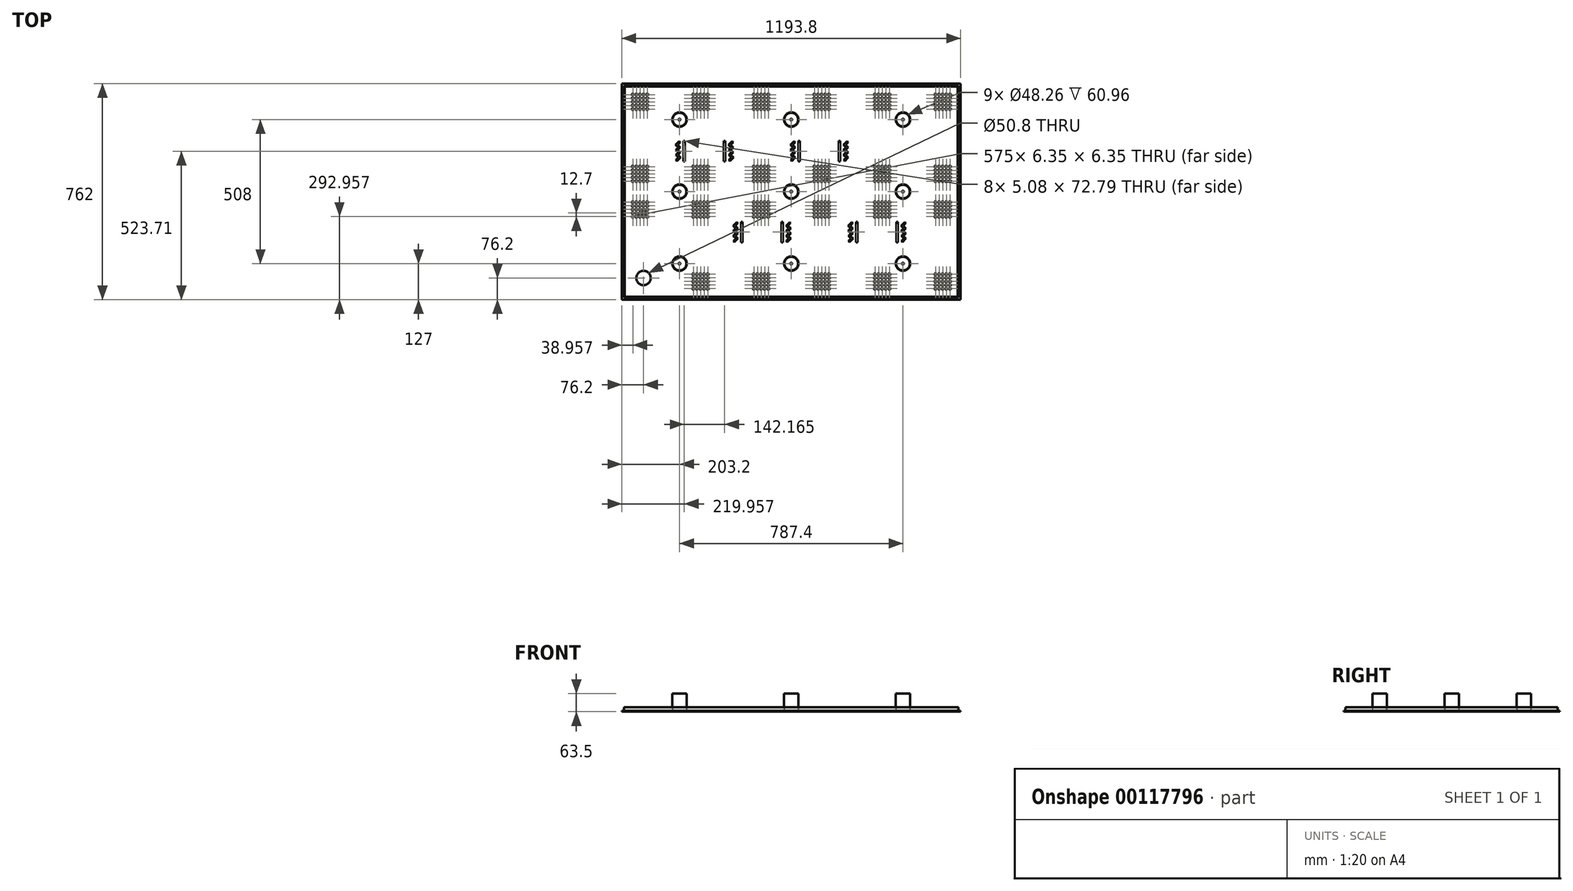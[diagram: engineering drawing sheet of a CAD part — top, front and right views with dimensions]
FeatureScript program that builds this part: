
annotation { "Feature Type Name" : "Feature", "Feature Type Description" : "" }
export const myFeature = defineFeature(function(context is Context, id is Id, definition is map)
    precondition{}
    {
        {
            var Q0;
            Q0=qCreatedBy(makeId("Top.planeOp"),FACE);
            var sketch = newSketch(context, id + "F0", { "sketchPlane" : qUnion([Q0])});
            skLineSegment(sketch, "E0.bottom", {"start": v(596.9, -381) * mm, "end": v(-596.9, -381) * mm});
            skLineSegment(sketch, "E0.top", {"start": v(596.9, 381) * mm, "end": v(-596.9, 381) * mm});
            skLineSegment(sketch, "E0.left", {"start": v(596.9, -381) * mm, "end": v(596.9, 381) * mm});
            skLineSegment(sketch, "E0.right", {"start": v(-596.9, -381) * mm, "end": v(-596.9, 381) * mm});
            skPoint(sketch, "E0.middle", {"position": v(0, 0) * mm});
            skSolve(sketch);
        }
        {
            var Q0;
            Q0=makeQuery(id+"F0.imprint","IMPRINT",FACE,{"disambiguationData":[TD([[makeQuery(id+"F0.imprint","IMPRINT",EDGE,{"derivedFrom":sQuery(id+"F0.wireOp",EDGE,"E0.bottom")}),-1.0]])]});
            extrude(context, id + "F1", {"entities" : qUnion([Q0]), "oppositeDirection" : true, "depth" : 2.54 * mm});
        }
        {
            var Q0;
            Q0=qCreatedBy(makeId("Top.planeOp"),FACE);
            var sketch = newSketch(context, id + "F2", { "sketchPlane" : qUnion([Q0])});
            skLineSegment(sketch, "E1.bottom", {"start": v(596.9, -381) * mm, "end": v(-596.9, -381) * mm});
            skLineSegment(sketch, "E1.top", {"start": v(596.9, 381) * mm, "end": v(-596.9, 381) * mm});
            skLineSegment(sketch, "E1.left", {"start": v(596.9, -381) * mm, "end": v(596.9, 381) * mm});
            skLineSegment(sketch, "E1.right", {"start": v(-596.9, -381) * mm, "end": v(-596.9, 381) * mm});
            skPoint(sketch, "E1.middle", {"position": v(0, 0) * mm});
            skLineSegment(sketch, "E2", {"start": v(-407.26, 165.03) * mm, "end": v(-398.13, 156.2) * mm});
            skLineSegment(sketch, "E3", {"start": v(-398.13, 156.2) * mm, "end": v(-406.97, 147.07) * mm});
            skLineSegment(sketch, "E4", {"start": v(-406.97, 147.07) * mm, "end": v(-397.85, 138.23) * mm});
            skLineSegment(sketch, "E5", {"start": v(-397.85, 138.23) * mm, "end": v(-406.69, 129.11) * mm});
            skLineSegment(sketch, "E6", {"start": v(-406.69, 129.11) * mm, "end": v(-397.56, 120.28) * mm});
            skLineSegment(sketch, "E7", {"start": v(-397.56, 120.28) * mm, "end": v(-406.4, 111.15) * mm});
            skLineSegment(sketch, "E8", {"start": v(-407.26, 165.03) * mm, "end": v(-394.88, 177.8) * mm});
            skLineSegment(sketch, "E9.0", {"start": v(-400.07, 165.14) * mm, "end": v(-391.24, 174.27) * mm});
            skLineSegment(sketch, "E9.1", {"start": v(-400.07, 165.14) * mm, "end": v(-390.95, 156.3) * mm});
            skLineSegment(sketch, "E9.2", {"start": v(-390.95, 156.3) * mm, "end": v(-399.79, 147.19) * mm});
            skLineSegment(sketch, "E9.3", {"start": v(-390.38, 120.4) * mm, "end": v(-402.75, 107.62) * mm});
            skLineSegment(sketch, "E9.4", {"start": v(-399.5, 129.23) * mm, "end": v(-390.38, 120.4) * mm});
            skLineSegment(sketch, "E9.5", {"start": v(-390.67, 138.35) * mm, "end": v(-399.5, 129.23) * mm});
            skLineSegment(sketch, "E9.6", {"start": v(-399.79, 147.19) * mm, "end": v(-390.67, 138.35) * mm});
            skLineSegment(sketch, "E10", {"start": v(-394.88, 177.8) * mm, "end": v(-391.24, 174.27) * mm});
            skLineSegment(sketch, "E11", {"start": v(-406.4, 111.15) * mm, "end": v(-402.75, 107.62) * mm});
            skLineSegment(sketch, "E12.bottom", {"start": v(-382.06, 177.8) * mm, "end": v(-229.66, 177.8) * mm});
            skLineSegment(sketch, "E12.top", {"start": v(-382.06, 107.62) * mm, "end": v(-229.66, 107.62) * mm});
            skLineSegment(sketch, "E12.left", {"start": v(-382.06, 177.8) * mm, "end": v(-382.06, 107.62) * mm});
            skLineSegment(sketch, "E12.right", {"start": v(-229.66, 177.8) * mm, "end": v(-229.66, 107.62) * mm});
            skLineSegment(sketch, "E13", {"start": v(-220.77, 165.03) * mm, "end": v(-211.65, 156.2) * mm});
            skLineSegment(sketch, "E14", {"start": v(-211.65, 156.2) * mm, "end": v(-220.49, 147.07) * mm});
            skLineSegment(sketch, "E15", {"start": v(-220.49, 147.07) * mm, "end": v(-211.36, 138.23) * mm});
            skLineSegment(sketch, "E16", {"start": v(-211.36, 138.23) * mm, "end": v(-220.2, 129.11) * mm});
            skLineSegment(sketch, "E17", {"start": v(-220.2, 129.11) * mm, "end": v(-211.08, 120.28) * mm});
            skLineSegment(sketch, "E18", {"start": v(-211.08, 120.28) * mm, "end": v(-219.92, 111.15) * mm});
            skLineSegment(sketch, "E19", {"start": v(-220.77, 165.03) * mm, "end": v(-208.4, 177.8) * mm});
            skLineSegment(sketch, "E20.0", {"start": v(-213.59, 165.14) * mm, "end": v(-204.75, 174.27) * mm});
            skLineSegment(sketch, "E20.1", {"start": v(-213.59, 165.14) * mm, "end": v(-204.47, 156.3) * mm});
            skLineSegment(sketch, "E20.2", {"start": v(-204.47, 156.3) * mm, "end": v(-213.3, 147.19) * mm});
            skLineSegment(sketch, "E20.3", {"start": v(-203.9, 120.4) * mm, "end": v(-216.27, 107.62) * mm});
            skLineSegment(sketch, "E20.4", {"start": v(-213.02, 129.23) * mm, "end": v(-203.9, 120.4) * mm});
            skLineSegment(sketch, "E20.5", {"start": v(-204.18, 138.35) * mm, "end": v(-213.02, 129.23) * mm});
            skLineSegment(sketch, "E20.6", {"start": v(-213.3, 147.19) * mm, "end": v(-204.18, 138.35) * mm});
            skLineSegment(sketch, "E21", {"start": v(-208.4, 177.8) * mm, "end": v(-204.75, 174.27) * mm});
            skLineSegment(sketch, "E22", {"start": v(-219.92, 111.15) * mm, "end": v(-216.27, 107.62) * mm});
            skLineSegment(sketch, "E23", {"start": v(-204.75, -120.4) * mm, "end": v(-195.63, -129.23) * mm});
            skLineSegment(sketch, "E24", {"start": v(-195.63, -129.23) * mm, "end": v(-204.47, -138.35) * mm});
            skLineSegment(sketch, "E25", {"start": v(-204.47, -138.35) * mm, "end": v(-195.34, -147.19) * mm});
            skLineSegment(sketch, "E26", {"start": v(-195.34, -147.19) * mm, "end": v(-204.18, -156.3) * mm});
            skLineSegment(sketch, "E27", {"start": v(-204.18, -156.3) * mm, "end": v(-195.06, -165.14) * mm});
            skLineSegment(sketch, "E28", {"start": v(-195.06, -165.14) * mm, "end": v(-203.9, -174.27) * mm});
            skLineSegment(sketch, "E29", {"start": v(-204.75, -120.4) * mm, "end": v(-192.38, -107.62) * mm});
            skLineSegment(sketch, "E30.0", {"start": v(-197.57, -120.28) * mm, "end": v(-188.73, -111.15) * mm});
            skLineSegment(sketch, "E30.1", {"start": v(-197.57, -120.28) * mm, "end": v(-188.45, -129.11) * mm});
            skLineSegment(sketch, "E30.2", {"start": v(-188.45, -129.11) * mm, "end": v(-197.28, -138.23) * mm});
            skLineSegment(sketch, "E30.3", {"start": v(-187.88, -165.03) * mm, "end": v(-200.25, -177.8) * mm});
            skLineSegment(sketch, "E30.4", {"start": v(-197, -156.2) * mm, "end": v(-187.88, -165.03) * mm});
            skLineSegment(sketch, "E30.5", {"start": v(-188.16, -147.07) * mm, "end": v(-197, -156.2) * mm});
            skLineSegment(sketch, "E30.6", {"start": v(-197.28, -138.23) * mm, "end": v(-188.16, -147.07) * mm});
            skLineSegment(sketch, "E31", {"start": v(-192.38, -107.62) * mm, "end": v(-188.73, -111.15) * mm});
            skLineSegment(sketch, "E32", {"start": v(-203.9, -174.27) * mm, "end": v(-200.25, -177.8) * mm});
            skLineSegment(sketch, "E33.bottom", {"start": v(-179.56, -107.62) * mm, "end": v(-27.16, -107.62) * mm});
            skLineSegment(sketch, "E33.top", {"start": v(-179.56, -177.8) * mm, "end": v(-27.16, -177.8) * mm});
            skLineSegment(sketch, "E33.left", {"start": v(-179.56, -107.62) * mm, "end": v(-179.56, -177.8) * mm});
            skLineSegment(sketch, "E33.right", {"start": v(-27.16, -107.62) * mm, "end": v(-27.16, -177.8) * mm});
            skLineSegment(sketch, "E34", {"start": v(-18.27, -120.4) * mm, "end": v(-9.14, -129.23) * mm});
            skLineSegment(sketch, "E35", {"start": v(-9.14, -129.23) * mm, "end": v(-17.98, -138.35) * mm});
            skLineSegment(sketch, "E36", {"start": v(-17.98, -138.35) * mm, "end": v(-8.86, -147.19) * mm});
            skLineSegment(sketch, "E37", {"start": v(-8.86, -147.19) * mm, "end": v(-17.7, -156.3) * mm});
            skLineSegment(sketch, "E38", {"start": v(-17.7, -156.3) * mm, "end": v(-8.57, -165.14) * mm});
            skLineSegment(sketch, "E39", {"start": v(-8.57, -165.14) * mm, "end": v(-17.41, -174.27) * mm});
            skLineSegment(sketch, "E40", {"start": v(-18.27, -120.4) * mm, "end": v(-5.9, -107.62) * mm});
            skLineSegment(sketch, "E41.0", {"start": v(-11.08, -120.28) * mm, "end": v(-2.25, -111.15) * mm});
            skLineSegment(sketch, "E41.1", {"start": v(-11.08, -120.28) * mm, "end": v(-1.96, -129.11) * mm});
            skLineSegment(sketch, "E41.2", {"start": v(-1.96, -129.11) * mm, "end": v(-10.8, -138.23) * mm});
            skLineSegment(sketch, "E41.3", {"start": v(-1.4, -165.03) * mm, "end": v(-13.76, -177.8) * mm});
            skLineSegment(sketch, "E41.4", {"start": v(-10.51, -156.2) * mm, "end": v(-1.4, -165.03) * mm});
            skLineSegment(sketch, "E41.5", {"start": v(-1.68, -147.07) * mm, "end": v(-10.51, -156.2) * mm});
            skLineSegment(sketch, "E41.6", {"start": v(-10.8, -138.23) * mm, "end": v(-1.68, -147.07) * mm});
            skLineSegment(sketch, "E42", {"start": v(-5.9, -107.62) * mm, "end": v(-2.25, -111.15) * mm});
            skLineSegment(sketch, "E43", {"start": v(-17.41, -174.27) * mm, "end": v(-13.76, -177.8) * mm});
            skLineSegment(sketch, "E44", {"start": v(-2.53, 165.03) * mm, "end": v(6.6, 156.2) * mm});
            skLineSegment(sketch, "E45", {"start": v(6.6, 156.2) * mm, "end": v(-2.25, 147.07) * mm});
            skLineSegment(sketch, "E46", {"start": v(-2.25, 147.07) * mm, "end": v(6.88, 138.23) * mm});
            skLineSegment(sketch, "E47", {"start": v(6.88, 138.23) * mm, "end": v(-1.96, 129.11) * mm});
            skLineSegment(sketch, "E48", {"start": v(-1.96, 129.11) * mm, "end": v(7.16, 120.28) * mm});
            skLineSegment(sketch, "E49", {"start": v(7.16, 120.28) * mm, "end": v(-1.68, 111.15) * mm});
            skLineSegment(sketch, "E50", {"start": v(-2.53, 165.03) * mm, "end": v(9.84, 177.8) * mm});
            skLineSegment(sketch, "E51.0", {"start": v(4.65, 165.14) * mm, "end": v(13.49, 174.27) * mm});
            skLineSegment(sketch, "E51.1", {"start": v(4.65, 165.14) * mm, "end": v(13.77, 156.3) * mm});
            skLineSegment(sketch, "E51.2", {"start": v(13.77, 156.3) * mm, "end": v(4.94, 147.19) * mm});
            skLineSegment(sketch, "E51.3", {"start": v(14.34, 120.4) * mm, "end": v(1.97, 107.62) * mm});
            skLineSegment(sketch, "E51.4", {"start": v(5.22, 129.23) * mm, "end": v(14.34, 120.4) * mm});
            skLineSegment(sketch, "E51.5", {"start": v(14.06, 138.35) * mm, "end": v(5.22, 129.23) * mm});
            skLineSegment(sketch, "E51.6", {"start": v(4.94, 147.19) * mm, "end": v(14.06, 138.35) * mm});
            skLineSegment(sketch, "E52", {"start": v(9.84, 177.8) * mm, "end": v(13.49, 174.27) * mm});
            skLineSegment(sketch, "E53", {"start": v(-1.68, 111.15) * mm, "end": v(1.97, 107.62) * mm});
            skLineSegment(sketch, "E54.bottom", {"start": v(22.66, 177.8) * mm, "end": v(175.06, 177.8) * mm});
            skLineSegment(sketch, "E54.top", {"start": v(22.66, 107.62) * mm, "end": v(175.06, 107.62) * mm});
            skLineSegment(sketch, "E54.left", {"start": v(22.66, 177.8) * mm, "end": v(22.66, 107.62) * mm});
            skLineSegment(sketch, "E54.right", {"start": v(175.06, 177.8) * mm, "end": v(175.06, 107.62) * mm});
            skLineSegment(sketch, "E55", {"start": v(183.95, 165.03) * mm, "end": v(193.08, 156.2) * mm});
            skLineSegment(sketch, "E56", {"start": v(193.08, 156.2) * mm, "end": v(184.24, 147.07) * mm});
            skLineSegment(sketch, "E57", {"start": v(184.24, 147.07) * mm, "end": v(193.36, 138.23) * mm});
            skLineSegment(sketch, "E58", {"start": v(193.36, 138.23) * mm, "end": v(184.52, 129.11) * mm});
            skLineSegment(sketch, "E59", {"start": v(184.52, 129.11) * mm, "end": v(193.65, 120.28) * mm});
            skLineSegment(sketch, "E60", {"start": v(193.65, 120.28) * mm, "end": v(184.8, 111.15) * mm});
            skLineSegment(sketch, "E61", {"start": v(183.95, 165.03) * mm, "end": v(196.33, 177.8) * mm});
            skLineSegment(sketch, "E62.0", {"start": v(191.14, 165.14) * mm, "end": v(199.97, 174.27) * mm});
            skLineSegment(sketch, "E62.1", {"start": v(191.14, 165.14) * mm, "end": v(200.26, 156.3) * mm});
            skLineSegment(sketch, "E62.2", {"start": v(200.26, 156.3) * mm, "end": v(191.42, 147.19) * mm});
            skLineSegment(sketch, "E62.3", {"start": v(200.83, 120.4) * mm, "end": v(188.46, 107.62) * mm});
            skLineSegment(sketch, "E62.4", {"start": v(191.7, 129.23) * mm, "end": v(200.83, 120.4) * mm});
            skLineSegment(sketch, "E62.5", {"start": v(200.54, 138.35) * mm, "end": v(191.7, 129.23) * mm});
            skLineSegment(sketch, "E62.6", {"start": v(191.42, 147.19) * mm, "end": v(200.54, 138.35) * mm});
            skLineSegment(sketch, "E63", {"start": v(196.33, 177.8) * mm, "end": v(199.97, 174.27) * mm});
            skLineSegment(sketch, "E64", {"start": v(184.8, 111.15) * mm, "end": v(188.46, 107.62) * mm});
            skLineSegment(sketch, "E65", {"start": v(200.83, -120.4) * mm, "end": v(209.95, -129.23) * mm});
            skLineSegment(sketch, "E66", {"start": v(209.95, -129.23) * mm, "end": v(201.11, -138.35) * mm});
            skLineSegment(sketch, "E67", {"start": v(201.11, -138.35) * mm, "end": v(210.24, -147.19) * mm});
            skLineSegment(sketch, "E68", {"start": v(210.24, -147.19) * mm, "end": v(201.4, -156.3) * mm});
            skLineSegment(sketch, "E69", {"start": v(201.4, -156.3) * mm, "end": v(210.52, -165.14) * mm});
            skLineSegment(sketch, "E70", {"start": v(210.52, -165.14) * mm, "end": v(201.68, -174.27) * mm});
            skLineSegment(sketch, "E71", {"start": v(200.83, -120.4) * mm, "end": v(213.2, -107.62) * mm});
            skLineSegment(sketch, "E72.0", {"start": v(208.01, -120.28) * mm, "end": v(216.85, -111.15) * mm});
            skLineSegment(sketch, "E72.1", {"start": v(208.01, -120.28) * mm, "end": v(217.13, -129.11) * mm});
            skLineSegment(sketch, "E72.2", {"start": v(217.13, -129.11) * mm, "end": v(208.3, -138.23) * mm});
            skLineSegment(sketch, "E72.3", {"start": v(217.7, -165.03) * mm, "end": v(205.33, -177.8) * mm});
            skLineSegment(sketch, "E72.4", {"start": v(208.58, -156.2) * mm, "end": v(217.7, -165.03) * mm});
            skLineSegment(sketch, "E72.5", {"start": v(217.42, -147.07) * mm, "end": v(208.58, -156.2) * mm});
            skLineSegment(sketch, "E72.6", {"start": v(208.3, -138.23) * mm, "end": v(217.42, -147.07) * mm});
            skLineSegment(sketch, "E73", {"start": v(213.2, -107.62) * mm, "end": v(216.85, -111.15) * mm});
            skLineSegment(sketch, "E74", {"start": v(201.68, -174.27) * mm, "end": v(205.33, -177.8) * mm});
            skLineSegment(sketch, "E75.bottom", {"start": v(226.02, -107.62) * mm, "end": v(378.42, -107.62) * mm});
            skLineSegment(sketch, "E75.top", {"start": v(226.02, -177.8) * mm, "end": v(378.42, -177.8) * mm});
            skLineSegment(sketch, "E75.left", {"start": v(226.02, -107.62) * mm, "end": v(226.02, -177.8) * mm});
            skLineSegment(sketch, "E75.right", {"start": v(378.42, -107.62) * mm, "end": v(378.42, -177.8) * mm});
            skLineSegment(sketch, "E76", {"start": v(387.31, -120.4) * mm, "end": v(396.44, -129.23) * mm});
            skLineSegment(sketch, "E77", {"start": v(396.44, -129.23) * mm, "end": v(387.6, -138.35) * mm});
            skLineSegment(sketch, "E78", {"start": v(387.6, -138.35) * mm, "end": v(396.72, -147.19) * mm});
            skLineSegment(sketch, "E79", {"start": v(396.72, -147.19) * mm, "end": v(387.88, -156.3) * mm});
            skLineSegment(sketch, "E80", {"start": v(387.88, -156.3) * mm, "end": v(397, -165.14) * mm});
            skLineSegment(sketch, "E81", {"start": v(397, -165.14) * mm, "end": v(388.17, -174.27) * mm});
            skLineSegment(sketch, "E82", {"start": v(387.31, -120.4) * mm, "end": v(399.69, -107.62) * mm});
            skLineSegment(sketch, "E83.0", {"start": v(394.5, -120.28) * mm, "end": v(403.33, -111.15) * mm});
            skLineSegment(sketch, "E83.1", {"start": v(394.5, -120.28) * mm, "end": v(403.62, -129.11) * mm});
            skLineSegment(sketch, "E83.2", {"start": v(403.62, -129.11) * mm, "end": v(394.78, -138.23) * mm});
            skLineSegment(sketch, "E83.3", {"start": v(404.19, -165.03) * mm, "end": v(391.82, -177.8) * mm});
            skLineSegment(sketch, "E83.4", {"start": v(395.07, -156.2) * mm, "end": v(404.19, -165.03) * mm});
            skLineSegment(sketch, "E83.5", {"start": v(403.9, -147.07) * mm, "end": v(395.07, -156.2) * mm});
            skLineSegment(sketch, "E83.6", {"start": v(394.78, -138.23) * mm, "end": v(403.9, -147.07) * mm});
            skLineSegment(sketch, "E84", {"start": v(399.69, -107.62) * mm, "end": v(403.33, -111.15) * mm});
            skLineSegment(sketch, "E85", {"start": v(388.17, -174.27) * mm, "end": v(391.82, -177.8) * mm});
            skSolve(sketch);
        }
        {
            var Q0;
            Q0=makeQuery(id+"F2.imprint","IMPRINT",FACE,{"disambiguationData":[TD([[makeQuery(id+"F2.imprint","IMPRINT",EDGE,{"derivedFrom":sQuery(id+"F2.wireOp",EDGE,"E2")}),1.0]])]});
            var Q1;
            Q1=makeQuery(id+"F2.imprint","IMPRINT",FACE,{"disambiguationData":[TD([[makeQuery(id+"F2.imprint","IMPRINT",EDGE,{"derivedFrom":sQuery(id+"F2.wireOp",EDGE,"E13")}),1.0]])]});
            var Q2;
            Q2=makeQuery(id+"F2.imprint","IMPRINT",FACE,{"disambiguationData":[TD([[makeQuery(id+"F2.imprint","IMPRINT",EDGE,{"derivedFrom":sQuery(id+"F2.wireOp",EDGE,"E23")}),1.0]])]});
            var Q3;
            Q3=makeQuery(id+"F2.imprint","IMPRINT",FACE,{"disambiguationData":[TD([[makeQuery(id+"F2.imprint","IMPRINT",EDGE,{"derivedFrom":sQuery(id+"F2.wireOp",EDGE,"E34")}),1.0]])]});
            var Q4;
            Q4=makeQuery(id+"F2.imprint","IMPRINT",FACE,{"disambiguationData":[TD([[makeQuery(id+"F2.imprint","IMPRINT",EDGE,{"derivedFrom":sQuery(id+"F2.wireOp",EDGE,"E76")}),1.0]])]});
            var Q5;
            Q5=makeQuery(id+"F2.imprint","IMPRINT",FACE,{"disambiguationData":[TD([[makeQuery(id+"F2.imprint","IMPRINT",EDGE,{"derivedFrom":sQuery(id+"F2.wireOp",EDGE,"E65")}),1.0]])]});
            var Q6;
            Q6=makeQuery(id+"F2.imprint","IMPRINT",FACE,{"disambiguationData":[TD([[makeQuery(id+"F2.imprint","IMPRINT",EDGE,{"derivedFrom":sQuery(id+"F2.wireOp",EDGE,"E44")}),1.0]])]});
            var Q7;
            Q7=makeQuery(id+"F2.imprint","IMPRINT",FACE,{"disambiguationData":[TD([[makeQuery(id+"F2.imprint","IMPRINT",EDGE,{"derivedFrom":sQuery(id+"F2.wireOp",EDGE,"E55")}),1.0]])]});
            extrude(context, id + "F3", {"entities" : qUnion([Q0, Q1, Q2, Q3, Q4, Q5, Q6, Q7]), "operationType" : NewBodyOperationType.REMOVE, "endBound" : BoundingType.THROUGH_ALL, "oppositeDirection" : true, "depth" : 25.4 * mm, "hasDraft" : true, "draftAngle" : 20 * degree});
        }
        {
            var Q0;
            Q0=makeQuery(id+"F1.opExtrude","CAP_FACE",FACE,{"disambiguationData":[OSD([sQuery(id+"F0.wireOp",EDGE,"E0.bottom"),sQuery(id+"F0.wireOp",EDGE,"E0.top"),sQuery(id+"F0.wireOp",EDGE,"E0.left"),sQuery(id+"F0.wireOp",EDGE,"E0.right")])],"isStart":false});
            var sketch = newSketch(context, id + "F4", { "sketchPlane" : qUnion([Q0])});
            skLineSegment(sketch, "E86.left", {"start": v(-176.7, 179.1) * mm, "end": v(-176.7, 106.31) * mm});
            skLineSegment(sketch, "E86.right", {"start": v(-29.73, 179.1) * mm, "end": v(-29.73, 106.31) * mm});
            skLineSegment(sketch, "E87.left", {"start": v(228.6, 179.1) * mm, "end": v(228.6, 106.31) * mm});
            skLineSegment(sketch, "E87.right", {"start": v(375.85, 179.1) * mm, "end": v(375.85, 106.31) * mm});
            skLineSegment(sketch, "E88.left", {"start": v(-379.48, -106.31) * mm, "end": v(-379.48, -179.1) * mm});
            skLineSegment(sketch, "E88.right", {"start": v(-232.24, -106.31) * mm, "end": v(-232.24, -179.1) * mm});
            skLineSegment(sketch, "E89.left", {"start": v(25.24, -106.31) * mm, "end": v(25.24, -179.1) * mm});
            skLineSegment(sketch, "E89.right", {"start": v(172.49, -106.31) * mm, "end": v(172.49, -179.1) * mm});
            skLineSegment(sketch, "E90", {"start": v(-379.48, -106.31) * mm, "end": v(-374.4, -106.31) * mm});
            skLineSegment(sketch, "E91", {"start": v(-374.4, -106.31) * mm, "end": v(-374.4, -179.1) * mm});
            skLineSegment(sketch, "E92", {"start": v(-374.4, -179.1) * mm, "end": v(-379.48, -179.1) * mm});
            skLineSegment(sketch, "E93", {"start": v(-232.24, -106.31) * mm, "end": v(-237.32, -106.31) * mm});
            skLineSegment(sketch, "E94", {"start": v(-237.32, -106.31) * mm, "end": v(-237.32, -179.1) * mm});
            skLineSegment(sketch, "E95", {"start": v(-237.32, -179.1) * mm, "end": v(-232.24, -179.1) * mm});
            skLineSegment(sketch, "E96", {"start": v(-176.7, 179.1) * mm, "end": v(-171.61, 179.1) * mm});
            skLineSegment(sketch, "E97", {"start": v(-171.61, 179.1) * mm, "end": v(-171.61, 106.31) * mm});
            skLineSegment(sketch, "E98", {"start": v(-171.61, 106.31) * mm, "end": v(-176.7, 106.31) * mm});
            skLineSegment(sketch, "E99", {"start": v(-29.73, 179.1) * mm, "end": v(-34.81, 179.1) * mm});
            skLineSegment(sketch, "E100", {"start": v(-34.81, 179.1) * mm, "end": v(-34.81, 106.31) * mm});
            skLineSegment(sketch, "E101", {"start": v(-34.81, 106.31) * mm, "end": v(-29.73, 106.31) * mm});
            skLineSegment(sketch, "E102", {"start": v(25.24, -106.31) * mm, "end": v(30.32, -106.31) * mm});
            skLineSegment(sketch, "E103", {"start": v(30.32, -106.31) * mm, "end": v(30.32, -179.1) * mm});
            skLineSegment(sketch, "E104", {"start": v(30.32, -179.1) * mm, "end": v(25.24, -179.1) * mm});
            skLineSegment(sketch, "E105", {"start": v(172.49, -106.31) * mm, "end": v(167.4, -106.31) * mm});
            skLineSegment(sketch, "E106", {"start": v(167.4, -106.31) * mm, "end": v(167.4, -179.1) * mm});
            skLineSegment(sketch, "E107", {"start": v(167.4, -179.1) * mm, "end": v(172.49, -179.1) * mm});
            skLineSegment(sketch, "E108", {"start": v(228.6, 179.1) * mm, "end": v(233.68, 179.1) * mm});
            skLineSegment(sketch, "E109", {"start": v(233.68, 179.1) * mm, "end": v(233.68, 106.31) * mm});
            skLineSegment(sketch, "E110", {"start": v(233.68, 106.31) * mm, "end": v(228.6, 106.31) * mm});
            skLineSegment(sketch, "E111", {"start": v(375.85, 179.1) * mm, "end": v(370.77, 179.1) * mm});
            skLineSegment(sketch, "E112", {"start": v(370.77, 179.1) * mm, "end": v(370.77, 106.31) * mm});
            skLineSegment(sketch, "E113", {"start": v(370.77, 106.31) * mm, "end": v(375.85, 106.31) * mm});
            skSolve(sketch);
        }
        {
            var Q0;
            Q0=makeQuery(id+"F1.opExtrude","CAP_FACE",FACE,{"disambiguationData":[OSD([sQuery(id+"F0.wireOp",EDGE,"E0.bottom"),sQuery(id+"F0.wireOp",EDGE,"E0.top"),sQuery(id+"F0.wireOp",EDGE,"E0.left"),sQuery(id+"F0.wireOp",EDGE,"E0.right")])],"isStart":true});
            var sketch = newSketch(context, id + "F5", { "sketchPlane" : qUnion([Q0])});
            skLineSegment(sketch, "E114.bottom", {"start": v(589.28, -373.38) * mm, "end": v(-589.28, -373.38) * mm});
            skLineSegment(sketch, "E114.top", {"start": v(589.28, 373.38) * mm, "end": v(-589.28, 373.38) * mm});
            skLineSegment(sketch, "E114.left", {"start": v(589.28, -373.38) * mm, "end": v(589.28, 373.38) * mm});
            skLineSegment(sketch, "E114.right", {"start": v(-589.28, -373.38) * mm, "end": v(-589.28, 373.38) * mm});
            skPoint(sketch, "E114.middle", {"position": v(0, 0) * mm});
            skLineSegment(sketch, "E115.0", {"start": v(586.74, 370.84) * mm, "end": v(-586.74, 370.84) * mm});
            skLineSegment(sketch, "E115.1", {"start": v(586.74, -370.84) * mm, "end": v(586.74, 370.84) * mm});
            skLineSegment(sketch, "E115.2", {"start": v(586.74, -370.84) * mm, "end": v(-586.74, -370.84) * mm});
            skLineSegment(sketch, "E115.3", {"start": v(-586.74, -370.84) * mm, "end": v(-586.74, 370.84) * mm});
            skSolve(sketch);
        }
        {
            var Q0;
            Q0=makeQuery(id+"F5.imprint","IMPRINT",FACE,{"disambiguationData":[TD([[makeQuery(id+"F5.imprint","IMPRINT",EDGE,{"derivedFrom":sQuery(id+"F5.wireOp",EDGE,"E114.bottom")}),-1.0]])]});
            extrude(context, id + "F6", {"entities" : qUnion([Q0]), "operationType" : NewBodyOperationType.ADD, "depth" : 12.7 * mm, "hasDraft" : true, "draftAngle" : 1 * degree});
        }
        {
            var Q0;
            Q0=makeQuery(id+"F6.boolean.opBoolean","SPLIT",FACE,{"disambiguationData":[TD([makeQuery(id+"F3.boolean.opBoolean","COPY",FACE,{"derivedFrom":makeQuery(id+"F3.opExtrude","SWEPT_FACE",FACE,{"disambiguationData":[OSD([sQuery(id+"F2.wireOp",EDGE,"E2")])]})})])],"derivedFrom":makeQuery(id+"F1.opExtrude","CAP_FACE",FACE,{"disambiguationData":[OSD([sQuery(id+"F0.wireOp",EDGE,"E0.bottom"),sQuery(id+"F0.wireOp",EDGE,"E0.top"),sQuery(id+"F0.wireOp",EDGE,"E0.left"),sQuery(id+"F0.wireOp",EDGE,"E0.right")])],"isStart":true})});
            var sketch = newSketch(context, id + "F7", { "sketchPlane" : qUnion([Q0])});
            skCircle(sketch, "E116", {"center": v(-393.7, 254) * mm, "radius": 25.4 * mm});
            skCircle(sketch, "E117", {"center": v(-393.7, 0) * mm, "radius": 25.4 * mm});
            skCircle(sketch, "E118", {"center": v(-393.7, -254) * mm, "radius": 25.4 * mm});
            skCircle(sketch, "E119", {"center": v(0, 254) * mm, "radius": 25.4 * mm});
            skCircle(sketch, "E120", {"center": v(393.7, 254) * mm, "radius": 25.4 * mm});
            skCircle(sketch, "E121", {"center": v(0, 0) * mm, "radius": 25.4 * mm});
            skCircle(sketch, "E122", {"center": v(0, -254) * mm, "radius": 25.4 * mm});
            skCircle(sketch, "E123", {"center": v(393.7, 0) * mm, "radius": 25.4 * mm});
            skCircle(sketch, "E124", {"center": v(393.7, -254) * mm, "radius": 25.4 * mm});
            skCircle(sketch, "E125", {"center": v(-393.7, 254) * mm, "radius": 24.13 * mm});
            skCircle(sketch, "E126", {"center": v(0, 254) * mm, "radius": 24.13 * mm});
            skCircle(sketch, "E127", {"center": v(393.7, 254) * mm, "radius": 24.13 * mm});
            skCircle(sketch, "E128", {"center": v(-393.7, 0) * mm, "radius": 24.13 * mm});
            skCircle(sketch, "E129", {"center": v(0, 0) * mm, "radius": 24.13 * mm});
            skCircle(sketch, "E130", {"center": v(393.7, 0) * mm, "radius": 24.13 * mm});
            skCircle(sketch, "E131", {"center": v(0, -254) * mm, "radius": 24.13 * mm});
            skCircle(sketch, "E132", {"center": v(393.7, -254) * mm, "radius": 24.13 * mm});
            skCircle(sketch, "E133", {"center": v(-393.7, -254) * mm, "radius": 24.13 * mm});
            skCircle(sketch, "E134", {"center": v(-393.7, 254) * mm, "radius": 3.18 * mm});
            skCircle(sketch, "E135", {"center": v(0, 254) * mm, "radius": 3.18 * mm});
            skCircle(sketch, "E136", {"center": v(393.7, 254) * mm, "radius": 3.18 * mm});
            skCircle(sketch, "E137", {"center": v(-393.7, 0) * mm, "radius": 3.18 * mm});
            skCircle(sketch, "E138", {"center": v(0, 0) * mm, "radius": 3.18 * mm});
            skCircle(sketch, "E139", {"center": v(393.7, 0) * mm, "radius": 3.18 * mm});
            skCircle(sketch, "E140", {"center": v(393.7, -254) * mm, "radius": 3.18 * mm});
            skCircle(sketch, "E141", {"center": v(0, -254) * mm, "radius": 3.18 * mm});
            skCircle(sketch, "E142", {"center": v(-393.7, -254) * mm, "radius": 3.18 * mm});
            skSolve(sketch);
        }
        {
            var Q0;
            Q0=makeQuery(id+"F7.imprint","IMPRINT",FACE,{"disambiguationData":[TD([[makeQuery(id+"F7.imprint","IMPRINT",EDGE,{"derivedFrom":sQuery(id+"F7.wireOp",EDGE,"E116")}),1.0]])]});
            var Q1;
            Q1=makeQuery(id+"F7.imprint","IMPRINT",FACE,{"disambiguationData":[TD([[makeQuery(id+"F7.imprint","IMPRINT",EDGE,{"derivedFrom":sQuery(id+"F7.wireOp",EDGE,"E119")}),1.0]])]});
            var Q2;
            Q2=makeQuery(id+"F7.imprint","IMPRINT",FACE,{"disambiguationData":[TD([[makeQuery(id+"F7.imprint","IMPRINT",EDGE,{"derivedFrom":sQuery(id+"F7.wireOp",EDGE,"E120")}),1.0]])]});
            var Q3;
            Q3=makeQuery(id+"F7.imprint","IMPRINT",FACE,{"disambiguationData":[TD([[makeQuery(id+"F7.imprint","IMPRINT",EDGE,{"derivedFrom":sQuery(id+"F7.wireOp",EDGE,"E123")}),1.0]])]});
            var Q4;
            Q4=makeQuery(id+"F7.imprint","IMPRINT",FACE,{"disambiguationData":[TD([[makeQuery(id+"F7.imprint","IMPRINT",EDGE,{"derivedFrom":sQuery(id+"F7.wireOp",EDGE,"E121")}),1.0]])]});
            var Q5;
            Q5=makeQuery(id+"F7.imprint","IMPRINT",FACE,{"disambiguationData":[TD([[makeQuery(id+"F7.imprint","IMPRINT",EDGE,{"derivedFrom":sQuery(id+"F7.wireOp",EDGE,"E117")}),1.0]])]});
            var Q6;
            Q6=makeQuery(id+"F7.imprint","IMPRINT",FACE,{"disambiguationData":[TD([[makeQuery(id+"F7.imprint","IMPRINT",EDGE,{"derivedFrom":sQuery(id+"F7.wireOp",EDGE,"E118")}),1.0]])]});
            var Q7;
            Q7=makeQuery(id+"F7.imprint","IMPRINT",FACE,{"disambiguationData":[TD([[makeQuery(id+"F7.imprint","IMPRINT",EDGE,{"derivedFrom":sQuery(id+"F7.wireOp",EDGE,"E122")}),1.0]])]});
            var Q8;
            Q8=makeQuery(id+"F7.imprint","IMPRINT",FACE,{"disambiguationData":[TD([[makeQuery(id+"F7.imprint","IMPRINT",EDGE,{"derivedFrom":sQuery(id+"F7.wireOp",EDGE,"E124")}),1.0]])]});
            extrude(context, id + "F8", {"entities" : qUnion([Q0, Q1, Q2, Q3, Q4, Q5, Q6, Q7, Q8]), "operationType" : NewBodyOperationType.ADD, "depth" : 60.96 * mm});
        }
        {
            var Q0;
            Q0=makeQuery(id+"F1.opExtrude","CAP_FACE",FACE,{"disambiguationData":[OSD([sQuery(id+"F0.wireOp",EDGE,"E0.bottom"),sQuery(id+"F0.wireOp",EDGE,"E0.top"),sQuery(id+"F0.wireOp",EDGE,"E0.left"),sQuery(id+"F0.wireOp",EDGE,"E0.right")])],"isStart":false});
            var sketch = newSketch(context, id + "F9", { "sketchPlane" : qUnion([Q0])});
            skCircle(sketch, "E143", {"center": v(-520.7, 304.8) * mm, "radius": 25.4 * mm});
            skSolve(sketch);
        }
        {
            var Q0;
            Q0=makeQuery(id+"F9.imprint","IMPRINT",FACE,{"disambiguationData":[TD([[makeQuery(id+"F9.imprint","IMPRINT",EDGE,{"derivedFrom":sQuery(id+"F9.wireOp",EDGE,"E143")}),1.0]])]});
            extrude(context, id + "F10", {"entities" : qUnion([Q0]), "operationType" : NewBodyOperationType.REMOVE, "endBound" : BoundingType.THROUGH_ALL, "oppositeDirection" : true, "depth" : 25.4 * mm});
        }
        {
            var Q0;
            Q0=makeQuery(id+"F7.imprint","IMPRINT",FACE,{"disambiguationData":[TD([[makeQuery(id+"F7.imprint","IMPRINT",EDGE,{"derivedFrom":sQuery(id+"F7.wireOp",EDGE,"E134")}),1.0]])]});
            var Q1;
            Q1=makeQuery(id+"F7.imprint","IMPRINT",FACE,{"disambiguationData":[TD([[makeQuery(id+"F7.imprint","IMPRINT",EDGE,{"derivedFrom":sQuery(id+"F7.wireOp",EDGE,"E135")}),1.0]])]});
            var Q2;
            Q2=makeQuery(id+"F7.imprint","IMPRINT",FACE,{"disambiguationData":[TD([[makeQuery(id+"F7.imprint","IMPRINT",EDGE,{"derivedFrom":sQuery(id+"F7.wireOp",EDGE,"E136")}),1.0]])]});
            var Q3;
            Q3=makeQuery(id+"F7.imprint","IMPRINT",FACE,{"disambiguationData":[TD([[makeQuery(id+"F7.imprint","IMPRINT",EDGE,{"derivedFrom":sQuery(id+"F7.wireOp",EDGE,"E139")}),1.0]])]});
            var Q4;
            Q4=makeQuery(id+"F7.imprint","IMPRINT",FACE,{"disambiguationData":[TD([[makeQuery(id+"F7.imprint","IMPRINT",EDGE,{"derivedFrom":sQuery(id+"F7.wireOp",EDGE,"E138")}),1.0]])]});
            var Q5;
            Q5=makeQuery(id+"F7.imprint","IMPRINT",FACE,{"disambiguationData":[TD([[makeQuery(id+"F7.imprint","IMPRINT",EDGE,{"derivedFrom":sQuery(id+"F7.wireOp",EDGE,"E137")}),1.0]])]});
            var Q6;
            Q6=makeQuery(id+"F7.imprint","IMPRINT",FACE,{"disambiguationData":[TD([[makeQuery(id+"F7.imprint","IMPRINT",EDGE,{"derivedFrom":sQuery(id+"F7.wireOp",EDGE,"E142")}),1.0]])]});
            var Q7;
            Q7=makeQuery(id+"F7.imprint","IMPRINT",FACE,{"disambiguationData":[TD([[makeQuery(id+"F7.imprint","IMPRINT",EDGE,{"derivedFrom":sQuery(id+"F7.wireOp",EDGE,"E141")}),1.0]])]});
            var Q8;
            Q8=makeQuery(id+"F7.imprint","IMPRINT",FACE,{"disambiguationData":[TD([[makeQuery(id+"F7.imprint","IMPRINT",EDGE,{"derivedFrom":sQuery(id+"F7.wireOp",EDGE,"E140")}),1.0]])]});
            extrude(context, id + "F11", {"entities" : qUnion([Q0, Q1, Q2, Q3, Q4, Q5, Q6, Q7, Q8]), "operationType" : NewBodyOperationType.REMOVE, "endBound" : BoundingType.THROUGH_ALL, "oppositeDirection" : true, "depth" : 25.4 * mm, "hasDraft" : true, "draftAngle" : 3 * degree});
        }
        {
            var Q0;
            {var subQ75=makeQuery(id+"F3.boolean.opBoolean","COPY",FACE,{"derivedFrom":makeQuery(id+"F3.opExtrude","SWEPT_FACE",FACE,{"disambiguationData":[OSD([sQuery(id+"F2.wireOp",EDGE,"E2")])]})});Q0=makeQuery(id+"F8.boolean.opBoolean","SPLIT",FACE,{"disambiguationData":[TD([subQ75])],"derivedFrom":makeQuery(id+"F6.boolean.opBoolean","SPLIT",FACE,{"disambiguationData":[TD([subQ75])],"derivedFrom":makeQuery(id+"F1.opExtrude","CAP_FACE",FACE,{"disambiguationData":[OSD([sQuery(id+"F0.wireOp",EDGE,"E0.bottom"),sQuery(id+"F0.wireOp",EDGE,"E0.top"),sQuery(id+"F0.wireOp",EDGE,"E0.left"),sQuery(id+"F0.wireOp",EDGE,"E0.right")])],"isStart":true})})});}
            var sketch = newSketch(context, id + "F12", { "sketchPlane" : qUnion([Q0])});
            skLineSegment(sketch, "E144.bottom", {"start": v(-561.12, 345.22) * mm, "end": v(-554.77, 345.22) * mm});
            skLineSegment(sketch, "E144.top", {"start": v(-561.12, 338.87) * mm, "end": v(-554.77, 338.87) * mm});
            skLineSegment(sketch, "E144.left", {"start": v(-561.12, 345.22) * mm, "end": v(-561.12, 338.87) * mm});
            skLineSegment(sketch, "E144.right", {"start": v(-554.77, 345.22) * mm, "end": v(-554.77, 338.87) * mm});
            skLineSegment(sketch, "E145.0.1.0", {"start": v(-554.77, 332.52) * mm, "end": v(-554.77, 326.17) * mm});
            skLineSegment(sketch, "E145.0.1.1", {"start": v(-561.12, 326.17) * mm, "end": v(-554.77, 326.17) * mm});
            skLineSegment(sketch, "E145.0.1.2", {"start": v(-561.12, 332.52) * mm, "end": v(-561.12, 326.17) * mm});
            skLineSegment(sketch, "E145.0.1.3", {"start": v(-561.12, 332.52) * mm, "end": v(-554.77, 332.52) * mm});
            skLineSegment(sketch, "E145.0.2.0", {"start": v(-554.77, 319.82) * mm, "end": v(-554.77, 313.47) * mm});
            skLineSegment(sketch, "E145.0.2.1", {"start": v(-561.12, 313.47) * mm, "end": v(-554.77, 313.47) * mm});
            skLineSegment(sketch, "E145.0.2.2", {"start": v(-561.12, 319.82) * mm, "end": v(-561.12, 313.47) * mm});
            skLineSegment(sketch, "E145.0.2.3", {"start": v(-561.12, 319.82) * mm, "end": v(-554.77, 319.82) * mm});
            skLineSegment(sketch, "E145.0.3.0", {"start": v(-554.77, 307.12) * mm, "end": v(-554.77, 300.77) * mm});
            skLineSegment(sketch, "E145.0.3.1", {"start": v(-561.12, 300.77) * mm, "end": v(-554.77, 300.77) * mm});
            skLineSegment(sketch, "E145.0.3.2", {"start": v(-561.12, 307.12) * mm, "end": v(-561.12, 300.77) * mm});
            skLineSegment(sketch, "E145.0.3.3", {"start": v(-561.12, 307.12) * mm, "end": v(-554.77, 307.12) * mm});
            skLineSegment(sketch, "E145.0.4.0", {"start": v(-554.77, 294.42) * mm, "end": v(-554.77, 288.07) * mm});
            skLineSegment(sketch, "E145.0.4.1", {"start": v(-561.12, 288.07) * mm, "end": v(-554.77, 288.07) * mm});
            skLineSegment(sketch, "E145.0.4.2", {"start": v(-561.12, 294.42) * mm, "end": v(-561.12, 288.07) * mm});
            skLineSegment(sketch, "E145.0.4.3", {"start": v(-561.12, 294.42) * mm, "end": v(-554.77, 294.42) * mm});
            skLineSegment(sketch, "E145.1.0.0", {"start": v(-542.07, 345.22) * mm, "end": v(-542.07, 338.87) * mm});
            skLineSegment(sketch, "E145.1.0.1", {"start": v(-548.42, 338.87) * mm, "end": v(-542.07, 338.87) * mm});
            skLineSegment(sketch, "E145.1.0.2", {"start": v(-548.42, 345.22) * mm, "end": v(-548.42, 338.87) * mm});
            skLineSegment(sketch, "E145.1.0.3", {"start": v(-548.42, 345.22) * mm, "end": v(-542.07, 345.22) * mm});
            skLineSegment(sketch, "E145.1.1.0", {"start": v(-542.07, 332.52) * mm, "end": v(-542.07, 326.17) * mm});
            skLineSegment(sketch, "E145.1.1.1", {"start": v(-548.42, 326.17) * mm, "end": v(-542.07, 326.17) * mm});
            skLineSegment(sketch, "E145.1.1.2", {"start": v(-548.42, 332.52) * mm, "end": v(-548.42, 326.17) * mm});
            skLineSegment(sketch, "E145.1.1.3", {"start": v(-548.42, 332.52) * mm, "end": v(-542.07, 332.52) * mm});
            skLineSegment(sketch, "E145.1.2.0", {"start": v(-542.07, 319.82) * mm, "end": v(-542.07, 313.47) * mm});
            skLineSegment(sketch, "E145.1.2.1", {"start": v(-548.42, 313.47) * mm, "end": v(-542.07, 313.47) * mm});
            skLineSegment(sketch, "E145.1.2.2", {"start": v(-548.42, 319.82) * mm, "end": v(-548.42, 313.47) * mm});
            skLineSegment(sketch, "E145.1.2.3", {"start": v(-548.42, 319.82) * mm, "end": v(-542.07, 319.82) * mm});
            skLineSegment(sketch, "E145.1.3.0", {"start": v(-542.07, 307.12) * mm, "end": v(-542.07, 300.77) * mm});
            skLineSegment(sketch, "E145.1.3.1", {"start": v(-548.42, 300.77) * mm, "end": v(-542.07, 300.77) * mm});
            skLineSegment(sketch, "E145.1.3.2", {"start": v(-548.42, 307.12) * mm, "end": v(-548.42, 300.77) * mm});
            skLineSegment(sketch, "E145.1.3.3", {"start": v(-548.42, 307.12) * mm, "end": v(-542.07, 307.12) * mm});
            skLineSegment(sketch, "E145.1.4.0", {"start": v(-542.07, 294.42) * mm, "end": v(-542.07, 288.07) * mm});
            skLineSegment(sketch, "E145.1.4.1", {"start": v(-548.42, 288.07) * mm, "end": v(-542.07, 288.07) * mm});
            skLineSegment(sketch, "E145.1.4.2", {"start": v(-548.42, 294.42) * mm, "end": v(-548.42, 288.07) * mm});
            skLineSegment(sketch, "E145.1.4.3", {"start": v(-548.42, 294.42) * mm, "end": v(-542.07, 294.42) * mm});
            skLineSegment(sketch, "E145.2.0.0", {"start": v(-529.37, 345.22) * mm, "end": v(-529.37, 338.87) * mm});
            skLineSegment(sketch, "E145.2.0.1", {"start": v(-535.72, 338.87) * mm, "end": v(-529.37, 338.87) * mm});
            skLineSegment(sketch, "E145.2.0.2", {"start": v(-535.72, 345.22) * mm, "end": v(-535.72, 338.87) * mm});
            skLineSegment(sketch, "E145.2.0.3", {"start": v(-535.72, 345.22) * mm, "end": v(-529.37, 345.22) * mm});
            skLineSegment(sketch, "E145.2.1.0", {"start": v(-529.37, 332.52) * mm, "end": v(-529.37, 326.17) * mm});
            skLineSegment(sketch, "E145.2.1.1", {"start": v(-535.72, 326.17) * mm, "end": v(-529.37, 326.17) * mm});
            skLineSegment(sketch, "E145.2.1.2", {"start": v(-535.72, 332.52) * mm, "end": v(-535.72, 326.17) * mm});
            skLineSegment(sketch, "E145.2.1.3", {"start": v(-535.72, 332.52) * mm, "end": v(-529.37, 332.52) * mm});
            skLineSegment(sketch, "E145.2.2.0", {"start": v(-529.37, 319.82) * mm, "end": v(-529.37, 313.47) * mm});
            skLineSegment(sketch, "E145.2.2.1", {"start": v(-535.72, 313.47) * mm, "end": v(-529.37, 313.47) * mm});
            skLineSegment(sketch, "E145.2.2.2", {"start": v(-535.72, 319.82) * mm, "end": v(-535.72, 313.47) * mm});
            skLineSegment(sketch, "E145.2.2.3", {"start": v(-535.72, 319.82) * mm, "end": v(-529.37, 319.82) * mm});
            skLineSegment(sketch, "E145.2.3.0", {"start": v(-529.37, 307.12) * mm, "end": v(-529.37, 300.77) * mm});
            skLineSegment(sketch, "E145.2.3.1", {"start": v(-535.72, 300.77) * mm, "end": v(-529.37, 300.77) * mm});
            skLineSegment(sketch, "E145.2.3.2", {"start": v(-535.72, 307.12) * mm, "end": v(-535.72, 300.77) * mm});
            skLineSegment(sketch, "E145.2.3.3", {"start": v(-535.72, 307.12) * mm, "end": v(-529.37, 307.12) * mm});
            skLineSegment(sketch, "E145.2.4.0", {"start": v(-529.37, 294.42) * mm, "end": v(-529.37, 288.07) * mm});
            skLineSegment(sketch, "E145.2.4.1", {"start": v(-535.72, 288.07) * mm, "end": v(-529.37, 288.07) * mm});
            skLineSegment(sketch, "E145.2.4.2", {"start": v(-535.72, 294.42) * mm, "end": v(-535.72, 288.07) * mm});
            skLineSegment(sketch, "E145.2.4.3", {"start": v(-535.72, 294.42) * mm, "end": v(-529.37, 294.42) * mm});
            skLineSegment(sketch, "E145.3.0.0", {"start": v(-516.67, 345.22) * mm, "end": v(-516.67, 338.87) * mm});
            skLineSegment(sketch, "E145.3.0.1", {"start": v(-523.02, 338.87) * mm, "end": v(-516.67, 338.87) * mm});
            skLineSegment(sketch, "E145.3.0.2", {"start": v(-523.02, 345.22) * mm, "end": v(-523.02, 338.87) * mm});
            skLineSegment(sketch, "E145.3.0.3", {"start": v(-523.02, 345.22) * mm, "end": v(-516.67, 345.22) * mm});
            skLineSegment(sketch, "E145.3.1.0", {"start": v(-516.67, 332.52) * mm, "end": v(-516.67, 326.17) * mm});
            skLineSegment(sketch, "E145.3.1.1", {"start": v(-523.02, 326.17) * mm, "end": v(-516.67, 326.17) * mm});
            skLineSegment(sketch, "E145.3.1.2", {"start": v(-523.02, 332.52) * mm, "end": v(-523.02, 326.17) * mm});
            skLineSegment(sketch, "E145.3.1.3", {"start": v(-523.02, 332.52) * mm, "end": v(-516.67, 332.52) * mm});
            skLineSegment(sketch, "E145.3.2.0", {"start": v(-516.67, 319.82) * mm, "end": v(-516.67, 313.47) * mm});
            skLineSegment(sketch, "E145.3.2.1", {"start": v(-523.02, 313.47) * mm, "end": v(-516.67, 313.47) * mm});
            skLineSegment(sketch, "E145.3.2.2", {"start": v(-523.02, 319.82) * mm, "end": v(-523.02, 313.47) * mm});
            skLineSegment(sketch, "E145.3.2.3", {"start": v(-523.02, 319.82) * mm, "end": v(-516.67, 319.82) * mm});
            skLineSegment(sketch, "E145.3.3.0", {"start": v(-516.67, 307.12) * mm, "end": v(-516.67, 300.77) * mm});
            skLineSegment(sketch, "E145.3.3.1", {"start": v(-523.02, 300.77) * mm, "end": v(-516.67, 300.77) * mm});
            skLineSegment(sketch, "E145.3.3.2", {"start": v(-523.02, 307.12) * mm, "end": v(-523.02, 300.77) * mm});
            skLineSegment(sketch, "E145.3.3.3", {"start": v(-523.02, 307.12) * mm, "end": v(-516.67, 307.12) * mm});
            skLineSegment(sketch, "E145.3.4.0", {"start": v(-516.67, 294.42) * mm, "end": v(-516.67, 288.07) * mm});
            skLineSegment(sketch, "E145.3.4.1", {"start": v(-523.02, 288.07) * mm, "end": v(-516.67, 288.07) * mm});
            skLineSegment(sketch, "E145.3.4.2", {"start": v(-523.02, 294.42) * mm, "end": v(-523.02, 288.07) * mm});
            skLineSegment(sketch, "E145.3.4.3", {"start": v(-523.02, 294.42) * mm, "end": v(-516.67, 294.42) * mm});
            skLineSegment(sketch, "E145.4.0.0", {"start": v(-503.97, 345.22) * mm, "end": v(-503.97, 338.87) * mm});
            skLineSegment(sketch, "E145.4.0.1", {"start": v(-510.32, 338.87) * mm, "end": v(-503.97, 338.87) * mm});
            skLineSegment(sketch, "E145.4.0.2", {"start": v(-510.32, 345.22) * mm, "end": v(-510.32, 338.87) * mm});
            skLineSegment(sketch, "E145.4.0.3", {"start": v(-510.32, 345.22) * mm, "end": v(-503.97, 345.22) * mm});
            skLineSegment(sketch, "E145.4.1.0", {"start": v(-503.97, 332.52) * mm, "end": v(-503.97, 326.17) * mm});
            skLineSegment(sketch, "E145.4.1.1", {"start": v(-510.32, 326.17) * mm, "end": v(-503.97, 326.17) * mm});
            skLineSegment(sketch, "E145.4.1.2", {"start": v(-510.32, 332.52) * mm, "end": v(-510.32, 326.17) * mm});
            skLineSegment(sketch, "E145.4.1.3", {"start": v(-510.32, 332.52) * mm, "end": v(-503.97, 332.52) * mm});
            skLineSegment(sketch, "E145.4.2.0", {"start": v(-503.97, 319.82) * mm, "end": v(-503.97, 313.47) * mm});
            skLineSegment(sketch, "E145.4.2.1", {"start": v(-510.32, 313.47) * mm, "end": v(-503.97, 313.47) * mm});
            skLineSegment(sketch, "E145.4.2.2", {"start": v(-510.32, 319.82) * mm, "end": v(-510.32, 313.47) * mm});
            skLineSegment(sketch, "E145.4.2.3", {"start": v(-510.32, 319.82) * mm, "end": v(-503.97, 319.82) * mm});
            skLineSegment(sketch, "E145.4.3.0", {"start": v(-503.97, 307.12) * mm, "end": v(-503.97, 300.77) * mm});
            skLineSegment(sketch, "E145.4.3.1", {"start": v(-510.32, 300.77) * mm, "end": v(-503.97, 300.77) * mm});
            skLineSegment(sketch, "E145.4.3.2", {"start": v(-510.32, 307.12) * mm, "end": v(-510.32, 300.77) * mm});
            skLineSegment(sketch, "E145.4.3.3", {"start": v(-510.32, 307.12) * mm, "end": v(-503.97, 307.12) * mm});
            skLineSegment(sketch, "E145.4.4.0", {"start": v(-503.97, 294.42) * mm, "end": v(-503.97, 288.07) * mm});
            skLineSegment(sketch, "E145.4.4.1", {"start": v(-510.32, 288.07) * mm, "end": v(-503.97, 288.07) * mm});
            skLineSegment(sketch, "E145.4.4.2", {"start": v(-510.32, 294.42) * mm, "end": v(-510.32, 288.07) * mm});
            skLineSegment(sketch, "E145.4.4.3", {"start": v(-510.32, 294.42) * mm, "end": v(-503.97, 294.42) * mm});
            skLineSegment(sketch, "E145.direction1", {"start": v(-561.12, 338.87) * mm, "end": v(-548.42, 338.87) * mm, "construction": true});
            skLineSegment(sketch, "E145.direction2", {"start": v(-561.12, 338.87) * mm, "end": v(-561.12, 326.17) * mm, "construction": true});
            skLineSegment(sketch, "E146.0.1.0", {"start": v(-535.72, 72.17) * mm, "end": v(-529.37, 72.17) * mm});
            skLineSegment(sketch, "E146.0.1.1", {"start": v(-523.02, 84.87) * mm, "end": v(-516.67, 84.87) * mm});
            skLineSegment(sketch, "E146.0.1.2", {"start": v(-523.02, 34.07) * mm, "end": v(-516.67, 34.07) * mm});
            skLineSegment(sketch, "E146.0.1.3", {"start": v(-510.32, 46.77) * mm, "end": v(-503.97, 46.77) * mm});
            skLineSegment(sketch, "E146.0.1.4", {"start": v(-535.72, 78.52) * mm, "end": v(-529.37, 78.52) * mm});
            skLineSegment(sketch, "E146.0.1.5", {"start": v(-523.02, 91.22) * mm, "end": v(-516.67, 91.22) * mm});
            skLineSegment(sketch, "E146.0.1.6", {"start": v(-523.02, 40.42) * mm, "end": v(-516.67, 40.42) * mm});
            skLineSegment(sketch, "E146.0.1.7", {"start": v(-510.32, 53.12) * mm, "end": v(-503.97, 53.12) * mm});
            skLineSegment(sketch, "E146.0.1.8", {"start": v(-535.72, 78.52) * mm, "end": v(-535.72, 72.17) * mm});
            skLineSegment(sketch, "E146.0.1.9", {"start": v(-523.02, 91.22) * mm, "end": v(-523.02, 84.87) * mm});
            skLineSegment(sketch, "E146.0.1.10", {"start": v(-523.02, 40.42) * mm, "end": v(-523.02, 34.07) * mm});
            skLineSegment(sketch, "E146.0.1.11", {"start": v(-510.32, 53.12) * mm, "end": v(-510.32, 46.77) * mm});
            skLineSegment(sketch, "E146.0.1.12", {"start": v(-554.77, 40.42) * mm, "end": v(-554.77, 34.07) * mm});
            skLineSegment(sketch, "E146.0.1.13", {"start": v(-542.07, 53.12) * mm, "end": v(-542.07, 46.77) * mm});
            skLineSegment(sketch, "E146.0.1.14", {"start": v(-535.72, 65.82) * mm, "end": v(-535.72, 59.47) * mm});
            skLineSegment(sketch, "E146.0.1.15", {"start": v(-523.02, 78.52) * mm, "end": v(-523.02, 72.17) * mm});
            skLineSegment(sketch, "E146.0.1.16", {"start": v(-510.32, 91.22) * mm, "end": v(-510.32, 84.87) * mm});
            skLineSegment(sketch, "E146.0.1.17", {"start": v(-510.32, 40.42) * mm, "end": v(-510.32, 34.07) * mm});
            skLineSegment(sketch, "E146.0.1.18", {"start": v(-561.12, 40.42) * mm, "end": v(-561.12, 34.07) * mm});
            skLineSegment(sketch, "E146.0.1.19", {"start": v(-548.42, 53.12) * mm, "end": v(-548.42, 46.77) * mm});
            skLineSegment(sketch, "E146.0.1.20", {"start": v(-561.12, 34.07) * mm, "end": v(-554.77, 34.07) * mm});
            skLineSegment(sketch, "E146.0.1.21", {"start": v(-548.42, 46.77) * mm, "end": v(-542.07, 46.77) * mm});
            skLineSegment(sketch, "E146.0.1.22", {"start": v(-535.72, 59.47) * mm, "end": v(-529.37, 59.47) * mm});
            skLineSegment(sketch, "E146.0.1.23", {"start": v(-523.02, 72.17) * mm, "end": v(-516.67, 72.17) * mm});
            skLineSegment(sketch, "E146.0.1.24", {"start": v(-510.32, 84.87) * mm, "end": v(-503.97, 84.87) * mm});
            skLineSegment(sketch, "E146.0.1.25", {"start": v(-510.32, 34.07) * mm, "end": v(-503.97, 34.07) * mm});
            skLineSegment(sketch, "E146.0.1.26", {"start": v(-529.37, 65.82) * mm, "end": v(-529.37, 59.47) * mm});
            skLineSegment(sketch, "E146.0.1.27", {"start": v(-516.67, 78.52) * mm, "end": v(-516.67, 72.17) * mm});
            skLineSegment(sketch, "E146.0.1.28", {"start": v(-503.97, 91.22) * mm, "end": v(-503.97, 84.87) * mm});
            skLineSegment(sketch, "E146.0.1.29", {"start": v(-503.97, 40.42) * mm, "end": v(-503.97, 34.07) * mm});
            skLineSegment(sketch, "E146.0.1.30", {"start": v(-548.42, 78.52) * mm, "end": v(-548.42, 72.17) * mm});
            skLineSegment(sketch, "E146.0.1.31", {"start": v(-535.72, 91.22) * mm, "end": v(-535.72, 84.87) * mm});
            skLineSegment(sketch, "E146.0.1.32", {"start": v(-535.72, 40.42) * mm, "end": v(-535.72, 34.07) * mm});
            skLineSegment(sketch, "E146.0.1.33", {"start": v(-523.02, 53.12) * mm, "end": v(-523.02, 46.77) * mm});
            skLineSegment(sketch, "E146.0.1.34", {"start": v(-510.32, 65.82) * mm, "end": v(-510.32, 59.47) * mm});
            skLineSegment(sketch, "E146.0.1.35", {"start": v(-510.32, 59.47) * mm, "end": v(-503.97, 59.47) * mm});
            skLineSegment(sketch, "E146.0.1.36", {"start": v(-548.42, 72.17) * mm, "end": v(-542.07, 72.17) * mm});
            skLineSegment(sketch, "E146.0.1.37", {"start": v(-535.72, 84.87) * mm, "end": v(-529.37, 84.87) * mm});
            skLineSegment(sketch, "E146.0.1.38", {"start": v(-535.72, 34.07) * mm, "end": v(-529.37, 34.07) * mm});
            skLineSegment(sketch, "E146.0.1.39", {"start": v(-523.02, 46.77) * mm, "end": v(-516.67, 46.77) * mm});
            skLineSegment(sketch, "E146.0.1.40", {"start": v(-542.07, 65.82) * mm, "end": v(-542.07, 59.47) * mm});
            skLineSegment(sketch, "E146.0.1.41", {"start": v(-529.37, 78.52) * mm, "end": v(-529.37, 72.17) * mm});
            skLineSegment(sketch, "E146.0.1.42", {"start": v(-516.67, 91.22) * mm, "end": v(-516.67, 84.87) * mm});
            skLineSegment(sketch, "E146.0.1.43", {"start": v(-516.67, 40.42) * mm, "end": v(-516.67, 34.07) * mm});
            skLineSegment(sketch, "E146.0.1.44", {"start": v(-503.97, 53.12) * mm, "end": v(-503.97, 46.77) * mm});
            skLineSegment(sketch, "E146.0.1.45", {"start": v(-548.42, 78.52) * mm, "end": v(-542.07, 78.52) * mm});
            skLineSegment(sketch, "E146.0.1.46", {"start": v(-535.72, 91.22) * mm, "end": v(-529.37, 91.22) * mm});
            skLineSegment(sketch, "E146.0.1.47", {"start": v(-535.72, 40.42) * mm, "end": v(-529.37, 40.42) * mm});
            skLineSegment(sketch, "E146.0.1.48", {"start": v(-523.02, 53.12) * mm, "end": v(-516.67, 53.12) * mm});
            skLineSegment(sketch, "E146.0.1.49", {"start": v(-510.32, 65.82) * mm, "end": v(-503.97, 65.82) * mm});
            skLineSegment(sketch, "E146.0.1.50", {"start": v(-542.07, 91.22) * mm, "end": v(-542.07, 84.87) * mm});
            skLineSegment(sketch, "E146.0.1.51", {"start": v(-542.07, 40.42) * mm, "end": v(-542.07, 34.07) * mm});
            skLineSegment(sketch, "E146.0.1.52", {"start": v(-529.37, 53.12) * mm, "end": v(-529.37, 46.77) * mm});
            skLineSegment(sketch, "E146.0.1.53", {"start": v(-516.67, 65.82) * mm, "end": v(-516.67, 59.47) * mm});
            skLineSegment(sketch, "E146.0.1.54", {"start": v(-503.97, 78.52) * mm, "end": v(-503.97, 72.17) * mm});
            skLineSegment(sketch, "E146.0.1.55", {"start": v(-561.12, 40.42) * mm, "end": v(-554.77, 40.42) * mm});
            skLineSegment(sketch, "E146.0.1.56", {"start": v(-548.42, 53.12) * mm, "end": v(-542.07, 53.12) * mm});
            skLineSegment(sketch, "E146.0.1.57", {"start": v(-535.72, 65.82) * mm, "end": v(-529.37, 65.82) * mm});
            skLineSegment(sketch, "E146.0.1.58", {"start": v(-523.02, 78.52) * mm, "end": v(-516.67, 78.52) * mm});
            skLineSegment(sketch, "E146.0.1.59", {"start": v(-510.32, 91.22) * mm, "end": v(-503.97, 91.22) * mm});
            skLineSegment(sketch, "E146.0.1.60", {"start": v(-510.32, 40.42) * mm, "end": v(-503.97, 40.42) * mm});
            skLineSegment(sketch, "E146.0.1.61", {"start": v(-535.72, 53.12) * mm, "end": v(-535.72, 46.77) * mm});
            skLineSegment(sketch, "E146.0.1.62", {"start": v(-523.02, 65.82) * mm, "end": v(-523.02, 59.47) * mm});
            skLineSegment(sketch, "E146.0.1.63", {"start": v(-510.32, 78.52) * mm, "end": v(-510.32, 72.17) * mm});
            skLineSegment(sketch, "E146.0.1.64", {"start": v(-548.42, 40.42) * mm, "end": v(-548.42, 34.07) * mm});
            skLineSegment(sketch, "E146.0.1.65", {"start": v(-561.12, 46.77) * mm, "end": v(-554.77, 46.77) * mm});
            skLineSegment(sketch, "E146.0.1.66", {"start": v(-561.12, 53.12) * mm, "end": v(-554.77, 53.12) * mm});
            skLineSegment(sketch, "E146.0.1.67", {"start": v(-561.12, 53.12) * mm, "end": v(-561.12, 46.77) * mm});
            skLineSegment(sketch, "E146.0.1.68", {"start": v(-548.42, 84.87) * mm, "end": v(-542.07, 84.87) * mm});
            skLineSegment(sketch, "E146.0.1.69", {"start": v(-548.42, 34.07) * mm, "end": v(-542.07, 34.07) * mm});
            skLineSegment(sketch, "E146.0.1.70", {"start": v(-535.72, 46.77) * mm, "end": v(-529.37, 46.77) * mm});
            skLineSegment(sketch, "E146.0.1.71", {"start": v(-523.02, 59.47) * mm, "end": v(-516.67, 59.47) * mm});
            skLineSegment(sketch, "E146.0.1.72", {"start": v(-510.32, 72.17) * mm, "end": v(-503.97, 72.17) * mm});
            skLineSegment(sketch, "E146.0.1.73", {"start": v(-561.12, 59.47) * mm, "end": v(-554.77, 59.47) * mm});
            skLineSegment(sketch, "E146.0.1.74", {"start": v(-561.12, 65.82) * mm, "end": v(-561.12, 59.47) * mm});
            skLineSegment(sketch, "E146.0.1.75", {"start": v(-554.77, 53.12) * mm, "end": v(-554.77, 46.77) * mm});
            skLineSegment(sketch, "E146.0.1.76", {"start": v(-542.07, 78.52) * mm, "end": v(-542.07, 72.17) * mm});
            skLineSegment(sketch, "E146.0.1.77", {"start": v(-529.37, 91.22) * mm, "end": v(-529.37, 84.87) * mm});
            skLineSegment(sketch, "E146.0.1.78", {"start": v(-529.37, 40.42) * mm, "end": v(-529.37, 34.07) * mm});
            skLineSegment(sketch, "E146.0.1.79", {"start": v(-516.67, 53.12) * mm, "end": v(-516.67, 46.77) * mm});
            skLineSegment(sketch, "E146.0.1.80", {"start": v(-503.97, 65.82) * mm, "end": v(-503.97, 59.47) * mm});
            skLineSegment(sketch, "E146.0.1.81", {"start": v(-548.42, 40.42) * mm, "end": v(-542.07, 40.42) * mm});
            skLineSegment(sketch, "E146.0.1.82", {"start": v(-535.72, 53.12) * mm, "end": v(-529.37, 53.12) * mm});
            skLineSegment(sketch, "E146.0.1.83", {"start": v(-523.02, 65.82) * mm, "end": v(-516.67, 65.82) * mm});
            skLineSegment(sketch, "E146.0.1.84", {"start": v(-510.32, 78.52) * mm, "end": v(-503.97, 78.52) * mm});
            skLineSegment(sketch, "E146.0.1.85", {"start": v(-548.42, 59.47) * mm, "end": v(-542.07, 59.47) * mm});
            skLineSegment(sketch, "E146.0.1.86", {"start": v(-548.42, 65.82) * mm, "end": v(-542.07, 65.82) * mm});
            skLineSegment(sketch, "E146.0.1.87", {"start": v(-548.42, 65.82) * mm, "end": v(-548.42, 59.47) * mm});
            skLineSegment(sketch, "E146.0.1.88", {"start": v(-561.12, 84.87) * mm, "end": v(-548.42, 84.87) * mm, "construction": true});
            skLineSegment(sketch, "E146.0.1.89", {"start": v(-554.77, 78.52) * mm, "end": v(-554.77, 72.17) * mm});
            skLineSegment(sketch, "E146.0.1.90", {"start": v(-554.77, 91.22) * mm, "end": v(-554.77, 84.87) * mm});
            skLineSegment(sketch, "E146.0.1.91", {"start": v(-561.12, 72.17) * mm, "end": v(-554.77, 72.17) * mm});
            skLineSegment(sketch, "E146.0.1.92", {"start": v(-561.12, 78.52) * mm, "end": v(-554.77, 78.52) * mm});
            skLineSegment(sketch, "E146.0.1.93", {"start": v(-561.12, 84.87) * mm, "end": v(-561.12, 72.17) * mm, "construction": true});
            skLineSegment(sketch, "E146.0.1.94", {"start": v(-554.77, 65.82) * mm, "end": v(-554.77, 59.47) * mm});
            skLineSegment(sketch, "E146.0.1.95", {"start": v(-561.12, 65.82) * mm, "end": v(-554.77, 65.82) * mm});
            skLineSegment(sketch, "E146.0.1.96", {"start": v(-548.42, 91.22) * mm, "end": v(-542.07, 91.22) * mm});
            skLineSegment(sketch, "E146.0.1.97", {"start": v(-548.42, 91.22) * mm, "end": v(-548.42, 84.87) * mm});
            skLineSegment(sketch, "E146.0.1.98", {"start": v(-561.12, 91.22) * mm, "end": v(-554.77, 91.22) * mm});
            skLineSegment(sketch, "E146.0.1.99", {"start": v(-561.12, 91.22) * mm, "end": v(-561.12, 84.87) * mm});
            skLineSegment(sketch, "E146.0.1.100", {"start": v(-561.12, 84.87) * mm, "end": v(-554.77, 84.87) * mm});
            skLineSegment(sketch, "E146.0.1.101", {"start": v(-561.12, 78.52) * mm, "end": v(-561.12, 72.17) * mm});
            skLineSegment(sketch, "E146.1.0.0", {"start": v(-322.36, 326.17) * mm, "end": v(-316, 326.17) * mm});
            skLineSegment(sketch, "E146.1.0.1", {"start": v(-309.66, 338.87) * mm, "end": v(-303.3, 338.87) * mm});
            skLineSegment(sketch, "E146.1.0.2", {"start": v(-309.66, 288.07) * mm, "end": v(-303.3, 288.07) * mm});
            skLineSegment(sketch, "E146.1.0.3", {"start": v(-296.96, 300.77) * mm, "end": v(-290.6, 300.77) * mm});
            skLineSegment(sketch, "E146.1.0.4", {"start": v(-322.36, 332.52) * mm, "end": v(-316, 332.52) * mm});
            skLineSegment(sketch, "E146.1.0.5", {"start": v(-309.66, 345.22) * mm, "end": v(-303.3, 345.22) * mm});
            skLineSegment(sketch, "E146.1.0.6", {"start": v(-309.66, 294.42) * mm, "end": v(-303.3, 294.42) * mm});
            skLineSegment(sketch, "E146.1.0.7", {"start": v(-296.96, 307.12) * mm, "end": v(-290.6, 307.12) * mm});
            skLineSegment(sketch, "E146.1.0.8", {"start": v(-322.36, 332.52) * mm, "end": v(-322.36, 326.17) * mm});
            skLineSegment(sketch, "E146.1.0.9", {"start": v(-309.66, 345.22) * mm, "end": v(-309.66, 338.87) * mm});
            skLineSegment(sketch, "E146.1.0.10", {"start": v(-309.66, 294.42) * mm, "end": v(-309.66, 288.07) * mm});
            skLineSegment(sketch, "E146.1.0.11", {"start": v(-296.96, 307.12) * mm, "end": v(-296.96, 300.77) * mm});
            skLineSegment(sketch, "E146.1.0.12", {"start": v(-341.4, 294.42) * mm, "end": v(-341.4, 288.07) * mm});
            skLineSegment(sketch, "E146.1.0.13", {"start": v(-328.7, 307.12) * mm, "end": v(-328.7, 300.77) * mm});
            skLineSegment(sketch, "E146.1.0.14", {"start": v(-322.36, 319.82) * mm, "end": v(-322.36, 313.47) * mm});
            skLineSegment(sketch, "E146.1.0.15", {"start": v(-309.66, 332.52) * mm, "end": v(-309.66, 326.17) * mm});
            skLineSegment(sketch, "E146.1.0.16", {"start": v(-296.96, 345.22) * mm, "end": v(-296.96, 338.87) * mm});
            skLineSegment(sketch, "E146.1.0.17", {"start": v(-296.96, 294.42) * mm, "end": v(-296.96, 288.07) * mm});
            skLineSegment(sketch, "E146.1.0.18", {"start": v(-347.76, 294.42) * mm, "end": v(-347.76, 288.07) * mm});
            skLineSegment(sketch, "E146.1.0.19", {"start": v(-335.06, 307.12) * mm, "end": v(-335.06, 300.77) * mm});
            skLineSegment(sketch, "E146.1.0.20", {"start": v(-347.76, 288.07) * mm, "end": v(-341.4, 288.07) * mm});
            skLineSegment(sketch, "E146.1.0.21", {"start": v(-335.06, 300.77) * mm, "end": v(-328.7, 300.77) * mm});
            skLineSegment(sketch, "E146.1.0.22", {"start": v(-322.36, 313.47) * mm, "end": v(-316, 313.47) * mm});
            skLineSegment(sketch, "E146.1.0.23", {"start": v(-309.66, 326.17) * mm, "end": v(-303.3, 326.17) * mm});
            skLineSegment(sketch, "E146.1.0.24", {"start": v(-296.96, 338.87) * mm, "end": v(-290.6, 338.87) * mm});
            skLineSegment(sketch, "E146.1.0.25", {"start": v(-296.96, 288.07) * mm, "end": v(-290.6, 288.07) * mm});
            skLineSegment(sketch, "E146.1.0.26", {"start": v(-316, 319.82) * mm, "end": v(-316, 313.47) * mm});
            skLineSegment(sketch, "E146.1.0.27", {"start": v(-303.3, 332.52) * mm, "end": v(-303.3, 326.17) * mm});
            skLineSegment(sketch, "E146.1.0.28", {"start": v(-290.6, 345.22) * mm, "end": v(-290.6, 338.87) * mm});
            skLineSegment(sketch, "E146.1.0.29", {"start": v(-290.6, 294.42) * mm, "end": v(-290.6, 288.07) * mm});
            skLineSegment(sketch, "E146.1.0.30", {"start": v(-335.06, 332.52) * mm, "end": v(-335.06, 326.17) * mm});
            skLineSegment(sketch, "E146.1.0.31", {"start": v(-322.36, 345.22) * mm, "end": v(-322.36, 338.87) * mm});
            skLineSegment(sketch, "E146.1.0.32", {"start": v(-322.36, 294.42) * mm, "end": v(-322.36, 288.07) * mm});
            skLineSegment(sketch, "E146.1.0.33", {"start": v(-309.66, 307.12) * mm, "end": v(-309.66, 300.77) * mm});
            skLineSegment(sketch, "E146.1.0.34", {"start": v(-296.96, 319.82) * mm, "end": v(-296.96, 313.47) * mm});
            skLineSegment(sketch, "E146.1.0.35", {"start": v(-296.96, 313.47) * mm, "end": v(-290.6, 313.47) * mm});
            skLineSegment(sketch, "E146.1.0.36", {"start": v(-335.06, 326.17) * mm, "end": v(-328.7, 326.17) * mm});
            skLineSegment(sketch, "E146.1.0.37", {"start": v(-322.36, 338.87) * mm, "end": v(-316, 338.87) * mm});
            skLineSegment(sketch, "E146.1.0.38", {"start": v(-322.36, 288.07) * mm, "end": v(-316, 288.07) * mm});
            skLineSegment(sketch, "E146.1.0.39", {"start": v(-309.66, 300.77) * mm, "end": v(-303.3, 300.77) * mm});
            skLineSegment(sketch, "E146.1.0.40", {"start": v(-328.7, 319.82) * mm, "end": v(-328.7, 313.47) * mm});
            skLineSegment(sketch, "E146.1.0.41", {"start": v(-316, 332.52) * mm, "end": v(-316, 326.17) * mm});
            skLineSegment(sketch, "E146.1.0.42", {"start": v(-303.3, 345.22) * mm, "end": v(-303.3, 338.87) * mm});
            skLineSegment(sketch, "E146.1.0.43", {"start": v(-303.3, 294.42) * mm, "end": v(-303.3, 288.07) * mm});
            skLineSegment(sketch, "E146.1.0.44", {"start": v(-290.6, 307.12) * mm, "end": v(-290.6, 300.77) * mm});
            skLineSegment(sketch, "E146.1.0.45", {"start": v(-335.06, 332.52) * mm, "end": v(-328.7, 332.52) * mm});
            skLineSegment(sketch, "E146.1.0.46", {"start": v(-322.36, 345.22) * mm, "end": v(-316, 345.22) * mm});
            skLineSegment(sketch, "E146.1.0.47", {"start": v(-322.36, 294.42) * mm, "end": v(-316, 294.42) * mm});
            skLineSegment(sketch, "E146.1.0.48", {"start": v(-309.66, 307.12) * mm, "end": v(-303.3, 307.12) * mm});
            skLineSegment(sketch, "E146.1.0.49", {"start": v(-296.96, 319.82) * mm, "end": v(-290.6, 319.82) * mm});
            skLineSegment(sketch, "E146.1.0.50", {"start": v(-328.7, 345.22) * mm, "end": v(-328.7, 338.87) * mm});
            skLineSegment(sketch, "E146.1.0.51", {"start": v(-328.7, 294.42) * mm, "end": v(-328.7, 288.07) * mm});
            skLineSegment(sketch, "E146.1.0.52", {"start": v(-316, 307.12) * mm, "end": v(-316, 300.77) * mm});
            skLineSegment(sketch, "E146.1.0.53", {"start": v(-303.3, 319.82) * mm, "end": v(-303.3, 313.47) * mm});
            skLineSegment(sketch, "E146.1.0.54", {"start": v(-290.6, 332.52) * mm, "end": v(-290.6, 326.17) * mm});
            skLineSegment(sketch, "E146.1.0.55", {"start": v(-347.76, 294.42) * mm, "end": v(-341.4, 294.42) * mm});
            skLineSegment(sketch, "E146.1.0.56", {"start": v(-335.06, 307.12) * mm, "end": v(-328.7, 307.12) * mm});
            skLineSegment(sketch, "E146.1.0.57", {"start": v(-322.36, 319.82) * mm, "end": v(-316, 319.82) * mm});
            skLineSegment(sketch, "E146.1.0.58", {"start": v(-309.66, 332.52) * mm, "end": v(-303.3, 332.52) * mm});
            skLineSegment(sketch, "E146.1.0.59", {"start": v(-296.96, 345.22) * mm, "end": v(-290.6, 345.22) * mm});
            skLineSegment(sketch, "E146.1.0.60", {"start": v(-296.96, 294.42) * mm, "end": v(-290.6, 294.42) * mm});
            skLineSegment(sketch, "E146.1.0.61", {"start": v(-322.36, 307.12) * mm, "end": v(-322.36, 300.77) * mm});
            skLineSegment(sketch, "E146.1.0.62", {"start": v(-309.66, 319.82) * mm, "end": v(-309.66, 313.47) * mm});
            skLineSegment(sketch, "E146.1.0.63", {"start": v(-296.96, 332.52) * mm, "end": v(-296.96, 326.17) * mm});
            skLineSegment(sketch, "E146.1.0.64", {"start": v(-335.06, 294.42) * mm, "end": v(-335.06, 288.07) * mm});
            skLineSegment(sketch, "E146.1.0.65", {"start": v(-347.76, 300.77) * mm, "end": v(-341.4, 300.77) * mm});
            skLineSegment(sketch, "E146.1.0.66", {"start": v(-347.76, 307.12) * mm, "end": v(-341.4, 307.12) * mm});
            skLineSegment(sketch, "E146.1.0.67", {"start": v(-347.76, 307.12) * mm, "end": v(-347.76, 300.77) * mm});
            skLineSegment(sketch, "E146.1.0.68", {"start": v(-335.06, 338.87) * mm, "end": v(-328.7, 338.87) * mm});
            skLineSegment(sketch, "E146.1.0.69", {"start": v(-335.06, 288.07) * mm, "end": v(-328.7, 288.07) * mm});
            skLineSegment(sketch, "E146.1.0.70", {"start": v(-322.36, 300.77) * mm, "end": v(-316, 300.77) * mm});
            skLineSegment(sketch, "E146.1.0.71", {"start": v(-309.66, 313.47) * mm, "end": v(-303.3, 313.47) * mm});
            skLineSegment(sketch, "E146.1.0.72", {"start": v(-296.96, 326.17) * mm, "end": v(-290.6, 326.17) * mm});
            skLineSegment(sketch, "E146.1.0.73", {"start": v(-347.76, 313.47) * mm, "end": v(-341.4, 313.47) * mm});
            skLineSegment(sketch, "E146.1.0.74", {"start": v(-347.76, 319.82) * mm, "end": v(-347.76, 313.47) * mm});
            skLineSegment(sketch, "E146.1.0.75", {"start": v(-341.4, 307.12) * mm, "end": v(-341.4, 300.77) * mm});
            skLineSegment(sketch, "E146.1.0.76", {"start": v(-328.7, 332.52) * mm, "end": v(-328.7, 326.17) * mm});
            skLineSegment(sketch, "E146.1.0.77", {"start": v(-316, 345.22) * mm, "end": v(-316, 338.87) * mm});
            skLineSegment(sketch, "E146.1.0.78", {"start": v(-316, 294.42) * mm, "end": v(-316, 288.07) * mm});
            skLineSegment(sketch, "E146.1.0.79", {"start": v(-303.3, 307.12) * mm, "end": v(-303.3, 300.77) * mm});
            skLineSegment(sketch, "E146.1.0.80", {"start": v(-290.6, 319.82) * mm, "end": v(-290.6, 313.47) * mm});
            skLineSegment(sketch, "E146.1.0.81", {"start": v(-335.06, 294.42) * mm, "end": v(-328.7, 294.42) * mm});
            skLineSegment(sketch, "E146.1.0.82", {"start": v(-322.36, 307.12) * mm, "end": v(-316, 307.12) * mm});
            skLineSegment(sketch, "E146.1.0.83", {"start": v(-309.66, 319.82) * mm, "end": v(-303.3, 319.82) * mm});
            skLineSegment(sketch, "E146.1.0.84", {"start": v(-296.96, 332.52) * mm, "end": v(-290.6, 332.52) * mm});
            skLineSegment(sketch, "E146.1.0.85", {"start": v(-335.06, 313.47) * mm, "end": v(-328.7, 313.47) * mm});
            skLineSegment(sketch, "E146.1.0.86", {"start": v(-335.06, 319.82) * mm, "end": v(-328.7, 319.82) * mm});
            skLineSegment(sketch, "E146.1.0.87", {"start": v(-335.06, 319.82) * mm, "end": v(-335.06, 313.47) * mm});
            skLineSegment(sketch, "E146.1.0.88", {"start": v(-347.76, 338.87) * mm, "end": v(-335.06, 338.87) * mm, "construction": true});
            skLineSegment(sketch, "E146.1.0.89", {"start": v(-341.4, 332.52) * mm, "end": v(-341.4, 326.17) * mm});
            skLineSegment(sketch, "E146.1.0.90", {"start": v(-341.4, 345.22) * mm, "end": v(-341.4, 338.87) * mm});
            skLineSegment(sketch, "E146.1.0.91", {"start": v(-347.76, 326.17) * mm, "end": v(-341.4, 326.17) * mm});
            skLineSegment(sketch, "E146.1.0.92", {"start": v(-347.76, 332.52) * mm, "end": v(-341.4, 332.52) * mm});
            skLineSegment(sketch, "E146.1.0.93", {"start": v(-347.76, 338.87) * mm, "end": v(-347.76, 326.17) * mm, "construction": true});
            skLineSegment(sketch, "E146.1.0.94", {"start": v(-341.4, 319.82) * mm, "end": v(-341.4, 313.47) * mm});
            skLineSegment(sketch, "E146.1.0.95", {"start": v(-347.76, 319.82) * mm, "end": v(-341.4, 319.82) * mm});
            skLineSegment(sketch, "E146.1.0.96", {"start": v(-335.06, 345.22) * mm, "end": v(-328.7, 345.22) * mm});
            skLineSegment(sketch, "E146.1.0.97", {"start": v(-335.06, 345.22) * mm, "end": v(-335.06, 338.87) * mm});
            skLineSegment(sketch, "E146.1.0.98", {"start": v(-347.76, 345.22) * mm, "end": v(-341.4, 345.22) * mm});
            skLineSegment(sketch, "E146.1.0.99", {"start": v(-347.76, 345.22) * mm, "end": v(-347.76, 338.87) * mm});
            skLineSegment(sketch, "E146.1.0.100", {"start": v(-347.76, 338.87) * mm, "end": v(-341.4, 338.87) * mm});
            skLineSegment(sketch, "E146.1.0.101", {"start": v(-347.76, 332.52) * mm, "end": v(-347.76, 326.17) * mm});
            skLineSegment(sketch, "E146.1.1.0", {"start": v(-322.36, 72.17) * mm, "end": v(-316, 72.17) * mm});
            skLineSegment(sketch, "E146.1.1.1", {"start": v(-309.66, 84.87) * mm, "end": v(-303.3, 84.87) * mm});
            skLineSegment(sketch, "E146.1.1.2", {"start": v(-309.66, 34.07) * mm, "end": v(-303.3, 34.07) * mm});
            skLineSegment(sketch, "E146.1.1.3", {"start": v(-296.96, 46.77) * mm, "end": v(-290.6, 46.77) * mm});
            skLineSegment(sketch, "E146.1.1.4", {"start": v(-322.36, 78.52) * mm, "end": v(-316, 78.52) * mm});
            skLineSegment(sketch, "E146.1.1.5", {"start": v(-309.66, 91.22) * mm, "end": v(-303.3, 91.22) * mm});
            skLineSegment(sketch, "E146.1.1.6", {"start": v(-309.66, 40.42) * mm, "end": v(-303.3, 40.42) * mm});
            skLineSegment(sketch, "E146.1.1.7", {"start": v(-296.96, 53.12) * mm, "end": v(-290.6, 53.12) * mm});
            skLineSegment(sketch, "E146.1.1.8", {"start": v(-322.36, 78.52) * mm, "end": v(-322.36, 72.17) * mm});
            skLineSegment(sketch, "E146.1.1.9", {"start": v(-309.66, 91.22) * mm, "end": v(-309.66, 84.87) * mm});
            skLineSegment(sketch, "E146.1.1.10", {"start": v(-309.66, 40.42) * mm, "end": v(-309.66, 34.07) * mm});
            skLineSegment(sketch, "E146.1.1.11", {"start": v(-296.96, 53.12) * mm, "end": v(-296.96, 46.77) * mm});
            skLineSegment(sketch, "E146.1.1.12", {"start": v(-341.4, 40.42) * mm, "end": v(-341.4, 34.07) * mm});
            skLineSegment(sketch, "E146.1.1.13", {"start": v(-328.7, 53.12) * mm, "end": v(-328.7, 46.77) * mm});
            skLineSegment(sketch, "E146.1.1.14", {"start": v(-322.36, 65.82) * mm, "end": v(-322.36, 59.47) * mm});
            skLineSegment(sketch, "E146.1.1.15", {"start": v(-309.66, 78.52) * mm, "end": v(-309.66, 72.17) * mm});
            skLineSegment(sketch, "E146.1.1.16", {"start": v(-296.96, 91.22) * mm, "end": v(-296.96, 84.87) * mm});
            skLineSegment(sketch, "E146.1.1.17", {"start": v(-296.96, 40.42) * mm, "end": v(-296.96, 34.07) * mm});
            skLineSegment(sketch, "E146.1.1.18", {"start": v(-347.76, 40.42) * mm, "end": v(-347.76, 34.07) * mm});
            skLineSegment(sketch, "E146.1.1.19", {"start": v(-335.06, 53.12) * mm, "end": v(-335.06, 46.77) * mm});
            skLineSegment(sketch, "E146.1.1.20", {"start": v(-347.76, 34.07) * mm, "end": v(-341.4, 34.07) * mm});
            skLineSegment(sketch, "E146.1.1.21", {"start": v(-335.06, 46.77) * mm, "end": v(-328.7, 46.77) * mm});
            skLineSegment(sketch, "E146.1.1.22", {"start": v(-322.36, 59.47) * mm, "end": v(-316, 59.47) * mm});
            skLineSegment(sketch, "E146.1.1.23", {"start": v(-309.66, 72.17) * mm, "end": v(-303.3, 72.17) * mm});
            skLineSegment(sketch, "E146.1.1.24", {"start": v(-296.96, 84.87) * mm, "end": v(-290.6, 84.87) * mm});
            skLineSegment(sketch, "E146.1.1.25", {"start": v(-296.96, 34.07) * mm, "end": v(-290.6, 34.07) * mm});
            skLineSegment(sketch, "E146.1.1.26", {"start": v(-316, 65.82) * mm, "end": v(-316, 59.47) * mm});
            skLineSegment(sketch, "E146.1.1.27", {"start": v(-303.3, 78.52) * mm, "end": v(-303.3, 72.17) * mm});
            skLineSegment(sketch, "E146.1.1.28", {"start": v(-290.6, 91.22) * mm, "end": v(-290.6, 84.87) * mm});
            skLineSegment(sketch, "E146.1.1.29", {"start": v(-290.6, 40.42) * mm, "end": v(-290.6, 34.07) * mm});
            skLineSegment(sketch, "E146.1.1.30", {"start": v(-335.06, 78.52) * mm, "end": v(-335.06, 72.17) * mm});
            skLineSegment(sketch, "E146.1.1.31", {"start": v(-322.36, 91.22) * mm, "end": v(-322.36, 84.87) * mm});
            skLineSegment(sketch, "E146.1.1.32", {"start": v(-322.36, 40.42) * mm, "end": v(-322.36, 34.07) * mm});
            skLineSegment(sketch, "E146.1.1.33", {"start": v(-309.66, 53.12) * mm, "end": v(-309.66, 46.77) * mm});
            skLineSegment(sketch, "E146.1.1.34", {"start": v(-296.96, 65.82) * mm, "end": v(-296.96, 59.47) * mm});
            skLineSegment(sketch, "E146.1.1.35", {"start": v(-296.96, 59.47) * mm, "end": v(-290.6, 59.47) * mm});
            skLineSegment(sketch, "E146.1.1.36", {"start": v(-335.06, 72.17) * mm, "end": v(-328.7, 72.17) * mm});
            skLineSegment(sketch, "E146.1.1.37", {"start": v(-322.36, 84.87) * mm, "end": v(-316, 84.87) * mm});
            skLineSegment(sketch, "E146.1.1.38", {"start": v(-322.36, 34.07) * mm, "end": v(-316, 34.07) * mm});
            skLineSegment(sketch, "E146.1.1.39", {"start": v(-309.66, 46.77) * mm, "end": v(-303.3, 46.77) * mm});
            skLineSegment(sketch, "E146.1.1.40", {"start": v(-328.7, 65.82) * mm, "end": v(-328.7, 59.47) * mm});
            skLineSegment(sketch, "E146.1.1.41", {"start": v(-316, 78.52) * mm, "end": v(-316, 72.17) * mm});
            skLineSegment(sketch, "E146.1.1.42", {"start": v(-303.3, 91.22) * mm, "end": v(-303.3, 84.87) * mm});
            skLineSegment(sketch, "E146.1.1.43", {"start": v(-303.3, 40.42) * mm, "end": v(-303.3, 34.07) * mm});
            skLineSegment(sketch, "E146.1.1.44", {"start": v(-290.6, 53.12) * mm, "end": v(-290.6, 46.77) * mm});
            skLineSegment(sketch, "E146.1.1.45", {"start": v(-335.06, 78.52) * mm, "end": v(-328.7, 78.52) * mm});
            skLineSegment(sketch, "E146.1.1.46", {"start": v(-322.36, 91.22) * mm, "end": v(-316, 91.22) * mm});
            skLineSegment(sketch, "E146.1.1.47", {"start": v(-322.36, 40.42) * mm, "end": v(-316, 40.42) * mm});
            skLineSegment(sketch, "E146.1.1.48", {"start": v(-309.66, 53.12) * mm, "end": v(-303.3, 53.12) * mm});
            skLineSegment(sketch, "E146.1.1.49", {"start": v(-296.96, 65.82) * mm, "end": v(-290.6, 65.82) * mm});
            skLineSegment(sketch, "E146.1.1.50", {"start": v(-328.7, 91.22) * mm, "end": v(-328.7, 84.87) * mm});
            skLineSegment(sketch, "E146.1.1.51", {"start": v(-328.7, 40.42) * mm, "end": v(-328.7, 34.07) * mm});
            skLineSegment(sketch, "E146.1.1.52", {"start": v(-316, 53.12) * mm, "end": v(-316, 46.77) * mm});
            skLineSegment(sketch, "E146.1.1.53", {"start": v(-303.3, 65.82) * mm, "end": v(-303.3, 59.47) * mm});
            skLineSegment(sketch, "E146.1.1.54", {"start": v(-290.6, 78.52) * mm, "end": v(-290.6, 72.17) * mm});
            skLineSegment(sketch, "E146.1.1.55", {"start": v(-347.76, 40.42) * mm, "end": v(-341.4, 40.42) * mm});
            skLineSegment(sketch, "E146.1.1.56", {"start": v(-335.06, 53.12) * mm, "end": v(-328.7, 53.12) * mm});
            skLineSegment(sketch, "E146.1.1.57", {"start": v(-322.36, 65.82) * mm, "end": v(-316, 65.82) * mm});
            skLineSegment(sketch, "E146.1.1.58", {"start": v(-309.66, 78.52) * mm, "end": v(-303.3, 78.52) * mm});
            skLineSegment(sketch, "E146.1.1.59", {"start": v(-296.96, 91.22) * mm, "end": v(-290.6, 91.22) * mm});
            skLineSegment(sketch, "E146.1.1.60", {"start": v(-296.96, 40.42) * mm, "end": v(-290.6, 40.42) * mm});
            skLineSegment(sketch, "E146.1.1.61", {"start": v(-322.36, 53.12) * mm, "end": v(-322.36, 46.77) * mm});
            skLineSegment(sketch, "E146.1.1.62", {"start": v(-309.66, 65.82) * mm, "end": v(-309.66, 59.47) * mm});
            skLineSegment(sketch, "E146.1.1.63", {"start": v(-296.96, 78.52) * mm, "end": v(-296.96, 72.17) * mm});
            skLineSegment(sketch, "E146.1.1.64", {"start": v(-335.06, 40.42) * mm, "end": v(-335.06, 34.07) * mm});
            skLineSegment(sketch, "E146.1.1.65", {"start": v(-347.76, 46.77) * mm, "end": v(-341.4, 46.77) * mm});
            skLineSegment(sketch, "E146.1.1.66", {"start": v(-347.76, 53.12) * mm, "end": v(-341.4, 53.12) * mm});
            skLineSegment(sketch, "E146.1.1.67", {"start": v(-347.76, 53.12) * mm, "end": v(-347.76, 46.77) * mm});
            skLineSegment(sketch, "E146.1.1.68", {"start": v(-335.06, 84.87) * mm, "end": v(-328.7, 84.87) * mm});
            skLineSegment(sketch, "E146.1.1.69", {"start": v(-335.06, 34.07) * mm, "end": v(-328.7, 34.07) * mm});
            skLineSegment(sketch, "E146.1.1.70", {"start": v(-322.36, 46.77) * mm, "end": v(-316, 46.77) * mm});
            skLineSegment(sketch, "E146.1.1.71", {"start": v(-309.66, 59.47) * mm, "end": v(-303.3, 59.47) * mm});
            skLineSegment(sketch, "E146.1.1.72", {"start": v(-296.96, 72.17) * mm, "end": v(-290.6, 72.17) * mm});
            skLineSegment(sketch, "E146.1.1.73", {"start": v(-347.76, 59.47) * mm, "end": v(-341.4, 59.47) * mm});
            skLineSegment(sketch, "E146.1.1.74", {"start": v(-347.76, 65.82) * mm, "end": v(-347.76, 59.47) * mm});
            skLineSegment(sketch, "E146.1.1.75", {"start": v(-341.4, 53.12) * mm, "end": v(-341.4, 46.77) * mm});
            skLineSegment(sketch, "E146.1.1.76", {"start": v(-328.7, 78.52) * mm, "end": v(-328.7, 72.17) * mm});
            skLineSegment(sketch, "E146.1.1.77", {"start": v(-316, 91.22) * mm, "end": v(-316, 84.87) * mm});
            skLineSegment(sketch, "E146.1.1.78", {"start": v(-316, 40.42) * mm, "end": v(-316, 34.07) * mm});
            skLineSegment(sketch, "E146.1.1.79", {"start": v(-303.3, 53.12) * mm, "end": v(-303.3, 46.77) * mm});
            skLineSegment(sketch, "E146.1.1.80", {"start": v(-290.6, 65.82) * mm, "end": v(-290.6, 59.47) * mm});
            skLineSegment(sketch, "E146.1.1.81", {"start": v(-335.06, 40.42) * mm, "end": v(-328.7, 40.42) * mm});
            skLineSegment(sketch, "E146.1.1.82", {"start": v(-322.36, 53.12) * mm, "end": v(-316, 53.12) * mm});
            skLineSegment(sketch, "E146.1.1.83", {"start": v(-309.66, 65.82) * mm, "end": v(-303.3, 65.82) * mm});
            skLineSegment(sketch, "E146.1.1.84", {"start": v(-296.96, 78.52) * mm, "end": v(-290.6, 78.52) * mm});
            skLineSegment(sketch, "E146.1.1.85", {"start": v(-335.06, 59.47) * mm, "end": v(-328.7, 59.47) * mm});
            skLineSegment(sketch, "E146.1.1.86", {"start": v(-335.06, 65.82) * mm, "end": v(-328.7, 65.82) * mm});
            skLineSegment(sketch, "E146.1.1.87", {"start": v(-335.06, 65.82) * mm, "end": v(-335.06, 59.47) * mm});
            skLineSegment(sketch, "E146.1.1.88", {"start": v(-347.76, 84.87) * mm, "end": v(-335.06, 84.87) * mm, "construction": true});
            skLineSegment(sketch, "E146.1.1.89", {"start": v(-341.4, 78.52) * mm, "end": v(-341.4, 72.17) * mm});
            skLineSegment(sketch, "E146.1.1.90", {"start": v(-341.4, 91.22) * mm, "end": v(-341.4, 84.87) * mm});
            skLineSegment(sketch, "E146.1.1.91", {"start": v(-347.76, 72.17) * mm, "end": v(-341.4, 72.17) * mm});
            skLineSegment(sketch, "E146.1.1.92", {"start": v(-347.76, 78.52) * mm, "end": v(-341.4, 78.52) * mm});
            skLineSegment(sketch, "E146.1.1.93", {"start": v(-347.76, 84.87) * mm, "end": v(-347.76, 72.17) * mm, "construction": true});
            skLineSegment(sketch, "E146.1.1.94", {"start": v(-341.4, 65.82) * mm, "end": v(-341.4, 59.47) * mm});
            skLineSegment(sketch, "E146.1.1.95", {"start": v(-347.76, 65.82) * mm, "end": v(-341.4, 65.82) * mm});
            skLineSegment(sketch, "E146.1.1.96", {"start": v(-335.06, 91.22) * mm, "end": v(-328.7, 91.22) * mm});
            skLineSegment(sketch, "E146.1.1.97", {"start": v(-335.06, 91.22) * mm, "end": v(-335.06, 84.87) * mm});
            skLineSegment(sketch, "E146.1.1.98", {"start": v(-347.76, 91.22) * mm, "end": v(-341.4, 91.22) * mm});
            skLineSegment(sketch, "E146.1.1.99", {"start": v(-347.76, 91.22) * mm, "end": v(-347.76, 84.87) * mm});
            skLineSegment(sketch, "E146.1.1.100", {"start": v(-347.76, 84.87) * mm, "end": v(-341.4, 84.87) * mm});
            skLineSegment(sketch, "E146.1.1.101", {"start": v(-347.76, 78.52) * mm, "end": v(-347.76, 72.17) * mm});
            skLineSegment(sketch, "E146.2.0.0", {"start": v(-109, 326.17) * mm, "end": v(-102.65, 326.17) * mm});
            skLineSegment(sketch, "E146.2.0.1", {"start": v(-96.3, 338.87) * mm, "end": v(-89.95, 338.87) * mm});
            skLineSegment(sketch, "E146.2.0.2", {"start": v(-96.3, 288.07) * mm, "end": v(-89.95, 288.07) * mm});
            skLineSegment(sketch, "E146.2.0.3", {"start": v(-83.6, 300.77) * mm, "end": v(-77.25, 300.77) * mm});
            skLineSegment(sketch, "E146.2.0.4", {"start": v(-109, 332.52) * mm, "end": v(-102.65, 332.52) * mm});
            skLineSegment(sketch, "E146.2.0.5", {"start": v(-96.3, 345.22) * mm, "end": v(-89.95, 345.22) * mm});
            skLineSegment(sketch, "E146.2.0.6", {"start": v(-96.3, 294.42) * mm, "end": v(-89.95, 294.42) * mm});
            skLineSegment(sketch, "E146.2.0.7", {"start": v(-83.6, 307.12) * mm, "end": v(-77.25, 307.12) * mm});
            skLineSegment(sketch, "E146.2.0.8", {"start": v(-109, 332.52) * mm, "end": v(-109, 326.17) * mm});
            skLineSegment(sketch, "E146.2.0.9", {"start": v(-96.3, 345.22) * mm, "end": v(-96.3, 338.87) * mm});
            skLineSegment(sketch, "E146.2.0.10", {"start": v(-96.3, 294.42) * mm, "end": v(-96.3, 288.07) * mm});
            skLineSegment(sketch, "E146.2.0.11", {"start": v(-83.6, 307.12) * mm, "end": v(-83.6, 300.77) * mm});
            skLineSegment(sketch, "E146.2.0.12", {"start": v(-128.05, 294.42) * mm, "end": v(-128.05, 288.07) * mm});
            skLineSegment(sketch, "E146.2.0.13", {"start": v(-115.35, 307.12) * mm, "end": v(-115.35, 300.77) * mm});
            skLineSegment(sketch, "E146.2.0.14", {"start": v(-109, 319.82) * mm, "end": v(-109, 313.47) * mm});
            skLineSegment(sketch, "E146.2.0.15", {"start": v(-96.3, 332.52) * mm, "end": v(-96.3, 326.17) * mm});
            skLineSegment(sketch, "E146.2.0.16", {"start": v(-83.6, 345.22) * mm, "end": v(-83.6, 338.87) * mm});
            skLineSegment(sketch, "E146.2.0.17", {"start": v(-83.6, 294.42) * mm, "end": v(-83.6, 288.07) * mm});
            skLineSegment(sketch, "E146.2.0.18", {"start": v(-134.4, 294.42) * mm, "end": v(-134.4, 288.07) * mm});
            skLineSegment(sketch, "E146.2.0.19", {"start": v(-121.7, 307.12) * mm, "end": v(-121.7, 300.77) * mm});
            skLineSegment(sketch, "E146.2.0.20", {"start": v(-134.4, 288.07) * mm, "end": v(-128.05, 288.07) * mm});
            skLineSegment(sketch, "E146.2.0.21", {"start": v(-121.7, 300.77) * mm, "end": v(-115.35, 300.77) * mm});
            skLineSegment(sketch, "E146.2.0.22", {"start": v(-109, 313.47) * mm, "end": v(-102.65, 313.47) * mm});
            skLineSegment(sketch, "E146.2.0.23", {"start": v(-96.3, 326.17) * mm, "end": v(-89.95, 326.17) * mm});
            skLineSegment(sketch, "E146.2.0.24", {"start": v(-83.6, 338.87) * mm, "end": v(-77.25, 338.87) * mm});
            skLineSegment(sketch, "E146.2.0.25", {"start": v(-83.6, 288.07) * mm, "end": v(-77.25, 288.07) * mm});
            skLineSegment(sketch, "E146.2.0.26", {"start": v(-102.65, 319.82) * mm, "end": v(-102.65, 313.47) * mm});
            skLineSegment(sketch, "E146.2.0.27", {"start": v(-89.95, 332.52) * mm, "end": v(-89.95, 326.17) * mm});
            skLineSegment(sketch, "E146.2.0.28", {"start": v(-77.25, 345.22) * mm, "end": v(-77.25, 338.87) * mm});
            skLineSegment(sketch, "E146.2.0.29", {"start": v(-77.25, 294.42) * mm, "end": v(-77.25, 288.07) * mm});
            skLineSegment(sketch, "E146.2.0.30", {"start": v(-121.7, 332.52) * mm, "end": v(-121.7, 326.17) * mm});
            skLineSegment(sketch, "E146.2.0.31", {"start": v(-109, 345.22) * mm, "end": v(-109, 338.87) * mm});
            skLineSegment(sketch, "E146.2.0.32", {"start": v(-109, 294.42) * mm, "end": v(-109, 288.07) * mm});
            skLineSegment(sketch, "E146.2.0.33", {"start": v(-96.3, 307.12) * mm, "end": v(-96.3, 300.77) * mm});
            skLineSegment(sketch, "E146.2.0.34", {"start": v(-83.6, 319.82) * mm, "end": v(-83.6, 313.47) * mm});
            skLineSegment(sketch, "E146.2.0.35", {"start": v(-83.6, 313.47) * mm, "end": v(-77.25, 313.47) * mm});
            skLineSegment(sketch, "E146.2.0.36", {"start": v(-121.7, 326.17) * mm, "end": v(-115.35, 326.17) * mm});
            skLineSegment(sketch, "E146.2.0.37", {"start": v(-109, 338.87) * mm, "end": v(-102.65, 338.87) * mm});
            skLineSegment(sketch, "E146.2.0.38", {"start": v(-109, 288.07) * mm, "end": v(-102.65, 288.07) * mm});
            skLineSegment(sketch, "E146.2.0.39", {"start": v(-96.3, 300.77) * mm, "end": v(-89.95, 300.77) * mm});
            skLineSegment(sketch, "E146.2.0.40", {"start": v(-115.35, 319.82) * mm, "end": v(-115.35, 313.47) * mm});
            skLineSegment(sketch, "E146.2.0.41", {"start": v(-102.65, 332.52) * mm, "end": v(-102.65, 326.17) * mm});
            skLineSegment(sketch, "E146.2.0.42", {"start": v(-89.95, 345.22) * mm, "end": v(-89.95, 338.87) * mm});
            skLineSegment(sketch, "E146.2.0.43", {"start": v(-89.95, 294.42) * mm, "end": v(-89.95, 288.07) * mm});
            skLineSegment(sketch, "E146.2.0.44", {"start": v(-77.25, 307.12) * mm, "end": v(-77.25, 300.77) * mm});
            skLineSegment(sketch, "E146.2.0.45", {"start": v(-121.7, 332.52) * mm, "end": v(-115.35, 332.52) * mm});
            skLineSegment(sketch, "E146.2.0.46", {"start": v(-109, 345.22) * mm, "end": v(-102.65, 345.22) * mm});
            skLineSegment(sketch, "E146.2.0.47", {"start": v(-109, 294.42) * mm, "end": v(-102.65, 294.42) * mm});
            skLineSegment(sketch, "E146.2.0.48", {"start": v(-96.3, 307.12) * mm, "end": v(-89.95, 307.12) * mm});
            skLineSegment(sketch, "E146.2.0.49", {"start": v(-83.6, 319.82) * mm, "end": v(-77.25, 319.82) * mm});
            skLineSegment(sketch, "E146.2.0.50", {"start": v(-115.35, 345.22) * mm, "end": v(-115.35, 338.87) * mm});
            skLineSegment(sketch, "E146.2.0.51", {"start": v(-115.35, 294.42) * mm, "end": v(-115.35, 288.07) * mm});
            skLineSegment(sketch, "E146.2.0.52", {"start": v(-102.65, 307.12) * mm, "end": v(-102.65, 300.77) * mm});
            skLineSegment(sketch, "E146.2.0.53", {"start": v(-89.95, 319.82) * mm, "end": v(-89.95, 313.47) * mm});
            skLineSegment(sketch, "E146.2.0.54", {"start": v(-77.25, 332.52) * mm, "end": v(-77.25, 326.17) * mm});
            skLineSegment(sketch, "E146.2.0.55", {"start": v(-134.4, 294.42) * mm, "end": v(-128.05, 294.42) * mm});
            skLineSegment(sketch, "E146.2.0.56", {"start": v(-121.7, 307.12) * mm, "end": v(-115.35, 307.12) * mm});
            skLineSegment(sketch, "E146.2.0.57", {"start": v(-109, 319.82) * mm, "end": v(-102.65, 319.82) * mm});
            skLineSegment(sketch, "E146.2.0.58", {"start": v(-96.3, 332.52) * mm, "end": v(-89.95, 332.52) * mm});
            skLineSegment(sketch, "E146.2.0.59", {"start": v(-83.6, 345.22) * mm, "end": v(-77.25, 345.22) * mm});
            skLineSegment(sketch, "E146.2.0.60", {"start": v(-83.6, 294.42) * mm, "end": v(-77.25, 294.42) * mm});
            skLineSegment(sketch, "E146.2.0.61", {"start": v(-109, 307.12) * mm, "end": v(-109, 300.77) * mm});
            skLineSegment(sketch, "E146.2.0.62", {"start": v(-96.3, 319.82) * mm, "end": v(-96.3, 313.47) * mm});
            skLineSegment(sketch, "E146.2.0.63", {"start": v(-83.6, 332.52) * mm, "end": v(-83.6, 326.17) * mm});
            skLineSegment(sketch, "E146.2.0.64", {"start": v(-121.7, 294.42) * mm, "end": v(-121.7, 288.07) * mm});
            skLineSegment(sketch, "E146.2.0.65", {"start": v(-134.4, 300.77) * mm, "end": v(-128.05, 300.77) * mm});
            skLineSegment(sketch, "E146.2.0.66", {"start": v(-134.4, 307.12) * mm, "end": v(-128.05, 307.12) * mm});
            skLineSegment(sketch, "E146.2.0.67", {"start": v(-134.4, 307.12) * mm, "end": v(-134.4, 300.77) * mm});
            skLineSegment(sketch, "E146.2.0.68", {"start": v(-121.7, 338.87) * mm, "end": v(-115.35, 338.87) * mm});
            skLineSegment(sketch, "E146.2.0.69", {"start": v(-121.7, 288.07) * mm, "end": v(-115.35, 288.07) * mm});
            skLineSegment(sketch, "E146.2.0.70", {"start": v(-109, 300.77) * mm, "end": v(-102.65, 300.77) * mm});
            skLineSegment(sketch, "E146.2.0.71", {"start": v(-96.3, 313.47) * mm, "end": v(-89.95, 313.47) * mm});
            skLineSegment(sketch, "E146.2.0.72", {"start": v(-83.6, 326.17) * mm, "end": v(-77.25, 326.17) * mm});
            skLineSegment(sketch, "E146.2.0.73", {"start": v(-134.4, 313.47) * mm, "end": v(-128.05, 313.47) * mm});
            skLineSegment(sketch, "E146.2.0.74", {"start": v(-134.4, 319.82) * mm, "end": v(-134.4, 313.47) * mm});
            skLineSegment(sketch, "E146.2.0.75", {"start": v(-128.05, 307.12) * mm, "end": v(-128.05, 300.77) * mm});
            skLineSegment(sketch, "E146.2.0.76", {"start": v(-115.35, 332.52) * mm, "end": v(-115.35, 326.17) * mm});
            skLineSegment(sketch, "E146.2.0.77", {"start": v(-102.65, 345.22) * mm, "end": v(-102.65, 338.87) * mm});
            skLineSegment(sketch, "E146.2.0.78", {"start": v(-102.65, 294.42) * mm, "end": v(-102.65, 288.07) * mm});
            skLineSegment(sketch, "E146.2.0.79", {"start": v(-89.95, 307.12) * mm, "end": v(-89.95, 300.77) * mm});
            skLineSegment(sketch, "E146.2.0.80", {"start": v(-77.25, 319.82) * mm, "end": v(-77.25, 313.47) * mm});
            skLineSegment(sketch, "E146.2.0.81", {"start": v(-121.7, 294.42) * mm, "end": v(-115.35, 294.42) * mm});
            skLineSegment(sketch, "E146.2.0.82", {"start": v(-109, 307.12) * mm, "end": v(-102.65, 307.12) * mm});
            skLineSegment(sketch, "E146.2.0.83", {"start": v(-96.3, 319.82) * mm, "end": v(-89.95, 319.82) * mm});
            skLineSegment(sketch, "E146.2.0.84", {"start": v(-83.6, 332.52) * mm, "end": v(-77.25, 332.52) * mm});
            skLineSegment(sketch, "E146.2.0.85", {"start": v(-121.7, 313.47) * mm, "end": v(-115.35, 313.47) * mm});
            skLineSegment(sketch, "E146.2.0.86", {"start": v(-121.7, 319.82) * mm, "end": v(-115.35, 319.82) * mm});
            skLineSegment(sketch, "E146.2.0.87", {"start": v(-121.7, 319.82) * mm, "end": v(-121.7, 313.47) * mm});
            skLineSegment(sketch, "E146.2.0.88", {"start": v(-134.4, 338.87) * mm, "end": v(-121.7, 338.87) * mm, "construction": true});
            skLineSegment(sketch, "E146.2.0.89", {"start": v(-128.05, 332.52) * mm, "end": v(-128.05, 326.17) * mm});
            skLineSegment(sketch, "E146.2.0.90", {"start": v(-128.05, 345.22) * mm, "end": v(-128.05, 338.87) * mm});
            skLineSegment(sketch, "E146.2.0.91", {"start": v(-134.4, 326.17) * mm, "end": v(-128.05, 326.17) * mm});
            skLineSegment(sketch, "E146.2.0.92", {"start": v(-134.4, 332.52) * mm, "end": v(-128.05, 332.52) * mm});
            skLineSegment(sketch, "E146.2.0.93", {"start": v(-134.4, 338.87) * mm, "end": v(-134.4, 326.17) * mm, "construction": true});
            skLineSegment(sketch, "E146.2.0.94", {"start": v(-128.05, 319.82) * mm, "end": v(-128.05, 313.47) * mm});
            skLineSegment(sketch, "E146.2.0.95", {"start": v(-134.4, 319.82) * mm, "end": v(-128.05, 319.82) * mm});
            skLineSegment(sketch, "E146.2.0.96", {"start": v(-121.7, 345.22) * mm, "end": v(-115.35, 345.22) * mm});
            skLineSegment(sketch, "E146.2.0.97", {"start": v(-121.7, 345.22) * mm, "end": v(-121.7, 338.87) * mm});
            skLineSegment(sketch, "E146.2.0.98", {"start": v(-134.4, 345.22) * mm, "end": v(-128.05, 345.22) * mm});
            skLineSegment(sketch, "E146.2.0.99", {"start": v(-134.4, 345.22) * mm, "end": v(-134.4, 338.87) * mm});
            skLineSegment(sketch, "E146.2.0.100", {"start": v(-134.4, 338.87) * mm, "end": v(-128.05, 338.87) * mm});
            skLineSegment(sketch, "E146.2.0.101", {"start": v(-134.4, 332.52) * mm, "end": v(-134.4, 326.17) * mm});
            skLineSegment(sketch, "E146.2.1.0", {"start": v(-109, 72.17) * mm, "end": v(-102.65, 72.17) * mm});
            skLineSegment(sketch, "E146.2.1.1", {"start": v(-96.3, 84.87) * mm, "end": v(-89.95, 84.87) * mm});
            skLineSegment(sketch, "E146.2.1.2", {"start": v(-96.3, 34.07) * mm, "end": v(-89.95, 34.07) * mm});
            skLineSegment(sketch, "E146.2.1.3", {"start": v(-83.6, 46.77) * mm, "end": v(-77.25, 46.77) * mm});
            skLineSegment(sketch, "E146.2.1.4", {"start": v(-109, 78.52) * mm, "end": v(-102.65, 78.52) * mm});
            skLineSegment(sketch, "E146.2.1.5", {"start": v(-96.3, 91.22) * mm, "end": v(-89.95, 91.22) * mm});
            skLineSegment(sketch, "E146.2.1.6", {"start": v(-96.3, 40.42) * mm, "end": v(-89.95, 40.42) * mm});
            skLineSegment(sketch, "E146.2.1.7", {"start": v(-83.6, 53.12) * mm, "end": v(-77.25, 53.12) * mm});
            skLineSegment(sketch, "E146.2.1.8", {"start": v(-109, 78.52) * mm, "end": v(-109, 72.17) * mm});
            skLineSegment(sketch, "E146.2.1.9", {"start": v(-96.3, 91.22) * mm, "end": v(-96.3, 84.87) * mm});
            skLineSegment(sketch, "E146.2.1.10", {"start": v(-96.3, 40.42) * mm, "end": v(-96.3, 34.07) * mm});
            skLineSegment(sketch, "E146.2.1.11", {"start": v(-83.6, 53.12) * mm, "end": v(-83.6, 46.77) * mm});
            skLineSegment(sketch, "E146.2.1.12", {"start": v(-128.05, 40.42) * mm, "end": v(-128.05, 34.07) * mm});
            skLineSegment(sketch, "E146.2.1.13", {"start": v(-115.35, 53.12) * mm, "end": v(-115.35, 46.77) * mm});
            skLineSegment(sketch, "E146.2.1.14", {"start": v(-109, 65.82) * mm, "end": v(-109, 59.47) * mm});
            skLineSegment(sketch, "E146.2.1.15", {"start": v(-96.3, 78.52) * mm, "end": v(-96.3, 72.17) * mm});
            skLineSegment(sketch, "E146.2.1.16", {"start": v(-83.6, 91.22) * mm, "end": v(-83.6, 84.87) * mm});
            skLineSegment(sketch, "E146.2.1.17", {"start": v(-83.6, 40.42) * mm, "end": v(-83.6, 34.07) * mm});
            skLineSegment(sketch, "E146.2.1.18", {"start": v(-134.4, 40.42) * mm, "end": v(-134.4, 34.07) * mm});
            skLineSegment(sketch, "E146.2.1.19", {"start": v(-121.7, 53.12) * mm, "end": v(-121.7, 46.77) * mm});
            skLineSegment(sketch, "E146.2.1.20", {"start": v(-134.4, 34.07) * mm, "end": v(-128.05, 34.07) * mm});
            skLineSegment(sketch, "E146.2.1.21", {"start": v(-121.7, 46.77) * mm, "end": v(-115.35, 46.77) * mm});
            skLineSegment(sketch, "E146.2.1.22", {"start": v(-109, 59.47) * mm, "end": v(-102.65, 59.47) * mm});
            skLineSegment(sketch, "E146.2.1.23", {"start": v(-96.3, 72.17) * mm, "end": v(-89.95, 72.17) * mm});
            skLineSegment(sketch, "E146.2.1.24", {"start": v(-83.6, 84.87) * mm, "end": v(-77.25, 84.87) * mm});
            skLineSegment(sketch, "E146.2.1.25", {"start": v(-83.6, 34.07) * mm, "end": v(-77.25, 34.07) * mm});
            skLineSegment(sketch, "E146.2.1.26", {"start": v(-102.65, 65.82) * mm, "end": v(-102.65, 59.47) * mm});
            skLineSegment(sketch, "E146.2.1.27", {"start": v(-89.95, 78.52) * mm, "end": v(-89.95, 72.17) * mm});
            skLineSegment(sketch, "E146.2.1.28", {"start": v(-77.25, 91.22) * mm, "end": v(-77.25, 84.87) * mm});
            skLineSegment(sketch, "E146.2.1.29", {"start": v(-77.25, 40.42) * mm, "end": v(-77.25, 34.07) * mm});
            skLineSegment(sketch, "E146.2.1.30", {"start": v(-121.7, 78.52) * mm, "end": v(-121.7, 72.17) * mm});
            skLineSegment(sketch, "E146.2.1.31", {"start": v(-109, 91.22) * mm, "end": v(-109, 84.87) * mm});
            skLineSegment(sketch, "E146.2.1.32", {"start": v(-109, 40.42) * mm, "end": v(-109, 34.07) * mm});
            skLineSegment(sketch, "E146.2.1.33", {"start": v(-96.3, 53.12) * mm, "end": v(-96.3, 46.77) * mm});
            skLineSegment(sketch, "E146.2.1.34", {"start": v(-83.6, 65.82) * mm, "end": v(-83.6, 59.47) * mm});
            skLineSegment(sketch, "E146.2.1.35", {"start": v(-83.6, 59.47) * mm, "end": v(-77.25, 59.47) * mm});
            skLineSegment(sketch, "E146.2.1.36", {"start": v(-121.7, 72.17) * mm, "end": v(-115.35, 72.17) * mm});
            skLineSegment(sketch, "E146.2.1.37", {"start": v(-109, 84.87) * mm, "end": v(-102.65, 84.87) * mm});
            skLineSegment(sketch, "E146.2.1.38", {"start": v(-109, 34.07) * mm, "end": v(-102.65, 34.07) * mm});
            skLineSegment(sketch, "E146.2.1.39", {"start": v(-96.3, 46.77) * mm, "end": v(-89.95, 46.77) * mm});
            skLineSegment(sketch, "E146.2.1.40", {"start": v(-115.35, 65.82) * mm, "end": v(-115.35, 59.47) * mm});
            skLineSegment(sketch, "E146.2.1.41", {"start": v(-102.65, 78.52) * mm, "end": v(-102.65, 72.17) * mm});
            skLineSegment(sketch, "E146.2.1.42", {"start": v(-89.95, 91.22) * mm, "end": v(-89.95, 84.87) * mm});
            skLineSegment(sketch, "E146.2.1.43", {"start": v(-89.95, 40.42) * mm, "end": v(-89.95, 34.07) * mm});
            skLineSegment(sketch, "E146.2.1.44", {"start": v(-77.25, 53.12) * mm, "end": v(-77.25, 46.77) * mm});
            skLineSegment(sketch, "E146.2.1.45", {"start": v(-121.7, 78.52) * mm, "end": v(-115.35, 78.52) * mm});
            skLineSegment(sketch, "E146.2.1.46", {"start": v(-109, 91.22) * mm, "end": v(-102.65, 91.22) * mm});
            skLineSegment(sketch, "E146.2.1.47", {"start": v(-109, 40.42) * mm, "end": v(-102.65, 40.42) * mm});
            skLineSegment(sketch, "E146.2.1.48", {"start": v(-96.3, 53.12) * mm, "end": v(-89.95, 53.12) * mm});
            skLineSegment(sketch, "E146.2.1.49", {"start": v(-83.6, 65.82) * mm, "end": v(-77.25, 65.82) * mm});
            skLineSegment(sketch, "E146.2.1.50", {"start": v(-115.35, 91.22) * mm, "end": v(-115.35, 84.87) * mm});
            skLineSegment(sketch, "E146.2.1.51", {"start": v(-115.35, 40.42) * mm, "end": v(-115.35, 34.07) * mm});
            skLineSegment(sketch, "E146.2.1.52", {"start": v(-102.65, 53.12) * mm, "end": v(-102.65, 46.77) * mm});
            skLineSegment(sketch, "E146.2.1.53", {"start": v(-89.95, 65.82) * mm, "end": v(-89.95, 59.47) * mm});
            skLineSegment(sketch, "E146.2.1.54", {"start": v(-77.25, 78.52) * mm, "end": v(-77.25, 72.17) * mm});
            skLineSegment(sketch, "E146.2.1.55", {"start": v(-134.4, 40.42) * mm, "end": v(-128.05, 40.42) * mm});
            skLineSegment(sketch, "E146.2.1.56", {"start": v(-121.7, 53.12) * mm, "end": v(-115.35, 53.12) * mm});
            skLineSegment(sketch, "E146.2.1.57", {"start": v(-109, 65.82) * mm, "end": v(-102.65, 65.82) * mm});
            skLineSegment(sketch, "E146.2.1.58", {"start": v(-96.3, 78.52) * mm, "end": v(-89.95, 78.52) * mm});
            skLineSegment(sketch, "E146.2.1.59", {"start": v(-83.6, 91.22) * mm, "end": v(-77.25, 91.22) * mm});
            skLineSegment(sketch, "E146.2.1.60", {"start": v(-83.6, 40.42) * mm, "end": v(-77.25, 40.42) * mm});
            skLineSegment(sketch, "E146.2.1.61", {"start": v(-109, 53.12) * mm, "end": v(-109, 46.77) * mm});
            skLineSegment(sketch, "E146.2.1.62", {"start": v(-96.3, 65.82) * mm, "end": v(-96.3, 59.47) * mm});
            skLineSegment(sketch, "E146.2.1.63", {"start": v(-83.6, 78.52) * mm, "end": v(-83.6, 72.17) * mm});
            skLineSegment(sketch, "E146.2.1.64", {"start": v(-121.7, 40.42) * mm, "end": v(-121.7, 34.07) * mm});
            skLineSegment(sketch, "E146.2.1.65", {"start": v(-134.4, 46.77) * mm, "end": v(-128.05, 46.77) * mm});
            skLineSegment(sketch, "E146.2.1.66", {"start": v(-134.4, 53.12) * mm, "end": v(-128.05, 53.12) * mm});
            skLineSegment(sketch, "E146.2.1.67", {"start": v(-134.4, 53.12) * mm, "end": v(-134.4, 46.77) * mm});
            skLineSegment(sketch, "E146.2.1.68", {"start": v(-121.7, 84.87) * mm, "end": v(-115.35, 84.87) * mm});
            skLineSegment(sketch, "E146.2.1.69", {"start": v(-121.7, 34.07) * mm, "end": v(-115.35, 34.07) * mm});
            skLineSegment(sketch, "E146.2.1.70", {"start": v(-109, 46.77) * mm, "end": v(-102.65, 46.77) * mm});
            skLineSegment(sketch, "E146.2.1.71", {"start": v(-96.3, 59.47) * mm, "end": v(-89.95, 59.47) * mm});
            skLineSegment(sketch, "E146.2.1.72", {"start": v(-83.6, 72.17) * mm, "end": v(-77.25, 72.17) * mm});
            skLineSegment(sketch, "E146.2.1.73", {"start": v(-134.4, 59.47) * mm, "end": v(-128.05, 59.47) * mm});
            skLineSegment(sketch, "E146.2.1.74", {"start": v(-134.4, 65.82) * mm, "end": v(-134.4, 59.47) * mm});
            skLineSegment(sketch, "E146.2.1.75", {"start": v(-128.05, 53.12) * mm, "end": v(-128.05, 46.77) * mm});
            skLineSegment(sketch, "E146.2.1.76", {"start": v(-115.35, 78.52) * mm, "end": v(-115.35, 72.17) * mm});
            skLineSegment(sketch, "E146.2.1.77", {"start": v(-102.65, 91.22) * mm, "end": v(-102.65, 84.87) * mm});
            skLineSegment(sketch, "E146.2.1.78", {"start": v(-102.65, 40.42) * mm, "end": v(-102.65, 34.07) * mm});
            skLineSegment(sketch, "E146.2.1.79", {"start": v(-89.95, 53.12) * mm, "end": v(-89.95, 46.77) * mm});
            skLineSegment(sketch, "E146.2.1.80", {"start": v(-77.25, 65.82) * mm, "end": v(-77.25, 59.47) * mm});
            skLineSegment(sketch, "E146.2.1.81", {"start": v(-121.7, 40.42) * mm, "end": v(-115.35, 40.42) * mm});
            skLineSegment(sketch, "E146.2.1.82", {"start": v(-109, 53.12) * mm, "end": v(-102.65, 53.12) * mm});
            skLineSegment(sketch, "E146.2.1.83", {"start": v(-96.3, 65.82) * mm, "end": v(-89.95, 65.82) * mm});
            skLineSegment(sketch, "E146.2.1.84", {"start": v(-83.6, 78.52) * mm, "end": v(-77.25, 78.52) * mm});
            skLineSegment(sketch, "E146.2.1.85", {"start": v(-121.7, 59.47) * mm, "end": v(-115.35, 59.47) * mm});
            skLineSegment(sketch, "E146.2.1.86", {"start": v(-121.7, 65.82) * mm, "end": v(-115.35, 65.82) * mm});
            skLineSegment(sketch, "E146.2.1.87", {"start": v(-121.7, 65.82) * mm, "end": v(-121.7, 59.47) * mm});
            skLineSegment(sketch, "E146.2.1.88", {"start": v(-134.4, 84.87) * mm, "end": v(-121.7, 84.87) * mm, "construction": true});
            skLineSegment(sketch, "E146.2.1.89", {"start": v(-128.05, 78.52) * mm, "end": v(-128.05, 72.17) * mm});
            skLineSegment(sketch, "E146.2.1.90", {"start": v(-128.05, 91.22) * mm, "end": v(-128.05, 84.87) * mm});
            skLineSegment(sketch, "E146.2.1.91", {"start": v(-134.4, 72.17) * mm, "end": v(-128.05, 72.17) * mm});
            skLineSegment(sketch, "E146.2.1.92", {"start": v(-134.4, 78.52) * mm, "end": v(-128.05, 78.52) * mm});
            skLineSegment(sketch, "E146.2.1.93", {"start": v(-134.4, 84.87) * mm, "end": v(-134.4, 72.17) * mm, "construction": true});
            skLineSegment(sketch, "E146.2.1.94", {"start": v(-128.05, 65.82) * mm, "end": v(-128.05, 59.47) * mm});
            skLineSegment(sketch, "E146.2.1.95", {"start": v(-134.4, 65.82) * mm, "end": v(-128.05, 65.82) * mm});
            skLineSegment(sketch, "E146.2.1.96", {"start": v(-121.7, 91.22) * mm, "end": v(-115.35, 91.22) * mm});
            skLineSegment(sketch, "E146.2.1.97", {"start": v(-121.7, 91.22) * mm, "end": v(-121.7, 84.87) * mm});
            skLineSegment(sketch, "E146.2.1.98", {"start": v(-134.4, 91.22) * mm, "end": v(-128.05, 91.22) * mm});
            skLineSegment(sketch, "E146.2.1.99", {"start": v(-134.4, 91.22) * mm, "end": v(-134.4, 84.87) * mm});
            skLineSegment(sketch, "E146.2.1.100", {"start": v(-134.4, 84.87) * mm, "end": v(-128.05, 84.87) * mm});
            skLineSegment(sketch, "E146.2.1.101", {"start": v(-134.4, 78.52) * mm, "end": v(-134.4, 72.17) * mm});
            skLineSegment(sketch, "E146.3.0.0", {"start": v(104.36, 326.17) * mm, "end": v(110.71, 326.17) * mm});
            skLineSegment(sketch, "E146.3.0.1", {"start": v(117.06, 338.87) * mm, "end": v(123.41, 338.87) * mm});
            skLineSegment(sketch, "E146.3.0.2", {"start": v(117.06, 288.07) * mm, "end": v(123.41, 288.07) * mm});
            skLineSegment(sketch, "E146.3.0.3", {"start": v(129.76, 300.77) * mm, "end": v(136.11, 300.77) * mm});
            skLineSegment(sketch, "E146.3.0.4", {"start": v(104.36, 332.52) * mm, "end": v(110.71, 332.52) * mm});
            skLineSegment(sketch, "E146.3.0.5", {"start": v(117.06, 345.22) * mm, "end": v(123.41, 345.22) * mm});
            skLineSegment(sketch, "E146.3.0.6", {"start": v(117.06, 294.42) * mm, "end": v(123.41, 294.42) * mm});
            skLineSegment(sketch, "E146.3.0.7", {"start": v(129.76, 307.12) * mm, "end": v(136.11, 307.12) * mm});
            skLineSegment(sketch, "E146.3.0.8", {"start": v(104.36, 332.52) * mm, "end": v(104.36, 326.17) * mm});
            skLineSegment(sketch, "E146.3.0.9", {"start": v(117.06, 345.22) * mm, "end": v(117.06, 338.87) * mm});
            skLineSegment(sketch, "E146.3.0.10", {"start": v(117.06, 294.42) * mm, "end": v(117.06, 288.07) * mm});
            skLineSegment(sketch, "E146.3.0.11", {"start": v(129.76, 307.12) * mm, "end": v(129.76, 300.77) * mm});
            skLineSegment(sketch, "E146.3.0.12", {"start": v(85.31, 294.42) * mm, "end": v(85.31, 288.07) * mm});
            skLineSegment(sketch, "E146.3.0.13", {"start": v(98.01, 307.12) * mm, "end": v(98.01, 300.77) * mm});
            skLineSegment(sketch, "E146.3.0.14", {"start": v(104.36, 319.82) * mm, "end": v(104.36, 313.47) * mm});
            skLineSegment(sketch, "E146.3.0.15", {"start": v(117.06, 332.52) * mm, "end": v(117.06, 326.17) * mm});
            skLineSegment(sketch, "E146.3.0.16", {"start": v(129.76, 345.22) * mm, "end": v(129.76, 338.87) * mm});
            skLineSegment(sketch, "E146.3.0.17", {"start": v(129.76, 294.42) * mm, "end": v(129.76, 288.07) * mm});
            skLineSegment(sketch, "E146.3.0.18", {"start": v(78.96, 294.42) * mm, "end": v(78.96, 288.07) * mm});
            skLineSegment(sketch, "E146.3.0.19", {"start": v(91.66, 307.12) * mm, "end": v(91.66, 300.77) * mm});
            skLineSegment(sketch, "E146.3.0.20", {"start": v(78.96, 288.07) * mm, "end": v(85.31, 288.07) * mm});
            skLineSegment(sketch, "E146.3.0.21", {"start": v(91.66, 300.77) * mm, "end": v(98.01, 300.77) * mm});
            skLineSegment(sketch, "E146.3.0.22", {"start": v(104.36, 313.47) * mm, "end": v(110.71, 313.47) * mm});
            skLineSegment(sketch, "E146.3.0.23", {"start": v(117.06, 326.17) * mm, "end": v(123.41, 326.17) * mm});
            skLineSegment(sketch, "E146.3.0.24", {"start": v(129.76, 338.87) * mm, "end": v(136.11, 338.87) * mm});
            skLineSegment(sketch, "E146.3.0.25", {"start": v(129.76, 288.07) * mm, "end": v(136.11, 288.07) * mm});
            skLineSegment(sketch, "E146.3.0.26", {"start": v(110.71, 319.82) * mm, "end": v(110.71, 313.47) * mm});
            skLineSegment(sketch, "E146.3.0.27", {"start": v(123.41, 332.52) * mm, "end": v(123.41, 326.17) * mm});
            skLineSegment(sketch, "E146.3.0.28", {"start": v(136.11, 345.22) * mm, "end": v(136.11, 338.87) * mm});
            skLineSegment(sketch, "E146.3.0.29", {"start": v(136.11, 294.42) * mm, "end": v(136.11, 288.07) * mm});
            skLineSegment(sketch, "E146.3.0.30", {"start": v(91.66, 332.52) * mm, "end": v(91.66, 326.17) * mm});
            skLineSegment(sketch, "E146.3.0.31", {"start": v(104.36, 345.22) * mm, "end": v(104.36, 338.87) * mm});
            skLineSegment(sketch, "E146.3.0.32", {"start": v(104.36, 294.42) * mm, "end": v(104.36, 288.07) * mm});
            skLineSegment(sketch, "E146.3.0.33", {"start": v(117.06, 307.12) * mm, "end": v(117.06, 300.77) * mm});
            skLineSegment(sketch, "E146.3.0.34", {"start": v(129.76, 319.82) * mm, "end": v(129.76, 313.47) * mm});
            skLineSegment(sketch, "E146.3.0.35", {"start": v(129.76, 313.47) * mm, "end": v(136.11, 313.47) * mm});
            skLineSegment(sketch, "E146.3.0.36", {"start": v(91.66, 326.17) * mm, "end": v(98.01, 326.17) * mm});
            skLineSegment(sketch, "E146.3.0.37", {"start": v(104.36, 338.87) * mm, "end": v(110.71, 338.87) * mm});
            skLineSegment(sketch, "E146.3.0.38", {"start": v(104.36, 288.07) * mm, "end": v(110.71, 288.07) * mm});
            skLineSegment(sketch, "E146.3.0.39", {"start": v(117.06, 300.77) * mm, "end": v(123.41, 300.77) * mm});
            skLineSegment(sketch, "E146.3.0.40", {"start": v(98.01, 319.82) * mm, "end": v(98.01, 313.47) * mm});
            skLineSegment(sketch, "E146.3.0.41", {"start": v(110.71, 332.52) * mm, "end": v(110.71, 326.17) * mm});
            skLineSegment(sketch, "E146.3.0.42", {"start": v(123.41, 345.22) * mm, "end": v(123.41, 338.87) * mm});
            skLineSegment(sketch, "E146.3.0.43", {"start": v(123.41, 294.42) * mm, "end": v(123.41, 288.07) * mm});
            skLineSegment(sketch, "E146.3.0.44", {"start": v(136.11, 307.12) * mm, "end": v(136.11, 300.77) * mm});
            skLineSegment(sketch, "E146.3.0.45", {"start": v(91.66, 332.52) * mm, "end": v(98.01, 332.52) * mm});
            skLineSegment(sketch, "E146.3.0.46", {"start": v(104.36, 345.22) * mm, "end": v(110.71, 345.22) * mm});
            skLineSegment(sketch, "E146.3.0.47", {"start": v(104.36, 294.42) * mm, "end": v(110.71, 294.42) * mm});
            skLineSegment(sketch, "E146.3.0.48", {"start": v(117.06, 307.12) * mm, "end": v(123.41, 307.12) * mm});
            skLineSegment(sketch, "E146.3.0.49", {"start": v(129.76, 319.82) * mm, "end": v(136.11, 319.82) * mm});
            skLineSegment(sketch, "E146.3.0.50", {"start": v(98.01, 345.22) * mm, "end": v(98.01, 338.87) * mm});
            skLineSegment(sketch, "E146.3.0.51", {"start": v(98.01, 294.42) * mm, "end": v(98.01, 288.07) * mm});
            skLineSegment(sketch, "E146.3.0.52", {"start": v(110.71, 307.12) * mm, "end": v(110.71, 300.77) * mm});
            skLineSegment(sketch, "E146.3.0.53", {"start": v(123.41, 319.82) * mm, "end": v(123.41, 313.47) * mm});
            skLineSegment(sketch, "E146.3.0.54", {"start": v(136.11, 332.52) * mm, "end": v(136.11, 326.17) * mm});
            skLineSegment(sketch, "E146.3.0.55", {"start": v(78.96, 294.42) * mm, "end": v(85.31, 294.42) * mm});
            skLineSegment(sketch, "E146.3.0.56", {"start": v(91.66, 307.12) * mm, "end": v(98.01, 307.12) * mm});
            skLineSegment(sketch, "E146.3.0.57", {"start": v(104.36, 319.82) * mm, "end": v(110.71, 319.82) * mm});
            skLineSegment(sketch, "E146.3.0.58", {"start": v(117.06, 332.52) * mm, "end": v(123.41, 332.52) * mm});
            skLineSegment(sketch, "E146.3.0.59", {"start": v(129.76, 345.22) * mm, "end": v(136.11, 345.22) * mm});
            skLineSegment(sketch, "E146.3.0.60", {"start": v(129.76, 294.42) * mm, "end": v(136.11, 294.42) * mm});
            skLineSegment(sketch, "E146.3.0.61", {"start": v(104.36, 307.12) * mm, "end": v(104.36, 300.77) * mm});
            skLineSegment(sketch, "E146.3.0.62", {"start": v(117.06, 319.82) * mm, "end": v(117.06, 313.47) * mm});
            skLineSegment(sketch, "E146.3.0.63", {"start": v(129.76, 332.52) * mm, "end": v(129.76, 326.17) * mm});
            skLineSegment(sketch, "E146.3.0.64", {"start": v(91.66, 294.42) * mm, "end": v(91.66, 288.07) * mm});
            skLineSegment(sketch, "E146.3.0.65", {"start": v(78.96, 300.77) * mm, "end": v(85.31, 300.77) * mm});
            skLineSegment(sketch, "E146.3.0.66", {"start": v(78.96, 307.12) * mm, "end": v(85.31, 307.12) * mm});
            skLineSegment(sketch, "E146.3.0.67", {"start": v(78.96, 307.12) * mm, "end": v(78.96, 300.77) * mm});
            skLineSegment(sketch, "E146.3.0.68", {"start": v(91.66, 338.87) * mm, "end": v(98.01, 338.87) * mm});
            skLineSegment(sketch, "E146.3.0.69", {"start": v(91.66, 288.07) * mm, "end": v(98.01, 288.07) * mm});
            skLineSegment(sketch, "E146.3.0.70", {"start": v(104.36, 300.77) * mm, "end": v(110.71, 300.77) * mm});
            skLineSegment(sketch, "E146.3.0.71", {"start": v(117.06, 313.47) * mm, "end": v(123.41, 313.47) * mm});
            skLineSegment(sketch, "E146.3.0.72", {"start": v(129.76, 326.17) * mm, "end": v(136.11, 326.17) * mm});
            skLineSegment(sketch, "E146.3.0.73", {"start": v(78.96, 313.47) * mm, "end": v(85.31, 313.47) * mm});
            skLineSegment(sketch, "E146.3.0.74", {"start": v(78.96, 319.82) * mm, "end": v(78.96, 313.47) * mm});
            skLineSegment(sketch, "E146.3.0.75", {"start": v(85.31, 307.12) * mm, "end": v(85.31, 300.77) * mm});
            skLineSegment(sketch, "E146.3.0.76", {"start": v(98.01, 332.52) * mm, "end": v(98.01, 326.17) * mm});
            skLineSegment(sketch, "E146.3.0.77", {"start": v(110.71, 345.22) * mm, "end": v(110.71, 338.87) * mm});
            skLineSegment(sketch, "E146.3.0.78", {"start": v(110.71, 294.42) * mm, "end": v(110.71, 288.07) * mm});
            skLineSegment(sketch, "E146.3.0.79", {"start": v(123.41, 307.12) * mm, "end": v(123.41, 300.77) * mm});
            skLineSegment(sketch, "E146.3.0.80", {"start": v(136.11, 319.82) * mm, "end": v(136.11, 313.47) * mm});
            skLineSegment(sketch, "E146.3.0.81", {"start": v(91.66, 294.42) * mm, "end": v(98.01, 294.42) * mm});
            skLineSegment(sketch, "E146.3.0.82", {"start": v(104.36, 307.12) * mm, "end": v(110.71, 307.12) * mm});
            skLineSegment(sketch, "E146.3.0.83", {"start": v(117.06, 319.82) * mm, "end": v(123.41, 319.82) * mm});
            skLineSegment(sketch, "E146.3.0.84", {"start": v(129.76, 332.52) * mm, "end": v(136.11, 332.52) * mm});
            skLineSegment(sketch, "E146.3.0.85", {"start": v(91.66, 313.47) * mm, "end": v(98.01, 313.47) * mm});
            skLineSegment(sketch, "E146.3.0.86", {"start": v(91.66, 319.82) * mm, "end": v(98.01, 319.82) * mm});
            skLineSegment(sketch, "E146.3.0.87", {"start": v(91.66, 319.82) * mm, "end": v(91.66, 313.47) * mm});
            skLineSegment(sketch, "E146.3.0.88", {"start": v(78.96, 338.87) * mm, "end": v(91.66, 338.87) * mm, "construction": true});
            skLineSegment(sketch, "E146.3.0.89", {"start": v(85.31, 332.52) * mm, "end": v(85.31, 326.17) * mm});
            skLineSegment(sketch, "E146.3.0.90", {"start": v(85.31, 345.22) * mm, "end": v(85.31, 338.87) * mm});
            skLineSegment(sketch, "E146.3.0.91", {"start": v(78.96, 326.17) * mm, "end": v(85.31, 326.17) * mm});
            skLineSegment(sketch, "E146.3.0.92", {"start": v(78.96, 332.52) * mm, "end": v(85.31, 332.52) * mm});
            skLineSegment(sketch, "E146.3.0.93", {"start": v(78.96, 338.87) * mm, "end": v(78.96, 326.17) * mm, "construction": true});
            skLineSegment(sketch, "E146.3.0.94", {"start": v(85.31, 319.82) * mm, "end": v(85.31, 313.47) * mm});
            skLineSegment(sketch, "E146.3.0.95", {"start": v(78.96, 319.82) * mm, "end": v(85.31, 319.82) * mm});
            skLineSegment(sketch, "E146.3.0.96", {"start": v(91.66, 345.22) * mm, "end": v(98.01, 345.22) * mm});
            skLineSegment(sketch, "E146.3.0.97", {"start": v(91.66, 345.22) * mm, "end": v(91.66, 338.87) * mm});
            skLineSegment(sketch, "E146.3.0.98", {"start": v(78.96, 345.22) * mm, "end": v(85.31, 345.22) * mm});
            skLineSegment(sketch, "E146.3.0.99", {"start": v(78.96, 345.22) * mm, "end": v(78.96, 338.87) * mm});
            skLineSegment(sketch, "E146.3.0.100", {"start": v(78.96, 338.87) * mm, "end": v(85.31, 338.87) * mm});
            skLineSegment(sketch, "E146.3.0.101", {"start": v(78.96, 332.52) * mm, "end": v(78.96, 326.17) * mm});
            skLineSegment(sketch, "E146.3.1.0", {"start": v(104.36, 72.17) * mm, "end": v(110.71, 72.17) * mm});
            skLineSegment(sketch, "E146.3.1.1", {"start": v(117.06, 84.87) * mm, "end": v(123.41, 84.87) * mm});
            skLineSegment(sketch, "E146.3.1.2", {"start": v(117.06, 34.07) * mm, "end": v(123.41, 34.07) * mm});
            skLineSegment(sketch, "E146.3.1.3", {"start": v(129.76, 46.77) * mm, "end": v(136.11, 46.77) * mm});
            skLineSegment(sketch, "E146.3.1.4", {"start": v(104.36, 78.52) * mm, "end": v(110.71, 78.52) * mm});
            skLineSegment(sketch, "E146.3.1.5", {"start": v(117.06, 91.22) * mm, "end": v(123.41, 91.22) * mm});
            skLineSegment(sketch, "E146.3.1.6", {"start": v(117.06, 40.42) * mm, "end": v(123.41, 40.42) * mm});
            skLineSegment(sketch, "E146.3.1.7", {"start": v(129.76, 53.12) * mm, "end": v(136.11, 53.12) * mm});
            skLineSegment(sketch, "E146.3.1.8", {"start": v(104.36, 78.52) * mm, "end": v(104.36, 72.17) * mm});
            skLineSegment(sketch, "E146.3.1.9", {"start": v(117.06, 91.22) * mm, "end": v(117.06, 84.87) * mm});
            skLineSegment(sketch, "E146.3.1.10", {"start": v(117.06, 40.42) * mm, "end": v(117.06, 34.07) * mm});
            skLineSegment(sketch, "E146.3.1.11", {"start": v(129.76, 53.12) * mm, "end": v(129.76, 46.77) * mm});
            skLineSegment(sketch, "E146.3.1.12", {"start": v(85.31, 40.42) * mm, "end": v(85.31, 34.07) * mm});
            skLineSegment(sketch, "E146.3.1.13", {"start": v(98.01, 53.12) * mm, "end": v(98.01, 46.77) * mm});
            skLineSegment(sketch, "E146.3.1.14", {"start": v(104.36, 65.82) * mm, "end": v(104.36, 59.47) * mm});
            skLineSegment(sketch, "E146.3.1.15", {"start": v(117.06, 78.52) * mm, "end": v(117.06, 72.17) * mm});
            skLineSegment(sketch, "E146.3.1.16", {"start": v(129.76, 91.22) * mm, "end": v(129.76, 84.87) * mm});
            skLineSegment(sketch, "E146.3.1.17", {"start": v(129.76, 40.42) * mm, "end": v(129.76, 34.07) * mm});
            skLineSegment(sketch, "E146.3.1.18", {"start": v(78.96, 40.42) * mm, "end": v(78.96, 34.07) * mm});
            skLineSegment(sketch, "E146.3.1.19", {"start": v(91.66, 53.12) * mm, "end": v(91.66, 46.77) * mm});
            skLineSegment(sketch, "E146.3.1.20", {"start": v(78.96, 34.07) * mm, "end": v(85.31, 34.07) * mm});
            skLineSegment(sketch, "E146.3.1.21", {"start": v(91.66, 46.77) * mm, "end": v(98.01, 46.77) * mm});
            skLineSegment(sketch, "E146.3.1.22", {"start": v(104.36, 59.47) * mm, "end": v(110.71, 59.47) * mm});
            skLineSegment(sketch, "E146.3.1.23", {"start": v(117.06, 72.17) * mm, "end": v(123.41, 72.17) * mm});
            skLineSegment(sketch, "E146.3.1.24", {"start": v(129.76, 84.87) * mm, "end": v(136.11, 84.87) * mm});
            skLineSegment(sketch, "E146.3.1.25", {"start": v(129.76, 34.07) * mm, "end": v(136.11, 34.07) * mm});
            skLineSegment(sketch, "E146.3.1.26", {"start": v(110.71, 65.82) * mm, "end": v(110.71, 59.47) * mm});
            skLineSegment(sketch, "E146.3.1.27", {"start": v(123.41, 78.52) * mm, "end": v(123.41, 72.17) * mm});
            skLineSegment(sketch, "E146.3.1.28", {"start": v(136.11, 91.22) * mm, "end": v(136.11, 84.87) * mm});
            skLineSegment(sketch, "E146.3.1.29", {"start": v(136.11, 40.42) * mm, "end": v(136.11, 34.07) * mm});
            skLineSegment(sketch, "E146.3.1.30", {"start": v(91.66, 78.52) * mm, "end": v(91.66, 72.17) * mm});
            skLineSegment(sketch, "E146.3.1.31", {"start": v(104.36, 91.22) * mm, "end": v(104.36, 84.87) * mm});
            skLineSegment(sketch, "E146.3.1.32", {"start": v(104.36, 40.42) * mm, "end": v(104.36, 34.07) * mm});
            skLineSegment(sketch, "E146.3.1.33", {"start": v(117.06, 53.12) * mm, "end": v(117.06, 46.77) * mm});
            skLineSegment(sketch, "E146.3.1.34", {"start": v(129.76, 65.82) * mm, "end": v(129.76, 59.47) * mm});
            skLineSegment(sketch, "E146.3.1.35", {"start": v(129.76, 59.47) * mm, "end": v(136.11, 59.47) * mm});
            skLineSegment(sketch, "E146.3.1.36", {"start": v(91.66, 72.17) * mm, "end": v(98.01, 72.17) * mm});
            skLineSegment(sketch, "E146.3.1.37", {"start": v(104.36, 84.87) * mm, "end": v(110.71, 84.87) * mm});
            skLineSegment(sketch, "E146.3.1.38", {"start": v(104.36, 34.07) * mm, "end": v(110.71, 34.07) * mm});
            skLineSegment(sketch, "E146.3.1.39", {"start": v(117.06, 46.77) * mm, "end": v(123.41, 46.77) * mm});
            skLineSegment(sketch, "E146.3.1.40", {"start": v(98.01, 65.82) * mm, "end": v(98.01, 59.47) * mm});
            skLineSegment(sketch, "E146.3.1.41", {"start": v(110.71, 78.52) * mm, "end": v(110.71, 72.17) * mm});
            skLineSegment(sketch, "E146.3.1.42", {"start": v(123.41, 91.22) * mm, "end": v(123.41, 84.87) * mm});
            skLineSegment(sketch, "E146.3.1.43", {"start": v(123.41, 40.42) * mm, "end": v(123.41, 34.07) * mm});
            skLineSegment(sketch, "E146.3.1.44", {"start": v(136.11, 53.12) * mm, "end": v(136.11, 46.77) * mm});
            skLineSegment(sketch, "E146.3.1.45", {"start": v(91.66, 78.52) * mm, "end": v(98.01, 78.52) * mm});
            skLineSegment(sketch, "E146.3.1.46", {"start": v(104.36, 91.22) * mm, "end": v(110.71, 91.22) * mm});
            skLineSegment(sketch, "E146.3.1.47", {"start": v(104.36, 40.42) * mm, "end": v(110.71, 40.42) * mm});
            skLineSegment(sketch, "E146.3.1.48", {"start": v(117.06, 53.12) * mm, "end": v(123.41, 53.12) * mm});
            skLineSegment(sketch, "E146.3.1.49", {"start": v(129.76, 65.82) * mm, "end": v(136.11, 65.82) * mm});
            skLineSegment(sketch, "E146.3.1.50", {"start": v(98.01, 91.22) * mm, "end": v(98.01, 84.87) * mm});
            skLineSegment(sketch, "E146.3.1.51", {"start": v(98.01, 40.42) * mm, "end": v(98.01, 34.07) * mm});
            skLineSegment(sketch, "E146.3.1.52", {"start": v(110.71, 53.12) * mm, "end": v(110.71, 46.77) * mm});
            skLineSegment(sketch, "E146.3.1.53", {"start": v(123.41, 65.82) * mm, "end": v(123.41, 59.47) * mm});
            skLineSegment(sketch, "E146.3.1.54", {"start": v(136.11, 78.52) * mm, "end": v(136.11, 72.17) * mm});
            skLineSegment(sketch, "E146.3.1.55", {"start": v(78.96, 40.42) * mm, "end": v(85.31, 40.42) * mm});
            skLineSegment(sketch, "E146.3.1.56", {"start": v(91.66, 53.12) * mm, "end": v(98.01, 53.12) * mm});
            skLineSegment(sketch, "E146.3.1.57", {"start": v(104.36, 65.82) * mm, "end": v(110.71, 65.82) * mm});
            skLineSegment(sketch, "E146.3.1.58", {"start": v(117.06, 78.52) * mm, "end": v(123.41, 78.52) * mm});
            skLineSegment(sketch, "E146.3.1.59", {"start": v(129.76, 91.22) * mm, "end": v(136.11, 91.22) * mm});
            skLineSegment(sketch, "E146.3.1.60", {"start": v(129.76, 40.42) * mm, "end": v(136.11, 40.42) * mm});
            skLineSegment(sketch, "E146.3.1.61", {"start": v(104.36, 53.12) * mm, "end": v(104.36, 46.77) * mm});
            skLineSegment(sketch, "E146.3.1.62", {"start": v(117.06, 65.82) * mm, "end": v(117.06, 59.47) * mm});
            skLineSegment(sketch, "E146.3.1.63", {"start": v(129.76, 78.52) * mm, "end": v(129.76, 72.17) * mm});
            skLineSegment(sketch, "E146.3.1.64", {"start": v(91.66, 40.42) * mm, "end": v(91.66, 34.07) * mm});
            skLineSegment(sketch, "E146.3.1.65", {"start": v(78.96, 46.77) * mm, "end": v(85.31, 46.77) * mm});
            skLineSegment(sketch, "E146.3.1.66", {"start": v(78.96, 53.12) * mm, "end": v(85.31, 53.12) * mm});
            skLineSegment(sketch, "E146.3.1.67", {"start": v(78.96, 53.12) * mm, "end": v(78.96, 46.77) * mm});
            skLineSegment(sketch, "E146.3.1.68", {"start": v(91.66, 84.87) * mm, "end": v(98.01, 84.87) * mm});
            skLineSegment(sketch, "E146.3.1.69", {"start": v(91.66, 34.07) * mm, "end": v(98.01, 34.07) * mm});
            skLineSegment(sketch, "E146.3.1.70", {"start": v(104.36, 46.77) * mm, "end": v(110.71, 46.77) * mm});
            skLineSegment(sketch, "E146.3.1.71", {"start": v(117.06, 59.47) * mm, "end": v(123.41, 59.47) * mm});
            skLineSegment(sketch, "E146.3.1.72", {"start": v(129.76, 72.17) * mm, "end": v(136.11, 72.17) * mm});
            skLineSegment(sketch, "E146.3.1.73", {"start": v(78.96, 59.47) * mm, "end": v(85.31, 59.47) * mm});
            skLineSegment(sketch, "E146.3.1.74", {"start": v(78.96, 65.82) * mm, "end": v(78.96, 59.47) * mm});
            skLineSegment(sketch, "E146.3.1.75", {"start": v(85.31, 53.12) * mm, "end": v(85.31, 46.77) * mm});
            skLineSegment(sketch, "E146.3.1.76", {"start": v(98.01, 78.52) * mm, "end": v(98.01, 72.17) * mm});
            skLineSegment(sketch, "E146.3.1.77", {"start": v(110.71, 91.22) * mm, "end": v(110.71, 84.87) * mm});
            skLineSegment(sketch, "E146.3.1.78", {"start": v(110.71, 40.42) * mm, "end": v(110.71, 34.07) * mm});
            skLineSegment(sketch, "E146.3.1.79", {"start": v(123.41, 53.12) * mm, "end": v(123.41, 46.77) * mm});
            skLineSegment(sketch, "E146.3.1.80", {"start": v(136.11, 65.82) * mm, "end": v(136.11, 59.47) * mm});
            skLineSegment(sketch, "E146.3.1.81", {"start": v(91.66, 40.42) * mm, "end": v(98.01, 40.42) * mm});
            skLineSegment(sketch, "E146.3.1.82", {"start": v(104.36, 53.12) * mm, "end": v(110.71, 53.12) * mm});
            skLineSegment(sketch, "E146.3.1.83", {"start": v(117.06, 65.82) * mm, "end": v(123.41, 65.82) * mm});
            skLineSegment(sketch, "E146.3.1.84", {"start": v(129.76, 78.52) * mm, "end": v(136.11, 78.52) * mm});
            skLineSegment(sketch, "E146.3.1.85", {"start": v(91.66, 59.47) * mm, "end": v(98.01, 59.47) * mm});
            skLineSegment(sketch, "E146.3.1.86", {"start": v(91.66, 65.82) * mm, "end": v(98.01, 65.82) * mm});
            skLineSegment(sketch, "E146.3.1.87", {"start": v(91.66, 65.82) * mm, "end": v(91.66, 59.47) * mm});
            skLineSegment(sketch, "E146.3.1.88", {"start": v(78.96, 84.87) * mm, "end": v(91.66, 84.87) * mm, "construction": true});
            skLineSegment(sketch, "E146.3.1.89", {"start": v(85.31, 78.52) * mm, "end": v(85.31, 72.17) * mm});
            skLineSegment(sketch, "E146.3.1.90", {"start": v(85.31, 91.22) * mm, "end": v(85.31, 84.87) * mm});
            skLineSegment(sketch, "E146.3.1.91", {"start": v(78.96, 72.17) * mm, "end": v(85.31, 72.17) * mm});
            skLineSegment(sketch, "E146.3.1.92", {"start": v(78.96, 78.52) * mm, "end": v(85.31, 78.52) * mm});
            skLineSegment(sketch, "E146.3.1.93", {"start": v(78.96, 84.87) * mm, "end": v(78.96, 72.17) * mm, "construction": true});
            skLineSegment(sketch, "E146.3.1.94", {"start": v(85.31, 65.82) * mm, "end": v(85.31, 59.47) * mm});
            skLineSegment(sketch, "E146.3.1.95", {"start": v(78.96, 65.82) * mm, "end": v(85.31, 65.82) * mm});
            skLineSegment(sketch, "E146.3.1.96", {"start": v(91.66, 91.22) * mm, "end": v(98.01, 91.22) * mm});
            skLineSegment(sketch, "E146.3.1.97", {"start": v(91.66, 91.22) * mm, "end": v(91.66, 84.87) * mm});
            skLineSegment(sketch, "E146.3.1.98", {"start": v(78.96, 91.22) * mm, "end": v(85.31, 91.22) * mm});
            skLineSegment(sketch, "E146.3.1.99", {"start": v(78.96, 91.22) * mm, "end": v(78.96, 84.87) * mm});
            skLineSegment(sketch, "E146.3.1.100", {"start": v(78.96, 84.87) * mm, "end": v(85.31, 84.87) * mm});
            skLineSegment(sketch, "E146.3.1.101", {"start": v(78.96, 78.52) * mm, "end": v(78.96, 72.17) * mm});
            skLineSegment(sketch, "E146.4.0.0", {"start": v(317.72, 326.17) * mm, "end": v(324.07, 326.17) * mm});
            skLineSegment(sketch, "E146.4.0.1", {"start": v(330.42, 338.87) * mm, "end": v(336.77, 338.87) * mm});
            skLineSegment(sketch, "E146.4.0.2", {"start": v(330.42, 288.07) * mm, "end": v(336.77, 288.07) * mm});
            skLineSegment(sketch, "E146.4.0.3", {"start": v(343.12, 300.77) * mm, "end": v(349.47, 300.77) * mm});
            skLineSegment(sketch, "E146.4.0.4", {"start": v(317.72, 332.52) * mm, "end": v(324.07, 332.52) * mm});
            skLineSegment(sketch, "E146.4.0.5", {"start": v(330.42, 345.22) * mm, "end": v(336.77, 345.22) * mm});
            skLineSegment(sketch, "E146.4.0.6", {"start": v(330.42, 294.42) * mm, "end": v(336.77, 294.42) * mm});
            skLineSegment(sketch, "E146.4.0.7", {"start": v(343.12, 307.12) * mm, "end": v(349.47, 307.12) * mm});
            skLineSegment(sketch, "E146.4.0.8", {"start": v(317.72, 332.52) * mm, "end": v(317.72, 326.17) * mm});
            skLineSegment(sketch, "E146.4.0.9", {"start": v(330.42, 345.22) * mm, "end": v(330.42, 338.87) * mm});
            skLineSegment(sketch, "E146.4.0.10", {"start": v(330.42, 294.42) * mm, "end": v(330.42, 288.07) * mm});
            skLineSegment(sketch, "E146.4.0.11", {"start": v(343.12, 307.12) * mm, "end": v(343.12, 300.77) * mm});
            skLineSegment(sketch, "E146.4.0.12", {"start": v(298.67, 294.42) * mm, "end": v(298.67, 288.07) * mm});
            skLineSegment(sketch, "E146.4.0.13", {"start": v(311.37, 307.12) * mm, "end": v(311.37, 300.77) * mm});
            skLineSegment(sketch, "E146.4.0.14", {"start": v(317.72, 319.82) * mm, "end": v(317.72, 313.47) * mm});
            skLineSegment(sketch, "E146.4.0.15", {"start": v(330.42, 332.52) * mm, "end": v(330.42, 326.17) * mm});
            skLineSegment(sketch, "E146.4.0.16", {"start": v(343.12, 345.22) * mm, "end": v(343.12, 338.87) * mm});
            skLineSegment(sketch, "E146.4.0.17", {"start": v(343.12, 294.42) * mm, "end": v(343.12, 288.07) * mm});
            skLineSegment(sketch, "E146.4.0.18", {"start": v(292.32, 294.42) * mm, "end": v(292.32, 288.07) * mm});
            skLineSegment(sketch, "E146.4.0.19", {"start": v(305.02, 307.12) * mm, "end": v(305.02, 300.77) * mm});
            skLineSegment(sketch, "E146.4.0.20", {"start": v(292.32, 288.07) * mm, "end": v(298.67, 288.07) * mm});
            skLineSegment(sketch, "E146.4.0.21", {"start": v(305.02, 300.77) * mm, "end": v(311.37, 300.77) * mm});
            skLineSegment(sketch, "E146.4.0.22", {"start": v(317.72, 313.47) * mm, "end": v(324.07, 313.47) * mm});
            skLineSegment(sketch, "E146.4.0.23", {"start": v(330.42, 326.17) * mm, "end": v(336.77, 326.17) * mm});
            skLineSegment(sketch, "E146.4.0.24", {"start": v(343.12, 338.87) * mm, "end": v(349.47, 338.87) * mm});
            skLineSegment(sketch, "E146.4.0.25", {"start": v(343.12, 288.07) * mm, "end": v(349.47, 288.07) * mm});
            skLineSegment(sketch, "E146.4.0.26", {"start": v(324.07, 319.82) * mm, "end": v(324.07, 313.47) * mm});
            skLineSegment(sketch, "E146.4.0.27", {"start": v(336.77, 332.52) * mm, "end": v(336.77, 326.17) * mm});
            skLineSegment(sketch, "E146.4.0.28", {"start": v(349.47, 345.22) * mm, "end": v(349.47, 338.87) * mm});
            skLineSegment(sketch, "E146.4.0.29", {"start": v(349.47, 294.42) * mm, "end": v(349.47, 288.07) * mm});
            skLineSegment(sketch, "E146.4.0.30", {"start": v(305.02, 332.52) * mm, "end": v(305.02, 326.17) * mm});
            skLineSegment(sketch, "E146.4.0.31", {"start": v(317.72, 345.22) * mm, "end": v(317.72, 338.87) * mm});
            skLineSegment(sketch, "E146.4.0.32", {"start": v(317.72, 294.42) * mm, "end": v(317.72, 288.07) * mm});
            skLineSegment(sketch, "E146.4.0.33", {"start": v(330.42, 307.12) * mm, "end": v(330.42, 300.77) * mm});
            skLineSegment(sketch, "E146.4.0.34", {"start": v(343.12, 319.82) * mm, "end": v(343.12, 313.47) * mm});
            skLineSegment(sketch, "E146.4.0.35", {"start": v(343.12, 313.47) * mm, "end": v(349.47, 313.47) * mm});
            skLineSegment(sketch, "E146.4.0.36", {"start": v(305.02, 326.17) * mm, "end": v(311.37, 326.17) * mm});
            skLineSegment(sketch, "E146.4.0.37", {"start": v(317.72, 338.87) * mm, "end": v(324.07, 338.87) * mm});
            skLineSegment(sketch, "E146.4.0.38", {"start": v(317.72, 288.07) * mm, "end": v(324.07, 288.07) * mm});
            skLineSegment(sketch, "E146.4.0.39", {"start": v(330.42, 300.77) * mm, "end": v(336.77, 300.77) * mm});
            skLineSegment(sketch, "E146.4.0.40", {"start": v(311.37, 319.82) * mm, "end": v(311.37, 313.47) * mm});
            skLineSegment(sketch, "E146.4.0.41", {"start": v(324.07, 332.52) * mm, "end": v(324.07, 326.17) * mm});
            skLineSegment(sketch, "E146.4.0.42", {"start": v(336.77, 345.22) * mm, "end": v(336.77, 338.87) * mm});
            skLineSegment(sketch, "E146.4.0.43", {"start": v(336.77, 294.42) * mm, "end": v(336.77, 288.07) * mm});
            skLineSegment(sketch, "E146.4.0.44", {"start": v(349.47, 307.12) * mm, "end": v(349.47, 300.77) * mm});
            skLineSegment(sketch, "E146.4.0.45", {"start": v(305.02, 332.52) * mm, "end": v(311.37, 332.52) * mm});
            skLineSegment(sketch, "E146.4.0.46", {"start": v(317.72, 345.22) * mm, "end": v(324.07, 345.22) * mm});
            skLineSegment(sketch, "E146.4.0.47", {"start": v(317.72, 294.42) * mm, "end": v(324.07, 294.42) * mm});
            skLineSegment(sketch, "E146.4.0.48", {"start": v(330.42, 307.12) * mm, "end": v(336.77, 307.12) * mm});
            skLineSegment(sketch, "E146.4.0.49", {"start": v(343.12, 319.82) * mm, "end": v(349.47, 319.82) * mm});
            skLineSegment(sketch, "E146.4.0.50", {"start": v(311.37, 345.22) * mm, "end": v(311.37, 338.87) * mm});
            skLineSegment(sketch, "E146.4.0.51", {"start": v(311.37, 294.42) * mm, "end": v(311.37, 288.07) * mm});
            skLineSegment(sketch, "E146.4.0.52", {"start": v(324.07, 307.12) * mm, "end": v(324.07, 300.77) * mm});
            skLineSegment(sketch, "E146.4.0.53", {"start": v(336.77, 319.82) * mm, "end": v(336.77, 313.47) * mm});
            skLineSegment(sketch, "E146.4.0.54", {"start": v(349.47, 332.52) * mm, "end": v(349.47, 326.17) * mm});
            skLineSegment(sketch, "E146.4.0.55", {"start": v(292.32, 294.42) * mm, "end": v(298.67, 294.42) * mm});
            skLineSegment(sketch, "E146.4.0.56", {"start": v(305.02, 307.12) * mm, "end": v(311.37, 307.12) * mm});
            skLineSegment(sketch, "E146.4.0.57", {"start": v(317.72, 319.82) * mm, "end": v(324.07, 319.82) * mm});
            skLineSegment(sketch, "E146.4.0.58", {"start": v(330.42, 332.52) * mm, "end": v(336.77, 332.52) * mm});
            skLineSegment(sketch, "E146.4.0.59", {"start": v(343.12, 345.22) * mm, "end": v(349.47, 345.22) * mm});
            skLineSegment(sketch, "E146.4.0.60", {"start": v(343.12, 294.42) * mm, "end": v(349.47, 294.42) * mm});
            skLineSegment(sketch, "E146.4.0.61", {"start": v(317.72, 307.12) * mm, "end": v(317.72, 300.77) * mm});
            skLineSegment(sketch, "E146.4.0.62", {"start": v(330.42, 319.82) * mm, "end": v(330.42, 313.47) * mm});
            skLineSegment(sketch, "E146.4.0.63", {"start": v(343.12, 332.52) * mm, "end": v(343.12, 326.17) * mm});
            skLineSegment(sketch, "E146.4.0.64", {"start": v(305.02, 294.42) * mm, "end": v(305.02, 288.07) * mm});
            skLineSegment(sketch, "E146.4.0.65", {"start": v(292.32, 300.77) * mm, "end": v(298.67, 300.77) * mm});
            skLineSegment(sketch, "E146.4.0.66", {"start": v(292.32, 307.12) * mm, "end": v(298.67, 307.12) * mm});
            skLineSegment(sketch, "E146.4.0.67", {"start": v(292.32, 307.12) * mm, "end": v(292.32, 300.77) * mm});
            skLineSegment(sketch, "E146.4.0.68", {"start": v(305.02, 338.87) * mm, "end": v(311.37, 338.87) * mm});
            skLineSegment(sketch, "E146.4.0.69", {"start": v(305.02, 288.07) * mm, "end": v(311.37, 288.07) * mm});
            skLineSegment(sketch, "E146.4.0.70", {"start": v(317.72, 300.77) * mm, "end": v(324.07, 300.77) * mm});
            skLineSegment(sketch, "E146.4.0.71", {"start": v(330.42, 313.47) * mm, "end": v(336.77, 313.47) * mm});
            skLineSegment(sketch, "E146.4.0.72", {"start": v(343.12, 326.17) * mm, "end": v(349.47, 326.17) * mm});
            skLineSegment(sketch, "E146.4.0.73", {"start": v(292.32, 313.47) * mm, "end": v(298.67, 313.47) * mm});
            skLineSegment(sketch, "E146.4.0.74", {"start": v(292.32, 319.82) * mm, "end": v(292.32, 313.47) * mm});
            skLineSegment(sketch, "E146.4.0.75", {"start": v(298.67, 307.12) * mm, "end": v(298.67, 300.77) * mm});
            skLineSegment(sketch, "E146.4.0.76", {"start": v(311.37, 332.52) * mm, "end": v(311.37, 326.17) * mm});
            skLineSegment(sketch, "E146.4.0.77", {"start": v(324.07, 345.22) * mm, "end": v(324.07, 338.87) * mm});
            skLineSegment(sketch, "E146.4.0.78", {"start": v(324.07, 294.42) * mm, "end": v(324.07, 288.07) * mm});
            skLineSegment(sketch, "E146.4.0.79", {"start": v(336.77, 307.12) * mm, "end": v(336.77, 300.77) * mm});
            skLineSegment(sketch, "E146.4.0.80", {"start": v(349.47, 319.82) * mm, "end": v(349.47, 313.47) * mm});
            skLineSegment(sketch, "E146.4.0.81", {"start": v(305.02, 294.42) * mm, "end": v(311.37, 294.42) * mm});
            skLineSegment(sketch, "E146.4.0.82", {"start": v(317.72, 307.12) * mm, "end": v(324.07, 307.12) * mm});
            skLineSegment(sketch, "E146.4.0.83", {"start": v(330.42, 319.82) * mm, "end": v(336.77, 319.82) * mm});
            skLineSegment(sketch, "E146.4.0.84", {"start": v(343.12, 332.52) * mm, "end": v(349.47, 332.52) * mm});
            skLineSegment(sketch, "E146.4.0.85", {"start": v(305.02, 313.47) * mm, "end": v(311.37, 313.47) * mm});
            skLineSegment(sketch, "E146.4.0.86", {"start": v(305.02, 319.82) * mm, "end": v(311.37, 319.82) * mm});
            skLineSegment(sketch, "E146.4.0.87", {"start": v(305.02, 319.82) * mm, "end": v(305.02, 313.47) * mm});
            skLineSegment(sketch, "E146.4.0.88", {"start": v(292.32, 338.87) * mm, "end": v(305.02, 338.87) * mm, "construction": true});
            skLineSegment(sketch, "E146.4.0.89", {"start": v(298.67, 332.52) * mm, "end": v(298.67, 326.17) * mm});
            skLineSegment(sketch, "E146.4.0.90", {"start": v(298.67, 345.22) * mm, "end": v(298.67, 338.87) * mm});
            skLineSegment(sketch, "E146.4.0.91", {"start": v(292.32, 326.17) * mm, "end": v(298.67, 326.17) * mm});
            skLineSegment(sketch, "E146.4.0.92", {"start": v(292.32, 332.52) * mm, "end": v(298.67, 332.52) * mm});
            skLineSegment(sketch, "E146.4.0.93", {"start": v(292.32, 338.87) * mm, "end": v(292.32, 326.17) * mm, "construction": true});
            skLineSegment(sketch, "E146.4.0.94", {"start": v(298.67, 319.82) * mm, "end": v(298.67, 313.47) * mm});
            skLineSegment(sketch, "E146.4.0.95", {"start": v(292.32, 319.82) * mm, "end": v(298.67, 319.82) * mm});
            skLineSegment(sketch, "E146.4.0.96", {"start": v(305.02, 345.22) * mm, "end": v(311.37, 345.22) * mm});
            skLineSegment(sketch, "E146.4.0.97", {"start": v(305.02, 345.22) * mm, "end": v(305.02, 338.87) * mm});
            skLineSegment(sketch, "E146.4.0.98", {"start": v(292.32, 345.22) * mm, "end": v(298.67, 345.22) * mm});
            skLineSegment(sketch, "E146.4.0.99", {"start": v(292.32, 345.22) * mm, "end": v(292.32, 338.87) * mm});
            skLineSegment(sketch, "E146.4.0.100", {"start": v(292.32, 338.87) * mm, "end": v(298.67, 338.87) * mm});
            skLineSegment(sketch, "E146.4.0.101", {"start": v(292.32, 332.52) * mm, "end": v(292.32, 326.17) * mm});
            skLineSegment(sketch, "E146.4.1.0", {"start": v(317.72, 72.17) * mm, "end": v(324.07, 72.17) * mm});
            skLineSegment(sketch, "E146.4.1.1", {"start": v(330.42, 84.87) * mm, "end": v(336.77, 84.87) * mm});
            skLineSegment(sketch, "E146.4.1.2", {"start": v(330.42, 34.07) * mm, "end": v(336.77, 34.07) * mm});
            skLineSegment(sketch, "E146.4.1.3", {"start": v(343.12, 46.77) * mm, "end": v(349.47, 46.77) * mm});
            skLineSegment(sketch, "E146.4.1.4", {"start": v(317.72, 78.52) * mm, "end": v(324.07, 78.52) * mm});
            skLineSegment(sketch, "E146.4.1.5", {"start": v(330.42, 91.22) * mm, "end": v(336.77, 91.22) * mm});
            skLineSegment(sketch, "E146.4.1.6", {"start": v(330.42, 40.42) * mm, "end": v(336.77, 40.42) * mm});
            skLineSegment(sketch, "E146.4.1.7", {"start": v(343.12, 53.12) * mm, "end": v(349.47, 53.12) * mm});
            skLineSegment(sketch, "E146.4.1.8", {"start": v(317.72, 78.52) * mm, "end": v(317.72, 72.17) * mm});
            skLineSegment(sketch, "E146.4.1.9", {"start": v(330.42, 91.22) * mm, "end": v(330.42, 84.87) * mm});
            skLineSegment(sketch, "E146.4.1.10", {"start": v(330.42, 40.42) * mm, "end": v(330.42, 34.07) * mm});
            skLineSegment(sketch, "E146.4.1.11", {"start": v(343.12, 53.12) * mm, "end": v(343.12, 46.77) * mm});
            skLineSegment(sketch, "E146.4.1.12", {"start": v(298.67, 40.42) * mm, "end": v(298.67, 34.07) * mm});
            skLineSegment(sketch, "E146.4.1.13", {"start": v(311.37, 53.12) * mm, "end": v(311.37, 46.77) * mm});
            skLineSegment(sketch, "E146.4.1.14", {"start": v(317.72, 65.82) * mm, "end": v(317.72, 59.47) * mm});
            skLineSegment(sketch, "E146.4.1.15", {"start": v(330.42, 78.52) * mm, "end": v(330.42, 72.17) * mm});
            skLineSegment(sketch, "E146.4.1.16", {"start": v(343.12, 91.22) * mm, "end": v(343.12, 84.87) * mm});
            skLineSegment(sketch, "E146.4.1.17", {"start": v(343.12, 40.42) * mm, "end": v(343.12, 34.07) * mm});
            skLineSegment(sketch, "E146.4.1.18", {"start": v(292.32, 40.42) * mm, "end": v(292.32, 34.07) * mm});
            skLineSegment(sketch, "E146.4.1.19", {"start": v(305.02, 53.12) * mm, "end": v(305.02, 46.77) * mm});
            skLineSegment(sketch, "E146.4.1.20", {"start": v(292.32, 34.07) * mm, "end": v(298.67, 34.07) * mm});
            skLineSegment(sketch, "E146.4.1.21", {"start": v(305.02, 46.77) * mm, "end": v(311.37, 46.77) * mm});
            skLineSegment(sketch, "E146.4.1.22", {"start": v(317.72, 59.47) * mm, "end": v(324.07, 59.47) * mm});
            skLineSegment(sketch, "E146.4.1.23", {"start": v(330.42, 72.17) * mm, "end": v(336.77, 72.17) * mm});
            skLineSegment(sketch, "E146.4.1.24", {"start": v(343.12, 84.87) * mm, "end": v(349.47, 84.87) * mm});
            skLineSegment(sketch, "E146.4.1.25", {"start": v(343.12, 34.07) * mm, "end": v(349.47, 34.07) * mm});
            skLineSegment(sketch, "E146.4.1.26", {"start": v(324.07, 65.82) * mm, "end": v(324.07, 59.47) * mm});
            skLineSegment(sketch, "E146.4.1.27", {"start": v(336.77, 78.52) * mm, "end": v(336.77, 72.17) * mm});
            skLineSegment(sketch, "E146.4.1.28", {"start": v(349.47, 91.22) * mm, "end": v(349.47, 84.87) * mm});
            skLineSegment(sketch, "E146.4.1.29", {"start": v(349.47, 40.42) * mm, "end": v(349.47, 34.07) * mm});
            skLineSegment(sketch, "E146.4.1.30", {"start": v(305.02, 78.52) * mm, "end": v(305.02, 72.17) * mm});
            skLineSegment(sketch, "E146.4.1.31", {"start": v(317.72, 91.22) * mm, "end": v(317.72, 84.87) * mm});
            skLineSegment(sketch, "E146.4.1.32", {"start": v(317.72, 40.42) * mm, "end": v(317.72, 34.07) * mm});
            skLineSegment(sketch, "E146.4.1.33", {"start": v(330.42, 53.12) * mm, "end": v(330.42, 46.77) * mm});
            skLineSegment(sketch, "E146.4.1.34", {"start": v(343.12, 65.82) * mm, "end": v(343.12, 59.47) * mm});
            skLineSegment(sketch, "E146.4.1.35", {"start": v(343.12, 59.47) * mm, "end": v(349.47, 59.47) * mm});
            skLineSegment(sketch, "E146.4.1.36", {"start": v(305.02, 72.17) * mm, "end": v(311.37, 72.17) * mm});
            skLineSegment(sketch, "E146.4.1.37", {"start": v(317.72, 84.87) * mm, "end": v(324.07, 84.87) * mm});
            skLineSegment(sketch, "E146.4.1.38", {"start": v(317.72, 34.07) * mm, "end": v(324.07, 34.07) * mm});
            skLineSegment(sketch, "E146.4.1.39", {"start": v(330.42, 46.77) * mm, "end": v(336.77, 46.77) * mm});
            skLineSegment(sketch, "E146.4.1.40", {"start": v(311.37, 65.82) * mm, "end": v(311.37, 59.47) * mm});
            skLineSegment(sketch, "E146.4.1.41", {"start": v(324.07, 78.52) * mm, "end": v(324.07, 72.17) * mm});
            skLineSegment(sketch, "E146.4.1.42", {"start": v(336.77, 91.22) * mm, "end": v(336.77, 84.87) * mm});
            skLineSegment(sketch, "E146.4.1.43", {"start": v(336.77, 40.42) * mm, "end": v(336.77, 34.07) * mm});
            skLineSegment(sketch, "E146.4.1.44", {"start": v(349.47, 53.12) * mm, "end": v(349.47, 46.77) * mm});
            skLineSegment(sketch, "E146.4.1.45", {"start": v(305.02, 78.52) * mm, "end": v(311.37, 78.52) * mm});
            skLineSegment(sketch, "E146.4.1.46", {"start": v(317.72, 91.22) * mm, "end": v(324.07, 91.22) * mm});
            skLineSegment(sketch, "E146.4.1.47", {"start": v(317.72, 40.42) * mm, "end": v(324.07, 40.42) * mm});
            skLineSegment(sketch, "E146.4.1.48", {"start": v(330.42, 53.12) * mm, "end": v(336.77, 53.12) * mm});
            skLineSegment(sketch, "E146.4.1.49", {"start": v(343.12, 65.82) * mm, "end": v(349.47, 65.82) * mm});
            skLineSegment(sketch, "E146.4.1.50", {"start": v(311.37, 91.22) * mm, "end": v(311.37, 84.87) * mm});
            skLineSegment(sketch, "E146.4.1.51", {"start": v(311.37, 40.42) * mm, "end": v(311.37, 34.07) * mm});
            skLineSegment(sketch, "E146.4.1.52", {"start": v(324.07, 53.12) * mm, "end": v(324.07, 46.77) * mm});
            skLineSegment(sketch, "E146.4.1.53", {"start": v(336.77, 65.82) * mm, "end": v(336.77, 59.47) * mm});
            skLineSegment(sketch, "E146.4.1.54", {"start": v(349.47, 78.52) * mm, "end": v(349.47, 72.17) * mm});
            skLineSegment(sketch, "E146.4.1.55", {"start": v(292.32, 40.42) * mm, "end": v(298.67, 40.42) * mm});
            skLineSegment(sketch, "E146.4.1.56", {"start": v(305.02, 53.12) * mm, "end": v(311.37, 53.12) * mm});
            skLineSegment(sketch, "E146.4.1.57", {"start": v(317.72, 65.82) * mm, "end": v(324.07, 65.82) * mm});
            skLineSegment(sketch, "E146.4.1.58", {"start": v(330.42, 78.52) * mm, "end": v(336.77, 78.52) * mm});
            skLineSegment(sketch, "E146.4.1.59", {"start": v(343.12, 91.22) * mm, "end": v(349.47, 91.22) * mm});
            skLineSegment(sketch, "E146.4.1.60", {"start": v(343.12, 40.42) * mm, "end": v(349.47, 40.42) * mm});
            skLineSegment(sketch, "E146.4.1.61", {"start": v(317.72, 53.12) * mm, "end": v(317.72, 46.77) * mm});
            skLineSegment(sketch, "E146.4.1.62", {"start": v(330.42, 65.82) * mm, "end": v(330.42, 59.47) * mm});
            skLineSegment(sketch, "E146.4.1.63", {"start": v(343.12, 78.52) * mm, "end": v(343.12, 72.17) * mm});
            skLineSegment(sketch, "E146.4.1.64", {"start": v(305.02, 40.42) * mm, "end": v(305.02, 34.07) * mm});
            skLineSegment(sketch, "E146.4.1.65", {"start": v(292.32, 46.77) * mm, "end": v(298.67, 46.77) * mm});
            skLineSegment(sketch, "E146.4.1.66", {"start": v(292.32, 53.12) * mm, "end": v(298.67, 53.12) * mm});
            skLineSegment(sketch, "E146.4.1.67", {"start": v(292.32, 53.12) * mm, "end": v(292.32, 46.77) * mm});
            skLineSegment(sketch, "E146.4.1.68", {"start": v(305.02, 84.87) * mm, "end": v(311.37, 84.87) * mm});
            skLineSegment(sketch, "E146.4.1.69", {"start": v(305.02, 34.07) * mm, "end": v(311.37, 34.07) * mm});
            skLineSegment(sketch, "E146.4.1.70", {"start": v(317.72, 46.77) * mm, "end": v(324.07, 46.77) * mm});
            skLineSegment(sketch, "E146.4.1.71", {"start": v(330.42, 59.47) * mm, "end": v(336.77, 59.47) * mm});
            skLineSegment(sketch, "E146.4.1.72", {"start": v(343.12, 72.17) * mm, "end": v(349.47, 72.17) * mm});
            skLineSegment(sketch, "E146.4.1.73", {"start": v(292.32, 59.47) * mm, "end": v(298.67, 59.47) * mm});
            skLineSegment(sketch, "E146.4.1.74", {"start": v(292.32, 65.82) * mm, "end": v(292.32, 59.47) * mm});
            skLineSegment(sketch, "E146.4.1.75", {"start": v(298.67, 53.12) * mm, "end": v(298.67, 46.77) * mm});
            skLineSegment(sketch, "E146.4.1.76", {"start": v(311.37, 78.52) * mm, "end": v(311.37, 72.17) * mm});
            skLineSegment(sketch, "E146.4.1.77", {"start": v(324.07, 91.22) * mm, "end": v(324.07, 84.87) * mm});
            skLineSegment(sketch, "E146.4.1.78", {"start": v(324.07, 40.42) * mm, "end": v(324.07, 34.07) * mm});
            skLineSegment(sketch, "E146.4.1.79", {"start": v(336.77, 53.12) * mm, "end": v(336.77, 46.77) * mm});
            skLineSegment(sketch, "E146.4.1.80", {"start": v(349.47, 65.82) * mm, "end": v(349.47, 59.47) * mm});
            skLineSegment(sketch, "E146.4.1.81", {"start": v(305.02, 40.42) * mm, "end": v(311.37, 40.42) * mm});
            skLineSegment(sketch, "E146.4.1.82", {"start": v(317.72, 53.12) * mm, "end": v(324.07, 53.12) * mm});
            skLineSegment(sketch, "E146.4.1.83", {"start": v(330.42, 65.82) * mm, "end": v(336.77, 65.82) * mm});
            skLineSegment(sketch, "E146.4.1.84", {"start": v(343.12, 78.52) * mm, "end": v(349.47, 78.52) * mm});
            skLineSegment(sketch, "E146.4.1.85", {"start": v(305.02, 59.47) * mm, "end": v(311.37, 59.47) * mm});
            skLineSegment(sketch, "E146.4.1.86", {"start": v(305.02, 65.82) * mm, "end": v(311.37, 65.82) * mm});
            skLineSegment(sketch, "E146.4.1.87", {"start": v(305.02, 65.82) * mm, "end": v(305.02, 59.47) * mm});
            skLineSegment(sketch, "E146.4.1.88", {"start": v(292.32, 84.87) * mm, "end": v(305.02, 84.87) * mm, "construction": true});
            skLineSegment(sketch, "E146.4.1.89", {"start": v(298.67, 78.52) * mm, "end": v(298.67, 72.17) * mm});
            skLineSegment(sketch, "E146.4.1.90", {"start": v(298.67, 91.22) * mm, "end": v(298.67, 84.87) * mm});
            skLineSegment(sketch, "E146.4.1.91", {"start": v(292.32, 72.17) * mm, "end": v(298.67, 72.17) * mm});
            skLineSegment(sketch, "E146.4.1.92", {"start": v(292.32, 78.52) * mm, "end": v(298.67, 78.52) * mm});
            skLineSegment(sketch, "E146.4.1.93", {"start": v(292.32, 84.87) * mm, "end": v(292.32, 72.17) * mm, "construction": true});
            skLineSegment(sketch, "E146.4.1.94", {"start": v(298.67, 65.82) * mm, "end": v(298.67, 59.47) * mm});
            skLineSegment(sketch, "E146.4.1.95", {"start": v(292.32, 65.82) * mm, "end": v(298.67, 65.82) * mm});
            skLineSegment(sketch, "E146.4.1.96", {"start": v(305.02, 91.22) * mm, "end": v(311.37, 91.22) * mm});
            skLineSegment(sketch, "E146.4.1.97", {"start": v(305.02, 91.22) * mm, "end": v(305.02, 84.87) * mm});
            skLineSegment(sketch, "E146.4.1.98", {"start": v(292.32, 91.22) * mm, "end": v(298.67, 91.22) * mm});
            skLineSegment(sketch, "E146.4.1.99", {"start": v(292.32, 91.22) * mm, "end": v(292.32, 84.87) * mm});
            skLineSegment(sketch, "E146.4.1.100", {"start": v(292.32, 84.87) * mm, "end": v(298.67, 84.87) * mm});
            skLineSegment(sketch, "E146.4.1.101", {"start": v(292.32, 78.52) * mm, "end": v(292.32, 72.17) * mm});
            skLineSegment(sketch, "E146.5.0.0", {"start": v(531.08, 326.17) * mm, "end": v(537.43, 326.17) * mm});
            skLineSegment(sketch, "E146.5.0.1", {"start": v(543.78, 338.87) * mm, "end": v(550.13, 338.87) * mm});
            skLineSegment(sketch, "E146.5.0.2", {"start": v(543.78, 288.07) * mm, "end": v(550.13, 288.07) * mm});
            skLineSegment(sketch, "E146.5.0.3", {"start": v(556.48, 300.77) * mm, "end": v(562.83, 300.77) * mm});
            skLineSegment(sketch, "E146.5.0.4", {"start": v(531.08, 332.52) * mm, "end": v(537.43, 332.52) * mm});
            skLineSegment(sketch, "E146.5.0.5", {"start": v(543.78, 345.22) * mm, "end": v(550.13, 345.22) * mm});
            skLineSegment(sketch, "E146.5.0.6", {"start": v(543.78, 294.42) * mm, "end": v(550.13, 294.42) * mm});
            skLineSegment(sketch, "E146.5.0.7", {"start": v(556.48, 307.12) * mm, "end": v(562.83, 307.12) * mm});
            skLineSegment(sketch, "E146.5.0.8", {"start": v(531.08, 332.52) * mm, "end": v(531.08, 326.17) * mm});
            skLineSegment(sketch, "E146.5.0.9", {"start": v(543.78, 345.22) * mm, "end": v(543.78, 338.87) * mm});
            skLineSegment(sketch, "E146.5.0.10", {"start": v(543.78, 294.42) * mm, "end": v(543.78, 288.07) * mm});
            skLineSegment(sketch, "E146.5.0.11", {"start": v(556.48, 307.12) * mm, "end": v(556.48, 300.77) * mm});
            skLineSegment(sketch, "E146.5.0.12", {"start": v(512.03, 294.42) * mm, "end": v(512.03, 288.07) * mm});
            skLineSegment(sketch, "E146.5.0.13", {"start": v(524.73, 307.12) * mm, "end": v(524.73, 300.77) * mm});
            skLineSegment(sketch, "E146.5.0.14", {"start": v(531.08, 319.82) * mm, "end": v(531.08, 313.47) * mm});
            skLineSegment(sketch, "E146.5.0.15", {"start": v(543.78, 332.52) * mm, "end": v(543.78, 326.17) * mm});
            skLineSegment(sketch, "E146.5.0.16", {"start": v(556.48, 345.22) * mm, "end": v(556.48, 338.87) * mm});
            skLineSegment(sketch, "E146.5.0.17", {"start": v(556.48, 294.42) * mm, "end": v(556.48, 288.07) * mm});
            skLineSegment(sketch, "E146.5.0.18", {"start": v(505.68, 294.42) * mm, "end": v(505.68, 288.07) * mm});
            skLineSegment(sketch, "E146.5.0.19", {"start": v(518.38, 307.12) * mm, "end": v(518.38, 300.77) * mm});
            skLineSegment(sketch, "E146.5.0.20", {"start": v(505.68, 288.07) * mm, "end": v(512.03, 288.07) * mm});
            skLineSegment(sketch, "E146.5.0.21", {"start": v(518.38, 300.77) * mm, "end": v(524.73, 300.77) * mm});
            skLineSegment(sketch, "E146.5.0.22", {"start": v(531.08, 313.47) * mm, "end": v(537.43, 313.47) * mm});
            skLineSegment(sketch, "E146.5.0.23", {"start": v(543.78, 326.17) * mm, "end": v(550.13, 326.17) * mm});
            skLineSegment(sketch, "E146.5.0.24", {"start": v(556.48, 338.87) * mm, "end": v(562.83, 338.87) * mm});
            skLineSegment(sketch, "E146.5.0.25", {"start": v(556.48, 288.07) * mm, "end": v(562.83, 288.07) * mm});
            skLineSegment(sketch, "E146.5.0.26", {"start": v(537.43, 319.82) * mm, "end": v(537.43, 313.47) * mm});
            skLineSegment(sketch, "E146.5.0.27", {"start": v(550.13, 332.52) * mm, "end": v(550.13, 326.17) * mm});
            skLineSegment(sketch, "E146.5.0.28", {"start": v(562.83, 345.22) * mm, "end": v(562.83, 338.87) * mm});
            skLineSegment(sketch, "E146.5.0.29", {"start": v(562.83, 294.42) * mm, "end": v(562.83, 288.07) * mm});
            skLineSegment(sketch, "E146.5.0.30", {"start": v(518.38, 332.52) * mm, "end": v(518.38, 326.17) * mm});
            skLineSegment(sketch, "E146.5.0.31", {"start": v(531.08, 345.22) * mm, "end": v(531.08, 338.87) * mm});
            skLineSegment(sketch, "E146.5.0.32", {"start": v(531.08, 294.42) * mm, "end": v(531.08, 288.07) * mm});
            skLineSegment(sketch, "E146.5.0.33", {"start": v(543.78, 307.12) * mm, "end": v(543.78, 300.77) * mm});
            skLineSegment(sketch, "E146.5.0.34", {"start": v(556.48, 319.82) * mm, "end": v(556.48, 313.47) * mm});
            skLineSegment(sketch, "E146.5.0.35", {"start": v(556.48, 313.47) * mm, "end": v(562.83, 313.47) * mm});
            skLineSegment(sketch, "E146.5.0.36", {"start": v(518.38, 326.17) * mm, "end": v(524.73, 326.17) * mm});
            skLineSegment(sketch, "E146.5.0.37", {"start": v(531.08, 338.87) * mm, "end": v(537.43, 338.87) * mm});
            skLineSegment(sketch, "E146.5.0.38", {"start": v(531.08, 288.07) * mm, "end": v(537.43, 288.07) * mm});
            skLineSegment(sketch, "E146.5.0.39", {"start": v(543.78, 300.77) * mm, "end": v(550.13, 300.77) * mm});
            skLineSegment(sketch, "E146.5.0.40", {"start": v(524.73, 319.82) * mm, "end": v(524.73, 313.47) * mm});
            skLineSegment(sketch, "E146.5.0.41", {"start": v(537.43, 332.52) * mm, "end": v(537.43, 326.17) * mm});
            skLineSegment(sketch, "E146.5.0.42", {"start": v(550.13, 345.22) * mm, "end": v(550.13, 338.87) * mm});
            skLineSegment(sketch, "E146.5.0.43", {"start": v(550.13, 294.42) * mm, "end": v(550.13, 288.07) * mm});
            skLineSegment(sketch, "E146.5.0.44", {"start": v(562.83, 307.12) * mm, "end": v(562.83, 300.77) * mm});
            skLineSegment(sketch, "E146.5.0.45", {"start": v(518.38, 332.52) * mm, "end": v(524.73, 332.52) * mm});
            skLineSegment(sketch, "E146.5.0.46", {"start": v(531.08, 345.22) * mm, "end": v(537.43, 345.22) * mm});
            skLineSegment(sketch, "E146.5.0.47", {"start": v(531.08, 294.42) * mm, "end": v(537.43, 294.42) * mm});
            skLineSegment(sketch, "E146.5.0.48", {"start": v(543.78, 307.12) * mm, "end": v(550.13, 307.12) * mm});
            skLineSegment(sketch, "E146.5.0.49", {"start": v(556.48, 319.82) * mm, "end": v(562.83, 319.82) * mm});
            skLineSegment(sketch, "E146.5.0.50", {"start": v(524.73, 345.22) * mm, "end": v(524.73, 338.87) * mm});
            skLineSegment(sketch, "E146.5.0.51", {"start": v(524.73, 294.42) * mm, "end": v(524.73, 288.07) * mm});
            skLineSegment(sketch, "E146.5.0.52", {"start": v(537.43, 307.12) * mm, "end": v(537.43, 300.77) * mm});
            skLineSegment(sketch, "E146.5.0.53", {"start": v(550.13, 319.82) * mm, "end": v(550.13, 313.47) * mm});
            skLineSegment(sketch, "E146.5.0.54", {"start": v(562.83, 332.52) * mm, "end": v(562.83, 326.17) * mm});
            skLineSegment(sketch, "E146.5.0.55", {"start": v(505.68, 294.42) * mm, "end": v(512.03, 294.42) * mm});
            skLineSegment(sketch, "E146.5.0.56", {"start": v(518.38, 307.12) * mm, "end": v(524.73, 307.12) * mm});
            skLineSegment(sketch, "E146.5.0.57", {"start": v(531.08, 319.82) * mm, "end": v(537.43, 319.82) * mm});
            skLineSegment(sketch, "E146.5.0.58", {"start": v(543.78, 332.52) * mm, "end": v(550.13, 332.52) * mm});
            skLineSegment(sketch, "E146.5.0.59", {"start": v(556.48, 345.22) * mm, "end": v(562.83, 345.22) * mm});
            skLineSegment(sketch, "E146.5.0.60", {"start": v(556.48, 294.42) * mm, "end": v(562.83, 294.42) * mm});
            skLineSegment(sketch, "E146.5.0.61", {"start": v(531.08, 307.12) * mm, "end": v(531.08, 300.77) * mm});
            skLineSegment(sketch, "E146.5.0.62", {"start": v(543.78, 319.82) * mm, "end": v(543.78, 313.47) * mm});
            skLineSegment(sketch, "E146.5.0.63", {"start": v(556.48, 332.52) * mm, "end": v(556.48, 326.17) * mm});
            skLineSegment(sketch, "E146.5.0.64", {"start": v(518.38, 294.42) * mm, "end": v(518.38, 288.07) * mm});
            skLineSegment(sketch, "E146.5.0.65", {"start": v(505.68, 300.77) * mm, "end": v(512.03, 300.77) * mm});
            skLineSegment(sketch, "E146.5.0.66", {"start": v(505.68, 307.12) * mm, "end": v(512.03, 307.12) * mm});
            skLineSegment(sketch, "E146.5.0.67", {"start": v(505.68, 307.12) * mm, "end": v(505.68, 300.77) * mm});
            skLineSegment(sketch, "E146.5.0.68", {"start": v(518.38, 338.87) * mm, "end": v(524.73, 338.87) * mm});
            skLineSegment(sketch, "E146.5.0.69", {"start": v(518.38, 288.07) * mm, "end": v(524.73, 288.07) * mm});
            skLineSegment(sketch, "E146.5.0.70", {"start": v(531.08, 300.77) * mm, "end": v(537.43, 300.77) * mm});
            skLineSegment(sketch, "E146.5.0.71", {"start": v(543.78, 313.47) * mm, "end": v(550.13, 313.47) * mm});
            skLineSegment(sketch, "E146.5.0.72", {"start": v(556.48, 326.17) * mm, "end": v(562.83, 326.17) * mm});
            skLineSegment(sketch, "E146.5.0.73", {"start": v(505.68, 313.47) * mm, "end": v(512.03, 313.47) * mm});
            skLineSegment(sketch, "E146.5.0.74", {"start": v(505.68, 319.82) * mm, "end": v(505.68, 313.47) * mm});
            skLineSegment(sketch, "E146.5.0.75", {"start": v(512.03, 307.12) * mm, "end": v(512.03, 300.77) * mm});
            skLineSegment(sketch, "E146.5.0.76", {"start": v(524.73, 332.52) * mm, "end": v(524.73, 326.17) * mm});
            skLineSegment(sketch, "E146.5.0.77", {"start": v(537.43, 345.22) * mm, "end": v(537.43, 338.87) * mm});
            skLineSegment(sketch, "E146.5.0.78", {"start": v(537.43, 294.42) * mm, "end": v(537.43, 288.07) * mm});
            skLineSegment(sketch, "E146.5.0.79", {"start": v(550.13, 307.12) * mm, "end": v(550.13, 300.77) * mm});
            skLineSegment(sketch, "E146.5.0.80", {"start": v(562.83, 319.82) * mm, "end": v(562.83, 313.47) * mm});
            skLineSegment(sketch, "E146.5.0.81", {"start": v(518.38, 294.42) * mm, "end": v(524.73, 294.42) * mm});
            skLineSegment(sketch, "E146.5.0.82", {"start": v(531.08, 307.12) * mm, "end": v(537.43, 307.12) * mm});
            skLineSegment(sketch, "E146.5.0.83", {"start": v(543.78, 319.82) * mm, "end": v(550.13, 319.82) * mm});
            skLineSegment(sketch, "E146.5.0.84", {"start": v(556.48, 332.52) * mm, "end": v(562.83, 332.52) * mm});
            skLineSegment(sketch, "E146.5.0.85", {"start": v(518.38, 313.47) * mm, "end": v(524.73, 313.47) * mm});
            skLineSegment(sketch, "E146.5.0.86", {"start": v(518.38, 319.82) * mm, "end": v(524.73, 319.82) * mm});
            skLineSegment(sketch, "E146.5.0.87", {"start": v(518.38, 319.82) * mm, "end": v(518.38, 313.47) * mm});
            skLineSegment(sketch, "E146.5.0.88", {"start": v(505.68, 338.87) * mm, "end": v(518.38, 338.87) * mm, "construction": true});
            skLineSegment(sketch, "E146.5.0.89", {"start": v(512.03, 332.52) * mm, "end": v(512.03, 326.17) * mm});
            skLineSegment(sketch, "E146.5.0.90", {"start": v(512.03, 345.22) * mm, "end": v(512.03, 338.87) * mm});
            skLineSegment(sketch, "E146.5.0.91", {"start": v(505.68, 326.17) * mm, "end": v(512.03, 326.17) * mm});
            skLineSegment(sketch, "E146.5.0.92", {"start": v(505.68, 332.52) * mm, "end": v(512.03, 332.52) * mm});
            skLineSegment(sketch, "E146.5.0.93", {"start": v(505.68, 338.87) * mm, "end": v(505.68, 326.17) * mm, "construction": true});
            skLineSegment(sketch, "E146.5.0.94", {"start": v(512.03, 319.82) * mm, "end": v(512.03, 313.47) * mm});
            skLineSegment(sketch, "E146.5.0.95", {"start": v(505.68, 319.82) * mm, "end": v(512.03, 319.82) * mm});
            skLineSegment(sketch, "E146.5.0.96", {"start": v(518.38, 345.22) * mm, "end": v(524.73, 345.22) * mm});
            skLineSegment(sketch, "E146.5.0.97", {"start": v(518.38, 345.22) * mm, "end": v(518.38, 338.87) * mm});
            skLineSegment(sketch, "E146.5.0.98", {"start": v(505.68, 345.22) * mm, "end": v(512.03, 345.22) * mm});
            skLineSegment(sketch, "E146.5.0.99", {"start": v(505.68, 345.22) * mm, "end": v(505.68, 338.87) * mm});
            skLineSegment(sketch, "E146.5.0.100", {"start": v(505.68, 338.87) * mm, "end": v(512.03, 338.87) * mm});
            skLineSegment(sketch, "E146.5.0.101", {"start": v(505.68, 332.52) * mm, "end": v(505.68, 326.17) * mm});
            skLineSegment(sketch, "E146.5.1.0", {"start": v(531.08, 72.17) * mm, "end": v(537.43, 72.17) * mm});
            skLineSegment(sketch, "E146.5.1.1", {"start": v(543.78, 84.87) * mm, "end": v(550.13, 84.87) * mm});
            skLineSegment(sketch, "E146.5.1.2", {"start": v(543.78, 34.07) * mm, "end": v(550.13, 34.07) * mm});
            skLineSegment(sketch, "E146.5.1.3", {"start": v(556.48, 46.77) * mm, "end": v(562.83, 46.77) * mm});
            skLineSegment(sketch, "E146.5.1.4", {"start": v(531.08, 78.52) * mm, "end": v(537.43, 78.52) * mm});
            skLineSegment(sketch, "E146.5.1.5", {"start": v(543.78, 91.22) * mm, "end": v(550.13, 91.22) * mm});
            skLineSegment(sketch, "E146.5.1.6", {"start": v(543.78, 40.42) * mm, "end": v(550.13, 40.42) * mm});
            skLineSegment(sketch, "E146.5.1.7", {"start": v(556.48, 53.12) * mm, "end": v(562.83, 53.12) * mm});
            skLineSegment(sketch, "E146.5.1.8", {"start": v(531.08, 78.52) * mm, "end": v(531.08, 72.17) * mm});
            skLineSegment(sketch, "E146.5.1.9", {"start": v(543.78, 91.22) * mm, "end": v(543.78, 84.87) * mm});
            skLineSegment(sketch, "E146.5.1.10", {"start": v(543.78, 40.42) * mm, "end": v(543.78, 34.07) * mm});
            skLineSegment(sketch, "E146.5.1.11", {"start": v(556.48, 53.12) * mm, "end": v(556.48, 46.77) * mm});
            skLineSegment(sketch, "E146.5.1.12", {"start": v(512.03, 40.42) * mm, "end": v(512.03, 34.07) * mm});
            skLineSegment(sketch, "E146.5.1.13", {"start": v(524.73, 53.12) * mm, "end": v(524.73, 46.77) * mm});
            skLineSegment(sketch, "E146.5.1.14", {"start": v(531.08, 65.82) * mm, "end": v(531.08, 59.47) * mm});
            skLineSegment(sketch, "E146.5.1.15", {"start": v(543.78, 78.52) * mm, "end": v(543.78, 72.17) * mm});
            skLineSegment(sketch, "E146.5.1.16", {"start": v(556.48, 91.22) * mm, "end": v(556.48, 84.87) * mm});
            skLineSegment(sketch, "E146.5.1.17", {"start": v(556.48, 40.42) * mm, "end": v(556.48, 34.07) * mm});
            skLineSegment(sketch, "E146.5.1.18", {"start": v(505.68, 40.42) * mm, "end": v(505.68, 34.07) * mm});
            skLineSegment(sketch, "E146.5.1.19", {"start": v(518.38, 53.12) * mm, "end": v(518.38, 46.77) * mm});
            skLineSegment(sketch, "E146.5.1.20", {"start": v(505.68, 34.07) * mm, "end": v(512.03, 34.07) * mm});
            skLineSegment(sketch, "E146.5.1.21", {"start": v(518.38, 46.77) * mm, "end": v(524.73, 46.77) * mm});
            skLineSegment(sketch, "E146.5.1.22", {"start": v(531.08, 59.47) * mm, "end": v(537.43, 59.47) * mm});
            skLineSegment(sketch, "E146.5.1.23", {"start": v(543.78, 72.17) * mm, "end": v(550.13, 72.17) * mm});
            skLineSegment(sketch, "E146.5.1.24", {"start": v(556.48, 84.87) * mm, "end": v(562.83, 84.87) * mm});
            skLineSegment(sketch, "E146.5.1.25", {"start": v(556.48, 34.07) * mm, "end": v(562.83, 34.07) * mm});
            skLineSegment(sketch, "E146.5.1.26", {"start": v(537.43, 65.82) * mm, "end": v(537.43, 59.47) * mm});
            skLineSegment(sketch, "E146.5.1.27", {"start": v(550.13, 78.52) * mm, "end": v(550.13, 72.17) * mm});
            skLineSegment(sketch, "E146.5.1.28", {"start": v(562.83, 91.22) * mm, "end": v(562.83, 84.87) * mm});
            skLineSegment(sketch, "E146.5.1.29", {"start": v(562.83, 40.42) * mm, "end": v(562.83, 34.07) * mm});
            skLineSegment(sketch, "E146.5.1.30", {"start": v(518.38, 78.52) * mm, "end": v(518.38, 72.17) * mm});
            skLineSegment(sketch, "E146.5.1.31", {"start": v(531.08, 91.22) * mm, "end": v(531.08, 84.87) * mm});
            skLineSegment(sketch, "E146.5.1.32", {"start": v(531.08, 40.42) * mm, "end": v(531.08, 34.07) * mm});
            skLineSegment(sketch, "E146.5.1.33", {"start": v(543.78, 53.12) * mm, "end": v(543.78, 46.77) * mm});
            skLineSegment(sketch, "E146.5.1.34", {"start": v(556.48, 65.82) * mm, "end": v(556.48, 59.47) * mm});
            skLineSegment(sketch, "E146.5.1.35", {"start": v(556.48, 59.47) * mm, "end": v(562.83, 59.47) * mm});
            skLineSegment(sketch, "E146.5.1.36", {"start": v(518.38, 72.17) * mm, "end": v(524.73, 72.17) * mm});
            skLineSegment(sketch, "E146.5.1.37", {"start": v(531.08, 84.87) * mm, "end": v(537.43, 84.87) * mm});
            skLineSegment(sketch, "E146.5.1.38", {"start": v(531.08, 34.07) * mm, "end": v(537.43, 34.07) * mm});
            skLineSegment(sketch, "E146.5.1.39", {"start": v(543.78, 46.77) * mm, "end": v(550.13, 46.77) * mm});
            skLineSegment(sketch, "E146.5.1.40", {"start": v(524.73, 65.82) * mm, "end": v(524.73, 59.47) * mm});
            skLineSegment(sketch, "E146.5.1.41", {"start": v(537.43, 78.52) * mm, "end": v(537.43, 72.17) * mm});
            skLineSegment(sketch, "E146.5.1.42", {"start": v(550.13, 91.22) * mm, "end": v(550.13, 84.87) * mm});
            skLineSegment(sketch, "E146.5.1.43", {"start": v(550.13, 40.42) * mm, "end": v(550.13, 34.07) * mm});
            skLineSegment(sketch, "E146.5.1.44", {"start": v(562.83, 53.12) * mm, "end": v(562.83, 46.77) * mm});
            skLineSegment(sketch, "E146.5.1.45", {"start": v(518.38, 78.52) * mm, "end": v(524.73, 78.52) * mm});
            skLineSegment(sketch, "E146.5.1.46", {"start": v(531.08, 91.22) * mm, "end": v(537.43, 91.22) * mm});
            skLineSegment(sketch, "E146.5.1.47", {"start": v(531.08, 40.42) * mm, "end": v(537.43, 40.42) * mm});
            skLineSegment(sketch, "E146.5.1.48", {"start": v(543.78, 53.12) * mm, "end": v(550.13, 53.12) * mm});
            skLineSegment(sketch, "E146.5.1.49", {"start": v(556.48, 65.82) * mm, "end": v(562.83, 65.82) * mm});
            skLineSegment(sketch, "E146.5.1.50", {"start": v(524.73, 91.22) * mm, "end": v(524.73, 84.87) * mm});
            skLineSegment(sketch, "E146.5.1.51", {"start": v(524.73, 40.42) * mm, "end": v(524.73, 34.07) * mm});
            skLineSegment(sketch, "E146.5.1.52", {"start": v(537.43, 53.12) * mm, "end": v(537.43, 46.77) * mm});
            skLineSegment(sketch, "E146.5.1.53", {"start": v(550.13, 65.82) * mm, "end": v(550.13, 59.47) * mm});
            skLineSegment(sketch, "E146.5.1.54", {"start": v(562.83, 78.52) * mm, "end": v(562.83, 72.17) * mm});
            skLineSegment(sketch, "E146.5.1.55", {"start": v(505.68, 40.42) * mm, "end": v(512.03, 40.42) * mm});
            skLineSegment(sketch, "E146.5.1.56", {"start": v(518.38, 53.12) * mm, "end": v(524.73, 53.12) * mm});
            skLineSegment(sketch, "E146.5.1.57", {"start": v(531.08, 65.82) * mm, "end": v(537.43, 65.82) * mm});
            skLineSegment(sketch, "E146.5.1.58", {"start": v(543.78, 78.52) * mm, "end": v(550.13, 78.52) * mm});
            skLineSegment(sketch, "E146.5.1.59", {"start": v(556.48, 91.22) * mm, "end": v(562.83, 91.22) * mm});
            skLineSegment(sketch, "E146.5.1.60", {"start": v(556.48, 40.42) * mm, "end": v(562.83, 40.42) * mm});
            skLineSegment(sketch, "E146.5.1.61", {"start": v(531.08, 53.12) * mm, "end": v(531.08, 46.77) * mm});
            skLineSegment(sketch, "E146.5.1.62", {"start": v(543.78, 65.82) * mm, "end": v(543.78, 59.47) * mm});
            skLineSegment(sketch, "E146.5.1.63", {"start": v(556.48, 78.52) * mm, "end": v(556.48, 72.17) * mm});
            skLineSegment(sketch, "E146.5.1.64", {"start": v(518.38, 40.42) * mm, "end": v(518.38, 34.07) * mm});
            skLineSegment(sketch, "E146.5.1.65", {"start": v(505.68, 46.77) * mm, "end": v(512.03, 46.77) * mm});
            skLineSegment(sketch, "E146.5.1.66", {"start": v(505.68, 53.12) * mm, "end": v(512.03, 53.12) * mm});
            skLineSegment(sketch, "E146.5.1.67", {"start": v(505.68, 53.12) * mm, "end": v(505.68, 46.77) * mm});
            skLineSegment(sketch, "E146.5.1.68", {"start": v(518.38, 84.87) * mm, "end": v(524.73, 84.87) * mm});
            skLineSegment(sketch, "E146.5.1.69", {"start": v(518.38, 34.07) * mm, "end": v(524.73, 34.07) * mm});
            skLineSegment(sketch, "E146.5.1.70", {"start": v(531.08, 46.77) * mm, "end": v(537.43, 46.77) * mm});
            skLineSegment(sketch, "E146.5.1.71", {"start": v(543.78, 59.47) * mm, "end": v(550.13, 59.47) * mm});
            skLineSegment(sketch, "E146.5.1.72", {"start": v(556.48, 72.17) * mm, "end": v(562.83, 72.17) * mm});
            skLineSegment(sketch, "E146.5.1.73", {"start": v(505.68, 59.47) * mm, "end": v(512.03, 59.47) * mm});
            skLineSegment(sketch, "E146.5.1.74", {"start": v(505.68, 65.82) * mm, "end": v(505.68, 59.47) * mm});
            skLineSegment(sketch, "E146.5.1.75", {"start": v(512.03, 53.12) * mm, "end": v(512.03, 46.77) * mm});
            skLineSegment(sketch, "E146.5.1.76", {"start": v(524.73, 78.52) * mm, "end": v(524.73, 72.17) * mm});
            skLineSegment(sketch, "E146.5.1.77", {"start": v(537.43, 91.22) * mm, "end": v(537.43, 84.87) * mm});
            skLineSegment(sketch, "E146.5.1.78", {"start": v(537.43, 40.42) * mm, "end": v(537.43, 34.07) * mm});
            skLineSegment(sketch, "E146.5.1.79", {"start": v(550.13, 53.12) * mm, "end": v(550.13, 46.77) * mm});
            skLineSegment(sketch, "E146.5.1.80", {"start": v(562.83, 65.82) * mm, "end": v(562.83, 59.47) * mm});
            skLineSegment(sketch, "E146.5.1.81", {"start": v(518.38, 40.42) * mm, "end": v(524.73, 40.42) * mm});
            skLineSegment(sketch, "E146.5.1.82", {"start": v(531.08, 53.12) * mm, "end": v(537.43, 53.12) * mm});
            skLineSegment(sketch, "E146.5.1.83", {"start": v(543.78, 65.82) * mm, "end": v(550.13, 65.82) * mm});
            skLineSegment(sketch, "E146.5.1.84", {"start": v(556.48, 78.52) * mm, "end": v(562.83, 78.52) * mm});
            skLineSegment(sketch, "E146.5.1.85", {"start": v(518.38, 59.47) * mm, "end": v(524.73, 59.47) * mm});
            skLineSegment(sketch, "E146.5.1.86", {"start": v(518.38, 65.82) * mm, "end": v(524.73, 65.82) * mm});
            skLineSegment(sketch, "E146.5.1.87", {"start": v(518.38, 65.82) * mm, "end": v(518.38, 59.47) * mm});
            skLineSegment(sketch, "E146.5.1.88", {"start": v(505.68, 84.87) * mm, "end": v(518.38, 84.87) * mm, "construction": true});
            skLineSegment(sketch, "E146.5.1.89", {"start": v(512.03, 78.52) * mm, "end": v(512.03, 72.17) * mm});
            skLineSegment(sketch, "E146.5.1.90", {"start": v(512.03, 91.22) * mm, "end": v(512.03, 84.87) * mm});
            skLineSegment(sketch, "E146.5.1.91", {"start": v(505.68, 72.17) * mm, "end": v(512.03, 72.17) * mm});
            skLineSegment(sketch, "E146.5.1.92", {"start": v(505.68, 78.52) * mm, "end": v(512.03, 78.52) * mm});
            skLineSegment(sketch, "E146.5.1.93", {"start": v(505.68, 84.87) * mm, "end": v(505.68, 72.17) * mm, "construction": true});
            skLineSegment(sketch, "E146.5.1.94", {"start": v(512.03, 65.82) * mm, "end": v(512.03, 59.47) * mm});
            skLineSegment(sketch, "E146.5.1.95", {"start": v(505.68, 65.82) * mm, "end": v(512.03, 65.82) * mm});
            skLineSegment(sketch, "E146.5.1.96", {"start": v(518.38, 91.22) * mm, "end": v(524.73, 91.22) * mm});
            skLineSegment(sketch, "E146.5.1.97", {"start": v(518.38, 91.22) * mm, "end": v(518.38, 84.87) * mm});
            skLineSegment(sketch, "E146.5.1.98", {"start": v(505.68, 91.22) * mm, "end": v(512.03, 91.22) * mm});
            skLineSegment(sketch, "E146.5.1.99", {"start": v(505.68, 91.22) * mm, "end": v(505.68, 84.87) * mm});
            skLineSegment(sketch, "E146.5.1.100", {"start": v(505.68, 84.87) * mm, "end": v(512.03, 84.87) * mm});
            skLineSegment(sketch, "E146.5.1.101", {"start": v(505.68, 78.52) * mm, "end": v(505.68, 72.17) * mm});
            skLineSegment(sketch, "E146.direction1", {"start": v(-561.12, 288.07) * mm, "end": v(-347.76, 288.07) * mm, "construction": true});
            skLineSegment(sketch, "E146.direction2", {"start": v(-561.12, 288.07) * mm, "end": v(-561.12, 34.07) * mm, "construction": true});
            skSolve(sketch);
        }
        {
            var Q0;
            Q0=makeQuery(id+"F12.imprint","IMPRINT",FACE,{"disambiguationData":[TD([[makeQuery(id+"F12.imprint","IMPRINT",EDGE,{"derivedFrom":sQuery(id+"F12.wireOp",EDGE,"E146.1.0.16")}),1.0]])]});
            var Q1;
            Q1=makeQuery(id+"F12.imprint","IMPRINT",FACE,{"disambiguationData":[TD([[makeQuery(id+"F12.imprint","IMPRINT",EDGE,{"derivedFrom":sQuery(id+"F12.wireOp",EDGE,"E146.5.0.16")}),1.0]])]});
            var Q2;
            Q2=makeQuery(id+"F12.imprint","IMPRINT",FACE,{"disambiguationData":[TD([[makeQuery(id+"F12.imprint","IMPRINT",EDGE,{"derivedFrom":sQuery(id+"F12.wireOp",EDGE,"E146.5.1.12")}),-1.0]])]});
            var Q3;
            Q3=makeQuery(id+"F12.imprint","IMPRINT",FACE,{"disambiguationData":[TD([[makeQuery(id+"F12.imprint","IMPRINT",EDGE,{"derivedFrom":sQuery(id+"F12.wireOp",EDGE,"E146.1.0.54")}),-1.0]])]});
            var Q4;
            Q4=makeQuery(id+"F12.imprint","IMPRINT",FACE,{"disambiguationData":[TD([[makeQuery(id+"F12.imprint","IMPRINT",EDGE,{"derivedFrom":sQuery(id+"F12.wireOp",EDGE,"E146.4.0.16")}),1.0]])]});
            var Q5;
            Q5=makeQuery(id+"F12.imprint","IMPRINT",FACE,{"disambiguationData":[TD([[makeQuery(id+"F12.imprint","IMPRINT",EDGE,{"derivedFrom":sQuery(id+"F12.wireOp",EDGE,"E146.4.1.16")}),1.0]])]});
            var Q6;
            Q6=makeQuery(id+"F12.imprint","IMPRINT",FACE,{"disambiguationData":[TD([[makeQuery(id+"F12.imprint","IMPRINT",EDGE,{"derivedFrom":sQuery(id+"F12.wireOp",EDGE,"E146.4.1.17")}),1.0]])]});
            var Q7;
            Q7=makeQuery(id+"F12.imprint","IMPRINT",FACE,{"disambiguationData":[TD([[makeQuery(id+"F12.imprint","IMPRINT",EDGE,{"derivedFrom":sQuery(id+"F12.wireOp",EDGE,"E146.3.1.54")}),-1.0]])]});
            var Q8;
            Q8=makeQuery(id+"F12.imprint","IMPRINT",FACE,{"disambiguationData":[TD([[makeQuery(id+"F12.imprint","IMPRINT",EDGE,{"derivedFrom":sQuery(id+"F12.wireOp",EDGE,"E146.1.1.16")}),1.0]])]});
            var Q9;
            Q9=makeQuery(id+"F12.imprint","IMPRINT",FACE,{"disambiguationData":[TD([[makeQuery(id+"F12.imprint","IMPRINT",EDGE,{"derivedFrom":sQuery(id+"F12.wireOp",EDGE,"E146.0.1.17")}),1.0]])]});
            var Q10;
            Q10=makeQuery(id+"F12.imprint","IMPRINT",FACE,{"disambiguationData":[TD([[makeQuery(id+"F12.imprint","IMPRINT",EDGE,{"derivedFrom":sQuery(id+"F12.wireOp",EDGE,"E146.4.0.17")}),1.0]])]});
            var Q11;
            Q11=makeQuery(id+"F12.imprint","IMPRINT",FACE,{"disambiguationData":[TD([[makeQuery(id+"F12.imprint","IMPRINT",EDGE,{"derivedFrom":sQuery(id+"F12.wireOp",EDGE,"E146.4.1.54")}),-1.0]])]});
            var Q12;
            Q12=makeQuery(id+"F12.imprint","IMPRINT",FACE,{"disambiguationData":[TD([[makeQuery(id+"F12.imprint","IMPRINT",EDGE,{"derivedFrom":sQuery(id+"F12.wireOp",EDGE,"E145.4.0.0")}),-1.0]])]});
            var Q13;
            Q13=makeQuery(id+"F12.imprint","IMPRINT",FACE,{"disambiguationData":[TD([[makeQuery(id+"F12.imprint","IMPRINT",EDGE,{"derivedFrom":sQuery(id+"F12.wireOp",EDGE,"E146.4.1.3")}),1.0]])]});
            var Q14;
            Q14=makeQuery(id+"F12.imprint","IMPRINT",FACE,{"disambiguationData":[TD([[makeQuery(id+"F12.imprint","IMPRINT",EDGE,{"derivedFrom":sQuery(id+"F12.wireOp",EDGE,"E146.1.1.17")}),1.0]])]});
            var Q15;
            Q15=makeQuery(id+"F12.imprint","IMPRINT",FACE,{"disambiguationData":[TD([[makeQuery(id+"F12.imprint","IMPRINT",EDGE,{"derivedFrom":sQuery(id+"F12.wireOp",EDGE,"E146.2.0.50")}),-1.0]])]});
            var Q16;
            Q16=makeQuery(id+"F12.imprint","IMPRINT",FACE,{"disambiguationData":[TD([[makeQuery(id+"F12.imprint","IMPRINT",EDGE,{"derivedFrom":sQuery(id+"F12.wireOp",EDGE,"E146.3.0.1")}),1.0]])]});
            var Q17;
            Q17=makeQuery(id+"F12.imprint","IMPRINT",FACE,{"disambiguationData":[TD([[makeQuery(id+"F12.imprint","IMPRINT",EDGE,{"derivedFrom":sQuery(id+"F12.wireOp",EDGE,"E146.3.1.16")}),1.0]])]});
            var Q18;
            Q18=makeQuery(id+"F12.imprint","IMPRINT",FACE,{"disambiguationData":[TD([[makeQuery(id+"F12.imprint","IMPRINT",EDGE,{"derivedFrom":sQuery(id+"F12.wireOp",EDGE,"E146.4.0.34")}),1.0]])]});
            var Q19;
            Q19=makeQuery(id+"F12.imprint","IMPRINT",FACE,{"disambiguationData":[TD([[makeQuery(id+"F12.imprint","IMPRINT",EDGE,{"derivedFrom":sQuery(id+"F12.wireOp",EDGE,"E146.2.1.17")}),1.0]])]});
            var Q20;
            Q20=makeQuery(id+"F12.imprint","IMPRINT",FACE,{"disambiguationData":[TD([[makeQuery(id+"F12.imprint","IMPRINT",EDGE,{"derivedFrom":sQuery(id+"F12.wireOp",EDGE,"E146.1.1.54")}),-1.0]])]});
            var Q21;
            Q21=makeQuery(id+"F12.imprint","IMPRINT",FACE,{"disambiguationData":[TD([[makeQuery(id+"F12.imprint","IMPRINT",EDGE,{"derivedFrom":sQuery(id+"F12.wireOp",EDGE,"E146.1.1.12")}),-1.0]])]});
            var Q22;
            Q22=makeQuery(id+"F12.imprint","IMPRINT",FACE,{"disambiguationData":[TD([[makeQuery(id+"F12.imprint","IMPRINT",EDGE,{"derivedFrom":sQuery(id+"F12.wireOp",EDGE,"E146.4.1.34")}),1.0]])]});
            var Q23;
            Q23=makeQuery(id+"F12.imprint","IMPRINT",FACE,{"disambiguationData":[TD([[makeQuery(id+"F12.imprint","IMPRINT",EDGE,{"derivedFrom":sQuery(id+"F12.wireOp",EDGE,"E146.5.0.54")}),-1.0]])]});
            var Q24;
            Q24=makeQuery(id+"F12.imprint","IMPRINT",FACE,{"disambiguationData":[TD([[makeQuery(id+"F12.imprint","IMPRINT",EDGE,{"derivedFrom":sQuery(id+"F12.wireOp",EDGE,"E146.3.0.16")}),1.0]])]});
            var Q25;
            Q25=makeQuery(id+"F12.imprint","IMPRINT",FACE,{"disambiguationData":[TD([[makeQuery(id+"F12.imprint","IMPRINT",EDGE,{"derivedFrom":sQuery(id+"F12.wireOp",EDGE,"E146.4.0.73")}),1.0]])]});
            var Q26;
            Q26=makeQuery(id+"F12.imprint","IMPRINT",FACE,{"disambiguationData":[TD([[makeQuery(id+"F12.imprint","IMPRINT",EDGE,{"derivedFrom":sQuery(id+"F12.wireOp",EDGE,"E146.0.1.16")}),1.0]])]});
            var Q27;
            Q27=makeQuery(id+"F12.imprint","IMPRINT",FACE,{"disambiguationData":[TD([[makeQuery(id+"F12.imprint","IMPRINT",EDGE,{"derivedFrom":sQuery(id+"F12.wireOp",EDGE,"E146.2.1.12")}),-1.0]])]});
            var Q28;
            Q28=makeQuery(id+"F12.imprint","IMPRINT",FACE,{"disambiguationData":[TD([[makeQuery(id+"F12.imprint","IMPRINT",EDGE,{"derivedFrom":sQuery(id+"F12.wireOp",EDGE,"E146.4.0.90")}),-1.0]])]});
            var Q29;
            Q29=makeQuery(id+"F12.imprint","IMPRINT",FACE,{"disambiguationData":[TD([[makeQuery(id+"F12.imprint","IMPRINT",EDGE,{"derivedFrom":sQuery(id+"F12.wireOp",EDGE,"E146.2.1.3")}),1.0]])]});
            var Q30;
            Q30=makeQuery(id+"F12.imprint","IMPRINT",FACE,{"disambiguationData":[TD([[makeQuery(id+"F12.imprint","IMPRINT",EDGE,{"derivedFrom":sQuery(id+"F12.wireOp",EDGE,"E146.4.0.1")}),1.0]])]});
            var Q31;
            Q31=makeQuery(id+"F12.imprint","IMPRINT",FACE,{"disambiguationData":[TD([[makeQuery(id+"F12.imprint","IMPRINT",EDGE,{"derivedFrom":sQuery(id+"F12.wireOp",EDGE,"E146.1.1.34")}),1.0]])]});
            var Q32;
            Q32=makeQuery(id+"F12.imprint","IMPRINT",FACE,{"disambiguationData":[TD([[makeQuery(id+"F12.imprint","IMPRINT",EDGE,{"derivedFrom":sQuery(id+"F12.wireOp",EDGE,"E146.2.0.12")}),-1.0]])]});
            var Q33;
            Q33=makeQuery(id+"F12.imprint","IMPRINT",FACE,{"disambiguationData":[TD([[makeQuery(id+"F12.imprint","IMPRINT",EDGE,{"derivedFrom":sQuery(id+"F12.wireOp",EDGE,"E145.4.4.0")}),-1.0]])]});
            var Q34;
            Q34=makeQuery(id+"F12.imprint","IMPRINT",FACE,{"disambiguationData":[TD([[makeQuery(id+"F12.imprint","IMPRINT",EDGE,{"derivedFrom":sQuery(id+"F12.wireOp",EDGE,"E146.5.1.65")}),1.0]])]});
            var Q35;
            Q35=makeQuery(id+"F12.imprint","IMPRINT",FACE,{"disambiguationData":[TD([[makeQuery(id+"F12.imprint","IMPRINT",EDGE,{"derivedFrom":sQuery(id+"F12.wireOp",EDGE,"E146.5.0.1")}),1.0]])]});
            var Q36;
            Q36=makeQuery(id+"F12.imprint","IMPRINT",FACE,{"disambiguationData":[TD([[makeQuery(id+"F12.imprint","IMPRINT",EDGE,{"derivedFrom":sQuery(id+"F12.wireOp",EDGE,"E146.1.0.90")}),-1.0]])]});
            var Q37;
            Q37=makeQuery(id+"F12.imprint","IMPRINT",FACE,{"disambiguationData":[TD([[makeQuery(id+"F12.imprint","IMPRINT",EDGE,{"derivedFrom":sQuery(id+"F12.wireOp",EDGE,"E146.2.0.90")}),-1.0]])]});
            var Q38;
            Q38=makeQuery(id+"F12.imprint","IMPRINT",FACE,{"disambiguationData":[TD([[makeQuery(id+"F12.imprint","IMPRINT",EDGE,{"derivedFrom":sQuery(id+"F12.wireOp",EDGE,"E146.0.1.3")}),1.0]])]});
            var Q39;
            Q39=makeQuery(id+"F12.imprint","IMPRINT",FACE,{"disambiguationData":[TD([[makeQuery(id+"F12.imprint","IMPRINT",EDGE,{"derivedFrom":sQuery(id+"F12.wireOp",EDGE,"E146.4.0.12")}),-1.0]])]});
            var Q40;
            Q40=makeQuery(id+"F12.imprint","IMPRINT",FACE,{"disambiguationData":[TD([[makeQuery(id+"F12.imprint","IMPRINT",EDGE,{"derivedFrom":sQuery(id+"F12.wireOp",EDGE,"E146.4.0.54")}),-1.0]])]});
            var Q41;
            Q41=makeQuery(id+"F12.imprint","IMPRINT",FACE,{"disambiguationData":[TD([[makeQuery(id+"F12.imprint","IMPRINT",EDGE,{"derivedFrom":sQuery(id+"F12.wireOp",EDGE,"E146.5.1.17")}),1.0]])]});
            var Q42;
            Q42=makeQuery(id+"F12.imprint","IMPRINT",FACE,{"disambiguationData":[TD([[makeQuery(id+"F12.imprint","IMPRINT",EDGE,{"derivedFrom":sQuery(id+"F12.wireOp",EDGE,"E145.2.0.0")}),-1.0]])]});
            var Q43;
            Q43=makeQuery(id+"F12.imprint","IMPRINT",FACE,{"disambiguationData":[TD([[makeQuery(id+"F12.imprint","IMPRINT",EDGE,{"derivedFrom":sQuery(id+"F12.wireOp",EDGE,"E146.2.1.73")}),1.0]])]});
            var Q44;
            Q44=makeQuery(id+"F12.imprint","IMPRINT",FACE,{"disambiguationData":[TD([[makeQuery(id+"F12.imprint","IMPRINT",EDGE,{"derivedFrom":sQuery(id+"F12.wireOp",EDGE,"E146.3.1.12")}),-1.0]])]});
            var Q45;
            Q45=makeQuery(id+"F12.imprint","IMPRINT",FACE,{"disambiguationData":[TD([[makeQuery(id+"F12.imprint","IMPRINT",EDGE,{"derivedFrom":sQuery(id+"F12.wireOp",EDGE,"E146.4.0.31")}),1.0]])]});
            var Q46;
            Q46=makeQuery(id+"F12.imprint","IMPRINT",FACE,{"disambiguationData":[TD([[makeQuery(id+"F12.imprint","IMPRINT",EDGE,{"derivedFrom":sQuery(id+"F12.wireOp",EDGE,"E146.1.0.51")}),-1.0]])]});
            var Q47;
            Q47=makeQuery(id+"F12.imprint","IMPRINT",FACE,{"disambiguationData":[TD([[makeQuery(id+"F12.imprint","IMPRINT",EDGE,{"derivedFrom":sQuery(id+"F12.wireOp",EDGE,"E146.1.0.1")}),1.0]])]});
            var Q48;
            Q48=makeQuery(id+"F12.imprint","IMPRINT",FACE,{"disambiguationData":[TD([[makeQuery(id+"F12.imprint","IMPRINT",EDGE,{"derivedFrom":sQuery(id+"F12.wireOp",EDGE,"E146.1.1.90")}),-1.0]])]});
            var Q49;
            Q49=makeQuery(id+"F12.imprint","IMPRINT",FACE,{"disambiguationData":[TD([[makeQuery(id+"F12.imprint","IMPRINT",EDGE,{"derivedFrom":sQuery(id+"F12.wireOp",EDGE,"E146.4.0.30")}),1.0]])]});
            var Q50;
            Q50=makeQuery(id+"F12.imprint","IMPRINT",FACE,{"disambiguationData":[TD([[makeQuery(id+"F12.imprint","IMPRINT",EDGE,{"derivedFrom":sQuery(id+"F12.wireOp",EDGE,"E146.5.0.90")}),-1.0]])]});
            var Q51;
            Q51=makeQuery(id+"F12.imprint","IMPRINT",FACE,{"disambiguationData":[TD([[makeQuery(id+"F12.imprint","IMPRINT",EDGE,{"derivedFrom":sQuery(id+"F12.wireOp",EDGE,"E146.2.1.65")}),1.0]])]});
            var Q52;
            Q52=makeQuery(id+"F12.imprint","IMPRINT",FACE,{"disambiguationData":[TD([[makeQuery(id+"F12.imprint","IMPRINT",EDGE,{"derivedFrom":sQuery(id+"F12.wireOp",EDGE,"E146.5.1.34")}),1.0]])]});
            var Q53;
            Q53=makeQuery(id+"F12.imprint","IMPRINT",FACE,{"disambiguationData":[TD([[makeQuery(id+"F12.imprint","IMPRINT",EDGE,{"derivedFrom":sQuery(id+"F12.wireOp",EDGE,"E146.3.0.31")}),1.0]])]});
            var Q54;
            Q54=makeQuery(id+"F12.imprint","IMPRINT",FACE,{"disambiguationData":[TD([[makeQuery(id+"F12.imprint","IMPRINT",EDGE,{"derivedFrom":sQuery(id+"F12.wireOp",EDGE,"E146.2.1.54")}),-1.0]])]});
            var Q55;
            Q55=makeQuery(id+"F12.imprint","IMPRINT",FACE,{"disambiguationData":[TD([[makeQuery(id+"F12.imprint","IMPRINT",EDGE,{"derivedFrom":sQuery(id+"F12.wireOp",EDGE,"E146.5.0.15")}),1.0]])]});
            var Q56;
            Q56=makeQuery(id+"F12.imprint","IMPRINT",FACE,{"disambiguationData":[TD([[makeQuery(id+"F12.imprint","IMPRINT",EDGE,{"derivedFrom":sQuery(id+"F12.wireOp",EDGE,"E146.1.0.53")}),-1.0]])]});
            var Q57;
            Q57=makeQuery(id+"F12.imprint","IMPRINT",FACE,{"disambiguationData":[TD([[makeQuery(id+"F12.imprint","IMPRINT",EDGE,{"derivedFrom":sQuery(id+"F12.wireOp",EDGE,"E146.2.0.1")}),1.0]])]});
            var Q58;
            Q58=makeQuery(id+"F12.imprint","IMPRINT",FACE,{"disambiguationData":[TD([[makeQuery(id+"F12.imprint","IMPRINT",EDGE,{"derivedFrom":sQuery(id+"F12.wireOp",EDGE,"E146.2.1.90")}),-1.0]])]});
            var Q59;
            Q59=makeQuery(id+"F12.imprint","IMPRINT",FACE,{"disambiguationData":[TD([[makeQuery(id+"F12.imprint","IMPRINT",EDGE,{"derivedFrom":sQuery(id+"F12.wireOp",EDGE,"E146.4.1.12")}),-1.0]])]});
            var Q60;
            Q60=makeQuery(id+"F12.imprint","IMPRINT",FACE,{"disambiguationData":[TD([[makeQuery(id+"F12.imprint","IMPRINT",EDGE,{"derivedFrom":sQuery(id+"F12.wireOp",EDGE,"E146.5.0.31")}),1.0]])]});
            var Q61;
            Q61=makeQuery(id+"F12.imprint","IMPRINT",FACE,{"disambiguationData":[TD([[makeQuery(id+"F12.imprint","IMPRINT",EDGE,{"derivedFrom":sQuery(id+"F12.wireOp",EDGE,"E146.5.1.1")}),1.0]])]});
            var Q62;
            Q62=makeQuery(id+"F12.imprint","IMPRINT",FACE,{"disambiguationData":[TD([[makeQuery(id+"F12.imprint","IMPRINT",EDGE,{"derivedFrom":sQuery(id+"F12.wireOp",EDGE,"E146.3.0.34")}),1.0]])]});
            var Q63;
            Q63=makeQuery(id+"F12.imprint","IMPRINT",FACE,{"disambiguationData":[TD([[makeQuery(id+"F12.imprint","IMPRINT",EDGE,{"derivedFrom":sQuery(id+"F12.wireOp",EDGE,"E146.5.1.0")}),1.0]])]});
            var Q64;
            Q64=makeQuery(id+"F12.imprint","IMPRINT",FACE,{"disambiguationData":[TD([[makeQuery(id+"F12.imprint","IMPRINT",EDGE,{"derivedFrom":sQuery(id+"F12.wireOp",EDGE,"E146.0.1.34")}),1.0]])]});
            var Q65;
            Q65=makeQuery(id+"F12.imprint","IMPRINT",FACE,{"disambiguationData":[TD([[makeQuery(id+"F12.imprint","IMPRINT",EDGE,{"derivedFrom":sQuery(id+"F12.wireOp",EDGE,"E145.4.3.0")}),-1.0]])]});
            var Q66;
            Q66=makeQuery(id+"F12.imprint","IMPRINT",FACE,{"disambiguationData":[TD([[makeQuery(id+"F12.imprint","IMPRINT",EDGE,{"derivedFrom":sQuery(id+"F12.wireOp",EDGE,"E146.1.0.65")}),1.0]])]});
            var Q67;
            Q67=makeQuery(id+"F12.imprint","IMPRINT",FACE,{"disambiguationData":[TD([[makeQuery(id+"F12.imprint","IMPRINT",EDGE,{"derivedFrom":sQuery(id+"F12.wireOp",EDGE,"E146.4.1.73")}),1.0]])]});
            var Q68;
            Q68=makeQuery(id+"F12.imprint","IMPRINT",FACE,{"disambiguationData":[TD([[makeQuery(id+"F12.imprint","IMPRINT",EDGE,{"derivedFrom":sQuery(id+"F12.wireOp",EDGE,"E146.5.0.32")}),1.0]])]});
            var Q69;
            Q69=makeQuery(id+"F12.imprint","IMPRINT",FACE,{"disambiguationData":[TD([[makeQuery(id+"F12.imprint","IMPRINT",EDGE,{"derivedFrom":sQuery(id+"F12.wireOp",EDGE,"E146.1.0.12")}),-1.0]])]});
            var Q70;
            Q70=makeQuery(id+"F12.imprint","IMPRINT",FACE,{"disambiguationData":[TD([[makeQuery(id+"F12.imprint","IMPRINT",EDGE,{"derivedFrom":sQuery(id+"F12.wireOp",EDGE,"E146.3.0.50")}),-1.0]])]});
            var Q71;
            Q71=makeQuery(id+"F12.imprint","IMPRINT",FACE,{"disambiguationData":[TD([[makeQuery(id+"F12.imprint","IMPRINT",EDGE,{"derivedFrom":sQuery(id+"F12.wireOp",EDGE,"E146.2.0.31")}),1.0]])]});
            var Q72;
            Q72=makeQuery(id+"F12.imprint","IMPRINT",FACE,{"disambiguationData":[TD([[makeQuery(id+"F12.imprint","IMPRINT",EDGE,{"derivedFrom":sQuery(id+"F12.wireOp",EDGE,"E146.2.1.2")}),1.0]])]});
            var Q73;
            Q73=makeQuery(id+"F12.imprint","IMPRINT",FACE,{"disambiguationData":[TD([[makeQuery(id+"F12.imprint","IMPRINT",EDGE,{"derivedFrom":sQuery(id+"F12.wireOp",EDGE,"E146.3.0.17")}),1.0]])]});
            var Q74;
            Q74=makeQuery(id+"F12.imprint","IMPRINT",FACE,{"disambiguationData":[TD([[makeQuery(id+"F12.imprint","IMPRINT",EDGE,{"derivedFrom":sQuery(id+"F12.wireOp",EDGE,"E146.1.0.33")}),1.0]])]});
            var Q75;
            Q75=makeQuery(id+"F12.imprint","IMPRINT",FACE,{"disambiguationData":[TD([[makeQuery(id+"F12.imprint","IMPRINT",EDGE,{"derivedFrom":sQuery(id+"F12.wireOp",EDGE,"E146.4.0.89")}),-1.0]])]});
            var Q76;
            Q76=makeQuery(id+"F12.imprint","IMPRINT",FACE,{"disambiguationData":[TD([[makeQuery(id+"F12.imprint","IMPRINT",EDGE,{"derivedFrom":sQuery(id+"F12.wireOp",EDGE,"E146.1.0.32")}),1.0]])]});
            var Q77;
            Q77=makeQuery(id+"F12.imprint","IMPRINT",FACE,{"disambiguationData":[TD([[makeQuery(id+"F12.imprint","IMPRINT",EDGE,{"derivedFrom":sQuery(id+"F12.wireOp",EDGE,"E146.1.1.3")}),1.0]])]});
            var Q78;
            Q78=makeQuery(id+"F12.imprint","IMPRINT",FACE,{"disambiguationData":[TD([[makeQuery(id+"F12.imprint","IMPRINT",EDGE,{"derivedFrom":sQuery(id+"F12.wireOp",EDGE,"E146.3.0.90")}),-1.0]])]});
            var Q79;
            Q79=makeQuery(id+"F12.imprint","IMPRINT",FACE,{"disambiguationData":[TD([[makeQuery(id+"F12.imprint","IMPRINT",EDGE,{"derivedFrom":sQuery(id+"F12.wireOp",EDGE,"E146.4.0.65")}),1.0]])]});
            var Q80;
            Q80=makeQuery(id+"F12.imprint","IMPRINT",FACE,{"disambiguationData":[TD([[makeQuery(id+"F12.imprint","IMPRINT",EDGE,{"derivedFrom":sQuery(id+"F12.wireOp",EDGE,"E146.5.0.53")}),-1.0]])]});
            var Q81;
            Q81=makeQuery(id+"F12.imprint","IMPRINT",FACE,{"disambiguationData":[TD([[makeQuery(id+"F12.imprint","IMPRINT",EDGE,{"derivedFrom":sQuery(id+"F12.wireOp",EDGE,"E146.3.1.34")}),1.0]])]});
            var Q82;
            Q82=makeQuery(id+"F12.imprint","IMPRINT",FACE,{"disambiguationData":[TD([[makeQuery(id+"F12.imprint","IMPRINT",EDGE,{"derivedFrom":sQuery(id+"F12.wireOp",EDGE,"E146.1.1.73")}),1.0]])]});
            var Q83;
            Q83=makeQuery(id+"F12.imprint","IMPRINT",FACE,{"disambiguationData":[TD([[makeQuery(id+"F12.imprint","IMPRINT",EDGE,{"derivedFrom":sQuery(id+"F12.wireOp",EDGE,"E146.1.1.65")}),1.0]])]});
            var Q84;
            Q84=makeQuery(id+"F12.imprint","IMPRINT",FACE,{"disambiguationData":[TD([[makeQuery(id+"F12.imprint","IMPRINT",EDGE,{"derivedFrom":sQuery(id+"F12.wireOp",EDGE,"E146.3.1.51")}),-1.0]])]});
            var Q85;
            Q85=makeQuery(id+"F12.imprint","IMPRINT",FACE,{"disambiguationData":[TD([[makeQuery(id+"F12.imprint","IMPRINT",EDGE,{"derivedFrom":sQuery(id+"F12.wireOp",EDGE,"E146.4.0.51")}),-1.0]])]});
            var Q86;
            Q86=makeQuery(id+"F12.imprint","IMPRINT",FACE,{"disambiguationData":[TD([[makeQuery(id+"F12.imprint","IMPRINT",EDGE,{"derivedFrom":sQuery(id+"F12.wireOp",EDGE,"E146.1.0.15")}),1.0]])]});
            var Q87;
            Q87=makeQuery(id+"F12.imprint","IMPRINT",FACE,{"disambiguationData":[TD([[makeQuery(id+"F12.imprint","IMPRINT",EDGE,{"derivedFrom":sQuery(id+"F12.wireOp",EDGE,"E146.4.1.90")}),-1.0]])]});
            var Q88;
            Q88=makeQuery(id+"F12.imprint","IMPRINT",FACE,{"disambiguationData":[TD([[makeQuery(id+"F12.imprint","IMPRINT",EDGE,{"derivedFrom":sQuery(id+"F12.wireOp",EDGE,"E146.5.1.73")}),1.0]])]});
            var Q89;
            Q89=makeQuery(id+"F12.imprint","IMPRINT",FACE,{"disambiguationData":[TD([[makeQuery(id+"F12.imprint","IMPRINT",EDGE,{"derivedFrom":sQuery(id+"F12.wireOp",EDGE,"E146.1.0.73")}),1.0]])]});
            var Q90;
            Q90=makeQuery(id+"F12.imprint","IMPRINT",FACE,{"disambiguationData":[TD([[makeQuery(id+"F12.imprint","IMPRINT",EDGE,{"derivedFrom":sQuery(id+"F12.wireOp",EDGE,"E146.2.1.31")}),1.0]])]});
            var Q91;
            Q91=makeQuery(id+"F12.imprint","IMPRINT",FACE,{"disambiguationData":[TD([[makeQuery(id+"F12.imprint","IMPRINT",EDGE,{"derivedFrom":sQuery(id+"F12.wireOp",EDGE,"E146.3.1.17")}),1.0]])]});
            var Q92;
            Q92=makeQuery(id+"F12.imprint","IMPRINT",FACE,{"disambiguationData":[TD([[makeQuery(id+"F12.imprint","IMPRINT",EDGE,{"derivedFrom":sQuery(id+"F12.wireOp",EDGE,"E146.4.0.50")}),-1.0]])]});
            var Q93;
            Q93=makeQuery(id+"F12.imprint","IMPRINT",FACE,{"disambiguationData":[TD([[makeQuery(id+"F12.imprint","IMPRINT",EDGE,{"derivedFrom":sQuery(id+"F12.wireOp",EDGE,"E146.5.0.34")}),1.0]])]});
            var Q94;
            Q94=makeQuery(id+"F12.imprint","IMPRINT",FACE,{"disambiguationData":[TD([[makeQuery(id+"F12.imprint","IMPRINT",EDGE,{"derivedFrom":sQuery(id+"F12.wireOp",EDGE,"E146.5.1.90")}),-1.0]])]});
            var Q95;
            Q95=makeQuery(id+"F12.imprint","IMPRINT",FACE,{"disambiguationData":[TD([[makeQuery(id+"F12.imprint","IMPRINT",EDGE,{"derivedFrom":sQuery(id+"F12.wireOp",EDGE,"E146.5.1.16")}),1.0]])]});
            var Q96;
            Q96=makeQuery(id+"F12.imprint","IMPRINT",FACE,{"disambiguationData":[TD([[makeQuery(id+"F12.imprint","IMPRINT",EDGE,{"derivedFrom":sQuery(id+"F12.wireOp",EDGE,"E146.2.1.34")}),1.0]])]});
            var Q97;
            Q97=makeQuery(id+"F12.imprint","IMPRINT",FACE,{"disambiguationData":[TD([[makeQuery(id+"F12.imprint","IMPRINT",EDGE,{"derivedFrom":sQuery(id+"F12.wireOp",EDGE,"E146.2.0.89")}),-1.0]])]});
            var Q98;
            Q98=makeQuery(id+"F12.imprint","IMPRINT",FACE,{"disambiguationData":[TD([[makeQuery(id+"F12.imprint","IMPRINT",EDGE,{"derivedFrom":sQuery(id+"F12.wireOp",EDGE,"E146.4.0.3")}),1.0]])]});
            var Q99;
            Q99=makeQuery(id+"F12.imprint","IMPRINT",FACE,{"disambiguationData":[TD([[makeQuery(id+"F12.imprint","IMPRINT",EDGE,{"derivedFrom":sQuery(id+"F12.wireOp",EDGE,"E146.5.0.50")}),-1.0]])]});
            var Q100;
            Q100=makeQuery(id+"F12.imprint","IMPRINT",FACE,{"disambiguationData":[TD([[makeQuery(id+"F12.imprint","IMPRINT",EDGE,{"derivedFrom":sQuery(id+"F12.wireOp",EDGE,"E146.3.0.54")}),-1.0]])]});
            var Q101;
            Q101=makeQuery(id+"F12.imprint","IMPRINT",FACE,{"disambiguationData":[TD([[makeQuery(id+"F12.imprint","IMPRINT",EDGE,{"derivedFrom":sQuery(id+"F12.wireOp",EDGE,"E146.3.0.12")}),-1.0]])]});
            var Q102;
            Q102=makeQuery(id+"F12.imprint","IMPRINT",FACE,{"disambiguationData":[TD([[makeQuery(id+"F12.imprint","IMPRINT",EDGE,{"derivedFrom":sQuery(id+"F12.wireOp",EDGE,"E146.2.0.16")}),1.0]])]});
            var Q103;
            Q103=makeQuery(id+"F12.imprint","IMPRINT",FACE,{"disambiguationData":[TD([[makeQuery(id+"F12.imprint","IMPRINT",EDGE,{"derivedFrom":sQuery(id+"F12.wireOp",EDGE,"E144.bottom")}),-1.0]])]});
            var Q104;
            Q104=makeQuery(id+"F12.imprint","IMPRINT",FACE,{"disambiguationData":[TD([[makeQuery(id+"F12.imprint","IMPRINT",EDGE,{"derivedFrom":sQuery(id+"F12.wireOp",EDGE,"E145.0.2.0")}),-1.0]])]});
            var Q105;
            Q105=makeQuery(id+"F12.imprint","IMPRINT",FACE,{"disambiguationData":[TD([[makeQuery(id+"F12.imprint","IMPRINT",EDGE,{"derivedFrom":sQuery(id+"F12.wireOp",EDGE,"E145.0.4.0")}),-1.0]])]});
            var Q106;
            Q106=makeQuery(id+"F12.imprint","IMPRINT",FACE,{"disambiguationData":[TD([[makeQuery(id+"F12.imprint","IMPRINT",EDGE,{"derivedFrom":sQuery(id+"F12.wireOp",EDGE,"E145.1.0.0")}),-1.0]])]});
            var Q107;
            Q107=makeQuery(id+"F12.imprint","IMPRINT",FACE,{"disambiguationData":[TD([[makeQuery(id+"F12.imprint","IMPRINT",EDGE,{"derivedFrom":sQuery(id+"F12.wireOp",EDGE,"E145.3.0.0")}),-1.0]])]});
            var Q108;
            Q108=makeQuery(id+"F12.imprint","IMPRINT",FACE,{"disambiguationData":[TD([[makeQuery(id+"F12.imprint","IMPRINT",EDGE,{"derivedFrom":sQuery(id+"F12.wireOp",EDGE,"E145.2.4.0")}),-1.0]])]});
            var Q109;
            Q109=makeQuery(id+"F12.imprint","IMPRINT",FACE,{"disambiguationData":[TD([[makeQuery(id+"F12.imprint","IMPRINT",EDGE,{"derivedFrom":sQuery(id+"F12.wireOp",EDGE,"E146.4.1.2")}),1.0]])]});
            var Q110;
            Q110=makeQuery(id+"F12.imprint","IMPRINT",FACE,{"disambiguationData":[TD([[makeQuery(id+"F12.imprint","IMPRINT",EDGE,{"derivedFrom":sQuery(id+"F12.wireOp",EDGE,"E146.5.0.17")}),1.0]])]});
            var Q111;
            Q111=makeQuery(id+"F12.imprint","IMPRINT",FACE,{"disambiguationData":[TD([[makeQuery(id+"F12.imprint","IMPRINT",EDGE,{"derivedFrom":sQuery(id+"F12.wireOp",EDGE,"E146.4.1.52")}),-1.0]])]});
            var Q112;
            Q112=makeQuery(id+"F12.imprint","IMPRINT",FACE,{"disambiguationData":[TD([[makeQuery(id+"F12.imprint","IMPRINT",EDGE,{"derivedFrom":sQuery(id+"F12.wireOp",EDGE,"E145.3.4.0")}),-1.0]])]});
            var Q113;
            Q113=makeQuery(id+"F12.imprint","IMPRINT",FACE,{"disambiguationData":[TD([[makeQuery(id+"F12.imprint","IMPRINT",EDGE,{"derivedFrom":sQuery(id+"F12.wireOp",EDGE,"E146.2.1.14")}),1.0]])]});
            var Q114;
            Q114=makeQuery(id+"F12.imprint","IMPRINT",FACE,{"disambiguationData":[TD([[makeQuery(id+"F12.imprint","IMPRINT",EDGE,{"derivedFrom":sQuery(id+"F12.wireOp",EDGE,"E146.4.1.1")}),1.0]])]});
            var Q115;
            Q115=makeQuery(id+"F12.imprint","IMPRINT",FACE,{"disambiguationData":[TD([[makeQuery(id+"F12.imprint","IMPRINT",EDGE,{"derivedFrom":sQuery(id+"F12.wireOp",EDGE,"E146.4.1.51")}),-1.0]])]});
            var Q116;
            Q116=makeQuery(id+"F12.imprint","IMPRINT",FACE,{"disambiguationData":[TD([[makeQuery(id+"F12.imprint","IMPRINT",EDGE,{"derivedFrom":sQuery(id+"F12.wireOp",EDGE,"E146.5.1.40")}),-1.0]])]});
            var Q117;
            Q117=makeQuery(id+"F12.imprint","IMPRINT",FACE,{"disambiguationData":[TD([[makeQuery(id+"F12.imprint","IMPRINT",EDGE,{"derivedFrom":sQuery(id+"F12.wireOp",EDGE,"E146.1.1.89")}),-1.0]])]});
            var Q118;
            Q118=makeQuery(id+"F12.imprint","IMPRINT",FACE,{"disambiguationData":[TD([[makeQuery(id+"F12.imprint","IMPRINT",EDGE,{"derivedFrom":sQuery(id+"F12.wireOp",EDGE,"E146.3.0.32")}),1.0]])]});
            var Q119;
            Q119=makeQuery(id+"F12.imprint","IMPRINT",FACE,{"disambiguationData":[TD([[makeQuery(id+"F12.imprint","IMPRINT",EDGE,{"derivedFrom":sQuery(id+"F12.wireOp",EDGE,"E146.3.1.53")}),-1.0]])]});
            var Q120;
            Q120=makeQuery(id+"F12.imprint","IMPRINT",FACE,{"disambiguationData":[TD([[makeQuery(id+"F12.imprint","IMPRINT",EDGE,{"derivedFrom":sQuery(id+"F12.wireOp",EDGE,"E146.3.1.3")}),1.0]])]});
            var Q121;
            Q121=makeQuery(id+"F12.imprint","IMPRINT",FACE,{"disambiguationData":[TD([[makeQuery(id+"F12.imprint","IMPRINT",EDGE,{"derivedFrom":sQuery(id+"F12.wireOp",EDGE,"E145.3.3.0")}),-1.0]])]});
            var Q122;
            Q122=makeQuery(id+"F12.imprint","IMPRINT",FACE,{"disambiguationData":[TD([[makeQuery(id+"F12.imprint","IMPRINT",EDGE,{"derivedFrom":sQuery(id+"F12.wireOp",EDGE,"E146.5.0.89")}),-1.0]])]});
            var Q123;
            Q123=makeQuery(id+"F12.imprint","IMPRINT",FACE,{"disambiguationData":[TD([[makeQuery(id+"F12.imprint","IMPRINT",EDGE,{"derivedFrom":sQuery(id+"F12.wireOp",EDGE,"E146.3.1.2")}),1.0]])]});
            var Q124;
            Q124=makeQuery(id+"F12.imprint","IMPRINT",FACE,{"disambiguationData":[TD([[makeQuery(id+"F12.imprint","IMPRINT",EDGE,{"derivedFrom":sQuery(id+"F12.wireOp",EDGE,"E146.0.1.32")}),1.0]])]});
            var Q125;
            Q125=makeQuery(id+"F12.imprint","IMPRINT",FACE,{"disambiguationData":[TD([[makeQuery(id+"F12.imprint","IMPRINT",EDGE,{"derivedFrom":sQuery(id+"F12.wireOp",EDGE,"E145.4.1.0")}),-1.0]])]});
            var Q126;
            Q126=makeQuery(id+"F12.imprint","IMPRINT",FACE,{"disambiguationData":[TD([[makeQuery(id+"F12.imprint","IMPRINT",EDGE,{"derivedFrom":sQuery(id+"F12.wireOp",EDGE,"E146.1.0.3")}),1.0]])]});
            var Q127;
            Q127=makeQuery(id+"F12.imprint","IMPRINT",FACE,{"disambiguationData":[TD([[makeQuery(id+"F12.imprint","IMPRINT",EDGE,{"derivedFrom":sQuery(id+"F12.wireOp",EDGE,"E146.2.1.16")}),1.0]])]});
            var Q128;
            Q128=makeQuery(id+"F12.imprint","IMPRINT",FACE,{"disambiguationData":[TD([[makeQuery(id+"F12.imprint","IMPRINT",EDGE,{"derivedFrom":sQuery(id+"F12.wireOp",EDGE,"E146.2.0.51")}),-1.0]])]});
            var Q129;
            Q129=makeQuery(id+"F12.imprint","IMPRINT",FACE,{"disambiguationData":[TD([[makeQuery(id+"F12.imprint","IMPRINT",EDGE,{"derivedFrom":sQuery(id+"F12.wireOp",EDGE,"E146.5.1.52")}),-1.0]])]});
            var Q130;
            Q130=makeQuery(id+"F12.imprint","IMPRINT",FACE,{"disambiguationData":[TD([[makeQuery(id+"F12.imprint","IMPRINT",EDGE,{"derivedFrom":sQuery(id+"F12.wireOp",EDGE,"E146.5.1.2")}),1.0]])]});
            var Q131;
            Q131=makeQuery(id+"F12.imprint","IMPRINT",FACE,{"disambiguationData":[TD([[makeQuery(id+"F12.imprint","IMPRINT",EDGE,{"derivedFrom":sQuery(id+"F12.wireOp",EDGE,"E146.3.1.73")}),1.0]])]});
            var Q132;
            Q132=makeQuery(id+"F12.imprint","IMPRINT",FACE,{"disambiguationData":[TD([[makeQuery(id+"F12.imprint","IMPRINT",EDGE,{"derivedFrom":sQuery(id+"F12.wireOp",EDGE,"E146.0.1.31")}),1.0]])]});
            var Q133;
            Q133=makeQuery(id+"F12.imprint","IMPRINT",FACE,{"disambiguationData":[TD([[makeQuery(id+"F12.imprint","IMPRINT",EDGE,{"derivedFrom":sQuery(id+"F12.wireOp",EDGE,"E146.1.0.52")}),-1.0]])]});
            var Q134;
            Q134=makeQuery(id+"F12.imprint","IMPRINT",FACE,{"disambiguationData":[TD([[makeQuery(id+"F12.imprint","IMPRINT",EDGE,{"derivedFrom":sQuery(id+"F12.wireOp",EDGE,"E146.1.0.2")}),1.0]])]});
            var Q135;
            Q135=makeQuery(id+"F12.imprint","IMPRINT",FACE,{"disambiguationData":[TD([[makeQuery(id+"F12.imprint","IMPRINT",EDGE,{"derivedFrom":sQuery(id+"F12.wireOp",EDGE,"E146.4.0.32")}),1.0]])]});
            var Q136;
            Q136=makeQuery(id+"F12.imprint","IMPRINT",FACE,{"disambiguationData":[TD([[makeQuery(id+"F12.imprint","IMPRINT",EDGE,{"derivedFrom":sQuery(id+"F12.wireOp",EDGE,"E146.5.0.30")}),1.0]])]});
            var Q137;
            Q137=makeQuery(id+"F12.imprint","IMPRINT",FACE,{"disambiguationData":[TD([[makeQuery(id+"F12.imprint","IMPRINT",EDGE,{"derivedFrom":sQuery(id+"F12.wireOp",EDGE,"E146.5.1.51")}),-1.0]])]});
            var Q138;
            Q138=makeQuery(id+"F12.imprint","IMPRINT",FACE,{"disambiguationData":[TD([[makeQuery(id+"F12.imprint","IMPRINT",EDGE,{"derivedFrom":sQuery(id+"F12.wireOp",EDGE,"E146.2.1.89")}),-1.0]])]});
            var Q139;
            Q139=makeQuery(id+"F12.imprint","IMPRINT",FACE,{"disambiguationData":[TD([[makeQuery(id+"F12.imprint","IMPRINT",EDGE,{"derivedFrom":sQuery(id+"F12.wireOp",EDGE,"E146.3.1.65")}),1.0]])]});
            var Q140;
            Q140=makeQuery(id+"F12.imprint","IMPRINT",FACE,{"disambiguationData":[TD([[makeQuery(id+"F12.imprint","IMPRINT",EDGE,{"derivedFrom":sQuery(id+"F12.wireOp",EDGE,"E146.5.1.50")}),-1.0]])]});
            var Q141;
            Q141=makeQuery(id+"F12.imprint","IMPRINT",FACE,{"disambiguationData":[TD([[makeQuery(id+"F12.imprint","IMPRINT",EDGE,{"derivedFrom":sQuery(id+"F12.wireOp",EDGE,"E146.1.0.13")}),-1.0]])]});
            var Q142;
            Q142=makeQuery(id+"F12.imprint","IMPRINT",FACE,{"disambiguationData":[TD([[makeQuery(id+"F12.imprint","IMPRINT",EDGE,{"derivedFrom":sQuery(id+"F12.wireOp",EDGE,"E146.5.0.33")}),1.0]])]});
            var Q143;
            Q143=makeQuery(id+"F12.imprint","IMPRINT",FACE,{"disambiguationData":[TD([[makeQuery(id+"F12.imprint","IMPRINT",EDGE,{"derivedFrom":sQuery(id+"F12.wireOp",EDGE,"E146.5.1.54")}),-1.0]])]});
            var Q144;
            Q144=makeQuery(id+"F12.imprint","IMPRINT",FACE,{"disambiguationData":[TD([[makeQuery(id+"F12.imprint","IMPRINT",EDGE,{"derivedFrom":sQuery(id+"F12.wireOp",EDGE,"E146.3.0.51")}),-1.0]])]});
            var Q145;
            Q145=makeQuery(id+"F12.imprint","IMPRINT",FACE,{"disambiguationData":[TD([[makeQuery(id+"F12.imprint","IMPRINT",EDGE,{"derivedFrom":sQuery(id+"F12.wireOp",EDGE,"E146.3.1.90")}),-1.0]])]});
            var Q146;
            Q146=makeQuery(id+"F12.imprint","IMPRINT",FACE,{"disambiguationData":[TD([[makeQuery(id+"F12.imprint","IMPRINT",EDGE,{"derivedFrom":sQuery(id+"F12.wireOp",EDGE,"E145.4.2.0")}),-1.0]])]});
            var Q147;
            Q147=makeQuery(id+"F12.imprint","IMPRINT",FACE,{"disambiguationData":[TD([[makeQuery(id+"F12.imprint","IMPRINT",EDGE,{"derivedFrom":sQuery(id+"F12.wireOp",EDGE,"E146.3.1.15")}),1.0]])]});
            var Q148;
            Q148=makeQuery(id+"F12.imprint","IMPRINT",FACE,{"disambiguationData":[TD([[makeQuery(id+"F12.imprint","IMPRINT",EDGE,{"derivedFrom":sQuery(id+"F12.wireOp",EDGE,"E146.4.1.13")}),-1.0]])]});
            var Q149;
            Q149=makeQuery(id+"F12.imprint","IMPRINT",FACE,{"disambiguationData":[TD([[makeQuery(id+"F12.imprint","IMPRINT",EDGE,{"derivedFrom":sQuery(id+"F12.wireOp",EDGE,"E146.4.1.65")}),1.0]])]});
            var Q150;
            Q150=makeQuery(id+"F12.imprint","IMPRINT",FACE,{"disambiguationData":[TD([[makeQuery(id+"F12.imprint","IMPRINT",EDGE,{"derivedFrom":sQuery(id+"F12.wireOp",EDGE,"E146.5.1.3")}),1.0]])]});
            var Q151;
            Q151=makeQuery(id+"F12.imprint","IMPRINT",FACE,{"disambiguationData":[TD([[makeQuery(id+"F12.imprint","IMPRINT",EDGE,{"derivedFrom":sQuery(id+"F12.wireOp",EDGE,"E146.2.1.52")}),-1.0]])]});
            var Q152;
            Q152=makeQuery(id+"F12.imprint","IMPRINT",FACE,{"disambiguationData":[TD([[makeQuery(id+"F12.imprint","IMPRINT",EDGE,{"derivedFrom":sQuery(id+"F12.wireOp",EDGE,"E146.5.0.13")}),-1.0]])]});
            var Q153;
            Q153=makeQuery(id+"F12.imprint","IMPRINT",FACE,{"disambiguationData":[TD([[makeQuery(id+"F12.imprint","IMPRINT",EDGE,{"derivedFrom":sQuery(id+"F12.wireOp",EDGE,"E146.2.1.1")}),1.0]])]});
            var Q154;
            Q154=makeQuery(id+"F12.imprint","IMPRINT",FACE,{"disambiguationData":[TD([[makeQuery(id+"F12.imprint","IMPRINT",EDGE,{"derivedFrom":sQuery(id+"F12.wireOp",EDGE,"E146.2.0.30")}),1.0]])]});
            var Q155;
            Q155=makeQuery(id+"F12.imprint","IMPRINT",FACE,{"disambiguationData":[TD([[makeQuery(id+"F12.imprint","IMPRINT",EDGE,{"derivedFrom":sQuery(id+"F12.wireOp",EDGE,"E146.5.1.31")}),1.0]])]});
            var Q156;
            Q156=makeQuery(id+"F12.imprint","IMPRINT",FACE,{"disambiguationData":[TD([[makeQuery(id+"F12.imprint","IMPRINT",EDGE,{"derivedFrom":sQuery(id+"F12.wireOp",EDGE,"E146.2.1.51")}),-1.0]])]});
            var Q157;
            Q157=makeQuery(id+"F12.imprint","IMPRINT",FACE,{"disambiguationData":[TD([[makeQuery(id+"F12.imprint","IMPRINT",EDGE,{"derivedFrom":sQuery(id+"F12.wireOp",EDGE,"E146.0.1.54")}),-1.0]])]});
            var Q158;
            Q158=makeQuery(id+"F12.imprint","IMPRINT",FACE,{"disambiguationData":[TD([[makeQuery(id+"F12.imprint","IMPRINT",EDGE,{"derivedFrom":sQuery(id+"F12.wireOp",EDGE,"E146.4.1.32")}),1.0]])]});
            var Q159;
            Q159=makeQuery(id+"F12.imprint","IMPRINT",FACE,{"disambiguationData":[TD([[makeQuery(id+"F12.imprint","IMPRINT",EDGE,{"derivedFrom":sQuery(id+"F12.wireOp",EDGE,"E146.5.1.30")}),1.0]])]});
            var Q160;
            Q160=makeQuery(id+"F12.imprint","IMPRINT",FACE,{"disambiguationData":[TD([[makeQuery(id+"F12.imprint","IMPRINT",EDGE,{"derivedFrom":sQuery(id+"F12.wireOp",EDGE,"E146.1.1.2")}),1.0]])]});
            var Q161;
            Q161=makeQuery(id+"F12.imprint","IMPRINT",FACE,{"disambiguationData":[TD([[makeQuery(id+"F12.imprint","IMPRINT",EDGE,{"derivedFrom":sQuery(id+"F12.wireOp",EDGE,"E146.2.0.17")}),1.0]])]});
            var Q162;
            Q162=makeQuery(id+"F12.imprint","IMPRINT",FACE,{"disambiguationData":[TD([[makeQuery(id+"F12.imprint","IMPRINT",EDGE,{"derivedFrom":sQuery(id+"F12.wireOp",EDGE,"E146.3.0.15")}),1.0]])]});
            var Q163;
            Q163=makeQuery(id+"F12.imprint","IMPRINT",FACE,{"disambiguationData":[TD([[makeQuery(id+"F12.imprint","IMPRINT",EDGE,{"derivedFrom":sQuery(id+"F12.wireOp",EDGE,"E146.2.1.50")}),-1.0]])]});
            var Q164;
            Q164=makeQuery(id+"F12.imprint","IMPRINT",FACE,{"disambiguationData":[TD([[makeQuery(id+"F12.imprint","IMPRINT",EDGE,{"derivedFrom":sQuery(id+"F12.wireOp",EDGE,"E146.1.0.40")}),-1.0]])]});
            var Q165;
            Q165=makeQuery(id+"F12.imprint","IMPRINT",FACE,{"disambiguationData":[TD([[makeQuery(id+"F12.imprint","IMPRINT",EDGE,{"derivedFrom":sQuery(id+"F12.wireOp",EDGE,"E146.0.1.90")}),-1.0]])]});
            var Q166;
            Q166=makeQuery(id+"F12.imprint","IMPRINT",FACE,{"disambiguationData":[TD([[makeQuery(id+"F12.imprint","IMPRINT",EDGE,{"derivedFrom":sQuery(id+"F12.wireOp",EDGE,"E146.5.0.14")}),1.0]])]});
            var Q167;
            Q167=makeQuery(id+"F12.imprint","IMPRINT",FACE,{"disambiguationData":[TD([[makeQuery(id+"F12.imprint","IMPRINT",EDGE,{"derivedFrom":sQuery(id+"F12.wireOp",EDGE,"E146.5.1.33")}),1.0]])]});
            var Q168;
            Q168=makeQuery(id+"F12.imprint","IMPRINT",FACE,{"disambiguationData":[TD([[makeQuery(id+"F12.imprint","IMPRINT",EDGE,{"derivedFrom":sQuery(id+"F12.wireOp",EDGE,"E146.5.0.73")}),1.0]])]});
            var Q169;
            Q169=makeQuery(id+"F12.imprint","IMPRINT",FACE,{"disambiguationData":[TD([[makeQuery(id+"F12.imprint","IMPRINT",EDGE,{"derivedFrom":sQuery(id+"F12.wireOp",EDGE,"E146.3.0.30")}),1.0]])]});
            var Q170;
            Q170=makeQuery(id+"F12.imprint","IMPRINT",FACE,{"disambiguationData":[TD([[makeQuery(id+"F12.imprint","IMPRINT",EDGE,{"derivedFrom":sQuery(id+"F12.wireOp",EDGE,"E146.2.1.53")}),-1.0]])]});
            var Q171;
            Q171=makeQuery(id+"F12.imprint","IMPRINT",FACE,{"disambiguationData":[TD([[makeQuery(id+"F12.imprint","IMPRINT",EDGE,{"derivedFrom":sQuery(id+"F12.wireOp",EDGE,"E146.0.1.15")}),1.0]])]});
            var Q172;
            Q172=makeQuery(id+"F12.imprint","IMPRINT",FACE,{"disambiguationData":[TD([[makeQuery(id+"F12.imprint","IMPRINT",EDGE,{"derivedFrom":sQuery(id+"F12.wireOp",EDGE,"E145.3.1.0")}),-1.0]])]});
            var Q173;
            Q173=makeQuery(id+"F12.imprint","IMPRINT",FACE,{"disambiguationData":[TD([[makeQuery(id+"F12.imprint","IMPRINT",EDGE,{"derivedFrom":sQuery(id+"F12.wireOp",EDGE,"E146.1.0.34")}),1.0]])]});
            var Q174;
            Q174=makeQuery(id+"F12.imprint","IMPRINT",FACE,{"disambiguationData":[TD([[makeQuery(id+"F12.imprint","IMPRINT",EDGE,{"derivedFrom":sQuery(id+"F12.wireOp",EDGE,"E146.2.1.32")}),1.0]])]});
            var Q175;
            Q175=makeQuery(id+"F12.imprint","IMPRINT",FACE,{"disambiguationData":[TD([[makeQuery(id+"F12.imprint","IMPRINT",EDGE,{"derivedFrom":sQuery(id+"F12.wireOp",EDGE,"E146.2.0.65")}),1.0]])]});
            var Q176;
            Q176=makeQuery(id+"F12.imprint","IMPRINT",FACE,{"disambiguationData":[TD([[makeQuery(id+"F12.imprint","IMPRINT",EDGE,{"derivedFrom":sQuery(id+"F12.wireOp",EDGE,"E146.3.0.3")}),1.0]])]});
            var Q177;
            Q177=makeQuery(id+"F12.imprint","IMPRINT",FACE,{"disambiguationData":[TD([[makeQuery(id+"F12.imprint","IMPRINT",EDGE,{"derivedFrom":sQuery(id+"F12.wireOp",EDGE,"E146.3.1.30")}),1.0]])]});
            var Q178;
            Q178=makeQuery(id+"F12.imprint","IMPRINT",FACE,{"disambiguationData":[TD([[makeQuery(id+"F12.imprint","IMPRINT",EDGE,{"derivedFrom":sQuery(id+"F12.wireOp",EDGE,"E146.1.0.89")}),-1.0]])]});
            var Q179;
            Q179=makeQuery(id+"F12.imprint","IMPRINT",FACE,{"disambiguationData":[TD([[makeQuery(id+"F12.imprint","IMPRINT",EDGE,{"derivedFrom":sQuery(id+"F12.wireOp",EDGE,"E146.5.0.40")}),-1.0]])]});
            var Q180;
            Q180=makeQuery(id+"F12.imprint","IMPRINT",FACE,{"disambiguationData":[TD([[makeQuery(id+"F12.imprint","IMPRINT",EDGE,{"derivedFrom":sQuery(id+"F12.wireOp",EDGE,"E146.5.1.14")}),1.0]])]});
            var Q181;
            Q181=makeQuery(id+"F12.imprint","IMPRINT",FACE,{"disambiguationData":[TD([[makeQuery(id+"F12.imprint","IMPRINT",EDGE,{"derivedFrom":sQuery(id+"F12.wireOp",EDGE,"E146.1.0.14")}),1.0]])]});
            var Q182;
            Q182=makeQuery(id+"F12.imprint","IMPRINT",FACE,{"disambiguationData":[TD([[makeQuery(id+"F12.imprint","IMPRINT",EDGE,{"derivedFrom":sQuery(id+"F12.wireOp",EDGE,"E146.1.1.33")}),1.0]])]});
            var Q183;
            Q183=makeQuery(id+"F12.imprint","IMPRINT",FACE,{"disambiguationData":[TD([[makeQuery(id+"F12.imprint","IMPRINT",EDGE,{"derivedFrom":sQuery(id+"F12.wireOp",EDGE,"E146.3.0.2")}),1.0]])]});
            var Q184;
            Q184=makeQuery(id+"F12.imprint","IMPRINT",FACE,{"disambiguationData":[TD([[makeQuery(id+"F12.imprint","IMPRINT",EDGE,{"derivedFrom":sQuery(id+"F12.wireOp",EDGE,"E146.4.0.0")}),1.0]])]});
            var Q185;
            Q185=makeQuery(id+"F12.imprint","IMPRINT",FACE,{"disambiguationData":[TD([[makeQuery(id+"F12.imprint","IMPRINT",EDGE,{"derivedFrom":sQuery(id+"F12.wireOp",EDGE,"E146.5.1.13")}),-1.0]])]});
            var Q186;
            Q186=makeQuery(id+"F12.imprint","IMPRINT",FACE,{"disambiguationData":[TD([[makeQuery(id+"F12.imprint","IMPRINT",EDGE,{"derivedFrom":sQuery(id+"F12.wireOp",EDGE,"E146.1.0.17")}),1.0]])]});
            var Q187;
            Q187=makeQuery(id+"F12.imprint","IMPRINT",FACE,{"disambiguationData":[TD([[makeQuery(id+"F12.imprint","IMPRINT",EDGE,{"derivedFrom":sQuery(id+"F12.wireOp",EDGE,"E146.5.0.51")}),-1.0]])]});
            var Q188;
            Q188=makeQuery(id+"F12.imprint","IMPRINT",FACE,{"disambiguationData":[TD([[makeQuery(id+"F12.imprint","IMPRINT",EDGE,{"derivedFrom":sQuery(id+"F12.wireOp",EDGE,"E146.3.1.32")}),1.0]])]});
            var Q189;
            Q189=makeQuery(id+"F12.imprint","IMPRINT",FACE,{"disambiguationData":[TD([[makeQuery(id+"F12.imprint","IMPRINT",EDGE,{"derivedFrom":sQuery(id+"F12.wireOp",EDGE,"E146.4.1.30")}),1.0]])]});
            var Q190;
            Q190=makeQuery(id+"F12.imprint","IMPRINT",FACE,{"disambiguationData":[TD([[makeQuery(id+"F12.imprint","IMPRINT",EDGE,{"derivedFrom":sQuery(id+"F12.wireOp",EDGE,"E146.4.0.53")}),-1.0]])]});
            var Q191;
            Q191=makeQuery(id+"F12.imprint","IMPRINT",FACE,{"disambiguationData":[TD([[makeQuery(id+"F12.imprint","IMPRINT",EDGE,{"derivedFrom":sQuery(id+"F12.wireOp",EDGE,"E146.0.1.1")}),1.0]])]});
            var Q192;
            Q192=makeQuery(id+"F12.imprint","IMPRINT",FACE,{"disambiguationData":[TD([[makeQuery(id+"F12.imprint","IMPRINT",EDGE,{"derivedFrom":sQuery(id+"F12.wireOp",EDGE,"E146.3.1.31")}),1.0]])]});
            var Q193;
            Q193=makeQuery(id+"F12.imprint","IMPRINT",FACE,{"disambiguationData":[TD([[makeQuery(id+"F12.imprint","IMPRINT",EDGE,{"derivedFrom":sQuery(id+"F12.wireOp",EDGE,"E146.5.0.0")}),1.0]])]});
            var Q194;
            Q194=makeQuery(id+"F12.imprint","IMPRINT",FACE,{"disambiguationData":[TD([[makeQuery(id+"F12.imprint","IMPRINT",EDGE,{"derivedFrom":sQuery(id+"F12.wireOp",EDGE,"E146.5.1.89")}),-1.0]])]});
            var Q195;
            Q195=makeQuery(id+"F12.imprint","IMPRINT",FACE,{"disambiguationData":[TD([[makeQuery(id+"F12.imprint","IMPRINT",EDGE,{"derivedFrom":sQuery(id+"F12.wireOp",EDGE,"E146.5.1.15")}),1.0]])]});
            var Q196;
            Q196=makeQuery(id+"F12.imprint","IMPRINT",FACE,{"disambiguationData":[TD([[makeQuery(id+"F12.imprint","IMPRINT",EDGE,{"derivedFrom":sQuery(id+"F12.wireOp",EDGE,"E146.2.1.33")}),1.0]])]});
            var Q197;
            Q197=makeQuery(id+"F12.imprint","IMPRINT",FACE,{"disambiguationData":[TD([[makeQuery(id+"F12.imprint","IMPRINT",EDGE,{"derivedFrom":sQuery(id+"F12.wireOp",EDGE,"E146.2.0.73")}),1.0]])]});
            var Q198;
            Q198=makeQuery(id+"F12.imprint","IMPRINT",FACE,{"disambiguationData":[TD([[makeQuery(id+"F12.imprint","IMPRINT",EDGE,{"derivedFrom":sQuery(id+"F12.wireOp",EDGE,"E146.1.1.1")}),1.0]])]});
            var Q199;
            Q199=makeQuery(id+"F12.imprint","IMPRINT",FACE,{"disambiguationData":[TD([[makeQuery(id+"F12.imprint","IMPRINT",EDGE,{"derivedFrom":sQuery(id+"F12.wireOp",EDGE,"E146.1.0.30")}),1.0]])]});
            var Q200;
            Q200=makeQuery(id+"F12.imprint","IMPRINT",FACE,{"disambiguationData":[TD([[makeQuery(id+"F12.imprint","IMPRINT",EDGE,{"derivedFrom":sQuery(id+"F12.wireOp",EDGE,"E146.1.1.51")}),-1.0]])]});
            var Q201;
            Q201=makeQuery(id+"F12.imprint","IMPRINT",FACE,{"disambiguationData":[TD([[makeQuery(id+"F12.imprint","IMPRINT",EDGE,{"derivedFrom":sQuery(id+"F12.wireOp",EDGE,"E146.2.1.40")}),-1.0]])]});
            var Q202;
            Q202=makeQuery(id+"F12.imprint","IMPRINT",FACE,{"disambiguationData":[TD([[makeQuery(id+"F12.imprint","IMPRINT",EDGE,{"derivedFrom":sQuery(id+"F12.wireOp",EDGE,"E146.5.0.52")}),-1.0]])]});
            var Q203;
            Q203=makeQuery(id+"F12.imprint","IMPRINT",FACE,{"disambiguationData":[TD([[makeQuery(id+"F12.imprint","IMPRINT",EDGE,{"derivedFrom":sQuery(id+"F12.wireOp",EDGE,"E146.5.0.2")}),1.0]])]});
            var Q204;
            Q204=makeQuery(id+"F12.imprint","IMPRINT",FACE,{"disambiguationData":[TD([[makeQuery(id+"F12.imprint","IMPRINT",EDGE,{"derivedFrom":sQuery(id+"F12.wireOp",EDGE,"E145.0.1.0")}),-1.0]])]});
            var Q205;
            Q205=makeQuery(id+"F12.imprint","IMPRINT",FACE,{"disambiguationData":[TD([[makeQuery(id+"F12.imprint","IMPRINT",EDGE,{"derivedFrom":sQuery(id+"F12.wireOp",EDGE,"E145.0.3.0")}),-1.0]])]});
            var Q206;
            Q206=makeQuery(id+"F12.imprint","IMPRINT",FACE,{"disambiguationData":[TD([[makeQuery(id+"F12.imprint","IMPRINT",EDGE,{"derivedFrom":sQuery(id+"F12.wireOp",EDGE,"E145.2.3.0")}),-1.0]])]});
            var Q207;
            Q207=makeQuery(id+"F12.imprint","IMPRINT",FACE,{"disambiguationData":[TD([[makeQuery(id+"F12.imprint","IMPRINT",EDGE,{"derivedFrom":sQuery(id+"F12.wireOp",EDGE,"E145.1.1.0")}),-1.0]])]});
            var Q208;
            Q208=makeQuery(id+"F12.imprint","IMPRINT",FACE,{"disambiguationData":[TD([[makeQuery(id+"F12.imprint","IMPRINT",EDGE,{"derivedFrom":sQuery(id+"F12.wireOp",EDGE,"E145.1.3.0")}),-1.0]])]});
            var Q209;
            Q209=makeQuery(id+"F12.imprint","IMPRINT",FACE,{"disambiguationData":[TD([[makeQuery(id+"F12.imprint","IMPRINT",EDGE,{"derivedFrom":sQuery(id+"F12.wireOp",EDGE,"E145.1.4.0")}),-1.0]])]});
            var Q210;
            Q210=makeQuery(id+"F12.imprint","IMPRINT",FACE,{"disambiguationData":[TD([[makeQuery(id+"F12.imprint","IMPRINT",EDGE,{"derivedFrom":sQuery(id+"F12.wireOp",EDGE,"E145.2.2.0")}),-1.0]])]});
            var Q211;
            Q211=makeQuery(id+"F12.imprint","IMPRINT",FACE,{"disambiguationData":[TD([[makeQuery(id+"F12.imprint","IMPRINT",EDGE,{"derivedFrom":sQuery(id+"F12.wireOp",EDGE,"E146.3.0.33")}),1.0]])]});
            var Q212;
            Q212=makeQuery(id+"F12.imprint","IMPRINT",FACE,{"disambiguationData":[TD([[makeQuery(id+"F12.imprint","IMPRINT",EDGE,{"derivedFrom":sQuery(id+"F12.wireOp",EDGE,"E146.0.1.30")}),1.0]])]});
            var Q213;
            Q213=makeQuery(id+"F12.imprint","IMPRINT",FACE,{"disambiguationData":[TD([[makeQuery(id+"F12.imprint","IMPRINT",EDGE,{"derivedFrom":sQuery(id+"F12.wireOp",EDGE,"E146.1.1.15")}),1.0]])]});
            var Q214;
            Q214=makeQuery(id+"F12.imprint","IMPRINT",FACE,{"disambiguationData":[TD([[makeQuery(id+"F12.imprint","IMPRINT",EDGE,{"derivedFrom":sQuery(id+"F12.wireOp",EDGE,"E146.2.1.13")}),-1.0]])]});
            var Q215;
            Q215=makeQuery(id+"F12.imprint","IMPRINT",FACE,{"disambiguationData":[TD([[makeQuery(id+"F12.imprint","IMPRINT",EDGE,{"derivedFrom":sQuery(id+"F12.wireOp",EDGE,"E146.2.0.34")}),1.0]])]});
            var Q216;
            Q216=makeQuery(id+"F12.imprint","IMPRINT",FACE,{"disambiguationData":[TD([[makeQuery(id+"F12.imprint","IMPRINT",EDGE,{"derivedFrom":sQuery(id+"F12.wireOp",EDGE,"E146.1.0.50")}),-1.0]])]});
            var Q217;
            Q217=makeQuery(id+"F12.imprint","IMPRINT",FACE,{"disambiguationData":[TD([[makeQuery(id+"F12.imprint","IMPRINT",EDGE,{"derivedFrom":sQuery(id+"F12.wireOp",EDGE,"E146.1.0.0")}),1.0]])]});
            var Q218;
            Q218=makeQuery(id+"F12.imprint","IMPRINT",FACE,{"disambiguationData":[TD([[makeQuery(id+"F12.imprint","IMPRINT",EDGE,{"derivedFrom":sQuery(id+"F12.wireOp",EDGE,"E146.3.1.52")}),-1.0]])]});
            var Q219;
            Q219=makeQuery(id+"F12.imprint","IMPRINT",FACE,{"disambiguationData":[TD([[makeQuery(id+"F12.imprint","IMPRINT",EDGE,{"derivedFrom":sQuery(id+"F12.wireOp",EDGE,"E146.4.1.50")}),-1.0]])]});
            var Q220;
            Q220=makeQuery(id+"F12.imprint","IMPRINT",FACE,{"disambiguationData":[TD([[makeQuery(id+"F12.imprint","IMPRINT",EDGE,{"derivedFrom":sQuery(id+"F12.wireOp",EDGE,"E146.4.0.33")}),1.0]])]});
            var Q221;
            Q221=makeQuery(id+"F12.imprint","IMPRINT",FACE,{"disambiguationData":[TD([[makeQuery(id+"F12.imprint","IMPRINT",EDGE,{"derivedFrom":sQuery(id+"F12.wireOp",EDGE,"E146.4.1.53")}),-1.0]])]});
            var Q222;
            Q222=makeQuery(id+"F12.imprint","IMPRINT",FACE,{"disambiguationData":[TD([[makeQuery(id+"F12.imprint","IMPRINT",EDGE,{"derivedFrom":sQuery(id+"F12.wireOp",EDGE,"E146.2.0.0")}),1.0]])]});
            var Q223;
            Q223=makeQuery(id+"F12.imprint","IMPRINT",FACE,{"disambiguationData":[TD([[makeQuery(id+"F12.imprint","IMPRINT",EDGE,{"derivedFrom":sQuery(id+"F12.wireOp",EDGE,"E146.2.1.15")}),1.0]])]});
            var Q224;
            Q224=makeQuery(id+"F12.imprint","IMPRINT",FACE,{"disambiguationData":[TD([[makeQuery(id+"F12.imprint","IMPRINT",EDGE,{"derivedFrom":sQuery(id+"F12.wireOp",EDGE,"E146.3.1.13")}),-1.0]])]});
            var Q225;
            Q225=makeQuery(id+"F12.imprint","IMPRINT",FACE,{"disambiguationData":[TD([[makeQuery(id+"F12.imprint","IMPRINT",EDGE,{"derivedFrom":sQuery(id+"F12.wireOp",EDGE,"E146.2.0.3")}),1.0]])]});
            var Q226;
            Q226=makeQuery(id+"F12.imprint","IMPRINT",FACE,{"disambiguationData":[TD([[makeQuery(id+"F12.imprint","IMPRINT",EDGE,{"derivedFrom":sQuery(id+"F12.wireOp",EDGE,"E146.1.1.32")}),1.0]])]});
            var Q227;
            Q227=makeQuery(id+"F12.imprint","IMPRINT",FACE,{"disambiguationData":[TD([[makeQuery(id+"F12.imprint","IMPRINT",EDGE,{"derivedFrom":sQuery(id+"F12.wireOp",EDGE,"E146.2.1.30")}),1.0]])]});
            var Q228;
            Q228=makeQuery(id+"F12.imprint","IMPRINT",FACE,{"disambiguationData":[TD([[makeQuery(id+"F12.imprint","IMPRINT",EDGE,{"derivedFrom":sQuery(id+"F12.wireOp",EDGE,"E146.2.0.53")}),-1.0]])]});
            var Q229;
            Q229=makeQuery(id+"F12.imprint","IMPRINT",FACE,{"disambiguationData":[TD([[makeQuery(id+"F12.imprint","IMPRINT",EDGE,{"derivedFrom":sQuery(id+"F12.wireOp",EDGE,"E146.4.1.14")}),1.0]])]});
            var Q230;
            Q230=makeQuery(id+"F12.imprint","IMPRINT",FACE,{"disambiguationData":[TD([[makeQuery(id+"F12.imprint","IMPRINT",EDGE,{"derivedFrom":sQuery(id+"F12.wireOp",EDGE,"E146.4.0.40")}),-1.0]])]});
            var Q231;
            Q231=makeQuery(id+"F12.imprint","IMPRINT",FACE,{"disambiguationData":[TD([[makeQuery(id+"F12.imprint","IMPRINT",EDGE,{"derivedFrom":sQuery(id+"F12.wireOp",EDGE,"E146.0.1.33")}),1.0]])]});
            var Q232;
            Q232=makeQuery(id+"F12.imprint","IMPRINT",FACE,{"disambiguationData":[TD([[makeQuery(id+"F12.imprint","IMPRINT",EDGE,{"derivedFrom":sQuery(id+"F12.wireOp",EDGE,"E146.3.1.89")}),-1.0]])]});
            var Q233;
            Q233=makeQuery(id+"F12.imprint","IMPRINT",FACE,{"disambiguationData":[TD([[makeQuery(id+"F12.imprint","IMPRINT",EDGE,{"derivedFrom":sQuery(id+"F12.wireOp",EDGE,"E146.5.1.53")}),-1.0]])]});
            var Q234;
            Q234=makeQuery(id+"F12.imprint","IMPRINT",FACE,{"disambiguationData":[TD([[makeQuery(id+"F12.imprint","IMPRINT",EDGE,{"derivedFrom":sQuery(id+"F12.wireOp",EDGE,"E146.3.0.0")}),1.0]])]});
            var Q235;
            Q235=makeQuery(id+"F12.imprint","IMPRINT",FACE,{"disambiguationData":[TD([[makeQuery(id+"F12.imprint","IMPRINT",EDGE,{"derivedFrom":sQuery(id+"F12.wireOp",EDGE,"E146.4.0.15")}),1.0]])]});
            var Q236;
            Q236=makeQuery(id+"F12.imprint","IMPRINT",FACE,{"disambiguationData":[TD([[makeQuery(id+"F12.imprint","IMPRINT",EDGE,{"derivedFrom":sQuery(id+"F12.wireOp",EDGE,"E146.3.1.50")}),-1.0]])]});
            var Q237;
            Q237=makeQuery(id+"F12.imprint","IMPRINT",FACE,{"disambiguationData":[TD([[makeQuery(id+"F12.imprint","IMPRINT",EDGE,{"derivedFrom":sQuery(id+"F12.wireOp",EDGE,"E146.0.1.73")}),1.0]])]});
            var Q238;
            Q238=makeQuery(id+"F12.imprint","IMPRINT",FACE,{"disambiguationData":[TD([[makeQuery(id+"F12.imprint","IMPRINT",EDGE,{"derivedFrom":sQuery(id+"F12.wireOp",EDGE,"E146.0.1.14")}),1.0]])]});
            var Q239;
            Q239=makeQuery(id+"F12.imprint","IMPRINT",FACE,{"disambiguationData":[TD([[makeQuery(id+"F12.imprint","IMPRINT",EDGE,{"derivedFrom":sQuery(id+"F12.wireOp",EDGE,"E146.5.0.65")}),1.0]])]});
            var Q240;
            Q240=makeQuery(id+"F12.imprint","IMPRINT",FACE,{"disambiguationData":[TD([[makeQuery(id+"F12.imprint","IMPRINT",EDGE,{"derivedFrom":sQuery(id+"F12.wireOp",EDGE,"E146.5.1.32")}),1.0]])]});
            var Q241;
            Q241=makeQuery(id+"F12.imprint","IMPRINT",FACE,{"disambiguationData":[TD([[makeQuery(id+"F12.imprint","IMPRINT",EDGE,{"derivedFrom":sQuery(id+"F12.wireOp",EDGE,"E146.1.1.53")}),-1.0]])]});
            var Q242;
            Q242=makeQuery(id+"F12.imprint","IMPRINT",FACE,{"disambiguationData":[TD([[makeQuery(id+"F12.imprint","IMPRINT",EDGE,{"derivedFrom":sQuery(id+"F12.wireOp",EDGE,"E146.3.1.40")}),-1.0]])]});
            var Q243;
            Q243=makeQuery(id+"F12.imprint","IMPRINT",FACE,{"disambiguationData":[TD([[makeQuery(id+"F12.imprint","IMPRINT",EDGE,{"derivedFrom":sQuery(id+"F12.wireOp",EDGE,"E146.4.0.14")}),1.0]])]});
            var Q244;
            Q244=makeQuery(id+"F12.imprint","IMPRINT",FACE,{"disambiguationData":[TD([[makeQuery(id+"F12.imprint","IMPRINT",EDGE,{"derivedFrom":sQuery(id+"F12.wireOp",EDGE,"E146.5.0.12")}),-1.0]])]});
            var Q245;
            Q245=makeQuery(id+"F12.imprint","IMPRINT",FACE,{"disambiguationData":[TD([[makeQuery(id+"F12.imprint","IMPRINT",EDGE,{"derivedFrom":sQuery(id+"F12.wireOp",EDGE,"E146.4.1.33")}),1.0]])]});
            var Q246;
            Q246=makeQuery(id+"F12.imprint","IMPRINT",FACE,{"disambiguationData":[TD([[makeQuery(id+"F12.imprint","IMPRINT",EDGE,{"derivedFrom":sQuery(id+"F12.wireOp",EDGE,"E146.0.1.12")}),-1.0]])]});
            var Q247;
            Q247=makeQuery(id+"F12.imprint","IMPRINT",FACE,{"disambiguationData":[TD([[makeQuery(id+"F12.imprint","IMPRINT",EDGE,{"derivedFrom":sQuery(id+"F12.wireOp",EDGE,"E146.1.0.31")}),1.0]])]});
            var Q248;
            Q248=makeQuery(id+"F12.imprint","IMPRINT",FACE,{"disambiguationData":[TD([[makeQuery(id+"F12.imprint","IMPRINT",EDGE,{"derivedFrom":sQuery(id+"F12.wireOp",EDGE,"E146.4.0.13")}),-1.0]])]});
            var Q249;
            Q249=makeQuery(id+"F12.imprint","IMPRINT",FACE,{"disambiguationData":[TD([[makeQuery(id+"F12.imprint","IMPRINT",EDGE,{"derivedFrom":sQuery(id+"F12.wireOp",EDGE,"E146.5.0.3")}),1.0]])]});
            var Q250;
            Q250=makeQuery(id+"F12.imprint","IMPRINT",FACE,{"disambiguationData":[TD([[makeQuery(id+"F12.imprint","IMPRINT",EDGE,{"derivedFrom":sQuery(id+"F12.wireOp",EDGE,"E146.2.1.0")}),1.0]])]});
            var Q251;
            Q251=makeQuery(id+"F12.imprint","IMPRINT",FACE,{"disambiguationData":[TD([[makeQuery(id+"F12.imprint","IMPRINT",EDGE,{"derivedFrom":sQuery(id+"F12.wireOp",EDGE,"E146.3.0.89")}),-1.0]])]});
            var Q252;
            Q252=makeQuery(id+"F12.imprint","IMPRINT",FACE,{"disambiguationData":[TD([[makeQuery(id+"F12.imprint","IMPRINT",EDGE,{"derivedFrom":sQuery(id+"F12.wireOp",EDGE,"E145.3.2.0")}),-1.0]])]});
            var Q253;
            Q253=makeQuery(id+"F12.imprint","IMPRINT",FACE,{"disambiguationData":[TD([[makeQuery(id+"F12.imprint","IMPRINT",EDGE,{"derivedFrom":sQuery(id+"F12.wireOp",EDGE,"E146.2.0.33")}),1.0]])]});
            var Q254;
            Q254=makeQuery(id+"F12.imprint","IMPRINT",FACE,{"disambiguationData":[TD([[makeQuery(id+"F12.imprint","IMPRINT",EDGE,{"derivedFrom":sQuery(id+"F12.wireOp",EDGE,"E146.4.1.40")}),-1.0]])]});
            var Q255;
            Q255=makeQuery(id+"F12.imprint","IMPRINT",FACE,{"disambiguationData":[TD([[makeQuery(id+"F12.imprint","IMPRINT",EDGE,{"derivedFrom":sQuery(id+"F12.wireOp",EDGE,"E146.1.1.13")}),-1.0]])]});
            var Q256;
            Q256=makeQuery(id+"F12.imprint","IMPRINT",FACE,{"disambiguationData":[TD([[makeQuery(id+"F12.imprint","IMPRINT",EDGE,{"derivedFrom":sQuery(id+"F12.wireOp",EDGE,"E146.2.0.32")}),1.0]])]});
            var Q257;
            Q257=makeQuery(id+"F12.imprint","IMPRINT",FACE,{"disambiguationData":[TD([[makeQuery(id+"F12.imprint","IMPRINT",EDGE,{"derivedFrom":sQuery(id+"F12.wireOp",EDGE,"E146.3.1.1")}),1.0]])]});
            var Q258;
            Q258=makeQuery(id+"F12.imprint","IMPRINT",FACE,{"disambiguationData":[TD([[makeQuery(id+"F12.imprint","IMPRINT",EDGE,{"derivedFrom":sQuery(id+"F12.wireOp",EDGE,"E146.0.1.89")}),-1.0]])]});
            var Q259;
            Q259=makeQuery(id+"F12.imprint","IMPRINT",FACE,{"disambiguationData":[TD([[makeQuery(id+"F12.imprint","IMPRINT",EDGE,{"derivedFrom":sQuery(id+"F12.wireOp",EDGE,"E146.3.0.53")}),-1.0]])]});
            var Q260;
            Q260=makeQuery(id+"F12.imprint","IMPRINT",FACE,{"disambiguationData":[TD([[makeQuery(id+"F12.imprint","IMPRINT",EDGE,{"derivedFrom":sQuery(id+"F12.wireOp",EDGE,"E146.0.1.50")}),-1.0]])]});
            var Q261;
            Q261=makeQuery(id+"F12.imprint","IMPRINT",FACE,{"disambiguationData":[TD([[makeQuery(id+"F12.imprint","IMPRINT",EDGE,{"derivedFrom":sQuery(id+"F12.wireOp",EDGE,"E146.2.0.13")}),-1.0]])]});
            var Q262;
            Q262=makeQuery(id+"F12.imprint","IMPRINT",FACE,{"disambiguationData":[TD([[makeQuery(id+"F12.imprint","IMPRINT",EDGE,{"derivedFrom":sQuery(id+"F12.wireOp",EDGE,"E146.2.0.54")}),-1.0]])]});
            var Q263;
            Q263=makeQuery(id+"F12.imprint","IMPRINT",FACE,{"disambiguationData":[TD([[makeQuery(id+"F12.imprint","IMPRINT",EDGE,{"derivedFrom":sQuery(id+"F12.wireOp",EDGE,"E146.4.1.89")}),-1.0]])]});
            var Q264;
            Q264=makeQuery(id+"F12.imprint","IMPRINT",FACE,{"disambiguationData":[TD([[makeQuery(id+"F12.imprint","IMPRINT",EDGE,{"derivedFrom":sQuery(id+"F12.wireOp",EDGE,"E146.0.1.52")}),-1.0]])]});
            var Q265;
            Q265=makeQuery(id+"F12.imprint","IMPRINT",FACE,{"disambiguationData":[TD([[makeQuery(id+"F12.imprint","IMPRINT",EDGE,{"derivedFrom":sQuery(id+"F12.wireOp",EDGE,"E146.0.1.2")}),1.0]])]});
            var Q266;
            Q266=makeQuery(id+"F12.imprint","IMPRINT",FACE,{"disambiguationData":[TD([[makeQuery(id+"F12.imprint","IMPRINT",EDGE,{"derivedFrom":sQuery(id+"F12.wireOp",EDGE,"E146.2.0.15")}),1.0]])]});
            var Q267;
            Q267=makeQuery(id+"F12.imprint","IMPRINT",FACE,{"disambiguationData":[TD([[makeQuery(id+"F12.imprint","IMPRINT",EDGE,{"derivedFrom":sQuery(id+"F12.wireOp",EDGE,"E146.1.1.50")}),-1.0]])]});
            var Q268;
            Q268=makeQuery(id+"F12.imprint","IMPRINT",FACE,{"disambiguationData":[TD([[makeQuery(id+"F12.imprint","IMPRINT",EDGE,{"derivedFrom":sQuery(id+"F12.wireOp",EDGE,"E146.3.0.65")}),1.0]])]});
            var Q269;
            Q269=makeQuery(id+"F12.imprint","IMPRINT",FACE,{"disambiguationData":[TD([[makeQuery(id+"F12.imprint","IMPRINT",EDGE,{"derivedFrom":sQuery(id+"F12.wireOp",EDGE,"E146.0.1.51")}),-1.0]])]});
            var Q270;
            Q270=makeQuery(id+"F12.imprint","IMPRINT",FACE,{"disambiguationData":[TD([[makeQuery(id+"F12.imprint","IMPRINT",EDGE,{"derivedFrom":sQuery(id+"F12.wireOp",EDGE,"E146.4.0.2")}),1.0]])]});
            var Q271;
            Q271=makeQuery(id+"F12.imprint","IMPRINT",FACE,{"disambiguationData":[TD([[makeQuery(id+"F12.imprint","IMPRINT",EDGE,{"derivedFrom":sQuery(id+"F12.wireOp",EDGE,"E146.4.0.52")}),-1.0]])]});
            var Q272;
            Q272=makeQuery(id+"F12.imprint","IMPRINT",FACE,{"disambiguationData":[TD([[makeQuery(id+"F12.imprint","IMPRINT",EDGE,{"derivedFrom":sQuery(id+"F12.wireOp",EDGE,"E146.3.0.73")}),1.0]])]});
            var Q273;
            Q273=makeQuery(id+"F12.imprint","IMPRINT",FACE,{"disambiguationData":[TD([[makeQuery(id+"F12.imprint","IMPRINT",EDGE,{"derivedFrom":sQuery(id+"F12.wireOp",EDGE,"E146.3.0.14")}),1.0]])]});
            var Q274;
            Q274=makeQuery(id+"F12.imprint","IMPRINT",FACE,{"disambiguationData":[TD([[makeQuery(id+"F12.imprint","IMPRINT",EDGE,{"derivedFrom":sQuery(id+"F12.wireOp",EDGE,"E146.0.1.53")}),-1.0]])]});
            var Q275;
            Q275=makeQuery(id+"F12.imprint","IMPRINT",FACE,{"disambiguationData":[TD([[makeQuery(id+"F12.imprint","IMPRINT",EDGE,{"derivedFrom":sQuery(id+"F12.wireOp",EDGE,"E146.3.1.33")}),1.0]])]});
            var Q276;
            Q276=makeQuery(id+"F12.imprint","IMPRINT",FACE,{"disambiguationData":[TD([[makeQuery(id+"F12.imprint","IMPRINT",EDGE,{"derivedFrom":sQuery(id+"F12.wireOp",EDGE,"E146.4.1.31")}),1.0]])]});
            var Q277;
            Q277=makeQuery(id+"F12.imprint","IMPRINT",FACE,{"disambiguationData":[TD([[makeQuery(id+"F12.imprint","IMPRINT",EDGE,{"derivedFrom":sQuery(id+"F12.wireOp",EDGE,"E145.1.2.0")}),-1.0]])]});
            var Q278;
            Q278=makeQuery(id+"F12.imprint","IMPRINT",FACE,{"disambiguationData":[TD([[makeQuery(id+"F12.imprint","IMPRINT",EDGE,{"derivedFrom":sQuery(id+"F12.wireOp",EDGE,"E145.2.1.0")}),-1.0]])]});
            var Q279;
            Q279=makeQuery(id+"F12.imprint","IMPRINT",FACE,{"disambiguationData":[TD([[makeQuery(id+"F12.imprint","IMPRINT",EDGE,{"derivedFrom":sQuery(id+"F12.wireOp",EDGE,"E146.2.0.40")}),-1.0]])]});
            var Q280;
            Q280=makeQuery(id+"F12.imprint","IMPRINT",FACE,{"disambiguationData":[TD([[makeQuery(id+"F12.imprint","IMPRINT",EDGE,{"derivedFrom":sQuery(id+"F12.wireOp",EDGE,"E146.4.1.0")}),1.0]])]});
            var Q281;
            Q281=makeQuery(id+"F12.imprint","IMPRINT",FACE,{"disambiguationData":[TD([[makeQuery(id+"F12.imprint","IMPRINT",EDGE,{"derivedFrom":sQuery(id+"F12.wireOp",EDGE,"E146.1.1.30")}),1.0]])]});
            var Q282;
            Q282=makeQuery(id+"F12.imprint","IMPRINT",FACE,{"disambiguationData":[TD([[makeQuery(id+"F12.imprint","IMPRINT",EDGE,{"derivedFrom":sQuery(id+"F12.wireOp",EDGE,"E146.3.0.40")}),-1.0]])]});
            var Q283;
            Q283=makeQuery(id+"F12.imprint","IMPRINT",FACE,{"disambiguationData":[TD([[makeQuery(id+"F12.imprint","IMPRINT",EDGE,{"derivedFrom":sQuery(id+"F12.wireOp",EDGE,"E146.3.1.14")}),1.0]])]});
            var Q284;
            Q284=makeQuery(id+"F12.imprint","IMPRINT",FACE,{"disambiguationData":[TD([[makeQuery(id+"F12.imprint","IMPRINT",EDGE,{"derivedFrom":sQuery(id+"F12.wireOp",EDGE,"E146.2.0.2")}),1.0]])]});
            var Q285;
            Q285=makeQuery(id+"F12.imprint","IMPRINT",FACE,{"disambiguationData":[TD([[makeQuery(id+"F12.imprint","IMPRINT",EDGE,{"derivedFrom":sQuery(id+"F12.wireOp",EDGE,"E146.1.1.31")}),1.0]])]});
            var Q286;
            Q286=makeQuery(id+"F12.imprint","IMPRINT",FACE,{"disambiguationData":[TD([[makeQuery(id+"F12.imprint","IMPRINT",EDGE,{"derivedFrom":sQuery(id+"F12.wireOp",EDGE,"E146.2.0.52")}),-1.0]])]});
            var Q287;
            Q287=makeQuery(id+"F12.imprint","IMPRINT",FACE,{"disambiguationData":[TD([[makeQuery(id+"F12.imprint","IMPRINT",EDGE,{"derivedFrom":sQuery(id+"F12.wireOp",EDGE,"E146.3.1.0")}),1.0]])]});
            var Q288;
            Q288=makeQuery(id+"F12.imprint","IMPRINT",FACE,{"disambiguationData":[TD([[makeQuery(id+"F12.imprint","IMPRINT",EDGE,{"derivedFrom":sQuery(id+"F12.wireOp",EDGE,"E146.0.1.13")}),-1.0]])]});
            var Q289;
            Q289=makeQuery(id+"F12.imprint","IMPRINT",FACE,{"disambiguationData":[TD([[makeQuery(id+"F12.imprint","IMPRINT",EDGE,{"derivedFrom":sQuery(id+"F12.wireOp",EDGE,"E146.0.1.65")}),1.0]])]});
            var Q290;
            Q290=makeQuery(id+"F12.imprint","IMPRINT",FACE,{"disambiguationData":[TD([[makeQuery(id+"F12.imprint","IMPRINT",EDGE,{"derivedFrom":sQuery(id+"F12.wireOp",EDGE,"E146.1.1.52")}),-1.0]])]});
            var Q291;
            Q291=makeQuery(id+"F12.imprint","IMPRINT",FACE,{"disambiguationData":[TD([[makeQuery(id+"F12.imprint","IMPRINT",EDGE,{"derivedFrom":sQuery(id+"F12.wireOp",EDGE,"E146.1.1.14")}),1.0]])]});
            var Q292;
            Q292=makeQuery(id+"F12.imprint","IMPRINT",FACE,{"disambiguationData":[TD([[makeQuery(id+"F12.imprint","IMPRINT",EDGE,{"derivedFrom":sQuery(id+"F12.wireOp",EDGE,"E146.0.1.0")}),1.0]])]});
            var Q293;
            Q293=makeQuery(id+"F12.imprint","IMPRINT",FACE,{"disambiguationData":[TD([[makeQuery(id+"F12.imprint","IMPRINT",EDGE,{"derivedFrom":sQuery(id+"F12.wireOp",EDGE,"E146.3.0.52")}),-1.0]])]});
            var Q294;
            Q294=makeQuery(id+"F12.imprint","IMPRINT",FACE,{"disambiguationData":[TD([[makeQuery(id+"F12.imprint","IMPRINT",EDGE,{"derivedFrom":sQuery(id+"F12.wireOp",EDGE,"E146.4.1.15")}),1.0]])]});
            var Q295;
            Q295=makeQuery(id+"F12.imprint","IMPRINT",FACE,{"disambiguationData":[TD([[makeQuery(id+"F12.imprint","IMPRINT",EDGE,{"derivedFrom":sQuery(id+"F12.wireOp",EDGE,"E146.3.0.13")}),-1.0]])]});
            var Q296;
            Q296=makeQuery(id+"F12.imprint","IMPRINT",FACE,{"disambiguationData":[TD([[makeQuery(id+"F12.imprint","IMPRINT",EDGE,{"derivedFrom":sQuery(id+"F12.wireOp",EDGE,"E146.2.0.14")}),1.0]])]});
            var Q297;
            Q297=makeQuery(id+"F12.imprint","IMPRINT",FACE,{"disambiguationData":[TD([[makeQuery(id+"F12.imprint","IMPRINT",EDGE,{"derivedFrom":sQuery(id+"F12.wireOp",EDGE,"E146.1.1.40")}),-1.0]])]});
            var Q298;
            Q298=makeQuery(id+"F12.imprint","IMPRINT",FACE,{"disambiguationData":[TD([[makeQuery(id+"F12.imprint","IMPRINT",EDGE,{"derivedFrom":sQuery(id+"F12.wireOp",EDGE,"E146.0.1.40")}),-1.0]])]});
            var Q299;
            Q299=makeQuery(id+"F12.imprint","IMPRINT",FACE,{"disambiguationData":[TD([[makeQuery(id+"F12.imprint","IMPRINT",EDGE,{"derivedFrom":sQuery(id+"F12.wireOp",EDGE,"E146.1.1.0")}),1.0]])]});
            extrude(context, id + "F13", {"entities" : qUnion([Q0, Q1, Q2, Q3, Q4, Q5, Q6, Q7, Q8, Q9, Q10, Q11, Q12, Q13, Q14, Q15, Q16, Q17, Q18, Q19, Q20, Q21, Q22, Q23, Q24, Q25, Q26, Q27, Q28, Q29, Q30, Q31, Q32, Q33, Q34, Q35, Q36, Q37, Q38, Q39, Q40, Q41, Q42, Q43, Q44, Q45, Q46, Q47, Q48, Q49, Q50, Q51, Q52, Q53, Q54, Q55, Q56, Q57, Q58, Q59, Q60, Q61, Q62, Q63, Q64, Q65, Q66, Q67, Q68, Q69, Q70, Q71, Q72, Q73, Q74, Q75, Q76, Q77, Q78, Q79, Q80, Q81, Q82, Q83, Q84, Q85, Q86, Q87, Q88, Q89, Q90, Q91, Q92, Q93, Q94, Q95, Q96, Q97, Q98, Q99, Q100, Q101, Q102, Q103, Q104, Q105, Q106, Q107, Q108, Q109, Q110, Q111, Q112, Q113, Q114, Q115, Q116, Q117, Q118, Q119, Q120, Q121, Q122, Q123, Q124, Q125, Q126, Q127, Q128, Q129, Q130, Q131, Q132, Q133, Q134, Q135, Q136, Q137, Q138, Q139, Q140, Q141, Q142, Q143, Q144, Q145, Q146, Q147, Q148, Q149, Q150, Q151, Q152, Q153, Q154, Q155, Q156, Q157, Q158, Q159, Q160, Q161, Q162, Q163, Q164, Q165, Q166, Q167, Q168, Q169, Q170, Q171, Q172, Q173, Q174, Q175, Q176, Q177, Q178, Q179, Q180, Q181, Q182, Q183, Q184, Q185, Q186, Q187, Q188, Q189, Q190, Q191, Q192, Q193, Q194, Q195, Q196, Q197, Q198, Q199, Q200, Q201, Q202, Q203, Q204, Q205, Q206, Q207, Q208, Q209, Q210, Q211, Q212, Q213, Q214, Q215, Q216, Q217, Q218, Q219, Q220, Q221, Q222, Q223, Q224, Q225, Q226, Q227, Q228, Q229, Q230, Q231, Q232, Q233, Q234, Q235, Q236, Q237, Q238, Q239, Q240, Q241, Q242, Q243, Q244, Q245, Q246, Q247, Q248, Q249, Q250, Q251, Q252, Q253, Q254, Q255, Q256, Q257, Q258, Q259, Q260, Q261, Q262, Q263, Q264, Q265, Q266, Q267, Q268, Q269, Q270, Q271, Q272, Q273, Q274, Q275, Q276, Q277, Q278, Q279, Q280, Q281, Q282, Q283, Q284, Q285, Q286, Q287, Q288, Q289, Q290, Q291, Q292, Q293, Q294, Q295, Q296, Q297, Q298, Q299]), "operationType" : NewBodyOperationType.REMOVE, "endBound" : BoundingType.THROUGH_ALL, "oppositeDirection" : true, "depth" : 25.4 * mm});
        }
        {
            var Q0;
            {var subQ75=makeQuery(id+"F3.boolean.opBoolean","COPY",FACE,{"derivedFrom":makeQuery(id+"F3.opExtrude","SWEPT_FACE",FACE,{"disambiguationData":[OSD([sQuery(id+"F2.wireOp",EDGE,"E2")])]})});Q0=makeQuery(id+"F8.boolean.opBoolean","SPLIT",FACE,{"disambiguationData":[TD([subQ75])],"derivedFrom":makeQuery(id+"F6.boolean.opBoolean","SPLIT",FACE,{"disambiguationData":[TD([subQ75])],"derivedFrom":makeQuery(id+"F1.opExtrude","CAP_FACE",FACE,{"disambiguationData":[OSD([sQuery(id+"F0.wireOp",EDGE,"E0.bottom"),sQuery(id+"F0.wireOp",EDGE,"E0.top"),sQuery(id+"F0.wireOp",EDGE,"E0.left"),sQuery(id+"F0.wireOp",EDGE,"E0.right")])],"isStart":true})})});}
            var sketch = newSketch(context, id + "F14", { "sketchPlane" : qUnion([Q0])});
            skLineSegment(sketch, "E147.bottom", {"start": v(-561.12, -84.87) * mm, "end": v(-554.77, -84.87) * mm});
            skLineSegment(sketch, "E147.top", {"start": v(-561.12, -91.22) * mm, "end": v(-554.77, -91.22) * mm});
            skLineSegment(sketch, "E147.left", {"start": v(-561.12, -84.87) * mm, "end": v(-561.12, -91.22) * mm});
            skLineSegment(sketch, "E147.right", {"start": v(-554.77, -84.87) * mm, "end": v(-554.77, -91.22) * mm});
            skLineSegment(sketch, "E148.0.1.0", {"start": v(-561.12, -72.17) * mm, "end": v(-554.77, -72.17) * mm});
            skLineSegment(sketch, "E148.0.1.1", {"start": v(-554.77, -72.17) * mm, "end": v(-554.77, -78.52) * mm});
            skLineSegment(sketch, "E148.0.1.2", {"start": v(-561.12, -78.52) * mm, "end": v(-554.77, -78.52) * mm});
            skLineSegment(sketch, "E148.0.1.3", {"start": v(-561.12, -72.17) * mm, "end": v(-561.12, -78.52) * mm});
            skLineSegment(sketch, "E148.0.2.0", {"start": v(-561.12, -59.47) * mm, "end": v(-554.77, -59.47) * mm});
            skLineSegment(sketch, "E148.0.2.1", {"start": v(-554.77, -59.47) * mm, "end": v(-554.77, -65.82) * mm});
            skLineSegment(sketch, "E148.0.2.2", {"start": v(-561.12, -65.82) * mm, "end": v(-554.77, -65.82) * mm});
            skLineSegment(sketch, "E148.0.2.3", {"start": v(-561.12, -59.47) * mm, "end": v(-561.12, -65.82) * mm});
            skLineSegment(sketch, "E148.0.3.0", {"start": v(-561.12, -46.77) * mm, "end": v(-554.77, -46.77) * mm});
            skLineSegment(sketch, "E148.0.3.1", {"start": v(-554.77, -46.77) * mm, "end": v(-554.77, -53.12) * mm});
            skLineSegment(sketch, "E148.0.3.2", {"start": v(-561.12, -53.12) * mm, "end": v(-554.77, -53.12) * mm});
            skLineSegment(sketch, "E148.0.3.3", {"start": v(-561.12, -46.77) * mm, "end": v(-561.12, -53.12) * mm});
            skLineSegment(sketch, "E148.0.4.0", {"start": v(-561.12, -34.07) * mm, "end": v(-554.77, -34.07) * mm});
            skLineSegment(sketch, "E148.0.4.1", {"start": v(-554.77, -34.07) * mm, "end": v(-554.77, -40.42) * mm});
            skLineSegment(sketch, "E148.0.4.2", {"start": v(-561.12, -40.42) * mm, "end": v(-554.77, -40.42) * mm});
            skLineSegment(sketch, "E148.0.4.3", {"start": v(-561.12, -34.07) * mm, "end": v(-561.12, -40.42) * mm});
            skLineSegment(sketch, "E148.1.0.0", {"start": v(-548.42, -84.87) * mm, "end": v(-542.07, -84.87) * mm});
            skLineSegment(sketch, "E148.1.0.1", {"start": v(-542.07, -84.87) * mm, "end": v(-542.07, -91.22) * mm});
            skLineSegment(sketch, "E148.1.0.2", {"start": v(-548.42, -91.22) * mm, "end": v(-542.07, -91.22) * mm});
            skLineSegment(sketch, "E148.1.0.3", {"start": v(-548.42, -84.87) * mm, "end": v(-548.42, -91.22) * mm});
            skLineSegment(sketch, "E148.1.1.0", {"start": v(-548.42, -72.17) * mm, "end": v(-542.07, -72.17) * mm});
            skLineSegment(sketch, "E148.1.1.1", {"start": v(-542.07, -72.17) * mm, "end": v(-542.07, -78.52) * mm});
            skLineSegment(sketch, "E148.1.1.2", {"start": v(-548.42, -78.52) * mm, "end": v(-542.07, -78.52) * mm});
            skLineSegment(sketch, "E148.1.1.3", {"start": v(-548.42, -72.17) * mm, "end": v(-548.42, -78.52) * mm});
            skLineSegment(sketch, "E148.1.2.0", {"start": v(-548.42, -59.47) * mm, "end": v(-542.07, -59.47) * mm});
            skLineSegment(sketch, "E148.1.2.1", {"start": v(-542.07, -59.47) * mm, "end": v(-542.07, -65.82) * mm});
            skLineSegment(sketch, "E148.1.2.2", {"start": v(-548.42, -65.82) * mm, "end": v(-542.07, -65.82) * mm});
            skLineSegment(sketch, "E148.1.2.3", {"start": v(-548.42, -59.47) * mm, "end": v(-548.42, -65.82) * mm});
            skLineSegment(sketch, "E148.1.3.0", {"start": v(-548.42, -46.77) * mm, "end": v(-542.07, -46.77) * mm});
            skLineSegment(sketch, "E148.1.3.1", {"start": v(-542.07, -46.77) * mm, "end": v(-542.07, -53.12) * mm});
            skLineSegment(sketch, "E148.1.3.2", {"start": v(-548.42, -53.12) * mm, "end": v(-542.07, -53.12) * mm});
            skLineSegment(sketch, "E148.1.3.3", {"start": v(-548.42, -46.77) * mm, "end": v(-548.42, -53.12) * mm});
            skLineSegment(sketch, "E148.1.4.0", {"start": v(-548.42, -34.07) * mm, "end": v(-542.07, -34.07) * mm});
            skLineSegment(sketch, "E148.1.4.1", {"start": v(-542.07, -34.07) * mm, "end": v(-542.07, -40.42) * mm});
            skLineSegment(sketch, "E148.1.4.2", {"start": v(-548.42, -40.42) * mm, "end": v(-542.07, -40.42) * mm});
            skLineSegment(sketch, "E148.1.4.3", {"start": v(-548.42, -34.07) * mm, "end": v(-548.42, -40.42) * mm});
            skLineSegment(sketch, "E148.2.0.0", {"start": v(-535.72, -84.87) * mm, "end": v(-529.37, -84.87) * mm});
            skLineSegment(sketch, "E148.2.0.1", {"start": v(-529.37, -84.87) * mm, "end": v(-529.37, -91.22) * mm});
            skLineSegment(sketch, "E148.2.0.2", {"start": v(-535.72, -91.22) * mm, "end": v(-529.37, -91.22) * mm});
            skLineSegment(sketch, "E148.2.0.3", {"start": v(-535.72, -84.87) * mm, "end": v(-535.72, -91.22) * mm});
            skLineSegment(sketch, "E148.2.1.0", {"start": v(-535.72, -72.17) * mm, "end": v(-529.37, -72.17) * mm});
            skLineSegment(sketch, "E148.2.1.1", {"start": v(-529.37, -72.17) * mm, "end": v(-529.37, -78.52) * mm});
            skLineSegment(sketch, "E148.2.1.2", {"start": v(-535.72, -78.52) * mm, "end": v(-529.37, -78.52) * mm});
            skLineSegment(sketch, "E148.2.1.3", {"start": v(-535.72, -72.17) * mm, "end": v(-535.72, -78.52) * mm});
            skLineSegment(sketch, "E148.2.2.0", {"start": v(-535.72, -59.47) * mm, "end": v(-529.37, -59.47) * mm});
            skLineSegment(sketch, "E148.2.2.1", {"start": v(-529.37, -59.47) * mm, "end": v(-529.37, -65.82) * mm});
            skLineSegment(sketch, "E148.2.2.2", {"start": v(-535.72, -65.82) * mm, "end": v(-529.37, -65.82) * mm});
            skLineSegment(sketch, "E148.2.2.3", {"start": v(-535.72, -59.47) * mm, "end": v(-535.72, -65.82) * mm});
            skLineSegment(sketch, "E148.2.3.0", {"start": v(-535.72, -46.77) * mm, "end": v(-529.37, -46.77) * mm});
            skLineSegment(sketch, "E148.2.3.1", {"start": v(-529.37, -46.77) * mm, "end": v(-529.37, -53.12) * mm});
            skLineSegment(sketch, "E148.2.3.2", {"start": v(-535.72, -53.12) * mm, "end": v(-529.37, -53.12) * mm});
            skLineSegment(sketch, "E148.2.3.3", {"start": v(-535.72, -46.77) * mm, "end": v(-535.72, -53.12) * mm});
            skLineSegment(sketch, "E148.2.4.0", {"start": v(-535.72, -34.07) * mm, "end": v(-529.37, -34.07) * mm});
            skLineSegment(sketch, "E148.2.4.1", {"start": v(-529.37, -34.07) * mm, "end": v(-529.37, -40.42) * mm});
            skLineSegment(sketch, "E148.2.4.2", {"start": v(-535.72, -40.42) * mm, "end": v(-529.37, -40.42) * mm});
            skLineSegment(sketch, "E148.2.4.3", {"start": v(-535.72, -34.07) * mm, "end": v(-535.72, -40.42) * mm});
            skLineSegment(sketch, "E148.3.0.0", {"start": v(-523.02, -84.87) * mm, "end": v(-516.67, -84.87) * mm});
            skLineSegment(sketch, "E148.3.0.1", {"start": v(-516.67, -84.87) * mm, "end": v(-516.67, -91.22) * mm});
            skLineSegment(sketch, "E148.3.0.2", {"start": v(-523.02, -91.22) * mm, "end": v(-516.67, -91.22) * mm});
            skLineSegment(sketch, "E148.3.0.3", {"start": v(-523.02, -84.87) * mm, "end": v(-523.02, -91.22) * mm});
            skLineSegment(sketch, "E148.3.1.0", {"start": v(-523.02, -72.17) * mm, "end": v(-516.67, -72.17) * mm});
            skLineSegment(sketch, "E148.3.1.1", {"start": v(-516.67, -72.17) * mm, "end": v(-516.67, -78.52) * mm});
            skLineSegment(sketch, "E148.3.1.2", {"start": v(-523.02, -78.52) * mm, "end": v(-516.67, -78.52) * mm});
            skLineSegment(sketch, "E148.3.1.3", {"start": v(-523.02, -72.17) * mm, "end": v(-523.02, -78.52) * mm});
            skLineSegment(sketch, "E148.3.2.0", {"start": v(-523.02, -59.47) * mm, "end": v(-516.67, -59.47) * mm});
            skLineSegment(sketch, "E148.3.2.1", {"start": v(-516.67, -59.47) * mm, "end": v(-516.67, -65.82) * mm});
            skLineSegment(sketch, "E148.3.2.2", {"start": v(-523.02, -65.82) * mm, "end": v(-516.67, -65.82) * mm});
            skLineSegment(sketch, "E148.3.2.3", {"start": v(-523.02, -59.47) * mm, "end": v(-523.02, -65.82) * mm});
            skLineSegment(sketch, "E148.3.3.0", {"start": v(-523.02, -46.77) * mm, "end": v(-516.67, -46.77) * mm});
            skLineSegment(sketch, "E148.3.3.1", {"start": v(-516.67, -46.77) * mm, "end": v(-516.67, -53.12) * mm});
            skLineSegment(sketch, "E148.3.3.2", {"start": v(-523.02, -53.12) * mm, "end": v(-516.67, -53.12) * mm});
            skLineSegment(sketch, "E148.3.3.3", {"start": v(-523.02, -46.77) * mm, "end": v(-523.02, -53.12) * mm});
            skLineSegment(sketch, "E148.3.4.0", {"start": v(-523.02, -34.07) * mm, "end": v(-516.67, -34.07) * mm});
            skLineSegment(sketch, "E148.3.4.1", {"start": v(-516.67, -34.07) * mm, "end": v(-516.67, -40.42) * mm});
            skLineSegment(sketch, "E148.3.4.2", {"start": v(-523.02, -40.42) * mm, "end": v(-516.67, -40.42) * mm});
            skLineSegment(sketch, "E148.3.4.3", {"start": v(-523.02, -34.07) * mm, "end": v(-523.02, -40.42) * mm});
            skLineSegment(sketch, "E148.4.0.0", {"start": v(-510.32, -84.87) * mm, "end": v(-503.97, -84.87) * mm});
            skLineSegment(sketch, "E148.4.0.1", {"start": v(-503.97, -84.87) * mm, "end": v(-503.97, -91.22) * mm});
            skLineSegment(sketch, "E148.4.0.2", {"start": v(-510.32, -91.22) * mm, "end": v(-503.97, -91.22) * mm});
            skLineSegment(sketch, "E148.4.0.3", {"start": v(-510.32, -84.87) * mm, "end": v(-510.32, -91.22) * mm});
            skLineSegment(sketch, "E148.4.1.0", {"start": v(-510.32, -72.17) * mm, "end": v(-503.97, -72.17) * mm});
            skLineSegment(sketch, "E148.4.1.1", {"start": v(-503.97, -72.17) * mm, "end": v(-503.97, -78.52) * mm});
            skLineSegment(sketch, "E148.4.1.2", {"start": v(-510.32, -78.52) * mm, "end": v(-503.97, -78.52) * mm});
            skLineSegment(sketch, "E148.4.1.3", {"start": v(-510.32, -72.17) * mm, "end": v(-510.32, -78.52) * mm});
            skLineSegment(sketch, "E148.4.2.0", {"start": v(-510.32, -59.47) * mm, "end": v(-503.97, -59.47) * mm});
            skLineSegment(sketch, "E148.4.2.1", {"start": v(-503.97, -59.47) * mm, "end": v(-503.97, -65.82) * mm});
            skLineSegment(sketch, "E148.4.2.2", {"start": v(-510.32, -65.82) * mm, "end": v(-503.97, -65.82) * mm});
            skLineSegment(sketch, "E148.4.2.3", {"start": v(-510.32, -59.47) * mm, "end": v(-510.32, -65.82) * mm});
            skLineSegment(sketch, "E148.4.3.0", {"start": v(-510.32, -46.77) * mm, "end": v(-503.97, -46.77) * mm});
            skLineSegment(sketch, "E148.4.3.1", {"start": v(-503.97, -46.77) * mm, "end": v(-503.97, -53.12) * mm});
            skLineSegment(sketch, "E148.4.3.2", {"start": v(-510.32, -53.12) * mm, "end": v(-503.97, -53.12) * mm});
            skLineSegment(sketch, "E148.4.3.3", {"start": v(-510.32, -46.77) * mm, "end": v(-510.32, -53.12) * mm});
            skLineSegment(sketch, "E148.4.4.0", {"start": v(-510.32, -34.07) * mm, "end": v(-503.97, -34.07) * mm});
            skLineSegment(sketch, "E148.4.4.1", {"start": v(-503.97, -34.07) * mm, "end": v(-503.97, -40.42) * mm});
            skLineSegment(sketch, "E148.4.4.2", {"start": v(-510.32, -40.42) * mm, "end": v(-503.97, -40.42) * mm});
            skLineSegment(sketch, "E148.4.4.3", {"start": v(-510.32, -34.07) * mm, "end": v(-510.32, -40.42) * mm});
            skLineSegment(sketch, "E148.direction1", {"start": v(-561.12, -91.22) * mm, "end": v(-548.42, -91.22) * mm, "construction": true});
            skLineSegment(sketch, "E148.direction2", {"start": v(-561.12, -91.22) * mm, "end": v(-561.12, -78.52) * mm, "construction": true});
            skLineSegment(sketch, "E149.0.1.0", {"start": v(-554.77, -300.77) * mm, "end": v(-554.77, -307.12) * mm, "construction": true});
            skLineSegment(sketch, "E149.0.1.1", {"start": v(-561.12, -300.77) * mm, "end": v(-561.12, -307.12) * mm, "construction": true});
            skLineSegment(sketch, "E149.0.1.2", {"start": v(-561.12, -307.12) * mm, "end": v(-554.77, -307.12) * mm, "construction": true});
            skLineSegment(sketch, "E149.0.1.3", {"start": v(-561.12, -300.77) * mm, "end": v(-554.77, -300.77) * mm, "construction": true});
            skLineSegment(sketch, "E149.0.1.4", {"start": v(-516.67, -338.87) * mm, "end": v(-516.67, -345.22) * mm, "construction": true});
            skLineSegment(sketch, "E149.0.1.5", {"start": v(-516.67, -288.07) * mm, "end": v(-516.67, -294.42) * mm, "construction": true});
            skLineSegment(sketch, "E149.0.1.6", {"start": v(-503.97, -300.77) * mm, "end": v(-503.97, -307.12) * mm, "construction": true});
            skLineSegment(sketch, "E149.0.1.7", {"start": v(-529.37, -326.17) * mm, "end": v(-529.37, -332.52) * mm, "construction": true});
            skLineSegment(sketch, "E149.0.1.8", {"start": v(-535.72, -326.17) * mm, "end": v(-535.72, -332.52) * mm, "construction": true});
            skLineSegment(sketch, "E149.0.1.9", {"start": v(-523.02, -338.87) * mm, "end": v(-523.02, -345.22) * mm, "construction": true});
            skLineSegment(sketch, "E149.0.1.10", {"start": v(-523.02, -288.07) * mm, "end": v(-523.02, -294.42) * mm, "construction": true});
            skLineSegment(sketch, "E149.0.1.11", {"start": v(-510.32, -300.77) * mm, "end": v(-510.32, -307.12) * mm, "construction": true});
            skLineSegment(sketch, "E149.0.1.12", {"start": v(-535.72, -332.52) * mm, "end": v(-529.37, -332.52) * mm, "construction": true});
            skLineSegment(sketch, "E149.0.1.13", {"start": v(-523.02, -345.22) * mm, "end": v(-516.67, -345.22) * mm, "construction": true});
            skLineSegment(sketch, "E149.0.1.14", {"start": v(-523.02, -294.42) * mm, "end": v(-516.67, -294.42) * mm, "construction": true});
            skLineSegment(sketch, "E149.0.1.15", {"start": v(-510.32, -307.12) * mm, "end": v(-503.97, -307.12) * mm, "construction": true});
            skLineSegment(sketch, "E149.0.1.16", {"start": v(-548.42, -338.87) * mm, "end": v(-548.42, -345.22) * mm, "construction": true});
            skLineSegment(sketch, "E149.0.1.17", {"start": v(-548.42, -288.07) * mm, "end": v(-548.42, -294.42) * mm, "construction": true});
            skLineSegment(sketch, "E149.0.1.18", {"start": v(-535.72, -300.77) * mm, "end": v(-535.72, -307.12) * mm, "construction": true});
            skLineSegment(sketch, "E149.0.1.19", {"start": v(-523.02, -313.47) * mm, "end": v(-523.02, -319.82) * mm, "construction": true});
            skLineSegment(sketch, "E149.0.1.20", {"start": v(-510.32, -326.17) * mm, "end": v(-510.32, -332.52) * mm, "construction": true});
            skLineSegment(sketch, "E149.0.1.21", {"start": v(-529.37, -338.87) * mm, "end": v(-529.37, -345.22) * mm, "construction": true});
            skLineSegment(sketch, "E149.0.1.22", {"start": v(-529.37, -288.07) * mm, "end": v(-529.37, -294.42) * mm, "construction": true});
            skLineSegment(sketch, "E149.0.1.23", {"start": v(-516.67, -300.77) * mm, "end": v(-516.67, -307.12) * mm, "construction": true});
            skLineSegment(sketch, "E149.0.1.24", {"start": v(-503.97, -313.47) * mm, "end": v(-503.97, -319.82) * mm, "construction": true});
            skLineSegment(sketch, "E149.0.1.25", {"start": v(-535.72, -338.87) * mm, "end": v(-529.37, -338.87) * mm, "construction": true});
            skLineSegment(sketch, "E149.0.1.26", {"start": v(-535.72, -288.07) * mm, "end": v(-529.37, -288.07) * mm, "construction": true});
            skLineSegment(sketch, "E149.0.1.27", {"start": v(-523.02, -300.77) * mm, "end": v(-516.67, -300.77) * mm, "construction": true});
            skLineSegment(sketch, "E149.0.1.28", {"start": v(-510.32, -313.47) * mm, "end": v(-503.97, -313.47) * mm, "construction": true});
            skLineSegment(sketch, "E149.0.1.29", {"start": v(-535.72, -338.87) * mm, "end": v(-535.72, -345.22) * mm, "construction": true});
            skLineSegment(sketch, "E149.0.1.30", {"start": v(-535.72, -288.07) * mm, "end": v(-535.72, -294.42) * mm, "construction": true});
            skLineSegment(sketch, "E149.0.1.31", {"start": v(-523.02, -300.77) * mm, "end": v(-523.02, -307.12) * mm, "construction": true});
            skLineSegment(sketch, "E149.0.1.32", {"start": v(-510.32, -313.47) * mm, "end": v(-510.32, -319.82) * mm, "construction": true});
            skLineSegment(sketch, "E149.0.1.33", {"start": v(-535.72, -345.22) * mm, "end": v(-529.37, -345.22) * mm, "construction": true});
            skLineSegment(sketch, "E149.0.1.34", {"start": v(-535.72, -294.42) * mm, "end": v(-529.37, -294.42) * mm, "construction": true});
            skLineSegment(sketch, "E149.0.1.35", {"start": v(-523.02, -307.12) * mm, "end": v(-516.67, -307.12) * mm, "construction": true});
            skLineSegment(sketch, "E149.0.1.36", {"start": v(-510.32, -319.82) * mm, "end": v(-503.97, -319.82) * mm, "construction": true});
            skLineSegment(sketch, "E149.0.1.37", {"start": v(-535.72, -326.17) * mm, "end": v(-529.37, -326.17) * mm, "construction": true});
            skLineSegment(sketch, "E149.0.1.38", {"start": v(-523.02, -338.87) * mm, "end": v(-516.67, -338.87) * mm, "construction": true});
            skLineSegment(sketch, "E149.0.1.39", {"start": v(-523.02, -288.07) * mm, "end": v(-516.67, -288.07) * mm, "construction": true});
            skLineSegment(sketch, "E149.0.1.40", {"start": v(-510.32, -300.77) * mm, "end": v(-503.97, -300.77) * mm, "construction": true});
            skLineSegment(sketch, "E149.0.1.41", {"start": v(-523.02, -326.17) * mm, "end": v(-516.67, -326.17) * mm, "construction": true});
            skLineSegment(sketch, "E149.0.1.42", {"start": v(-510.32, -338.87) * mm, "end": v(-503.97, -338.87) * mm, "construction": true});
            skLineSegment(sketch, "E149.0.1.43", {"start": v(-510.32, -288.07) * mm, "end": v(-503.97, -288.07) * mm, "construction": true});
            skLineSegment(sketch, "E149.0.1.44", {"start": v(-561.12, -288.07) * mm, "end": v(-554.77, -288.07) * mm, "construction": true});
            skLineSegment(sketch, "E149.0.1.45", {"start": v(-548.42, -300.77) * mm, "end": v(-542.07, -300.77) * mm, "construction": true});
            skLineSegment(sketch, "E149.0.1.46", {"start": v(-535.72, -313.47) * mm, "end": v(-529.37, -313.47) * mm, "construction": true});
            skLineSegment(sketch, "E149.0.1.47", {"start": v(-523.02, -332.52) * mm, "end": v(-516.67, -332.52) * mm, "construction": true});
            skLineSegment(sketch, "E149.0.1.48", {"start": v(-510.32, -345.22) * mm, "end": v(-503.97, -345.22) * mm, "construction": true});
            skLineSegment(sketch, "E149.0.1.49", {"start": v(-510.32, -294.42) * mm, "end": v(-503.97, -294.42) * mm, "construction": true});
            skLineSegment(sketch, "E149.0.1.50", {"start": v(-561.12, -294.42) * mm, "end": v(-554.77, -294.42) * mm, "construction": true});
            skLineSegment(sketch, "E149.0.1.51", {"start": v(-548.42, -307.12) * mm, "end": v(-542.07, -307.12) * mm, "construction": true});
            skLineSegment(sketch, "E149.0.1.52", {"start": v(-535.72, -319.82) * mm, "end": v(-529.37, -319.82) * mm, "construction": true});
            skLineSegment(sketch, "E149.0.1.53", {"start": v(-554.77, -288.07) * mm, "end": v(-554.77, -294.42) * mm, "construction": true});
            skLineSegment(sketch, "E149.0.1.54", {"start": v(-542.07, -300.77) * mm, "end": v(-542.07, -307.12) * mm, "construction": true});
            skLineSegment(sketch, "E149.0.1.55", {"start": v(-529.37, -313.47) * mm, "end": v(-529.37, -319.82) * mm, "construction": true});
            skLineSegment(sketch, "E149.0.1.56", {"start": v(-516.67, -326.17) * mm, "end": v(-516.67, -332.52) * mm, "construction": true});
            skLineSegment(sketch, "E149.0.1.57", {"start": v(-503.97, -338.87) * mm, "end": v(-503.97, -345.22) * mm, "construction": true});
            skLineSegment(sketch, "E149.0.1.58", {"start": v(-503.97, -288.07) * mm, "end": v(-503.97, -294.42) * mm, "construction": true});
            skLineSegment(sketch, "E149.0.1.59", {"start": v(-523.02, -313.47) * mm, "end": v(-516.67, -313.47) * mm, "construction": true});
            skLineSegment(sketch, "E149.0.1.60", {"start": v(-510.32, -326.17) * mm, "end": v(-503.97, -326.17) * mm, "construction": true});
            skLineSegment(sketch, "E149.0.1.61", {"start": v(-548.42, -338.87) * mm, "end": v(-542.07, -338.87) * mm, "construction": true});
            skLineSegment(sketch, "E149.0.1.62", {"start": v(-548.42, -288.07) * mm, "end": v(-542.07, -288.07) * mm, "construction": true});
            skLineSegment(sketch, "E149.0.1.63", {"start": v(-535.72, -300.77) * mm, "end": v(-529.37, -300.77) * mm, "construction": true});
            skLineSegment(sketch, "E149.0.1.64", {"start": v(-561.12, -288.07) * mm, "end": v(-561.12, -294.42) * mm, "construction": true});
            skLineSegment(sketch, "E149.0.1.65", {"start": v(-548.42, -300.77) * mm, "end": v(-548.42, -307.12) * mm, "construction": true});
            skLineSegment(sketch, "E149.0.1.66", {"start": v(-535.72, -313.47) * mm, "end": v(-535.72, -319.82) * mm, "construction": true});
            skLineSegment(sketch, "E149.0.1.67", {"start": v(-523.02, -326.17) * mm, "end": v(-523.02, -332.52) * mm, "construction": true});
            skLineSegment(sketch, "E149.0.1.68", {"start": v(-510.32, -338.87) * mm, "end": v(-510.32, -345.22) * mm, "construction": true});
            skLineSegment(sketch, "E149.0.1.69", {"start": v(-510.32, -288.07) * mm, "end": v(-510.32, -294.42) * mm, "construction": true});
            skLineSegment(sketch, "E149.0.1.70", {"start": v(-548.42, -345.22) * mm, "end": v(-542.07, -345.22) * mm, "construction": true});
            skLineSegment(sketch, "E149.0.1.71", {"start": v(-548.42, -294.42) * mm, "end": v(-542.07, -294.42) * mm, "construction": true});
            skLineSegment(sketch, "E149.0.1.72", {"start": v(-535.72, -307.12) * mm, "end": v(-529.37, -307.12) * mm, "construction": true});
            skLineSegment(sketch, "E149.0.1.73", {"start": v(-523.02, -319.82) * mm, "end": v(-516.67, -319.82) * mm, "construction": true});
            skLineSegment(sketch, "E149.0.1.74", {"start": v(-510.32, -332.52) * mm, "end": v(-503.97, -332.52) * mm, "construction": true});
            skLineSegment(sketch, "E149.0.1.75", {"start": v(-542.07, -338.87) * mm, "end": v(-542.07, -345.22) * mm, "construction": true});
            skLineSegment(sketch, "E149.0.1.76", {"start": v(-542.07, -288.07) * mm, "end": v(-542.07, -294.42) * mm, "construction": true});
            skLineSegment(sketch, "E149.0.1.77", {"start": v(-529.37, -300.77) * mm, "end": v(-529.37, -307.12) * mm, "construction": true});
            skLineSegment(sketch, "E149.0.1.78", {"start": v(-516.67, -313.47) * mm, "end": v(-516.67, -319.82) * mm, "construction": true});
            skLineSegment(sketch, "E149.0.1.79", {"start": v(-503.97, -326.17) * mm, "end": v(-503.97, -332.52) * mm, "construction": true});
            skLineSegment(sketch, "E149.0.1.80", {"start": v(-561.12, -326.17) * mm, "end": v(-554.77, -326.17) * mm, "construction": true});
            skLineSegment(sketch, "E149.0.1.81", {"start": v(-554.77, -338.87) * mm, "end": v(-554.77, -345.22) * mm, "construction": true});
            skLineSegment(sketch, "E149.0.1.82", {"start": v(-561.12, -332.52) * mm, "end": v(-554.77, -332.52) * mm, "construction": true});
            skLineSegment(sketch, "E149.0.1.83", {"start": v(-554.77, -326.17) * mm, "end": v(-554.77, -332.52) * mm, "construction": true});
            skLineSegment(sketch, "E149.0.1.84", {"start": v(-561.12, -338.87) * mm, "end": v(-554.77, -338.87) * mm, "construction": true});
            skLineSegment(sketch, "E149.0.1.85", {"start": v(-561.12, -313.47) * mm, "end": v(-554.77, -313.47) * mm, "construction": true});
            skLineSegment(sketch, "E149.0.1.86", {"start": v(-561.12, -326.17) * mm, "end": v(-561.12, -332.52) * mm, "construction": true});
            skLineSegment(sketch, "E149.0.1.87", {"start": v(-561.12, -319.82) * mm, "end": v(-554.77, -319.82) * mm, "construction": true});
            skLineSegment(sketch, "E149.0.1.88", {"start": v(-554.77, -313.47) * mm, "end": v(-554.77, -319.82) * mm, "construction": true});
            skLineSegment(sketch, "E149.0.1.89", {"start": v(-561.12, -313.47) * mm, "end": v(-561.12, -319.82) * mm, "construction": true});
            skLineSegment(sketch, "E149.0.1.90", {"start": v(-542.07, -313.47) * mm, "end": v(-542.07, -319.82) * mm, "construction": true});
            skLineSegment(sketch, "E149.0.1.91", {"start": v(-548.42, -313.47) * mm, "end": v(-548.42, -319.82) * mm, "construction": true});
            skLineSegment(sketch, "E149.0.1.92", {"start": v(-548.42, -319.82) * mm, "end": v(-542.07, -319.82) * mm, "construction": true});
            skLineSegment(sketch, "E149.0.1.93", {"start": v(-542.07, -326.17) * mm, "end": v(-542.07, -332.52) * mm, "construction": true});
            skLineSegment(sketch, "E149.0.1.94", {"start": v(-548.42, -326.17) * mm, "end": v(-542.07, -326.17) * mm, "construction": true});
            skLineSegment(sketch, "E149.0.1.95", {"start": v(-548.42, -326.17) * mm, "end": v(-548.42, -332.52) * mm, "construction": true});
            skLineSegment(sketch, "E149.0.1.96", {"start": v(-548.42, -332.52) * mm, "end": v(-542.07, -332.52) * mm, "construction": true});
            skLineSegment(sketch, "E149.0.1.97", {"start": v(-548.42, -313.47) * mm, "end": v(-542.07, -313.47) * mm, "construction": true});
            skLineSegment(sketch, "E149.0.1.98", {"start": v(-561.12, -345.22) * mm, "end": v(-548.42, -345.22) * mm, "construction": true});
            skLineSegment(sketch, "E149.0.1.99", {"start": v(-561.12, -345.22) * mm, "end": v(-561.12, -332.52) * mm, "construction": true});
            skLineSegment(sketch, "E149.0.1.100", {"start": v(-561.12, -338.87) * mm, "end": v(-561.12, -345.22) * mm, "construction": true});
            skLineSegment(sketch, "E149.0.1.101", {"start": v(-561.12, -345.22) * mm, "end": v(-554.77, -345.22) * mm, "construction": true});
            skLineSegment(sketch, "E149.1.0.0", {"start": v(-341.4, -46.77) * mm, "end": v(-341.4, -53.12) * mm});
            skLineSegment(sketch, "E149.1.0.1", {"start": v(-347.76, -46.77) * mm, "end": v(-347.76, -53.12) * mm});
            skLineSegment(sketch, "E149.1.0.2", {"start": v(-347.76, -53.12) * mm, "end": v(-341.4, -53.12) * mm});
            skLineSegment(sketch, "E149.1.0.3", {"start": v(-347.76, -46.77) * mm, "end": v(-341.4, -46.77) * mm});
            skLineSegment(sketch, "E149.1.0.4", {"start": v(-303.3, -84.87) * mm, "end": v(-303.3, -91.22) * mm});
            skLineSegment(sketch, "E149.1.0.5", {"start": v(-303.3, -34.07) * mm, "end": v(-303.3, -40.42) * mm});
            skLineSegment(sketch, "E149.1.0.6", {"start": v(-290.6, -46.77) * mm, "end": v(-290.6, -53.12) * mm});
            skLineSegment(sketch, "E149.1.0.7", {"start": v(-316, -72.17) * mm, "end": v(-316, -78.52) * mm});
            skLineSegment(sketch, "E149.1.0.8", {"start": v(-322.36, -72.17) * mm, "end": v(-322.36, -78.52) * mm});
            skLineSegment(sketch, "E149.1.0.9", {"start": v(-309.66, -84.87) * mm, "end": v(-309.66, -91.22) * mm});
            skLineSegment(sketch, "E149.1.0.10", {"start": v(-309.66, -34.07) * mm, "end": v(-309.66, -40.42) * mm});
            skLineSegment(sketch, "E149.1.0.11", {"start": v(-296.96, -46.77) * mm, "end": v(-296.96, -53.12) * mm});
            skLineSegment(sketch, "E149.1.0.12", {"start": v(-322.36, -78.52) * mm, "end": v(-316, -78.52) * mm});
            skLineSegment(sketch, "E149.1.0.13", {"start": v(-309.66, -91.22) * mm, "end": v(-303.3, -91.22) * mm});
            skLineSegment(sketch, "E149.1.0.14", {"start": v(-309.66, -40.42) * mm, "end": v(-303.3, -40.42) * mm});
            skLineSegment(sketch, "E149.1.0.15", {"start": v(-296.96, -53.12) * mm, "end": v(-290.6, -53.12) * mm});
            skLineSegment(sketch, "E149.1.0.16", {"start": v(-335.06, -84.87) * mm, "end": v(-335.06, -91.22) * mm});
            skLineSegment(sketch, "E149.1.0.17", {"start": v(-335.06, -34.07) * mm, "end": v(-335.06, -40.42) * mm});
            skLineSegment(sketch, "E149.1.0.18", {"start": v(-322.36, -46.77) * mm, "end": v(-322.36, -53.12) * mm});
            skLineSegment(sketch, "E149.1.0.19", {"start": v(-309.66, -59.47) * mm, "end": v(-309.66, -65.82) * mm});
            skLineSegment(sketch, "E149.1.0.20", {"start": v(-296.96, -72.17) * mm, "end": v(-296.96, -78.52) * mm});
            skLineSegment(sketch, "E149.1.0.21", {"start": v(-316, -84.87) * mm, "end": v(-316, -91.22) * mm});
            skLineSegment(sketch, "E149.1.0.22", {"start": v(-316, -34.07) * mm, "end": v(-316, -40.42) * mm});
            skLineSegment(sketch, "E149.1.0.23", {"start": v(-303.3, -46.77) * mm, "end": v(-303.3, -53.12) * mm});
            skLineSegment(sketch, "E149.1.0.24", {"start": v(-290.6, -59.47) * mm, "end": v(-290.6, -65.82) * mm});
            skLineSegment(sketch, "E149.1.0.25", {"start": v(-322.36, -84.87) * mm, "end": v(-316, -84.87) * mm});
            skLineSegment(sketch, "E149.1.0.26", {"start": v(-322.36, -34.07) * mm, "end": v(-316, -34.07) * mm});
            skLineSegment(sketch, "E149.1.0.27", {"start": v(-309.66, -46.77) * mm, "end": v(-303.3, -46.77) * mm});
            skLineSegment(sketch, "E149.1.0.28", {"start": v(-296.96, -59.47) * mm, "end": v(-290.6, -59.47) * mm});
            skLineSegment(sketch, "E149.1.0.29", {"start": v(-322.36, -84.87) * mm, "end": v(-322.36, -91.22) * mm});
            skLineSegment(sketch, "E149.1.0.30", {"start": v(-322.36, -34.07) * mm, "end": v(-322.36, -40.42) * mm});
            skLineSegment(sketch, "E149.1.0.31", {"start": v(-309.66, -46.77) * mm, "end": v(-309.66, -53.12) * mm});
            skLineSegment(sketch, "E149.1.0.32", {"start": v(-296.96, -59.47) * mm, "end": v(-296.96, -65.82) * mm});
            skLineSegment(sketch, "E149.1.0.33", {"start": v(-322.36, -91.22) * mm, "end": v(-316, -91.22) * mm});
            skLineSegment(sketch, "E149.1.0.34", {"start": v(-322.36, -40.42) * mm, "end": v(-316, -40.42) * mm});
            skLineSegment(sketch, "E149.1.0.35", {"start": v(-309.66, -53.12) * mm, "end": v(-303.3, -53.12) * mm});
            skLineSegment(sketch, "E149.1.0.36", {"start": v(-296.96, -65.82) * mm, "end": v(-290.6, -65.82) * mm});
            skLineSegment(sketch, "E149.1.0.37", {"start": v(-322.36, -72.17) * mm, "end": v(-316, -72.17) * mm});
            skLineSegment(sketch, "E149.1.0.38", {"start": v(-309.66, -84.87) * mm, "end": v(-303.3, -84.87) * mm});
            skLineSegment(sketch, "E149.1.0.39", {"start": v(-309.66, -34.07) * mm, "end": v(-303.3, -34.07) * mm});
            skLineSegment(sketch, "E149.1.0.40", {"start": v(-296.96, -46.77) * mm, "end": v(-290.6, -46.77) * mm});
            skLineSegment(sketch, "E149.1.0.41", {"start": v(-309.66, -72.17) * mm, "end": v(-303.3, -72.17) * mm});
            skLineSegment(sketch, "E149.1.0.42", {"start": v(-296.96, -84.87) * mm, "end": v(-290.6, -84.87) * mm});
            skLineSegment(sketch, "E149.1.0.43", {"start": v(-296.96, -34.07) * mm, "end": v(-290.6, -34.07) * mm});
            skLineSegment(sketch, "E149.1.0.44", {"start": v(-347.76, -34.07) * mm, "end": v(-341.4, -34.07) * mm});
            skLineSegment(sketch, "E149.1.0.45", {"start": v(-335.06, -46.77) * mm, "end": v(-328.7, -46.77) * mm});
            skLineSegment(sketch, "E149.1.0.46", {"start": v(-322.36, -59.47) * mm, "end": v(-316, -59.47) * mm});
            skLineSegment(sketch, "E149.1.0.47", {"start": v(-309.66, -78.52) * mm, "end": v(-303.3, -78.52) * mm});
            skLineSegment(sketch, "E149.1.0.48", {"start": v(-296.96, -91.22) * mm, "end": v(-290.6, -91.22) * mm});
            skLineSegment(sketch, "E149.1.0.49", {"start": v(-296.96, -40.42) * mm, "end": v(-290.6, -40.42) * mm});
            skLineSegment(sketch, "E149.1.0.50", {"start": v(-347.76, -40.42) * mm, "end": v(-341.4, -40.42) * mm});
            skLineSegment(sketch, "E149.1.0.51", {"start": v(-335.06, -53.12) * mm, "end": v(-328.7, -53.12) * mm});
            skLineSegment(sketch, "E149.1.0.52", {"start": v(-322.36, -65.82) * mm, "end": v(-316, -65.82) * mm});
            skLineSegment(sketch, "E149.1.0.53", {"start": v(-341.4, -34.07) * mm, "end": v(-341.4, -40.42) * mm});
            skLineSegment(sketch, "E149.1.0.54", {"start": v(-328.7, -46.77) * mm, "end": v(-328.7, -53.12) * mm});
            skLineSegment(sketch, "E149.1.0.55", {"start": v(-316, -59.47) * mm, "end": v(-316, -65.82) * mm});
            skLineSegment(sketch, "E149.1.0.56", {"start": v(-303.3, -72.17) * mm, "end": v(-303.3, -78.52) * mm});
            skLineSegment(sketch, "E149.1.0.57", {"start": v(-290.6, -84.87) * mm, "end": v(-290.6, -91.22) * mm});
            skLineSegment(sketch, "E149.1.0.58", {"start": v(-290.6, -34.07) * mm, "end": v(-290.6, -40.42) * mm});
            skLineSegment(sketch, "E149.1.0.59", {"start": v(-309.66, -59.47) * mm, "end": v(-303.3, -59.47) * mm});
            skLineSegment(sketch, "E149.1.0.60", {"start": v(-296.96, -72.17) * mm, "end": v(-290.6, -72.17) * mm});
            skLineSegment(sketch, "E149.1.0.61", {"start": v(-335.06, -84.87) * mm, "end": v(-328.7, -84.87) * mm});
            skLineSegment(sketch, "E149.1.0.62", {"start": v(-335.06, -34.07) * mm, "end": v(-328.7, -34.07) * mm});
            skLineSegment(sketch, "E149.1.0.63", {"start": v(-322.36, -46.77) * mm, "end": v(-316, -46.77) * mm});
            skLineSegment(sketch, "E149.1.0.64", {"start": v(-347.76, -34.07) * mm, "end": v(-347.76, -40.42) * mm});
            skLineSegment(sketch, "E149.1.0.65", {"start": v(-335.06, -46.77) * mm, "end": v(-335.06, -53.12) * mm});
            skLineSegment(sketch, "E149.1.0.66", {"start": v(-322.36, -59.47) * mm, "end": v(-322.36, -65.82) * mm});
            skLineSegment(sketch, "E149.1.0.67", {"start": v(-309.66, -72.17) * mm, "end": v(-309.66, -78.52) * mm});
            skLineSegment(sketch, "E149.1.0.68", {"start": v(-296.96, -84.87) * mm, "end": v(-296.96, -91.22) * mm});
            skLineSegment(sketch, "E149.1.0.69", {"start": v(-296.96, -34.07) * mm, "end": v(-296.96, -40.42) * mm});
            skLineSegment(sketch, "E149.1.0.70", {"start": v(-335.06, -91.22) * mm, "end": v(-328.7, -91.22) * mm});
            skLineSegment(sketch, "E149.1.0.71", {"start": v(-335.06, -40.42) * mm, "end": v(-328.7, -40.42) * mm});
            skLineSegment(sketch, "E149.1.0.72", {"start": v(-322.36, -53.12) * mm, "end": v(-316, -53.12) * mm});
            skLineSegment(sketch, "E149.1.0.73", {"start": v(-309.66, -65.82) * mm, "end": v(-303.3, -65.82) * mm});
            skLineSegment(sketch, "E149.1.0.74", {"start": v(-296.96, -78.52) * mm, "end": v(-290.6, -78.52) * mm});
            skLineSegment(sketch, "E149.1.0.75", {"start": v(-328.7, -84.87) * mm, "end": v(-328.7, -91.22) * mm});
            skLineSegment(sketch, "E149.1.0.76", {"start": v(-328.7, -34.07) * mm, "end": v(-328.7, -40.42) * mm});
            skLineSegment(sketch, "E149.1.0.77", {"start": v(-316, -46.77) * mm, "end": v(-316, -53.12) * mm});
            skLineSegment(sketch, "E149.1.0.78", {"start": v(-303.3, -59.47) * mm, "end": v(-303.3, -65.82) * mm});
            skLineSegment(sketch, "E149.1.0.79", {"start": v(-290.6, -72.17) * mm, "end": v(-290.6, -78.52) * mm});
            skLineSegment(sketch, "E149.1.0.80", {"start": v(-347.76, -72.17) * mm, "end": v(-341.4, -72.17) * mm});
            skLineSegment(sketch, "E149.1.0.81", {"start": v(-341.4, -84.87) * mm, "end": v(-341.4, -91.22) * mm});
            skLineSegment(sketch, "E149.1.0.82", {"start": v(-347.76, -78.52) * mm, "end": v(-341.4, -78.52) * mm});
            skLineSegment(sketch, "E149.1.0.83", {"start": v(-341.4, -72.17) * mm, "end": v(-341.4, -78.52) * mm});
            skLineSegment(sketch, "E149.1.0.84", {"start": v(-347.76, -84.87) * mm, "end": v(-341.4, -84.87) * mm});
            skLineSegment(sketch, "E149.1.0.85", {"start": v(-347.76, -59.47) * mm, "end": v(-341.4, -59.47) * mm});
            skLineSegment(sketch, "E149.1.0.86", {"start": v(-347.76, -72.17) * mm, "end": v(-347.76, -78.52) * mm});
            skLineSegment(sketch, "E149.1.0.87", {"start": v(-347.76, -65.82) * mm, "end": v(-341.4, -65.82) * mm});
            skLineSegment(sketch, "E149.1.0.88", {"start": v(-341.4, -59.47) * mm, "end": v(-341.4, -65.82) * mm});
            skLineSegment(sketch, "E149.1.0.89", {"start": v(-347.76, -59.47) * mm, "end": v(-347.76, -65.82) * mm});
            skLineSegment(sketch, "E149.1.0.90", {"start": v(-328.7, -59.47) * mm, "end": v(-328.7, -65.82) * mm});
            skLineSegment(sketch, "E149.1.0.91", {"start": v(-335.06, -59.47) * mm, "end": v(-335.06, -65.82) * mm});
            skLineSegment(sketch, "E149.1.0.92", {"start": v(-335.06, -65.82) * mm, "end": v(-328.7, -65.82) * mm});
            skLineSegment(sketch, "E149.1.0.93", {"start": v(-328.7, -72.17) * mm, "end": v(-328.7, -78.52) * mm});
            skLineSegment(sketch, "E149.1.0.94", {"start": v(-335.06, -72.17) * mm, "end": v(-328.7, -72.17) * mm});
            skLineSegment(sketch, "E149.1.0.95", {"start": v(-335.06, -72.17) * mm, "end": v(-335.06, -78.52) * mm});
            skLineSegment(sketch, "E149.1.0.96", {"start": v(-335.06, -78.52) * mm, "end": v(-328.7, -78.52) * mm});
            skLineSegment(sketch, "E149.1.0.97", {"start": v(-335.06, -59.47) * mm, "end": v(-328.7, -59.47) * mm});
            skLineSegment(sketch, "E149.1.0.98", {"start": v(-347.76, -91.22) * mm, "end": v(-335.06, -91.22) * mm, "construction": true});
            skLineSegment(sketch, "E149.1.0.99", {"start": v(-347.76, -91.22) * mm, "end": v(-347.76, -78.52) * mm, "construction": true});
            skLineSegment(sketch, "E149.1.0.100", {"start": v(-347.76, -84.87) * mm, "end": v(-347.76, -91.22) * mm});
            skLineSegment(sketch, "E149.1.0.101", {"start": v(-347.76, -91.22) * mm, "end": v(-341.4, -91.22) * mm});
            skLineSegment(sketch, "E149.1.1.0", {"start": v(-341.4, -300.77) * mm, "end": v(-341.4, -307.12) * mm});
            skLineSegment(sketch, "E149.1.1.1", {"start": v(-347.76, -300.77) * mm, "end": v(-347.76, -307.12) * mm});
            skLineSegment(sketch, "E149.1.1.2", {"start": v(-347.76, -307.12) * mm, "end": v(-341.4, -307.12) * mm});
            skLineSegment(sketch, "E149.1.1.3", {"start": v(-347.76, -300.77) * mm, "end": v(-341.4, -300.77) * mm});
            skLineSegment(sketch, "E149.1.1.4", {"start": v(-303.3, -338.87) * mm, "end": v(-303.3, -345.22) * mm});
            skLineSegment(sketch, "E149.1.1.5", {"start": v(-303.3, -288.07) * mm, "end": v(-303.3, -294.42) * mm});
            skLineSegment(sketch, "E149.1.1.6", {"start": v(-290.6, -300.77) * mm, "end": v(-290.6, -307.12) * mm});
            skLineSegment(sketch, "E149.1.1.7", {"start": v(-316, -326.17) * mm, "end": v(-316, -332.52) * mm});
            skLineSegment(sketch, "E149.1.1.8", {"start": v(-322.36, -326.17) * mm, "end": v(-322.36, -332.52) * mm});
            skLineSegment(sketch, "E149.1.1.9", {"start": v(-309.66, -338.87) * mm, "end": v(-309.66, -345.22) * mm});
            skLineSegment(sketch, "E149.1.1.10", {"start": v(-309.66, -288.07) * mm, "end": v(-309.66, -294.42) * mm});
            skLineSegment(sketch, "E149.1.1.11", {"start": v(-296.96, -300.77) * mm, "end": v(-296.96, -307.12) * mm});
            skLineSegment(sketch, "E149.1.1.12", {"start": v(-322.36, -332.52) * mm, "end": v(-316, -332.52) * mm});
            skLineSegment(sketch, "E149.1.1.13", {"start": v(-309.66, -345.22) * mm, "end": v(-303.3, -345.22) * mm});
            skLineSegment(sketch, "E149.1.1.14", {"start": v(-309.66, -294.42) * mm, "end": v(-303.3, -294.42) * mm});
            skLineSegment(sketch, "E149.1.1.15", {"start": v(-296.96, -307.12) * mm, "end": v(-290.6, -307.12) * mm});
            skLineSegment(sketch, "E149.1.1.16", {"start": v(-335.06, -338.87) * mm, "end": v(-335.06, -345.22) * mm});
            skLineSegment(sketch, "E149.1.1.17", {"start": v(-335.06, -288.07) * mm, "end": v(-335.06, -294.42) * mm});
            skLineSegment(sketch, "E149.1.1.18", {"start": v(-322.36, -300.77) * mm, "end": v(-322.36, -307.12) * mm});
            skLineSegment(sketch, "E149.1.1.19", {"start": v(-309.66, -313.47) * mm, "end": v(-309.66, -319.82) * mm});
            skLineSegment(sketch, "E149.1.1.20", {"start": v(-296.96, -326.17) * mm, "end": v(-296.96, -332.52) * mm});
            skLineSegment(sketch, "E149.1.1.21", {"start": v(-316, -338.87) * mm, "end": v(-316, -345.22) * mm});
            skLineSegment(sketch, "E149.1.1.22", {"start": v(-316, -288.07) * mm, "end": v(-316, -294.42) * mm});
            skLineSegment(sketch, "E149.1.1.23", {"start": v(-303.3, -300.77) * mm, "end": v(-303.3, -307.12) * mm});
            skLineSegment(sketch, "E149.1.1.24", {"start": v(-290.6, -313.47) * mm, "end": v(-290.6, -319.82) * mm});
            skLineSegment(sketch, "E149.1.1.25", {"start": v(-322.36, -338.87) * mm, "end": v(-316, -338.87) * mm});
            skLineSegment(sketch, "E149.1.1.26", {"start": v(-322.36, -288.07) * mm, "end": v(-316, -288.07) * mm});
            skLineSegment(sketch, "E149.1.1.27", {"start": v(-309.66, -300.77) * mm, "end": v(-303.3, -300.77) * mm});
            skLineSegment(sketch, "E149.1.1.28", {"start": v(-296.96, -313.47) * mm, "end": v(-290.6, -313.47) * mm});
            skLineSegment(sketch, "E149.1.1.29", {"start": v(-322.36, -338.87) * mm, "end": v(-322.36, -345.22) * mm});
            skLineSegment(sketch, "E149.1.1.30", {"start": v(-322.36, -288.07) * mm, "end": v(-322.36, -294.42) * mm});
            skLineSegment(sketch, "E149.1.1.31", {"start": v(-309.66, -300.77) * mm, "end": v(-309.66, -307.12) * mm});
            skLineSegment(sketch, "E149.1.1.32", {"start": v(-296.96, -313.47) * mm, "end": v(-296.96, -319.82) * mm});
            skLineSegment(sketch, "E149.1.1.33", {"start": v(-322.36, -345.22) * mm, "end": v(-316, -345.22) * mm});
            skLineSegment(sketch, "E149.1.1.34", {"start": v(-322.36, -294.42) * mm, "end": v(-316, -294.42) * mm});
            skLineSegment(sketch, "E149.1.1.35", {"start": v(-309.66, -307.12) * mm, "end": v(-303.3, -307.12) * mm});
            skLineSegment(sketch, "E149.1.1.36", {"start": v(-296.96, -319.82) * mm, "end": v(-290.6, -319.82) * mm});
            skLineSegment(sketch, "E149.1.1.37", {"start": v(-322.36, -326.17) * mm, "end": v(-316, -326.17) * mm});
            skLineSegment(sketch, "E149.1.1.38", {"start": v(-309.66, -338.87) * mm, "end": v(-303.3, -338.87) * mm});
            skLineSegment(sketch, "E149.1.1.39", {"start": v(-309.66, -288.07) * mm, "end": v(-303.3, -288.07) * mm});
            skLineSegment(sketch, "E149.1.1.40", {"start": v(-296.96, -300.77) * mm, "end": v(-290.6, -300.77) * mm});
            skLineSegment(sketch, "E149.1.1.41", {"start": v(-309.66, -326.17) * mm, "end": v(-303.3, -326.17) * mm});
            skLineSegment(sketch, "E149.1.1.42", {"start": v(-296.96, -338.87) * mm, "end": v(-290.6, -338.87) * mm});
            skLineSegment(sketch, "E149.1.1.43", {"start": v(-296.96, -288.07) * mm, "end": v(-290.6, -288.07) * mm});
            skLineSegment(sketch, "E149.1.1.44", {"start": v(-347.76, -288.07) * mm, "end": v(-341.4, -288.07) * mm});
            skLineSegment(sketch, "E149.1.1.45", {"start": v(-335.06, -300.77) * mm, "end": v(-328.7, -300.77) * mm});
            skLineSegment(sketch, "E149.1.1.46", {"start": v(-322.36, -313.47) * mm, "end": v(-316, -313.47) * mm});
            skLineSegment(sketch, "E149.1.1.47", {"start": v(-309.66, -332.52) * mm, "end": v(-303.3, -332.52) * mm});
            skLineSegment(sketch, "E149.1.1.48", {"start": v(-296.96, -345.22) * mm, "end": v(-290.6, -345.22) * mm});
            skLineSegment(sketch, "E149.1.1.49", {"start": v(-296.96, -294.42) * mm, "end": v(-290.6, -294.42) * mm});
            skLineSegment(sketch, "E149.1.1.50", {"start": v(-347.76, -294.42) * mm, "end": v(-341.4, -294.42) * mm});
            skLineSegment(sketch, "E149.1.1.51", {"start": v(-335.06, -307.12) * mm, "end": v(-328.7, -307.12) * mm});
            skLineSegment(sketch, "E149.1.1.52", {"start": v(-322.36, -319.82) * mm, "end": v(-316, -319.82) * mm});
            skLineSegment(sketch, "E149.1.1.53", {"start": v(-341.4, -288.07) * mm, "end": v(-341.4, -294.42) * mm});
            skLineSegment(sketch, "E149.1.1.54", {"start": v(-328.7, -300.77) * mm, "end": v(-328.7, -307.12) * mm});
            skLineSegment(sketch, "E149.1.1.55", {"start": v(-316, -313.47) * mm, "end": v(-316, -319.82) * mm});
            skLineSegment(sketch, "E149.1.1.56", {"start": v(-303.3, -326.17) * mm, "end": v(-303.3, -332.52) * mm});
            skLineSegment(sketch, "E149.1.1.57", {"start": v(-290.6, -338.87) * mm, "end": v(-290.6, -345.22) * mm});
            skLineSegment(sketch, "E149.1.1.58", {"start": v(-290.6, -288.07) * mm, "end": v(-290.6, -294.42) * mm});
            skLineSegment(sketch, "E149.1.1.59", {"start": v(-309.66, -313.47) * mm, "end": v(-303.3, -313.47) * mm});
            skLineSegment(sketch, "E149.1.1.60", {"start": v(-296.96, -326.17) * mm, "end": v(-290.6, -326.17) * mm});
            skLineSegment(sketch, "E149.1.1.61", {"start": v(-335.06, -338.87) * mm, "end": v(-328.7, -338.87) * mm});
            skLineSegment(sketch, "E149.1.1.62", {"start": v(-335.06, -288.07) * mm, "end": v(-328.7, -288.07) * mm});
            skLineSegment(sketch, "E149.1.1.63", {"start": v(-322.36, -300.77) * mm, "end": v(-316, -300.77) * mm});
            skLineSegment(sketch, "E149.1.1.64", {"start": v(-347.76, -288.07) * mm, "end": v(-347.76, -294.42) * mm});
            skLineSegment(sketch, "E149.1.1.65", {"start": v(-335.06, -300.77) * mm, "end": v(-335.06, -307.12) * mm});
            skLineSegment(sketch, "E149.1.1.66", {"start": v(-322.36, -313.47) * mm, "end": v(-322.36, -319.82) * mm});
            skLineSegment(sketch, "E149.1.1.67", {"start": v(-309.66, -326.17) * mm, "end": v(-309.66, -332.52) * mm});
            skLineSegment(sketch, "E149.1.1.68", {"start": v(-296.96, -338.87) * mm, "end": v(-296.96, -345.22) * mm});
            skLineSegment(sketch, "E149.1.1.69", {"start": v(-296.96, -288.07) * mm, "end": v(-296.96, -294.42) * mm});
            skLineSegment(sketch, "E149.1.1.70", {"start": v(-335.06, -345.22) * mm, "end": v(-328.7, -345.22) * mm});
            skLineSegment(sketch, "E149.1.1.71", {"start": v(-335.06, -294.42) * mm, "end": v(-328.7, -294.42) * mm});
            skLineSegment(sketch, "E149.1.1.72", {"start": v(-322.36, -307.12) * mm, "end": v(-316, -307.12) * mm});
            skLineSegment(sketch, "E149.1.1.73", {"start": v(-309.66, -319.82) * mm, "end": v(-303.3, -319.82) * mm});
            skLineSegment(sketch, "E149.1.1.74", {"start": v(-296.96, -332.52) * mm, "end": v(-290.6, -332.52) * mm});
            skLineSegment(sketch, "E149.1.1.75", {"start": v(-328.7, -338.87) * mm, "end": v(-328.7, -345.22) * mm});
            skLineSegment(sketch, "E149.1.1.76", {"start": v(-328.7, -288.07) * mm, "end": v(-328.7, -294.42) * mm});
            skLineSegment(sketch, "E149.1.1.77", {"start": v(-316, -300.77) * mm, "end": v(-316, -307.12) * mm});
            skLineSegment(sketch, "E149.1.1.78", {"start": v(-303.3, -313.47) * mm, "end": v(-303.3, -319.82) * mm});
            skLineSegment(sketch, "E149.1.1.79", {"start": v(-290.6, -326.17) * mm, "end": v(-290.6, -332.52) * mm});
            skLineSegment(sketch, "E149.1.1.80", {"start": v(-347.76, -326.17) * mm, "end": v(-341.4, -326.17) * mm});
            skLineSegment(sketch, "E149.1.1.81", {"start": v(-341.4, -338.87) * mm, "end": v(-341.4, -345.22) * mm});
            skLineSegment(sketch, "E149.1.1.82", {"start": v(-347.76, -332.52) * mm, "end": v(-341.4, -332.52) * mm});
            skLineSegment(sketch, "E149.1.1.83", {"start": v(-341.4, -326.17) * mm, "end": v(-341.4, -332.52) * mm});
            skLineSegment(sketch, "E149.1.1.84", {"start": v(-347.76, -338.87) * mm, "end": v(-341.4, -338.87) * mm});
            skLineSegment(sketch, "E149.1.1.85", {"start": v(-347.76, -313.47) * mm, "end": v(-341.4, -313.47) * mm});
            skLineSegment(sketch, "E149.1.1.86", {"start": v(-347.76, -326.17) * mm, "end": v(-347.76, -332.52) * mm});
            skLineSegment(sketch, "E149.1.1.87", {"start": v(-347.76, -319.82) * mm, "end": v(-341.4, -319.82) * mm});
            skLineSegment(sketch, "E149.1.1.88", {"start": v(-341.4, -313.47) * mm, "end": v(-341.4, -319.82) * mm});
            skLineSegment(sketch, "E149.1.1.89", {"start": v(-347.76, -313.47) * mm, "end": v(-347.76, -319.82) * mm});
            skLineSegment(sketch, "E149.1.1.90", {"start": v(-328.7, -313.47) * mm, "end": v(-328.7, -319.82) * mm});
            skLineSegment(sketch, "E149.1.1.91", {"start": v(-335.06, -313.47) * mm, "end": v(-335.06, -319.82) * mm});
            skLineSegment(sketch, "E149.1.1.92", {"start": v(-335.06, -319.82) * mm, "end": v(-328.7, -319.82) * mm});
            skLineSegment(sketch, "E149.1.1.93", {"start": v(-328.7, -326.17) * mm, "end": v(-328.7, -332.52) * mm});
            skLineSegment(sketch, "E149.1.1.94", {"start": v(-335.06, -326.17) * mm, "end": v(-328.7, -326.17) * mm});
            skLineSegment(sketch, "E149.1.1.95", {"start": v(-335.06, -326.17) * mm, "end": v(-335.06, -332.52) * mm});
            skLineSegment(sketch, "E149.1.1.96", {"start": v(-335.06, -332.52) * mm, "end": v(-328.7, -332.52) * mm});
            skLineSegment(sketch, "E149.1.1.97", {"start": v(-335.06, -313.47) * mm, "end": v(-328.7, -313.47) * mm});
            skLineSegment(sketch, "E149.1.1.98", {"start": v(-347.76, -345.22) * mm, "end": v(-335.06, -345.22) * mm, "construction": true});
            skLineSegment(sketch, "E149.1.1.99", {"start": v(-347.76, -345.22) * mm, "end": v(-347.76, -332.52) * mm, "construction": true});
            skLineSegment(sketch, "E149.1.1.100", {"start": v(-347.76, -338.87) * mm, "end": v(-347.76, -345.22) * mm});
            skLineSegment(sketch, "E149.1.1.101", {"start": v(-347.76, -345.22) * mm, "end": v(-341.4, -345.22) * mm});
            skLineSegment(sketch, "E149.2.0.0", {"start": v(-128.05, -46.77) * mm, "end": v(-128.05, -53.12) * mm});
            skLineSegment(sketch, "E149.2.0.1", {"start": v(-134.4, -46.77) * mm, "end": v(-134.4, -53.12) * mm});
            skLineSegment(sketch, "E149.2.0.2", {"start": v(-134.4, -53.12) * mm, "end": v(-128.05, -53.12) * mm});
            skLineSegment(sketch, "E149.2.0.3", {"start": v(-134.4, -46.77) * mm, "end": v(-128.05, -46.77) * mm});
            skLineSegment(sketch, "E149.2.0.4", {"start": v(-89.95, -84.87) * mm, "end": v(-89.95, -91.22) * mm});
            skLineSegment(sketch, "E149.2.0.5", {"start": v(-89.95, -34.07) * mm, "end": v(-89.95, -40.42) * mm});
            skLineSegment(sketch, "E149.2.0.6", {"start": v(-77.25, -46.77) * mm, "end": v(-77.25, -53.12) * mm});
            skLineSegment(sketch, "E149.2.0.7", {"start": v(-102.65, -72.17) * mm, "end": v(-102.65, -78.52) * mm});
            skLineSegment(sketch, "E149.2.0.8", {"start": v(-109, -72.17) * mm, "end": v(-109, -78.52) * mm});
            skLineSegment(sketch, "E149.2.0.9", {"start": v(-96.3, -84.87) * mm, "end": v(-96.3, -91.22) * mm});
            skLineSegment(sketch, "E149.2.0.10", {"start": v(-96.3, -34.07) * mm, "end": v(-96.3, -40.42) * mm});
            skLineSegment(sketch, "E149.2.0.11", {"start": v(-83.6, -46.77) * mm, "end": v(-83.6, -53.12) * mm});
            skLineSegment(sketch, "E149.2.0.12", {"start": v(-109, -78.52) * mm, "end": v(-102.65, -78.52) * mm});
            skLineSegment(sketch, "E149.2.0.13", {"start": v(-96.3, -91.22) * mm, "end": v(-89.95, -91.22) * mm});
            skLineSegment(sketch, "E149.2.0.14", {"start": v(-96.3, -40.42) * mm, "end": v(-89.95, -40.42) * mm});
            skLineSegment(sketch, "E149.2.0.15", {"start": v(-83.6, -53.12) * mm, "end": v(-77.25, -53.12) * mm});
            skLineSegment(sketch, "E149.2.0.16", {"start": v(-121.7, -84.87) * mm, "end": v(-121.7, -91.22) * mm});
            skLineSegment(sketch, "E149.2.0.17", {"start": v(-121.7, -34.07) * mm, "end": v(-121.7, -40.42) * mm});
            skLineSegment(sketch, "E149.2.0.18", {"start": v(-109, -46.77) * mm, "end": v(-109, -53.12) * mm});
            skLineSegment(sketch, "E149.2.0.19", {"start": v(-96.3, -59.47) * mm, "end": v(-96.3, -65.82) * mm});
            skLineSegment(sketch, "E149.2.0.20", {"start": v(-83.6, -72.17) * mm, "end": v(-83.6, -78.52) * mm});
            skLineSegment(sketch, "E149.2.0.21", {"start": v(-102.65, -84.87) * mm, "end": v(-102.65, -91.22) * mm});
            skLineSegment(sketch, "E149.2.0.22", {"start": v(-102.65, -34.07) * mm, "end": v(-102.65, -40.42) * mm});
            skLineSegment(sketch, "E149.2.0.23", {"start": v(-89.95, -46.77) * mm, "end": v(-89.95, -53.12) * mm});
            skLineSegment(sketch, "E149.2.0.24", {"start": v(-77.25, -59.47) * mm, "end": v(-77.25, -65.82) * mm});
            skLineSegment(sketch, "E149.2.0.25", {"start": v(-109, -84.87) * mm, "end": v(-102.65, -84.87) * mm});
            skLineSegment(sketch, "E149.2.0.26", {"start": v(-109, -34.07) * mm, "end": v(-102.65, -34.07) * mm});
            skLineSegment(sketch, "E149.2.0.27", {"start": v(-96.3, -46.77) * mm, "end": v(-89.95, -46.77) * mm});
            skLineSegment(sketch, "E149.2.0.28", {"start": v(-83.6, -59.47) * mm, "end": v(-77.25, -59.47) * mm});
            skLineSegment(sketch, "E149.2.0.29", {"start": v(-109, -84.87) * mm, "end": v(-109, -91.22) * mm});
            skLineSegment(sketch, "E149.2.0.30", {"start": v(-109, -34.07) * mm, "end": v(-109, -40.42) * mm});
            skLineSegment(sketch, "E149.2.0.31", {"start": v(-96.3, -46.77) * mm, "end": v(-96.3, -53.12) * mm});
            skLineSegment(sketch, "E149.2.0.32", {"start": v(-83.6, -59.47) * mm, "end": v(-83.6, -65.82) * mm});
            skLineSegment(sketch, "E149.2.0.33", {"start": v(-109, -91.22) * mm, "end": v(-102.65, -91.22) * mm});
            skLineSegment(sketch, "E149.2.0.34", {"start": v(-109, -40.42) * mm, "end": v(-102.65, -40.42) * mm});
            skLineSegment(sketch, "E149.2.0.35", {"start": v(-96.3, -53.12) * mm, "end": v(-89.95, -53.12) * mm});
            skLineSegment(sketch, "E149.2.0.36", {"start": v(-83.6, -65.82) * mm, "end": v(-77.25, -65.82) * mm});
            skLineSegment(sketch, "E149.2.0.37", {"start": v(-109, -72.17) * mm, "end": v(-102.65, -72.17) * mm});
            skLineSegment(sketch, "E149.2.0.38", {"start": v(-96.3, -84.87) * mm, "end": v(-89.95, -84.87) * mm});
            skLineSegment(sketch, "E149.2.0.39", {"start": v(-96.3, -34.07) * mm, "end": v(-89.95, -34.07) * mm});
            skLineSegment(sketch, "E149.2.0.40", {"start": v(-83.6, -46.77) * mm, "end": v(-77.25, -46.77) * mm});
            skLineSegment(sketch, "E149.2.0.41", {"start": v(-96.3, -72.17) * mm, "end": v(-89.95, -72.17) * mm});
            skLineSegment(sketch, "E149.2.0.42", {"start": v(-83.6, -84.87) * mm, "end": v(-77.25, -84.87) * mm});
            skLineSegment(sketch, "E149.2.0.43", {"start": v(-83.6, -34.07) * mm, "end": v(-77.25, -34.07) * mm});
            skLineSegment(sketch, "E149.2.0.44", {"start": v(-134.4, -34.07) * mm, "end": v(-128.05, -34.07) * mm});
            skLineSegment(sketch, "E149.2.0.45", {"start": v(-121.7, -46.77) * mm, "end": v(-115.35, -46.77) * mm});
            skLineSegment(sketch, "E149.2.0.46", {"start": v(-109, -59.47) * mm, "end": v(-102.65, -59.47) * mm});
            skLineSegment(sketch, "E149.2.0.47", {"start": v(-96.3, -78.52) * mm, "end": v(-89.95, -78.52) * mm});
            skLineSegment(sketch, "E149.2.0.48", {"start": v(-83.6, -91.22) * mm, "end": v(-77.25, -91.22) * mm});
            skLineSegment(sketch, "E149.2.0.49", {"start": v(-83.6, -40.42) * mm, "end": v(-77.25, -40.42) * mm});
            skLineSegment(sketch, "E149.2.0.50", {"start": v(-134.4, -40.42) * mm, "end": v(-128.05, -40.42) * mm});
            skLineSegment(sketch, "E149.2.0.51", {"start": v(-121.7, -53.12) * mm, "end": v(-115.35, -53.12) * mm});
            skLineSegment(sketch, "E149.2.0.52", {"start": v(-109, -65.82) * mm, "end": v(-102.65, -65.82) * mm});
            skLineSegment(sketch, "E149.2.0.53", {"start": v(-128.05, -34.07) * mm, "end": v(-128.05, -40.42) * mm});
            skLineSegment(sketch, "E149.2.0.54", {"start": v(-115.35, -46.77) * mm, "end": v(-115.35, -53.12) * mm});
            skLineSegment(sketch, "E149.2.0.55", {"start": v(-102.65, -59.47) * mm, "end": v(-102.65, -65.82) * mm});
            skLineSegment(sketch, "E149.2.0.56", {"start": v(-89.95, -72.17) * mm, "end": v(-89.95, -78.52) * mm});
            skLineSegment(sketch, "E149.2.0.57", {"start": v(-77.25, -84.87) * mm, "end": v(-77.25, -91.22) * mm});
            skLineSegment(sketch, "E149.2.0.58", {"start": v(-77.25, -34.07) * mm, "end": v(-77.25, -40.42) * mm});
            skLineSegment(sketch, "E149.2.0.59", {"start": v(-96.3, -59.47) * mm, "end": v(-89.95, -59.47) * mm});
            skLineSegment(sketch, "E149.2.0.60", {"start": v(-83.6, -72.17) * mm, "end": v(-77.25, -72.17) * mm});
            skLineSegment(sketch, "E149.2.0.61", {"start": v(-121.7, -84.87) * mm, "end": v(-115.35, -84.87) * mm});
            skLineSegment(sketch, "E149.2.0.62", {"start": v(-121.7, -34.07) * mm, "end": v(-115.35, -34.07) * mm});
            skLineSegment(sketch, "E149.2.0.63", {"start": v(-109, -46.77) * mm, "end": v(-102.65, -46.77) * mm});
            skLineSegment(sketch, "E149.2.0.64", {"start": v(-134.4, -34.07) * mm, "end": v(-134.4, -40.42) * mm});
            skLineSegment(sketch, "E149.2.0.65", {"start": v(-121.7, -46.77) * mm, "end": v(-121.7, -53.12) * mm});
            skLineSegment(sketch, "E149.2.0.66", {"start": v(-109, -59.47) * mm, "end": v(-109, -65.82) * mm});
            skLineSegment(sketch, "E149.2.0.67", {"start": v(-96.3, -72.17) * mm, "end": v(-96.3, -78.52) * mm});
            skLineSegment(sketch, "E149.2.0.68", {"start": v(-83.6, -84.87) * mm, "end": v(-83.6, -91.22) * mm});
            skLineSegment(sketch, "E149.2.0.69", {"start": v(-83.6, -34.07) * mm, "end": v(-83.6, -40.42) * mm});
            skLineSegment(sketch, "E149.2.0.70", {"start": v(-121.7, -91.22) * mm, "end": v(-115.35, -91.22) * mm});
            skLineSegment(sketch, "E149.2.0.71", {"start": v(-121.7, -40.42) * mm, "end": v(-115.35, -40.42) * mm});
            skLineSegment(sketch, "E149.2.0.72", {"start": v(-109, -53.12) * mm, "end": v(-102.65, -53.12) * mm});
            skLineSegment(sketch, "E149.2.0.73", {"start": v(-96.3, -65.82) * mm, "end": v(-89.95, -65.82) * mm});
            skLineSegment(sketch, "E149.2.0.74", {"start": v(-83.6, -78.52) * mm, "end": v(-77.25, -78.52) * mm});
            skLineSegment(sketch, "E149.2.0.75", {"start": v(-115.35, -84.87) * mm, "end": v(-115.35, -91.22) * mm});
            skLineSegment(sketch, "E149.2.0.76", {"start": v(-115.35, -34.07) * mm, "end": v(-115.35, -40.42) * mm});
            skLineSegment(sketch, "E149.2.0.77", {"start": v(-102.65, -46.77) * mm, "end": v(-102.65, -53.12) * mm});
            skLineSegment(sketch, "E149.2.0.78", {"start": v(-89.95, -59.47) * mm, "end": v(-89.95, -65.82) * mm});
            skLineSegment(sketch, "E149.2.0.79", {"start": v(-77.25, -72.17) * mm, "end": v(-77.25, -78.52) * mm});
            skLineSegment(sketch, "E149.2.0.80", {"start": v(-134.4, -72.17) * mm, "end": v(-128.05, -72.17) * mm});
            skLineSegment(sketch, "E149.2.0.81", {"start": v(-128.05, -84.87) * mm, "end": v(-128.05, -91.22) * mm});
            skLineSegment(sketch, "E149.2.0.82", {"start": v(-134.4, -78.52) * mm, "end": v(-128.05, -78.52) * mm});
            skLineSegment(sketch, "E149.2.0.83", {"start": v(-128.05, -72.17) * mm, "end": v(-128.05, -78.52) * mm});
            skLineSegment(sketch, "E149.2.0.84", {"start": v(-134.4, -84.87) * mm, "end": v(-128.05, -84.87) * mm});
            skLineSegment(sketch, "E149.2.0.85", {"start": v(-134.4, -59.47) * mm, "end": v(-128.05, -59.47) * mm});
            skLineSegment(sketch, "E149.2.0.86", {"start": v(-134.4, -72.17) * mm, "end": v(-134.4, -78.52) * mm});
            skLineSegment(sketch, "E149.2.0.87", {"start": v(-134.4, -65.82) * mm, "end": v(-128.05, -65.82) * mm});
            skLineSegment(sketch, "E149.2.0.88", {"start": v(-128.05, -59.47) * mm, "end": v(-128.05, -65.82) * mm});
            skLineSegment(sketch, "E149.2.0.89", {"start": v(-134.4, -59.47) * mm, "end": v(-134.4, -65.82) * mm});
            skLineSegment(sketch, "E149.2.0.90", {"start": v(-115.35, -59.47) * mm, "end": v(-115.35, -65.82) * mm});
            skLineSegment(sketch, "E149.2.0.91", {"start": v(-121.7, -59.47) * mm, "end": v(-121.7, -65.82) * mm});
            skLineSegment(sketch, "E149.2.0.92", {"start": v(-121.7, -65.82) * mm, "end": v(-115.35, -65.82) * mm});
            skLineSegment(sketch, "E149.2.0.93", {"start": v(-115.35, -72.17) * mm, "end": v(-115.35, -78.52) * mm});
            skLineSegment(sketch, "E149.2.0.94", {"start": v(-121.7, -72.17) * mm, "end": v(-115.35, -72.17) * mm});
            skLineSegment(sketch, "E149.2.0.95", {"start": v(-121.7, -72.17) * mm, "end": v(-121.7, -78.52) * mm});
            skLineSegment(sketch, "E149.2.0.96", {"start": v(-121.7, -78.52) * mm, "end": v(-115.35, -78.52) * mm});
            skLineSegment(sketch, "E149.2.0.97", {"start": v(-121.7, -59.47) * mm, "end": v(-115.35, -59.47) * mm});
            skLineSegment(sketch, "E149.2.0.98", {"start": v(-134.4, -91.22) * mm, "end": v(-121.7, -91.22) * mm, "construction": true});
            skLineSegment(sketch, "E149.2.0.99", {"start": v(-134.4, -91.22) * mm, "end": v(-134.4, -78.52) * mm, "construction": true});
            skLineSegment(sketch, "E149.2.0.100", {"start": v(-134.4, -84.87) * mm, "end": v(-134.4, -91.22) * mm});
            skLineSegment(sketch, "E149.2.0.101", {"start": v(-134.4, -91.22) * mm, "end": v(-128.05, -91.22) * mm});
            skLineSegment(sketch, "E149.2.1.0", {"start": v(-128.05, -300.77) * mm, "end": v(-128.05, -307.12) * mm});
            skLineSegment(sketch, "E149.2.1.1", {"start": v(-134.4, -300.77) * mm, "end": v(-134.4, -307.12) * mm});
            skLineSegment(sketch, "E149.2.1.2", {"start": v(-134.4, -307.12) * mm, "end": v(-128.05, -307.12) * mm});
            skLineSegment(sketch, "E149.2.1.3", {"start": v(-134.4, -300.77) * mm, "end": v(-128.05, -300.77) * mm});
            skLineSegment(sketch, "E149.2.1.4", {"start": v(-89.95, -338.87) * mm, "end": v(-89.95, -345.22) * mm});
            skLineSegment(sketch, "E149.2.1.5", {"start": v(-89.95, -288.07) * mm, "end": v(-89.95, -294.42) * mm});
            skLineSegment(sketch, "E149.2.1.6", {"start": v(-77.25, -300.77) * mm, "end": v(-77.25, -307.12) * mm});
            skLineSegment(sketch, "E149.2.1.7", {"start": v(-102.65, -326.17) * mm, "end": v(-102.65, -332.52) * mm});
            skLineSegment(sketch, "E149.2.1.8", {"start": v(-109, -326.17) * mm, "end": v(-109, -332.52) * mm});
            skLineSegment(sketch, "E149.2.1.9", {"start": v(-96.3, -338.87) * mm, "end": v(-96.3, -345.22) * mm});
            skLineSegment(sketch, "E149.2.1.10", {"start": v(-96.3, -288.07) * mm, "end": v(-96.3, -294.42) * mm});
            skLineSegment(sketch, "E149.2.1.11", {"start": v(-83.6, -300.77) * mm, "end": v(-83.6, -307.12) * mm});
            skLineSegment(sketch, "E149.2.1.12", {"start": v(-109, -332.52) * mm, "end": v(-102.65, -332.52) * mm});
            skLineSegment(sketch, "E149.2.1.13", {"start": v(-96.3, -345.22) * mm, "end": v(-89.95, -345.22) * mm});
            skLineSegment(sketch, "E149.2.1.14", {"start": v(-96.3, -294.42) * mm, "end": v(-89.95, -294.42) * mm});
            skLineSegment(sketch, "E149.2.1.15", {"start": v(-83.6, -307.12) * mm, "end": v(-77.25, -307.12) * mm});
            skLineSegment(sketch, "E149.2.1.16", {"start": v(-121.7, -338.87) * mm, "end": v(-121.7, -345.22) * mm});
            skLineSegment(sketch, "E149.2.1.17", {"start": v(-121.7, -288.07) * mm, "end": v(-121.7, -294.42) * mm});
            skLineSegment(sketch, "E149.2.1.18", {"start": v(-109, -300.77) * mm, "end": v(-109, -307.12) * mm});
            skLineSegment(sketch, "E149.2.1.19", {"start": v(-96.3, -313.47) * mm, "end": v(-96.3, -319.82) * mm});
            skLineSegment(sketch, "E149.2.1.20", {"start": v(-83.6, -326.17) * mm, "end": v(-83.6, -332.52) * mm});
            skLineSegment(sketch, "E149.2.1.21", {"start": v(-102.65, -338.87) * mm, "end": v(-102.65, -345.22) * mm});
            skLineSegment(sketch, "E149.2.1.22", {"start": v(-102.65, -288.07) * mm, "end": v(-102.65, -294.42) * mm});
            skLineSegment(sketch, "E149.2.1.23", {"start": v(-89.95, -300.77) * mm, "end": v(-89.95, -307.12) * mm});
            skLineSegment(sketch, "E149.2.1.24", {"start": v(-77.25, -313.47) * mm, "end": v(-77.25, -319.82) * mm});
            skLineSegment(sketch, "E149.2.1.25", {"start": v(-109, -338.87) * mm, "end": v(-102.65, -338.87) * mm});
            skLineSegment(sketch, "E149.2.1.26", {"start": v(-109, -288.07) * mm, "end": v(-102.65, -288.07) * mm});
            skLineSegment(sketch, "E149.2.1.27", {"start": v(-96.3, -300.77) * mm, "end": v(-89.95, -300.77) * mm});
            skLineSegment(sketch, "E149.2.1.28", {"start": v(-83.6, -313.47) * mm, "end": v(-77.25, -313.47) * mm});
            skLineSegment(sketch, "E149.2.1.29", {"start": v(-109, -338.87) * mm, "end": v(-109, -345.22) * mm});
            skLineSegment(sketch, "E149.2.1.30", {"start": v(-109, -288.07) * mm, "end": v(-109, -294.42) * mm});
            skLineSegment(sketch, "E149.2.1.31", {"start": v(-96.3, -300.77) * mm, "end": v(-96.3, -307.12) * mm});
            skLineSegment(sketch, "E149.2.1.32", {"start": v(-83.6, -313.47) * mm, "end": v(-83.6, -319.82) * mm});
            skLineSegment(sketch, "E149.2.1.33", {"start": v(-109, -345.22) * mm, "end": v(-102.65, -345.22) * mm});
            skLineSegment(sketch, "E149.2.1.34", {"start": v(-109, -294.42) * mm, "end": v(-102.65, -294.42) * mm});
            skLineSegment(sketch, "E149.2.1.35", {"start": v(-96.3, -307.12) * mm, "end": v(-89.95, -307.12) * mm});
            skLineSegment(sketch, "E149.2.1.36", {"start": v(-83.6, -319.82) * mm, "end": v(-77.25, -319.82) * mm});
            skLineSegment(sketch, "E149.2.1.37", {"start": v(-109, -326.17) * mm, "end": v(-102.65, -326.17) * mm});
            skLineSegment(sketch, "E149.2.1.38", {"start": v(-96.3, -338.87) * mm, "end": v(-89.95, -338.87) * mm});
            skLineSegment(sketch, "E149.2.1.39", {"start": v(-96.3, -288.07) * mm, "end": v(-89.95, -288.07) * mm});
            skLineSegment(sketch, "E149.2.1.40", {"start": v(-83.6, -300.77) * mm, "end": v(-77.25, -300.77) * mm});
            skLineSegment(sketch, "E149.2.1.41", {"start": v(-96.3, -326.17) * mm, "end": v(-89.95, -326.17) * mm});
            skLineSegment(sketch, "E149.2.1.42", {"start": v(-83.6, -338.87) * mm, "end": v(-77.25, -338.87) * mm});
            skLineSegment(sketch, "E149.2.1.43", {"start": v(-83.6, -288.07) * mm, "end": v(-77.25, -288.07) * mm});
            skLineSegment(sketch, "E149.2.1.44", {"start": v(-134.4, -288.07) * mm, "end": v(-128.05, -288.07) * mm});
            skLineSegment(sketch, "E149.2.1.45", {"start": v(-121.7, -300.77) * mm, "end": v(-115.35, -300.77) * mm});
            skLineSegment(sketch, "E149.2.1.46", {"start": v(-109, -313.47) * mm, "end": v(-102.65, -313.47) * mm});
            skLineSegment(sketch, "E149.2.1.47", {"start": v(-96.3, -332.52) * mm, "end": v(-89.95, -332.52) * mm});
            skLineSegment(sketch, "E149.2.1.48", {"start": v(-83.6, -345.22) * mm, "end": v(-77.25, -345.22) * mm});
            skLineSegment(sketch, "E149.2.1.49", {"start": v(-83.6, -294.42) * mm, "end": v(-77.25, -294.42) * mm});
            skLineSegment(sketch, "E149.2.1.50", {"start": v(-134.4, -294.42) * mm, "end": v(-128.05, -294.42) * mm});
            skLineSegment(sketch, "E149.2.1.51", {"start": v(-121.7, -307.12) * mm, "end": v(-115.35, -307.12) * mm});
            skLineSegment(sketch, "E149.2.1.52", {"start": v(-109, -319.82) * mm, "end": v(-102.65, -319.82) * mm});
            skLineSegment(sketch, "E149.2.1.53", {"start": v(-128.05, -288.07) * mm, "end": v(-128.05, -294.42) * mm});
            skLineSegment(sketch, "E149.2.1.54", {"start": v(-115.35, -300.77) * mm, "end": v(-115.35, -307.12) * mm});
            skLineSegment(sketch, "E149.2.1.55", {"start": v(-102.65, -313.47) * mm, "end": v(-102.65, -319.82) * mm});
            skLineSegment(sketch, "E149.2.1.56", {"start": v(-89.95, -326.17) * mm, "end": v(-89.95, -332.52) * mm});
            skLineSegment(sketch, "E149.2.1.57", {"start": v(-77.25, -338.87) * mm, "end": v(-77.25, -345.22) * mm});
            skLineSegment(sketch, "E149.2.1.58", {"start": v(-77.25, -288.07) * mm, "end": v(-77.25, -294.42) * mm});
            skLineSegment(sketch, "E149.2.1.59", {"start": v(-96.3, -313.47) * mm, "end": v(-89.95, -313.47) * mm});
            skLineSegment(sketch, "E149.2.1.60", {"start": v(-83.6, -326.17) * mm, "end": v(-77.25, -326.17) * mm});
            skLineSegment(sketch, "E149.2.1.61", {"start": v(-121.7, -338.87) * mm, "end": v(-115.35, -338.87) * mm});
            skLineSegment(sketch, "E149.2.1.62", {"start": v(-121.7, -288.07) * mm, "end": v(-115.35, -288.07) * mm});
            skLineSegment(sketch, "E149.2.1.63", {"start": v(-109, -300.77) * mm, "end": v(-102.65, -300.77) * mm});
            skLineSegment(sketch, "E149.2.1.64", {"start": v(-134.4, -288.07) * mm, "end": v(-134.4, -294.42) * mm});
            skLineSegment(sketch, "E149.2.1.65", {"start": v(-121.7, -300.77) * mm, "end": v(-121.7, -307.12) * mm});
            skLineSegment(sketch, "E149.2.1.66", {"start": v(-109, -313.47) * mm, "end": v(-109, -319.82) * mm});
            skLineSegment(sketch, "E149.2.1.67", {"start": v(-96.3, -326.17) * mm, "end": v(-96.3, -332.52) * mm});
            skLineSegment(sketch, "E149.2.1.68", {"start": v(-83.6, -338.87) * mm, "end": v(-83.6, -345.22) * mm});
            skLineSegment(sketch, "E149.2.1.69", {"start": v(-83.6, -288.07) * mm, "end": v(-83.6, -294.42) * mm});
            skLineSegment(sketch, "E149.2.1.70", {"start": v(-121.7, -345.22) * mm, "end": v(-115.35, -345.22) * mm});
            skLineSegment(sketch, "E149.2.1.71", {"start": v(-121.7, -294.42) * mm, "end": v(-115.35, -294.42) * mm});
            skLineSegment(sketch, "E149.2.1.72", {"start": v(-109, -307.12) * mm, "end": v(-102.65, -307.12) * mm});
            skLineSegment(sketch, "E149.2.1.73", {"start": v(-96.3, -319.82) * mm, "end": v(-89.95, -319.82) * mm});
            skLineSegment(sketch, "E149.2.1.74", {"start": v(-83.6, -332.52) * mm, "end": v(-77.25, -332.52) * mm});
            skLineSegment(sketch, "E149.2.1.75", {"start": v(-115.35, -338.87) * mm, "end": v(-115.35, -345.22) * mm});
            skLineSegment(sketch, "E149.2.1.76", {"start": v(-115.35, -288.07) * mm, "end": v(-115.35, -294.42) * mm});
            skLineSegment(sketch, "E149.2.1.77", {"start": v(-102.65, -300.77) * mm, "end": v(-102.65, -307.12) * mm});
            skLineSegment(sketch, "E149.2.1.78", {"start": v(-89.95, -313.47) * mm, "end": v(-89.95, -319.82) * mm});
            skLineSegment(sketch, "E149.2.1.79", {"start": v(-77.25, -326.17) * mm, "end": v(-77.25, -332.52) * mm});
            skLineSegment(sketch, "E149.2.1.80", {"start": v(-134.4, -326.17) * mm, "end": v(-128.05, -326.17) * mm});
            skLineSegment(sketch, "E149.2.1.81", {"start": v(-128.05, -338.87) * mm, "end": v(-128.05, -345.22) * mm});
            skLineSegment(sketch, "E149.2.1.82", {"start": v(-134.4, -332.52) * mm, "end": v(-128.05, -332.52) * mm});
            skLineSegment(sketch, "E149.2.1.83", {"start": v(-128.05, -326.17) * mm, "end": v(-128.05, -332.52) * mm});
            skLineSegment(sketch, "E149.2.1.84", {"start": v(-134.4, -338.87) * mm, "end": v(-128.05, -338.87) * mm});
            skLineSegment(sketch, "E149.2.1.85", {"start": v(-134.4, -313.47) * mm, "end": v(-128.05, -313.47) * mm});
            skLineSegment(sketch, "E149.2.1.86", {"start": v(-134.4, -326.17) * mm, "end": v(-134.4, -332.52) * mm});
            skLineSegment(sketch, "E149.2.1.87", {"start": v(-134.4, -319.82) * mm, "end": v(-128.05, -319.82) * mm});
            skLineSegment(sketch, "E149.2.1.88", {"start": v(-128.05, -313.47) * mm, "end": v(-128.05, -319.82) * mm});
            skLineSegment(sketch, "E149.2.1.89", {"start": v(-134.4, -313.47) * mm, "end": v(-134.4, -319.82) * mm});
            skLineSegment(sketch, "E149.2.1.90", {"start": v(-115.35, -313.47) * mm, "end": v(-115.35, -319.82) * mm});
            skLineSegment(sketch, "E149.2.1.91", {"start": v(-121.7, -313.47) * mm, "end": v(-121.7, -319.82) * mm});
            skLineSegment(sketch, "E149.2.1.92", {"start": v(-121.7, -319.82) * mm, "end": v(-115.35, -319.82) * mm});
            skLineSegment(sketch, "E149.2.1.93", {"start": v(-115.35, -326.17) * mm, "end": v(-115.35, -332.52) * mm});
            skLineSegment(sketch, "E149.2.1.94", {"start": v(-121.7, -326.17) * mm, "end": v(-115.35, -326.17) * mm});
            skLineSegment(sketch, "E149.2.1.95", {"start": v(-121.7, -326.17) * mm, "end": v(-121.7, -332.52) * mm});
            skLineSegment(sketch, "E149.2.1.96", {"start": v(-121.7, -332.52) * mm, "end": v(-115.35, -332.52) * mm});
            skLineSegment(sketch, "E149.2.1.97", {"start": v(-121.7, -313.47) * mm, "end": v(-115.35, -313.47) * mm});
            skLineSegment(sketch, "E149.2.1.98", {"start": v(-134.4, -345.22) * mm, "end": v(-121.7, -345.22) * mm, "construction": true});
            skLineSegment(sketch, "E149.2.1.99", {"start": v(-134.4, -345.22) * mm, "end": v(-134.4, -332.52) * mm, "construction": true});
            skLineSegment(sketch, "E149.2.1.100", {"start": v(-134.4, -338.87) * mm, "end": v(-134.4, -345.22) * mm});
            skLineSegment(sketch, "E149.2.1.101", {"start": v(-134.4, -345.22) * mm, "end": v(-128.05, -345.22) * mm});
            skLineSegment(sketch, "E149.3.0.0", {"start": v(85.31, -46.77) * mm, "end": v(85.31, -53.12) * mm});
            skLineSegment(sketch, "E149.3.0.1", {"start": v(78.96, -46.77) * mm, "end": v(78.96, -53.12) * mm});
            skLineSegment(sketch, "E149.3.0.2", {"start": v(78.96, -53.12) * mm, "end": v(85.31, -53.12) * mm});
            skLineSegment(sketch, "E149.3.0.3", {"start": v(78.96, -46.77) * mm, "end": v(85.31, -46.77) * mm});
            skLineSegment(sketch, "E149.3.0.4", {"start": v(123.41, -84.87) * mm, "end": v(123.41, -91.22) * mm});
            skLineSegment(sketch, "E149.3.0.5", {"start": v(123.41, -34.07) * mm, "end": v(123.41, -40.42) * mm});
            skLineSegment(sketch, "E149.3.0.6", {"start": v(136.11, -46.77) * mm, "end": v(136.11, -53.12) * mm});
            skLineSegment(sketch, "E149.3.0.7", {"start": v(110.71, -72.17) * mm, "end": v(110.71, -78.52) * mm});
            skLineSegment(sketch, "E149.3.0.8", {"start": v(104.36, -72.17) * mm, "end": v(104.36, -78.52) * mm});
            skLineSegment(sketch, "E149.3.0.9", {"start": v(117.06, -84.87) * mm, "end": v(117.06, -91.22) * mm});
            skLineSegment(sketch, "E149.3.0.10", {"start": v(117.06, -34.07) * mm, "end": v(117.06, -40.42) * mm});
            skLineSegment(sketch, "E149.3.0.11", {"start": v(129.76, -46.77) * mm, "end": v(129.76, -53.12) * mm});
            skLineSegment(sketch, "E149.3.0.12", {"start": v(104.36, -78.52) * mm, "end": v(110.71, -78.52) * mm});
            skLineSegment(sketch, "E149.3.0.13", {"start": v(117.06, -91.22) * mm, "end": v(123.41, -91.22) * mm});
            skLineSegment(sketch, "E149.3.0.14", {"start": v(117.06, -40.42) * mm, "end": v(123.41, -40.42) * mm});
            skLineSegment(sketch, "E149.3.0.15", {"start": v(129.76, -53.12) * mm, "end": v(136.11, -53.12) * mm});
            skLineSegment(sketch, "E149.3.0.16", {"start": v(91.66, -84.87) * mm, "end": v(91.66, -91.22) * mm});
            skLineSegment(sketch, "E149.3.0.17", {"start": v(91.66, -34.07) * mm, "end": v(91.66, -40.42) * mm});
            skLineSegment(sketch, "E149.3.0.18", {"start": v(104.36, -46.77) * mm, "end": v(104.36, -53.12) * mm});
            skLineSegment(sketch, "E149.3.0.19", {"start": v(117.06, -59.47) * mm, "end": v(117.06, -65.82) * mm});
            skLineSegment(sketch, "E149.3.0.20", {"start": v(129.76, -72.17) * mm, "end": v(129.76, -78.52) * mm});
            skLineSegment(sketch, "E149.3.0.21", {"start": v(110.71, -84.87) * mm, "end": v(110.71, -91.22) * mm});
            skLineSegment(sketch, "E149.3.0.22", {"start": v(110.71, -34.07) * mm, "end": v(110.71, -40.42) * mm});
            skLineSegment(sketch, "E149.3.0.23", {"start": v(123.41, -46.77) * mm, "end": v(123.41, -53.12) * mm});
            skLineSegment(sketch, "E149.3.0.24", {"start": v(136.11, -59.47) * mm, "end": v(136.11, -65.82) * mm});
            skLineSegment(sketch, "E149.3.0.25", {"start": v(104.36, -84.87) * mm, "end": v(110.71, -84.87) * mm});
            skLineSegment(sketch, "E149.3.0.26", {"start": v(104.36, -34.07) * mm, "end": v(110.71, -34.07) * mm});
            skLineSegment(sketch, "E149.3.0.27", {"start": v(117.06, -46.77) * mm, "end": v(123.41, -46.77) * mm});
            skLineSegment(sketch, "E149.3.0.28", {"start": v(129.76, -59.47) * mm, "end": v(136.11, -59.47) * mm});
            skLineSegment(sketch, "E149.3.0.29", {"start": v(104.36, -84.87) * mm, "end": v(104.36, -91.22) * mm});
            skLineSegment(sketch, "E149.3.0.30", {"start": v(104.36, -34.07) * mm, "end": v(104.36, -40.42) * mm});
            skLineSegment(sketch, "E149.3.0.31", {"start": v(117.06, -46.77) * mm, "end": v(117.06, -53.12) * mm});
            skLineSegment(sketch, "E149.3.0.32", {"start": v(129.76, -59.47) * mm, "end": v(129.76, -65.82) * mm});
            skLineSegment(sketch, "E149.3.0.33", {"start": v(104.36, -91.22) * mm, "end": v(110.71, -91.22) * mm});
            skLineSegment(sketch, "E149.3.0.34", {"start": v(104.36, -40.42) * mm, "end": v(110.71, -40.42) * mm});
            skLineSegment(sketch, "E149.3.0.35", {"start": v(117.06, -53.12) * mm, "end": v(123.41, -53.12) * mm});
            skLineSegment(sketch, "E149.3.0.36", {"start": v(129.76, -65.82) * mm, "end": v(136.11, -65.82) * mm});
            skLineSegment(sketch, "E149.3.0.37", {"start": v(104.36, -72.17) * mm, "end": v(110.71, -72.17) * mm});
            skLineSegment(sketch, "E149.3.0.38", {"start": v(117.06, -84.87) * mm, "end": v(123.41, -84.87) * mm});
            skLineSegment(sketch, "E149.3.0.39", {"start": v(117.06, -34.07) * mm, "end": v(123.41, -34.07) * mm});
            skLineSegment(sketch, "E149.3.0.40", {"start": v(129.76, -46.77) * mm, "end": v(136.11, -46.77) * mm});
            skLineSegment(sketch, "E149.3.0.41", {"start": v(117.06, -72.17) * mm, "end": v(123.41, -72.17) * mm});
            skLineSegment(sketch, "E149.3.0.42", {"start": v(129.76, -84.87) * mm, "end": v(136.11, -84.87) * mm});
            skLineSegment(sketch, "E149.3.0.43", {"start": v(129.76, -34.07) * mm, "end": v(136.11, -34.07) * mm});
            skLineSegment(sketch, "E149.3.0.44", {"start": v(78.96, -34.07) * mm, "end": v(85.31, -34.07) * mm});
            skLineSegment(sketch, "E149.3.0.45", {"start": v(91.66, -46.77) * mm, "end": v(98.01, -46.77) * mm});
            skLineSegment(sketch, "E149.3.0.46", {"start": v(104.36, -59.47) * mm, "end": v(110.71, -59.47) * mm});
            skLineSegment(sketch, "E149.3.0.47", {"start": v(117.06, -78.52) * mm, "end": v(123.41, -78.52) * mm});
            skLineSegment(sketch, "E149.3.0.48", {"start": v(129.76, -91.22) * mm, "end": v(136.11, -91.22) * mm});
            skLineSegment(sketch, "E149.3.0.49", {"start": v(129.76, -40.42) * mm, "end": v(136.11, -40.42) * mm});
            skLineSegment(sketch, "E149.3.0.50", {"start": v(78.96, -40.42) * mm, "end": v(85.31, -40.42) * mm});
            skLineSegment(sketch, "E149.3.0.51", {"start": v(91.66, -53.12) * mm, "end": v(98.01, -53.12) * mm});
            skLineSegment(sketch, "E149.3.0.52", {"start": v(104.36, -65.82) * mm, "end": v(110.71, -65.82) * mm});
            skLineSegment(sketch, "E149.3.0.53", {"start": v(85.31, -34.07) * mm, "end": v(85.31, -40.42) * mm});
            skLineSegment(sketch, "E149.3.0.54", {"start": v(98.01, -46.77) * mm, "end": v(98.01, -53.12) * mm});
            skLineSegment(sketch, "E149.3.0.55", {"start": v(110.71, -59.47) * mm, "end": v(110.71, -65.82) * mm});
            skLineSegment(sketch, "E149.3.0.56", {"start": v(123.41, -72.17) * mm, "end": v(123.41, -78.52) * mm});
            skLineSegment(sketch, "E149.3.0.57", {"start": v(136.11, -84.87) * mm, "end": v(136.11, -91.22) * mm});
            skLineSegment(sketch, "E149.3.0.58", {"start": v(136.11, -34.07) * mm, "end": v(136.11, -40.42) * mm});
            skLineSegment(sketch, "E149.3.0.59", {"start": v(117.06, -59.47) * mm, "end": v(123.41, -59.47) * mm});
            skLineSegment(sketch, "E149.3.0.60", {"start": v(129.76, -72.17) * mm, "end": v(136.11, -72.17) * mm});
            skLineSegment(sketch, "E149.3.0.61", {"start": v(91.66, -84.87) * mm, "end": v(98.01, -84.87) * mm});
            skLineSegment(sketch, "E149.3.0.62", {"start": v(91.66, -34.07) * mm, "end": v(98.01, -34.07) * mm});
            skLineSegment(sketch, "E149.3.0.63", {"start": v(104.36, -46.77) * mm, "end": v(110.71, -46.77) * mm});
            skLineSegment(sketch, "E149.3.0.64", {"start": v(78.96, -34.07) * mm, "end": v(78.96, -40.42) * mm});
            skLineSegment(sketch, "E149.3.0.65", {"start": v(91.66, -46.77) * mm, "end": v(91.66, -53.12) * mm});
            skLineSegment(sketch, "E149.3.0.66", {"start": v(104.36, -59.47) * mm, "end": v(104.36, -65.82) * mm});
            skLineSegment(sketch, "E149.3.0.67", {"start": v(117.06, -72.17) * mm, "end": v(117.06, -78.52) * mm});
            skLineSegment(sketch, "E149.3.0.68", {"start": v(129.76, -84.87) * mm, "end": v(129.76, -91.22) * mm});
            skLineSegment(sketch, "E149.3.0.69", {"start": v(129.76, -34.07) * mm, "end": v(129.76, -40.42) * mm});
            skLineSegment(sketch, "E149.3.0.70", {"start": v(91.66, -91.22) * mm, "end": v(98.01, -91.22) * mm});
            skLineSegment(sketch, "E149.3.0.71", {"start": v(91.66, -40.42) * mm, "end": v(98.01, -40.42) * mm});
            skLineSegment(sketch, "E149.3.0.72", {"start": v(104.36, -53.12) * mm, "end": v(110.71, -53.12) * mm});
            skLineSegment(sketch, "E149.3.0.73", {"start": v(117.06, -65.82) * mm, "end": v(123.41, -65.82) * mm});
            skLineSegment(sketch, "E149.3.0.74", {"start": v(129.76, -78.52) * mm, "end": v(136.11, -78.52) * mm});
            skLineSegment(sketch, "E149.3.0.75", {"start": v(98.01, -84.87) * mm, "end": v(98.01, -91.22) * mm});
            skLineSegment(sketch, "E149.3.0.76", {"start": v(98.01, -34.07) * mm, "end": v(98.01, -40.42) * mm});
            skLineSegment(sketch, "E149.3.0.77", {"start": v(110.71, -46.77) * mm, "end": v(110.71, -53.12) * mm});
            skLineSegment(sketch, "E149.3.0.78", {"start": v(123.41, -59.47) * mm, "end": v(123.41, -65.82) * mm});
            skLineSegment(sketch, "E149.3.0.79", {"start": v(136.11, -72.17) * mm, "end": v(136.11, -78.52) * mm});
            skLineSegment(sketch, "E149.3.0.80", {"start": v(78.96, -72.17) * mm, "end": v(85.31, -72.17) * mm});
            skLineSegment(sketch, "E149.3.0.81", {"start": v(85.31, -84.87) * mm, "end": v(85.31, -91.22) * mm});
            skLineSegment(sketch, "E149.3.0.82", {"start": v(78.96, -78.52) * mm, "end": v(85.31, -78.52) * mm});
            skLineSegment(sketch, "E149.3.0.83", {"start": v(85.31, -72.17) * mm, "end": v(85.31, -78.52) * mm});
            skLineSegment(sketch, "E149.3.0.84", {"start": v(78.96, -84.87) * mm, "end": v(85.31, -84.87) * mm});
            skLineSegment(sketch, "E149.3.0.85", {"start": v(78.96, -59.47) * mm, "end": v(85.31, -59.47) * mm});
            skLineSegment(sketch, "E149.3.0.86", {"start": v(78.96, -72.17) * mm, "end": v(78.96, -78.52) * mm});
            skLineSegment(sketch, "E149.3.0.87", {"start": v(78.96, -65.82) * mm, "end": v(85.31, -65.82) * mm});
            skLineSegment(sketch, "E149.3.0.88", {"start": v(85.31, -59.47) * mm, "end": v(85.31, -65.82) * mm});
            skLineSegment(sketch, "E149.3.0.89", {"start": v(78.96, -59.47) * mm, "end": v(78.96, -65.82) * mm});
            skLineSegment(sketch, "E149.3.0.90", {"start": v(98.01, -59.47) * mm, "end": v(98.01, -65.82) * mm});
            skLineSegment(sketch, "E149.3.0.91", {"start": v(91.66, -59.47) * mm, "end": v(91.66, -65.82) * mm});
            skLineSegment(sketch, "E149.3.0.92", {"start": v(91.66, -65.82) * mm, "end": v(98.01, -65.82) * mm});
            skLineSegment(sketch, "E149.3.0.93", {"start": v(98.01, -72.17) * mm, "end": v(98.01, -78.52) * mm});
            skLineSegment(sketch, "E149.3.0.94", {"start": v(91.66, -72.17) * mm, "end": v(98.01, -72.17) * mm});
            skLineSegment(sketch, "E149.3.0.95", {"start": v(91.66, -72.17) * mm, "end": v(91.66, -78.52) * mm});
            skLineSegment(sketch, "E149.3.0.96", {"start": v(91.66, -78.52) * mm, "end": v(98.01, -78.52) * mm});
            skLineSegment(sketch, "E149.3.0.97", {"start": v(91.66, -59.47) * mm, "end": v(98.01, -59.47) * mm});
            skLineSegment(sketch, "E149.3.0.98", {"start": v(78.96, -91.22) * mm, "end": v(91.66, -91.22) * mm, "construction": true});
            skLineSegment(sketch, "E149.3.0.99", {"start": v(78.96, -91.22) * mm, "end": v(78.96, -78.52) * mm, "construction": true});
            skLineSegment(sketch, "E149.3.0.100", {"start": v(78.96, -84.87) * mm, "end": v(78.96, -91.22) * mm});
            skLineSegment(sketch, "E149.3.0.101", {"start": v(78.96, -91.22) * mm, "end": v(85.31, -91.22) * mm});
            skLineSegment(sketch, "E149.3.1.0", {"start": v(85.31, -300.77) * mm, "end": v(85.31, -307.12) * mm});
            skLineSegment(sketch, "E149.3.1.1", {"start": v(78.96, -300.77) * mm, "end": v(78.96, -307.12) * mm});
            skLineSegment(sketch, "E149.3.1.2", {"start": v(78.96, -307.12) * mm, "end": v(85.31, -307.12) * mm});
            skLineSegment(sketch, "E149.3.1.3", {"start": v(78.96, -300.77) * mm, "end": v(85.31, -300.77) * mm});
            skLineSegment(sketch, "E149.3.1.4", {"start": v(123.41, -338.87) * mm, "end": v(123.41, -345.22) * mm});
            skLineSegment(sketch, "E149.3.1.5", {"start": v(123.41, -288.07) * mm, "end": v(123.41, -294.42) * mm});
            skLineSegment(sketch, "E149.3.1.6", {"start": v(136.11, -300.77) * mm, "end": v(136.11, -307.12) * mm});
            skLineSegment(sketch, "E149.3.1.7", {"start": v(110.71, -326.17) * mm, "end": v(110.71, -332.52) * mm});
            skLineSegment(sketch, "E149.3.1.8", {"start": v(104.36, -326.17) * mm, "end": v(104.36, -332.52) * mm});
            skLineSegment(sketch, "E149.3.1.9", {"start": v(117.06, -338.87) * mm, "end": v(117.06, -345.22) * mm});
            skLineSegment(sketch, "E149.3.1.10", {"start": v(117.06, -288.07) * mm, "end": v(117.06, -294.42) * mm});
            skLineSegment(sketch, "E149.3.1.11", {"start": v(129.76, -300.77) * mm, "end": v(129.76, -307.12) * mm});
            skLineSegment(sketch, "E149.3.1.12", {"start": v(104.36, -332.52) * mm, "end": v(110.71, -332.52) * mm});
            skLineSegment(sketch, "E149.3.1.13", {"start": v(117.06, -345.22) * mm, "end": v(123.41, -345.22) * mm});
            skLineSegment(sketch, "E149.3.1.14", {"start": v(117.06, -294.42) * mm, "end": v(123.41, -294.42) * mm});
            skLineSegment(sketch, "E149.3.1.15", {"start": v(129.76, -307.12) * mm, "end": v(136.11, -307.12) * mm});
            skLineSegment(sketch, "E149.3.1.16", {"start": v(91.66, -338.87) * mm, "end": v(91.66, -345.22) * mm});
            skLineSegment(sketch, "E149.3.1.17", {"start": v(91.66, -288.07) * mm, "end": v(91.66, -294.42) * mm});
            skLineSegment(sketch, "E149.3.1.18", {"start": v(104.36, -300.77) * mm, "end": v(104.36, -307.12) * mm});
            skLineSegment(sketch, "E149.3.1.19", {"start": v(117.06, -313.47) * mm, "end": v(117.06, -319.82) * mm});
            skLineSegment(sketch, "E149.3.1.20", {"start": v(129.76, -326.17) * mm, "end": v(129.76, -332.52) * mm});
            skLineSegment(sketch, "E149.3.1.21", {"start": v(110.71, -338.87) * mm, "end": v(110.71, -345.22) * mm});
            skLineSegment(sketch, "E149.3.1.22", {"start": v(110.71, -288.07) * mm, "end": v(110.71, -294.42) * mm});
            skLineSegment(sketch, "E149.3.1.23", {"start": v(123.41, -300.77) * mm, "end": v(123.41, -307.12) * mm});
            skLineSegment(sketch, "E149.3.1.24", {"start": v(136.11, -313.47) * mm, "end": v(136.11, -319.82) * mm});
            skLineSegment(sketch, "E149.3.1.25", {"start": v(104.36, -338.87) * mm, "end": v(110.71, -338.87) * mm});
            skLineSegment(sketch, "E149.3.1.26", {"start": v(104.36, -288.07) * mm, "end": v(110.71, -288.07) * mm});
            skLineSegment(sketch, "E149.3.1.27", {"start": v(117.06, -300.77) * mm, "end": v(123.41, -300.77) * mm});
            skLineSegment(sketch, "E149.3.1.28", {"start": v(129.76, -313.47) * mm, "end": v(136.11, -313.47) * mm});
            skLineSegment(sketch, "E149.3.1.29", {"start": v(104.36, -338.87) * mm, "end": v(104.36, -345.22) * mm});
            skLineSegment(sketch, "E149.3.1.30", {"start": v(104.36, -288.07) * mm, "end": v(104.36, -294.42) * mm});
            skLineSegment(sketch, "E149.3.1.31", {"start": v(117.06, -300.77) * mm, "end": v(117.06, -307.12) * mm});
            skLineSegment(sketch, "E149.3.1.32", {"start": v(129.76, -313.47) * mm, "end": v(129.76, -319.82) * mm});
            skLineSegment(sketch, "E149.3.1.33", {"start": v(104.36, -345.22) * mm, "end": v(110.71, -345.22) * mm});
            skLineSegment(sketch, "E149.3.1.34", {"start": v(104.36, -294.42) * mm, "end": v(110.71, -294.42) * mm});
            skLineSegment(sketch, "E149.3.1.35", {"start": v(117.06, -307.12) * mm, "end": v(123.41, -307.12) * mm});
            skLineSegment(sketch, "E149.3.1.36", {"start": v(129.76, -319.82) * mm, "end": v(136.11, -319.82) * mm});
            skLineSegment(sketch, "E149.3.1.37", {"start": v(104.36, -326.17) * mm, "end": v(110.71, -326.17) * mm});
            skLineSegment(sketch, "E149.3.1.38", {"start": v(117.06, -338.87) * mm, "end": v(123.41, -338.87) * mm});
            skLineSegment(sketch, "E149.3.1.39", {"start": v(117.06, -288.07) * mm, "end": v(123.41, -288.07) * mm});
            skLineSegment(sketch, "E149.3.1.40", {"start": v(129.76, -300.77) * mm, "end": v(136.11, -300.77) * mm});
            skLineSegment(sketch, "E149.3.1.41", {"start": v(117.06, -326.17) * mm, "end": v(123.41, -326.17) * mm});
            skLineSegment(sketch, "E149.3.1.42", {"start": v(129.76, -338.87) * mm, "end": v(136.11, -338.87) * mm});
            skLineSegment(sketch, "E149.3.1.43", {"start": v(129.76, -288.07) * mm, "end": v(136.11, -288.07) * mm});
            skLineSegment(sketch, "E149.3.1.44", {"start": v(78.96, -288.07) * mm, "end": v(85.31, -288.07) * mm});
            skLineSegment(sketch, "E149.3.1.45", {"start": v(91.66, -300.77) * mm, "end": v(98.01, -300.77) * mm});
            skLineSegment(sketch, "E149.3.1.46", {"start": v(104.36, -313.47) * mm, "end": v(110.71, -313.47) * mm});
            skLineSegment(sketch, "E149.3.1.47", {"start": v(117.06, -332.52) * mm, "end": v(123.41, -332.52) * mm});
            skLineSegment(sketch, "E149.3.1.48", {"start": v(129.76, -345.22) * mm, "end": v(136.11, -345.22) * mm});
            skLineSegment(sketch, "E149.3.1.49", {"start": v(129.76, -294.42) * mm, "end": v(136.11, -294.42) * mm});
            skLineSegment(sketch, "E149.3.1.50", {"start": v(78.96, -294.42) * mm, "end": v(85.31, -294.42) * mm});
            skLineSegment(sketch, "E149.3.1.51", {"start": v(91.66, -307.12) * mm, "end": v(98.01, -307.12) * mm});
            skLineSegment(sketch, "E149.3.1.52", {"start": v(104.36, -319.82) * mm, "end": v(110.71, -319.82) * mm});
            skLineSegment(sketch, "E149.3.1.53", {"start": v(85.31, -288.07) * mm, "end": v(85.31, -294.42) * mm});
            skLineSegment(sketch, "E149.3.1.54", {"start": v(98.01, -300.77) * mm, "end": v(98.01, -307.12) * mm});
            skLineSegment(sketch, "E149.3.1.55", {"start": v(110.71, -313.47) * mm, "end": v(110.71, -319.82) * mm});
            skLineSegment(sketch, "E149.3.1.56", {"start": v(123.41, -326.17) * mm, "end": v(123.41, -332.52) * mm});
            skLineSegment(sketch, "E149.3.1.57", {"start": v(136.11, -338.87) * mm, "end": v(136.11, -345.22) * mm});
            skLineSegment(sketch, "E149.3.1.58", {"start": v(136.11, -288.07) * mm, "end": v(136.11, -294.42) * mm});
            skLineSegment(sketch, "E149.3.1.59", {"start": v(117.06, -313.47) * mm, "end": v(123.41, -313.47) * mm});
            skLineSegment(sketch, "E149.3.1.60", {"start": v(129.76, -326.17) * mm, "end": v(136.11, -326.17) * mm});
            skLineSegment(sketch, "E149.3.1.61", {"start": v(91.66, -338.87) * mm, "end": v(98.01, -338.87) * mm});
            skLineSegment(sketch, "E149.3.1.62", {"start": v(91.66, -288.07) * mm, "end": v(98.01, -288.07) * mm});
            skLineSegment(sketch, "E149.3.1.63", {"start": v(104.36, -300.77) * mm, "end": v(110.71, -300.77) * mm});
            skLineSegment(sketch, "E149.3.1.64", {"start": v(78.96, -288.07) * mm, "end": v(78.96, -294.42) * mm});
            skLineSegment(sketch, "E149.3.1.65", {"start": v(91.66, -300.77) * mm, "end": v(91.66, -307.12) * mm});
            skLineSegment(sketch, "E149.3.1.66", {"start": v(104.36, -313.47) * mm, "end": v(104.36, -319.82) * mm});
            skLineSegment(sketch, "E149.3.1.67", {"start": v(117.06, -326.17) * mm, "end": v(117.06, -332.52) * mm});
            skLineSegment(sketch, "E149.3.1.68", {"start": v(129.76, -338.87) * mm, "end": v(129.76, -345.22) * mm});
            skLineSegment(sketch, "E149.3.1.69", {"start": v(129.76, -288.07) * mm, "end": v(129.76, -294.42) * mm});
            skLineSegment(sketch, "E149.3.1.70", {"start": v(91.66, -345.22) * mm, "end": v(98.01, -345.22) * mm});
            skLineSegment(sketch, "E149.3.1.71", {"start": v(91.66, -294.42) * mm, "end": v(98.01, -294.42) * mm});
            skLineSegment(sketch, "E149.3.1.72", {"start": v(104.36, -307.12) * mm, "end": v(110.71, -307.12) * mm});
            skLineSegment(sketch, "E149.3.1.73", {"start": v(117.06, -319.82) * mm, "end": v(123.41, -319.82) * mm});
            skLineSegment(sketch, "E149.3.1.74", {"start": v(129.76, -332.52) * mm, "end": v(136.11, -332.52) * mm});
            skLineSegment(sketch, "E149.3.1.75", {"start": v(98.01, -338.87) * mm, "end": v(98.01, -345.22) * mm});
            skLineSegment(sketch, "E149.3.1.76", {"start": v(98.01, -288.07) * mm, "end": v(98.01, -294.42) * mm});
            skLineSegment(sketch, "E149.3.1.77", {"start": v(110.71, -300.77) * mm, "end": v(110.71, -307.12) * mm});
            skLineSegment(sketch, "E149.3.1.78", {"start": v(123.41, -313.47) * mm, "end": v(123.41, -319.82) * mm});
            skLineSegment(sketch, "E149.3.1.79", {"start": v(136.11, -326.17) * mm, "end": v(136.11, -332.52) * mm});
            skLineSegment(sketch, "E149.3.1.80", {"start": v(78.96, -326.17) * mm, "end": v(85.31, -326.17) * mm});
            skLineSegment(sketch, "E149.3.1.81", {"start": v(85.31, -338.87) * mm, "end": v(85.31, -345.22) * mm});
            skLineSegment(sketch, "E149.3.1.82", {"start": v(78.96, -332.52) * mm, "end": v(85.31, -332.52) * mm});
            skLineSegment(sketch, "E149.3.1.83", {"start": v(85.31, -326.17) * mm, "end": v(85.31, -332.52) * mm});
            skLineSegment(sketch, "E149.3.1.84", {"start": v(78.96, -338.87) * mm, "end": v(85.31, -338.87) * mm});
            skLineSegment(sketch, "E149.3.1.85", {"start": v(78.96, -313.47) * mm, "end": v(85.31, -313.47) * mm});
            skLineSegment(sketch, "E149.3.1.86", {"start": v(78.96, -326.17) * mm, "end": v(78.96, -332.52) * mm});
            skLineSegment(sketch, "E149.3.1.87", {"start": v(78.96, -319.82) * mm, "end": v(85.31, -319.82) * mm});
            skLineSegment(sketch, "E149.3.1.88", {"start": v(85.31, -313.47) * mm, "end": v(85.31, -319.82) * mm});
            skLineSegment(sketch, "E149.3.1.89", {"start": v(78.96, -313.47) * mm, "end": v(78.96, -319.82) * mm});
            skLineSegment(sketch, "E149.3.1.90", {"start": v(98.01, -313.47) * mm, "end": v(98.01, -319.82) * mm});
            skLineSegment(sketch, "E149.3.1.91", {"start": v(91.66, -313.47) * mm, "end": v(91.66, -319.82) * mm});
            skLineSegment(sketch, "E149.3.1.92", {"start": v(91.66, -319.82) * mm, "end": v(98.01, -319.82) * mm});
            skLineSegment(sketch, "E149.3.1.93", {"start": v(98.01, -326.17) * mm, "end": v(98.01, -332.52) * mm});
            skLineSegment(sketch, "E149.3.1.94", {"start": v(91.66, -326.17) * mm, "end": v(98.01, -326.17) * mm});
            skLineSegment(sketch, "E149.3.1.95", {"start": v(91.66, -326.17) * mm, "end": v(91.66, -332.52) * mm});
            skLineSegment(sketch, "E149.3.1.96", {"start": v(91.66, -332.52) * mm, "end": v(98.01, -332.52) * mm});
            skLineSegment(sketch, "E149.3.1.97", {"start": v(91.66, -313.47) * mm, "end": v(98.01, -313.47) * mm});
            skLineSegment(sketch, "E149.3.1.98", {"start": v(78.96, -345.22) * mm, "end": v(91.66, -345.22) * mm, "construction": true});
            skLineSegment(sketch, "E149.3.1.99", {"start": v(78.96, -345.22) * mm, "end": v(78.96, -332.52) * mm, "construction": true});
            skLineSegment(sketch, "E149.3.1.100", {"start": v(78.96, -338.87) * mm, "end": v(78.96, -345.22) * mm});
            skLineSegment(sketch, "E149.3.1.101", {"start": v(78.96, -345.22) * mm, "end": v(85.31, -345.22) * mm});
            skLineSegment(sketch, "E149.4.0.0", {"start": v(298.67, -46.77) * mm, "end": v(298.67, -53.12) * mm});
            skLineSegment(sketch, "E149.4.0.1", {"start": v(292.32, -46.77) * mm, "end": v(292.32, -53.12) * mm});
            skLineSegment(sketch, "E149.4.0.2", {"start": v(292.32, -53.12) * mm, "end": v(298.67, -53.12) * mm});
            skLineSegment(sketch, "E149.4.0.3", {"start": v(292.32, -46.77) * mm, "end": v(298.67, -46.77) * mm});
            skLineSegment(sketch, "E149.4.0.4", {"start": v(336.77, -84.87) * mm, "end": v(336.77, -91.22) * mm});
            skLineSegment(sketch, "E149.4.0.5", {"start": v(336.77, -34.07) * mm, "end": v(336.77, -40.42) * mm});
            skLineSegment(sketch, "E149.4.0.6", {"start": v(349.47, -46.77) * mm, "end": v(349.47, -53.12) * mm});
            skLineSegment(sketch, "E149.4.0.7", {"start": v(324.07, -72.17) * mm, "end": v(324.07, -78.52) * mm});
            skLineSegment(sketch, "E149.4.0.8", {"start": v(317.72, -72.17) * mm, "end": v(317.72, -78.52) * mm});
            skLineSegment(sketch, "E149.4.0.9", {"start": v(330.42, -84.87) * mm, "end": v(330.42, -91.22) * mm});
            skLineSegment(sketch, "E149.4.0.10", {"start": v(330.42, -34.07) * mm, "end": v(330.42, -40.42) * mm});
            skLineSegment(sketch, "E149.4.0.11", {"start": v(343.12, -46.77) * mm, "end": v(343.12, -53.12) * mm});
            skLineSegment(sketch, "E149.4.0.12", {"start": v(317.72, -78.52) * mm, "end": v(324.07, -78.52) * mm});
            skLineSegment(sketch, "E149.4.0.13", {"start": v(330.42, -91.22) * mm, "end": v(336.77, -91.22) * mm});
            skLineSegment(sketch, "E149.4.0.14", {"start": v(330.42, -40.42) * mm, "end": v(336.77, -40.42) * mm});
            skLineSegment(sketch, "E149.4.0.15", {"start": v(343.12, -53.12) * mm, "end": v(349.47, -53.12) * mm});
            skLineSegment(sketch, "E149.4.0.16", {"start": v(305.02, -84.87) * mm, "end": v(305.02, -91.22) * mm});
            skLineSegment(sketch, "E149.4.0.17", {"start": v(305.02, -34.07) * mm, "end": v(305.02, -40.42) * mm});
            skLineSegment(sketch, "E149.4.0.18", {"start": v(317.72, -46.77) * mm, "end": v(317.72, -53.12) * mm});
            skLineSegment(sketch, "E149.4.0.19", {"start": v(330.42, -59.47) * mm, "end": v(330.42, -65.82) * mm});
            skLineSegment(sketch, "E149.4.0.20", {"start": v(343.12, -72.17) * mm, "end": v(343.12, -78.52) * mm});
            skLineSegment(sketch, "E149.4.0.21", {"start": v(324.07, -84.87) * mm, "end": v(324.07, -91.22) * mm});
            skLineSegment(sketch, "E149.4.0.22", {"start": v(324.07, -34.07) * mm, "end": v(324.07, -40.42) * mm});
            skLineSegment(sketch, "E149.4.0.23", {"start": v(336.77, -46.77) * mm, "end": v(336.77, -53.12) * mm});
            skLineSegment(sketch, "E149.4.0.24", {"start": v(349.47, -59.47) * mm, "end": v(349.47, -65.82) * mm});
            skLineSegment(sketch, "E149.4.0.25", {"start": v(317.72, -84.87) * mm, "end": v(324.07, -84.87) * mm});
            skLineSegment(sketch, "E149.4.0.26", {"start": v(317.72, -34.07) * mm, "end": v(324.07, -34.07) * mm});
            skLineSegment(sketch, "E149.4.0.27", {"start": v(330.42, -46.77) * mm, "end": v(336.77, -46.77) * mm});
            skLineSegment(sketch, "E149.4.0.28", {"start": v(343.12, -59.47) * mm, "end": v(349.47, -59.47) * mm});
            skLineSegment(sketch, "E149.4.0.29", {"start": v(317.72, -84.87) * mm, "end": v(317.72, -91.22) * mm});
            skLineSegment(sketch, "E149.4.0.30", {"start": v(317.72, -34.07) * mm, "end": v(317.72, -40.42) * mm});
            skLineSegment(sketch, "E149.4.0.31", {"start": v(330.42, -46.77) * mm, "end": v(330.42, -53.12) * mm});
            skLineSegment(sketch, "E149.4.0.32", {"start": v(343.12, -59.47) * mm, "end": v(343.12, -65.82) * mm});
            skLineSegment(sketch, "E149.4.0.33", {"start": v(317.72, -91.22) * mm, "end": v(324.07, -91.22) * mm});
            skLineSegment(sketch, "E149.4.0.34", {"start": v(317.72, -40.42) * mm, "end": v(324.07, -40.42) * mm});
            skLineSegment(sketch, "E149.4.0.35", {"start": v(330.42, -53.12) * mm, "end": v(336.77, -53.12) * mm});
            skLineSegment(sketch, "E149.4.0.36", {"start": v(343.12, -65.82) * mm, "end": v(349.47, -65.82) * mm});
            skLineSegment(sketch, "E149.4.0.37", {"start": v(317.72, -72.17) * mm, "end": v(324.07, -72.17) * mm});
            skLineSegment(sketch, "E149.4.0.38", {"start": v(330.42, -84.87) * mm, "end": v(336.77, -84.87) * mm});
            skLineSegment(sketch, "E149.4.0.39", {"start": v(330.42, -34.07) * mm, "end": v(336.77, -34.07) * mm});
            skLineSegment(sketch, "E149.4.0.40", {"start": v(343.12, -46.77) * mm, "end": v(349.47, -46.77) * mm});
            skLineSegment(sketch, "E149.4.0.41", {"start": v(330.42, -72.17) * mm, "end": v(336.77, -72.17) * mm});
            skLineSegment(sketch, "E149.4.0.42", {"start": v(343.12, -84.87) * mm, "end": v(349.47, -84.87) * mm});
            skLineSegment(sketch, "E149.4.0.43", {"start": v(343.12, -34.07) * mm, "end": v(349.47, -34.07) * mm});
            skLineSegment(sketch, "E149.4.0.44", {"start": v(292.32, -34.07) * mm, "end": v(298.67, -34.07) * mm});
            skLineSegment(sketch, "E149.4.0.45", {"start": v(305.02, -46.77) * mm, "end": v(311.37, -46.77) * mm});
            skLineSegment(sketch, "E149.4.0.46", {"start": v(317.72, -59.47) * mm, "end": v(324.07, -59.47) * mm});
            skLineSegment(sketch, "E149.4.0.47", {"start": v(330.42, -78.52) * mm, "end": v(336.77, -78.52) * mm});
            skLineSegment(sketch, "E149.4.0.48", {"start": v(343.12, -91.22) * mm, "end": v(349.47, -91.22) * mm});
            skLineSegment(sketch, "E149.4.0.49", {"start": v(343.12, -40.42) * mm, "end": v(349.47, -40.42) * mm});
            skLineSegment(sketch, "E149.4.0.50", {"start": v(292.32, -40.42) * mm, "end": v(298.67, -40.42) * mm});
            skLineSegment(sketch, "E149.4.0.51", {"start": v(305.02, -53.12) * mm, "end": v(311.37, -53.12) * mm});
            skLineSegment(sketch, "E149.4.0.52", {"start": v(317.72, -65.82) * mm, "end": v(324.07, -65.82) * mm});
            skLineSegment(sketch, "E149.4.0.53", {"start": v(298.67, -34.07) * mm, "end": v(298.67, -40.42) * mm});
            skLineSegment(sketch, "E149.4.0.54", {"start": v(311.37, -46.77) * mm, "end": v(311.37, -53.12) * mm});
            skLineSegment(sketch, "E149.4.0.55", {"start": v(324.07, -59.47) * mm, "end": v(324.07, -65.82) * mm});
            skLineSegment(sketch, "E149.4.0.56", {"start": v(336.77, -72.17) * mm, "end": v(336.77, -78.52) * mm});
            skLineSegment(sketch, "E149.4.0.57", {"start": v(349.47, -84.87) * mm, "end": v(349.47, -91.22) * mm});
            skLineSegment(sketch, "E149.4.0.58", {"start": v(349.47, -34.07) * mm, "end": v(349.47, -40.42) * mm});
            skLineSegment(sketch, "E149.4.0.59", {"start": v(330.42, -59.47) * mm, "end": v(336.77, -59.47) * mm});
            skLineSegment(sketch, "E149.4.0.60", {"start": v(343.12, -72.17) * mm, "end": v(349.47, -72.17) * mm});
            skLineSegment(sketch, "E149.4.0.61", {"start": v(305.02, -84.87) * mm, "end": v(311.37, -84.87) * mm});
            skLineSegment(sketch, "E149.4.0.62", {"start": v(305.02, -34.07) * mm, "end": v(311.37, -34.07) * mm});
            skLineSegment(sketch, "E149.4.0.63", {"start": v(317.72, -46.77) * mm, "end": v(324.07, -46.77) * mm});
            skLineSegment(sketch, "E149.4.0.64", {"start": v(292.32, -34.07) * mm, "end": v(292.32, -40.42) * mm});
            skLineSegment(sketch, "E149.4.0.65", {"start": v(305.02, -46.77) * mm, "end": v(305.02, -53.12) * mm});
            skLineSegment(sketch, "E149.4.0.66", {"start": v(317.72, -59.47) * mm, "end": v(317.72, -65.82) * mm});
            skLineSegment(sketch, "E149.4.0.67", {"start": v(330.42, -72.17) * mm, "end": v(330.42, -78.52) * mm});
            skLineSegment(sketch, "E149.4.0.68", {"start": v(343.12, -84.87) * mm, "end": v(343.12, -91.22) * mm});
            skLineSegment(sketch, "E149.4.0.69", {"start": v(343.12, -34.07) * mm, "end": v(343.12, -40.42) * mm});
            skLineSegment(sketch, "E149.4.0.70", {"start": v(305.02, -91.22) * mm, "end": v(311.37, -91.22) * mm});
            skLineSegment(sketch, "E149.4.0.71", {"start": v(305.02, -40.42) * mm, "end": v(311.37, -40.42) * mm});
            skLineSegment(sketch, "E149.4.0.72", {"start": v(317.72, -53.12) * mm, "end": v(324.07, -53.12) * mm});
            skLineSegment(sketch, "E149.4.0.73", {"start": v(330.42, -65.82) * mm, "end": v(336.77, -65.82) * mm});
            skLineSegment(sketch, "E149.4.0.74", {"start": v(343.12, -78.52) * mm, "end": v(349.47, -78.52) * mm});
            skLineSegment(sketch, "E149.4.0.75", {"start": v(311.37, -84.87) * mm, "end": v(311.37, -91.22) * mm});
            skLineSegment(sketch, "E149.4.0.76", {"start": v(311.37, -34.07) * mm, "end": v(311.37, -40.42) * mm});
            skLineSegment(sketch, "E149.4.0.77", {"start": v(324.07, -46.77) * mm, "end": v(324.07, -53.12) * mm});
            skLineSegment(sketch, "E149.4.0.78", {"start": v(336.77, -59.47) * mm, "end": v(336.77, -65.82) * mm});
            skLineSegment(sketch, "E149.4.0.79", {"start": v(349.47, -72.17) * mm, "end": v(349.47, -78.52) * mm});
            skLineSegment(sketch, "E149.4.0.80", {"start": v(292.32, -72.17) * mm, "end": v(298.67, -72.17) * mm});
            skLineSegment(sketch, "E149.4.0.81", {"start": v(298.67, -84.87) * mm, "end": v(298.67, -91.22) * mm});
            skLineSegment(sketch, "E149.4.0.82", {"start": v(292.32, -78.52) * mm, "end": v(298.67, -78.52) * mm});
            skLineSegment(sketch, "E149.4.0.83", {"start": v(298.67, -72.17) * mm, "end": v(298.67, -78.52) * mm});
            skLineSegment(sketch, "E149.4.0.84", {"start": v(292.32, -84.87) * mm, "end": v(298.67, -84.87) * mm});
            skLineSegment(sketch, "E149.4.0.85", {"start": v(292.32, -59.47) * mm, "end": v(298.67, -59.47) * mm});
            skLineSegment(sketch, "E149.4.0.86", {"start": v(292.32, -72.17) * mm, "end": v(292.32, -78.52) * mm});
            skLineSegment(sketch, "E149.4.0.87", {"start": v(292.32, -65.82) * mm, "end": v(298.67, -65.82) * mm});
            skLineSegment(sketch, "E149.4.0.88", {"start": v(298.67, -59.47) * mm, "end": v(298.67, -65.82) * mm});
            skLineSegment(sketch, "E149.4.0.89", {"start": v(292.32, -59.47) * mm, "end": v(292.32, -65.82) * mm});
            skLineSegment(sketch, "E149.4.0.90", {"start": v(311.37, -59.47) * mm, "end": v(311.37, -65.82) * mm});
            skLineSegment(sketch, "E149.4.0.91", {"start": v(305.02, -59.47) * mm, "end": v(305.02, -65.82) * mm});
            skLineSegment(sketch, "E149.4.0.92", {"start": v(305.02, -65.82) * mm, "end": v(311.37, -65.82) * mm});
            skLineSegment(sketch, "E149.4.0.93", {"start": v(311.37, -72.17) * mm, "end": v(311.37, -78.52) * mm});
            skLineSegment(sketch, "E149.4.0.94", {"start": v(305.02, -72.17) * mm, "end": v(311.37, -72.17) * mm});
            skLineSegment(sketch, "E149.4.0.95", {"start": v(305.02, -72.17) * mm, "end": v(305.02, -78.52) * mm});
            skLineSegment(sketch, "E149.4.0.96", {"start": v(305.02, -78.52) * mm, "end": v(311.37, -78.52) * mm});
            skLineSegment(sketch, "E149.4.0.97", {"start": v(305.02, -59.47) * mm, "end": v(311.37, -59.47) * mm});
            skLineSegment(sketch, "E149.4.0.98", {"start": v(292.32, -91.22) * mm, "end": v(305.02, -91.22) * mm, "construction": true});
            skLineSegment(sketch, "E149.4.0.99", {"start": v(292.32, -91.22) * mm, "end": v(292.32, -78.52) * mm, "construction": true});
            skLineSegment(sketch, "E149.4.0.100", {"start": v(292.32, -84.87) * mm, "end": v(292.32, -91.22) * mm});
            skLineSegment(sketch, "E149.4.0.101", {"start": v(292.32, -91.22) * mm, "end": v(298.67, -91.22) * mm});
            skLineSegment(sketch, "E149.4.1.0", {"start": v(298.67, -300.77) * mm, "end": v(298.67, -307.12) * mm});
            skLineSegment(sketch, "E149.4.1.1", {"start": v(292.32, -300.77) * mm, "end": v(292.32, -307.12) * mm});
            skLineSegment(sketch, "E149.4.1.2", {"start": v(292.32, -307.12) * mm, "end": v(298.67, -307.12) * mm});
            skLineSegment(sketch, "E149.4.1.3", {"start": v(292.32, -300.77) * mm, "end": v(298.67, -300.77) * mm});
            skLineSegment(sketch, "E149.4.1.4", {"start": v(336.77, -338.87) * mm, "end": v(336.77, -345.22) * mm});
            skLineSegment(sketch, "E149.4.1.5", {"start": v(336.77, -288.07) * mm, "end": v(336.77, -294.42) * mm});
            skLineSegment(sketch, "E149.4.1.6", {"start": v(349.47, -300.77) * mm, "end": v(349.47, -307.12) * mm});
            skLineSegment(sketch, "E149.4.1.7", {"start": v(324.07, -326.17) * mm, "end": v(324.07, -332.52) * mm});
            skLineSegment(sketch, "E149.4.1.8", {"start": v(317.72, -326.17) * mm, "end": v(317.72, -332.52) * mm});
            skLineSegment(sketch, "E149.4.1.9", {"start": v(330.42, -338.87) * mm, "end": v(330.42, -345.22) * mm});
            skLineSegment(sketch, "E149.4.1.10", {"start": v(330.42, -288.07) * mm, "end": v(330.42, -294.42) * mm});
            skLineSegment(sketch, "E149.4.1.11", {"start": v(343.12, -300.77) * mm, "end": v(343.12, -307.12) * mm});
            skLineSegment(sketch, "E149.4.1.12", {"start": v(317.72, -332.52) * mm, "end": v(324.07, -332.52) * mm});
            skLineSegment(sketch, "E149.4.1.13", {"start": v(330.42, -345.22) * mm, "end": v(336.77, -345.22) * mm});
            skLineSegment(sketch, "E149.4.1.14", {"start": v(330.42, -294.42) * mm, "end": v(336.77, -294.42) * mm});
            skLineSegment(sketch, "E149.4.1.15", {"start": v(343.12, -307.12) * mm, "end": v(349.47, -307.12) * mm});
            skLineSegment(sketch, "E149.4.1.16", {"start": v(305.02, -338.87) * mm, "end": v(305.02, -345.22) * mm});
            skLineSegment(sketch, "E149.4.1.17", {"start": v(305.02, -288.07) * mm, "end": v(305.02, -294.42) * mm});
            skLineSegment(sketch, "E149.4.1.18", {"start": v(317.72, -300.77) * mm, "end": v(317.72, -307.12) * mm});
            skLineSegment(sketch, "E149.4.1.19", {"start": v(330.42, -313.47) * mm, "end": v(330.42, -319.82) * mm});
            skLineSegment(sketch, "E149.4.1.20", {"start": v(343.12, -326.17) * mm, "end": v(343.12, -332.52) * mm});
            skLineSegment(sketch, "E149.4.1.21", {"start": v(324.07, -338.87) * mm, "end": v(324.07, -345.22) * mm});
            skLineSegment(sketch, "E149.4.1.22", {"start": v(324.07, -288.07) * mm, "end": v(324.07, -294.42) * mm});
            skLineSegment(sketch, "E149.4.1.23", {"start": v(336.77, -300.77) * mm, "end": v(336.77, -307.12) * mm});
            skLineSegment(sketch, "E149.4.1.24", {"start": v(349.47, -313.47) * mm, "end": v(349.47, -319.82) * mm});
            skLineSegment(sketch, "E149.4.1.25", {"start": v(317.72, -338.87) * mm, "end": v(324.07, -338.87) * mm});
            skLineSegment(sketch, "E149.4.1.26", {"start": v(317.72, -288.07) * mm, "end": v(324.07, -288.07) * mm});
            skLineSegment(sketch, "E149.4.1.27", {"start": v(330.42, -300.77) * mm, "end": v(336.77, -300.77) * mm});
            skLineSegment(sketch, "E149.4.1.28", {"start": v(343.12, -313.47) * mm, "end": v(349.47, -313.47) * mm});
            skLineSegment(sketch, "E149.4.1.29", {"start": v(317.72, -338.87) * mm, "end": v(317.72, -345.22) * mm});
            skLineSegment(sketch, "E149.4.1.30", {"start": v(317.72, -288.07) * mm, "end": v(317.72, -294.42) * mm});
            skLineSegment(sketch, "E149.4.1.31", {"start": v(330.42, -300.77) * mm, "end": v(330.42, -307.12) * mm});
            skLineSegment(sketch, "E149.4.1.32", {"start": v(343.12, -313.47) * mm, "end": v(343.12, -319.82) * mm});
            skLineSegment(sketch, "E149.4.1.33", {"start": v(317.72, -345.22) * mm, "end": v(324.07, -345.22) * mm});
            skLineSegment(sketch, "E149.4.1.34", {"start": v(317.72, -294.42) * mm, "end": v(324.07, -294.42) * mm});
            skLineSegment(sketch, "E149.4.1.35", {"start": v(330.42, -307.12) * mm, "end": v(336.77, -307.12) * mm});
            skLineSegment(sketch, "E149.4.1.36", {"start": v(343.12, -319.82) * mm, "end": v(349.47, -319.82) * mm});
            skLineSegment(sketch, "E149.4.1.37", {"start": v(317.72, -326.17) * mm, "end": v(324.07, -326.17) * mm});
            skLineSegment(sketch, "E149.4.1.38", {"start": v(330.42, -338.87) * mm, "end": v(336.77, -338.87) * mm});
            skLineSegment(sketch, "E149.4.1.39", {"start": v(330.42, -288.07) * mm, "end": v(336.77, -288.07) * mm});
            skLineSegment(sketch, "E149.4.1.40", {"start": v(343.12, -300.77) * mm, "end": v(349.47, -300.77) * mm});
            skLineSegment(sketch, "E149.4.1.41", {"start": v(330.42, -326.17) * mm, "end": v(336.77, -326.17) * mm});
            skLineSegment(sketch, "E149.4.1.42", {"start": v(343.12, -338.87) * mm, "end": v(349.47, -338.87) * mm});
            skLineSegment(sketch, "E149.4.1.43", {"start": v(343.12, -288.07) * mm, "end": v(349.47, -288.07) * mm});
            skLineSegment(sketch, "E149.4.1.44", {"start": v(292.32, -288.07) * mm, "end": v(298.67, -288.07) * mm});
            skLineSegment(sketch, "E149.4.1.45", {"start": v(305.02, -300.77) * mm, "end": v(311.37, -300.77) * mm});
            skLineSegment(sketch, "E149.4.1.46", {"start": v(317.72, -313.47) * mm, "end": v(324.07, -313.47) * mm});
            skLineSegment(sketch, "E149.4.1.47", {"start": v(330.42, -332.52) * mm, "end": v(336.77, -332.52) * mm});
            skLineSegment(sketch, "E149.4.1.48", {"start": v(343.12, -345.22) * mm, "end": v(349.47, -345.22) * mm});
            skLineSegment(sketch, "E149.4.1.49", {"start": v(343.12, -294.42) * mm, "end": v(349.47, -294.42) * mm});
            skLineSegment(sketch, "E149.4.1.50", {"start": v(292.32, -294.42) * mm, "end": v(298.67, -294.42) * mm});
            skLineSegment(sketch, "E149.4.1.51", {"start": v(305.02, -307.12) * mm, "end": v(311.37, -307.12) * mm});
            skLineSegment(sketch, "E149.4.1.52", {"start": v(317.72, -319.82) * mm, "end": v(324.07, -319.82) * mm});
            skLineSegment(sketch, "E149.4.1.53", {"start": v(298.67, -288.07) * mm, "end": v(298.67, -294.42) * mm});
            skLineSegment(sketch, "E149.4.1.54", {"start": v(311.37, -300.77) * mm, "end": v(311.37, -307.12) * mm});
            skLineSegment(sketch, "E149.4.1.55", {"start": v(324.07, -313.47) * mm, "end": v(324.07, -319.82) * mm});
            skLineSegment(sketch, "E149.4.1.56", {"start": v(336.77, -326.17) * mm, "end": v(336.77, -332.52) * mm});
            skLineSegment(sketch, "E149.4.1.57", {"start": v(349.47, -338.87) * mm, "end": v(349.47, -345.22) * mm});
            skLineSegment(sketch, "E149.4.1.58", {"start": v(349.47, -288.07) * mm, "end": v(349.47, -294.42) * mm});
            skLineSegment(sketch, "E149.4.1.59", {"start": v(330.42, -313.47) * mm, "end": v(336.77, -313.47) * mm});
            skLineSegment(sketch, "E149.4.1.60", {"start": v(343.12, -326.17) * mm, "end": v(349.47, -326.17) * mm});
            skLineSegment(sketch, "E149.4.1.61", {"start": v(305.02, -338.87) * mm, "end": v(311.37, -338.87) * mm});
            skLineSegment(sketch, "E149.4.1.62", {"start": v(305.02, -288.07) * mm, "end": v(311.37, -288.07) * mm});
            skLineSegment(sketch, "E149.4.1.63", {"start": v(317.72, -300.77) * mm, "end": v(324.07, -300.77) * mm});
            skLineSegment(sketch, "E149.4.1.64", {"start": v(292.32, -288.07) * mm, "end": v(292.32, -294.42) * mm});
            skLineSegment(sketch, "E149.4.1.65", {"start": v(305.02, -300.77) * mm, "end": v(305.02, -307.12) * mm});
            skLineSegment(sketch, "E149.4.1.66", {"start": v(317.72, -313.47) * mm, "end": v(317.72, -319.82) * mm});
            skLineSegment(sketch, "E149.4.1.67", {"start": v(330.42, -326.17) * mm, "end": v(330.42, -332.52) * mm});
            skLineSegment(sketch, "E149.4.1.68", {"start": v(343.12, -338.87) * mm, "end": v(343.12, -345.22) * mm});
            skLineSegment(sketch, "E149.4.1.69", {"start": v(343.12, -288.07) * mm, "end": v(343.12, -294.42) * mm});
            skLineSegment(sketch, "E149.4.1.70", {"start": v(305.02, -345.22) * mm, "end": v(311.37, -345.22) * mm});
            skLineSegment(sketch, "E149.4.1.71", {"start": v(305.02, -294.42) * mm, "end": v(311.37, -294.42) * mm});
            skLineSegment(sketch, "E149.4.1.72", {"start": v(317.72, -307.12) * mm, "end": v(324.07, -307.12) * mm});
            skLineSegment(sketch, "E149.4.1.73", {"start": v(330.42, -319.82) * mm, "end": v(336.77, -319.82) * mm});
            skLineSegment(sketch, "E149.4.1.74", {"start": v(343.12, -332.52) * mm, "end": v(349.47, -332.52) * mm});
            skLineSegment(sketch, "E149.4.1.75", {"start": v(311.37, -338.87) * mm, "end": v(311.37, -345.22) * mm});
            skLineSegment(sketch, "E149.4.1.76", {"start": v(311.37, -288.07) * mm, "end": v(311.37, -294.42) * mm});
            skLineSegment(sketch, "E149.4.1.77", {"start": v(324.07, -300.77) * mm, "end": v(324.07, -307.12) * mm});
            skLineSegment(sketch, "E149.4.1.78", {"start": v(336.77, -313.47) * mm, "end": v(336.77, -319.82) * mm});
            skLineSegment(sketch, "E149.4.1.79", {"start": v(349.47, -326.17) * mm, "end": v(349.47, -332.52) * mm});
            skLineSegment(sketch, "E149.4.1.80", {"start": v(292.32, -326.17) * mm, "end": v(298.67, -326.17) * mm});
            skLineSegment(sketch, "E149.4.1.81", {"start": v(298.67, -338.87) * mm, "end": v(298.67, -345.22) * mm});
            skLineSegment(sketch, "E149.4.1.82", {"start": v(292.32, -332.52) * mm, "end": v(298.67, -332.52) * mm});
            skLineSegment(sketch, "E149.4.1.83", {"start": v(298.67, -326.17) * mm, "end": v(298.67, -332.52) * mm});
            skLineSegment(sketch, "E149.4.1.84", {"start": v(292.32, -338.87) * mm, "end": v(298.67, -338.87) * mm});
            skLineSegment(sketch, "E149.4.1.85", {"start": v(292.32, -313.47) * mm, "end": v(298.67, -313.47) * mm});
            skLineSegment(sketch, "E149.4.1.86", {"start": v(292.32, -326.17) * mm, "end": v(292.32, -332.52) * mm});
            skLineSegment(sketch, "E149.4.1.87", {"start": v(292.32, -319.82) * mm, "end": v(298.67, -319.82) * mm});
            skLineSegment(sketch, "E149.4.1.88", {"start": v(298.67, -313.47) * mm, "end": v(298.67, -319.82) * mm});
            skLineSegment(sketch, "E149.4.1.89", {"start": v(292.32, -313.47) * mm, "end": v(292.32, -319.82) * mm});
            skLineSegment(sketch, "E149.4.1.90", {"start": v(311.37, -313.47) * mm, "end": v(311.37, -319.82) * mm});
            skLineSegment(sketch, "E149.4.1.91", {"start": v(305.02, -313.47) * mm, "end": v(305.02, -319.82) * mm});
            skLineSegment(sketch, "E149.4.1.92", {"start": v(305.02, -319.82) * mm, "end": v(311.37, -319.82) * mm});
            skLineSegment(sketch, "E149.4.1.93", {"start": v(311.37, -326.17) * mm, "end": v(311.37, -332.52) * mm});
            skLineSegment(sketch, "E149.4.1.94", {"start": v(305.02, -326.17) * mm, "end": v(311.37, -326.17) * mm});
            skLineSegment(sketch, "E149.4.1.95", {"start": v(305.02, -326.17) * mm, "end": v(305.02, -332.52) * mm});
            skLineSegment(sketch, "E149.4.1.96", {"start": v(305.02, -332.52) * mm, "end": v(311.37, -332.52) * mm});
            skLineSegment(sketch, "E149.4.1.97", {"start": v(305.02, -313.47) * mm, "end": v(311.37, -313.47) * mm});
            skLineSegment(sketch, "E149.4.1.98", {"start": v(292.32, -345.22) * mm, "end": v(305.02, -345.22) * mm, "construction": true});
            skLineSegment(sketch, "E149.4.1.99", {"start": v(292.32, -345.22) * mm, "end": v(292.32, -332.52) * mm, "construction": true});
            skLineSegment(sketch, "E149.4.1.100", {"start": v(292.32, -338.87) * mm, "end": v(292.32, -345.22) * mm});
            skLineSegment(sketch, "E149.4.1.101", {"start": v(292.32, -345.22) * mm, "end": v(298.67, -345.22) * mm});
            skLineSegment(sketch, "E149.5.0.0", {"start": v(512.03, -46.77) * mm, "end": v(512.03, -53.12) * mm});
            skLineSegment(sketch, "E149.5.0.1", {"start": v(505.68, -46.77) * mm, "end": v(505.68, -53.12) * mm});
            skLineSegment(sketch, "E149.5.0.2", {"start": v(505.68, -53.12) * mm, "end": v(512.03, -53.12) * mm});
            skLineSegment(sketch, "E149.5.0.3", {"start": v(505.68, -46.77) * mm, "end": v(512.03, -46.77) * mm});
            skLineSegment(sketch, "E149.5.0.4", {"start": v(550.13, -84.87) * mm, "end": v(550.13, -91.22) * mm});
            skLineSegment(sketch, "E149.5.0.5", {"start": v(550.13, -34.07) * mm, "end": v(550.13, -40.42) * mm});
            skLineSegment(sketch, "E149.5.0.6", {"start": v(562.83, -46.77) * mm, "end": v(562.83, -53.12) * mm});
            skLineSegment(sketch, "E149.5.0.7", {"start": v(537.43, -72.17) * mm, "end": v(537.43, -78.52) * mm});
            skLineSegment(sketch, "E149.5.0.8", {"start": v(531.08, -72.17) * mm, "end": v(531.08, -78.52) * mm});
            skLineSegment(sketch, "E149.5.0.9", {"start": v(543.78, -84.87) * mm, "end": v(543.78, -91.22) * mm});
            skLineSegment(sketch, "E149.5.0.10", {"start": v(543.78, -34.07) * mm, "end": v(543.78, -40.42) * mm});
            skLineSegment(sketch, "E149.5.0.11", {"start": v(556.48, -46.77) * mm, "end": v(556.48, -53.12) * mm});
            skLineSegment(sketch, "E149.5.0.12", {"start": v(531.08, -78.52) * mm, "end": v(537.43, -78.52) * mm});
            skLineSegment(sketch, "E149.5.0.13", {"start": v(543.78, -91.22) * mm, "end": v(550.13, -91.22) * mm});
            skLineSegment(sketch, "E149.5.0.14", {"start": v(543.78, -40.42) * mm, "end": v(550.13, -40.42) * mm});
            skLineSegment(sketch, "E149.5.0.15", {"start": v(556.48, -53.12) * mm, "end": v(562.83, -53.12) * mm});
            skLineSegment(sketch, "E149.5.0.16", {"start": v(518.38, -84.87) * mm, "end": v(518.38, -91.22) * mm});
            skLineSegment(sketch, "E149.5.0.17", {"start": v(518.38, -34.07) * mm, "end": v(518.38, -40.42) * mm});
            skLineSegment(sketch, "E149.5.0.18", {"start": v(531.08, -46.77) * mm, "end": v(531.08, -53.12) * mm});
            skLineSegment(sketch, "E149.5.0.19", {"start": v(543.78, -59.47) * mm, "end": v(543.78, -65.82) * mm});
            skLineSegment(sketch, "E149.5.0.20", {"start": v(556.48, -72.17) * mm, "end": v(556.48, -78.52) * mm});
            skLineSegment(sketch, "E149.5.0.21", {"start": v(537.43, -84.87) * mm, "end": v(537.43, -91.22) * mm});
            skLineSegment(sketch, "E149.5.0.22", {"start": v(537.43, -34.07) * mm, "end": v(537.43, -40.42) * mm});
            skLineSegment(sketch, "E149.5.0.23", {"start": v(550.13, -46.77) * mm, "end": v(550.13, -53.12) * mm});
            skLineSegment(sketch, "E149.5.0.24", {"start": v(562.83, -59.47) * mm, "end": v(562.83, -65.82) * mm});
            skLineSegment(sketch, "E149.5.0.25", {"start": v(531.08, -84.87) * mm, "end": v(537.43, -84.87) * mm});
            skLineSegment(sketch, "E149.5.0.26", {"start": v(531.08, -34.07) * mm, "end": v(537.43, -34.07) * mm});
            skLineSegment(sketch, "E149.5.0.27", {"start": v(543.78, -46.77) * mm, "end": v(550.13, -46.77) * mm});
            skLineSegment(sketch, "E149.5.0.28", {"start": v(556.48, -59.47) * mm, "end": v(562.83, -59.47) * mm});
            skLineSegment(sketch, "E149.5.0.29", {"start": v(531.08, -84.87) * mm, "end": v(531.08, -91.22) * mm});
            skLineSegment(sketch, "E149.5.0.30", {"start": v(531.08, -34.07) * mm, "end": v(531.08, -40.42) * mm});
            skLineSegment(sketch, "E149.5.0.31", {"start": v(543.78, -46.77) * mm, "end": v(543.78, -53.12) * mm});
            skLineSegment(sketch, "E149.5.0.32", {"start": v(556.48, -59.47) * mm, "end": v(556.48, -65.82) * mm});
            skLineSegment(sketch, "E149.5.0.33", {"start": v(531.08, -91.22) * mm, "end": v(537.43, -91.22) * mm});
            skLineSegment(sketch, "E149.5.0.34", {"start": v(531.08, -40.42) * mm, "end": v(537.43, -40.42) * mm});
            skLineSegment(sketch, "E149.5.0.35", {"start": v(543.78, -53.12) * mm, "end": v(550.13, -53.12) * mm});
            skLineSegment(sketch, "E149.5.0.36", {"start": v(556.48, -65.82) * mm, "end": v(562.83, -65.82) * mm});
            skLineSegment(sketch, "E149.5.0.37", {"start": v(531.08, -72.17) * mm, "end": v(537.43, -72.17) * mm});
            skLineSegment(sketch, "E149.5.0.38", {"start": v(543.78, -84.87) * mm, "end": v(550.13, -84.87) * mm});
            skLineSegment(sketch, "E149.5.0.39", {"start": v(543.78, -34.07) * mm, "end": v(550.13, -34.07) * mm});
            skLineSegment(sketch, "E149.5.0.40", {"start": v(556.48, -46.77) * mm, "end": v(562.83, -46.77) * mm});
            skLineSegment(sketch, "E149.5.0.41", {"start": v(543.78, -72.17) * mm, "end": v(550.13, -72.17) * mm});
            skLineSegment(sketch, "E149.5.0.42", {"start": v(556.48, -84.87) * mm, "end": v(562.83, -84.87) * mm});
            skLineSegment(sketch, "E149.5.0.43", {"start": v(556.48, -34.07) * mm, "end": v(562.83, -34.07) * mm});
            skLineSegment(sketch, "E149.5.0.44", {"start": v(505.68, -34.07) * mm, "end": v(512.03, -34.07) * mm});
            skLineSegment(sketch, "E149.5.0.45", {"start": v(518.38, -46.77) * mm, "end": v(524.73, -46.77) * mm});
            skLineSegment(sketch, "E149.5.0.46", {"start": v(531.08, -59.47) * mm, "end": v(537.43, -59.47) * mm});
            skLineSegment(sketch, "E149.5.0.47", {"start": v(543.78, -78.52) * mm, "end": v(550.13, -78.52) * mm});
            skLineSegment(sketch, "E149.5.0.48", {"start": v(556.48, -91.22) * mm, "end": v(562.83, -91.22) * mm});
            skLineSegment(sketch, "E149.5.0.49", {"start": v(556.48, -40.42) * mm, "end": v(562.83, -40.42) * mm});
            skLineSegment(sketch, "E149.5.0.50", {"start": v(505.68, -40.42) * mm, "end": v(512.03, -40.42) * mm});
            skLineSegment(sketch, "E149.5.0.51", {"start": v(518.38, -53.12) * mm, "end": v(524.73, -53.12) * mm});
            skLineSegment(sketch, "E149.5.0.52", {"start": v(531.08, -65.82) * mm, "end": v(537.43, -65.82) * mm});
            skLineSegment(sketch, "E149.5.0.53", {"start": v(512.03, -34.07) * mm, "end": v(512.03, -40.42) * mm});
            skLineSegment(sketch, "E149.5.0.54", {"start": v(524.73, -46.77) * mm, "end": v(524.73, -53.12) * mm});
            skLineSegment(sketch, "E149.5.0.55", {"start": v(537.43, -59.47) * mm, "end": v(537.43, -65.82) * mm});
            skLineSegment(sketch, "E149.5.0.56", {"start": v(550.13, -72.17) * mm, "end": v(550.13, -78.52) * mm});
            skLineSegment(sketch, "E149.5.0.57", {"start": v(562.83, -84.87) * mm, "end": v(562.83, -91.22) * mm});
            skLineSegment(sketch, "E149.5.0.58", {"start": v(562.83, -34.07) * mm, "end": v(562.83, -40.42) * mm});
            skLineSegment(sketch, "E149.5.0.59", {"start": v(543.78, -59.47) * mm, "end": v(550.13, -59.47) * mm});
            skLineSegment(sketch, "E149.5.0.60", {"start": v(556.48, -72.17) * mm, "end": v(562.83, -72.17) * mm});
            skLineSegment(sketch, "E149.5.0.61", {"start": v(518.38, -84.87) * mm, "end": v(524.73, -84.87) * mm});
            skLineSegment(sketch, "E149.5.0.62", {"start": v(518.38, -34.07) * mm, "end": v(524.73, -34.07) * mm});
            skLineSegment(sketch, "E149.5.0.63", {"start": v(531.08, -46.77) * mm, "end": v(537.43, -46.77) * mm});
            skLineSegment(sketch, "E149.5.0.64", {"start": v(505.68, -34.07) * mm, "end": v(505.68, -40.42) * mm});
            skLineSegment(sketch, "E149.5.0.65", {"start": v(518.38, -46.77) * mm, "end": v(518.38, -53.12) * mm});
            skLineSegment(sketch, "E149.5.0.66", {"start": v(531.08, -59.47) * mm, "end": v(531.08, -65.82) * mm});
            skLineSegment(sketch, "E149.5.0.67", {"start": v(543.78, -72.17) * mm, "end": v(543.78, -78.52) * mm});
            skLineSegment(sketch, "E149.5.0.68", {"start": v(556.48, -84.87) * mm, "end": v(556.48, -91.22) * mm});
            skLineSegment(sketch, "E149.5.0.69", {"start": v(556.48, -34.07) * mm, "end": v(556.48, -40.42) * mm});
            skLineSegment(sketch, "E149.5.0.70", {"start": v(518.38, -91.22) * mm, "end": v(524.73, -91.22) * mm});
            skLineSegment(sketch, "E149.5.0.71", {"start": v(518.38, -40.42) * mm, "end": v(524.73, -40.42) * mm});
            skLineSegment(sketch, "E149.5.0.72", {"start": v(531.08, -53.12) * mm, "end": v(537.43, -53.12) * mm});
            skLineSegment(sketch, "E149.5.0.73", {"start": v(543.78, -65.82) * mm, "end": v(550.13, -65.82) * mm});
            skLineSegment(sketch, "E149.5.0.74", {"start": v(556.48, -78.52) * mm, "end": v(562.83, -78.52) * mm});
            skLineSegment(sketch, "E149.5.0.75", {"start": v(524.73, -84.87) * mm, "end": v(524.73, -91.22) * mm});
            skLineSegment(sketch, "E149.5.0.76", {"start": v(524.73, -34.07) * mm, "end": v(524.73, -40.42) * mm});
            skLineSegment(sketch, "E149.5.0.77", {"start": v(537.43, -46.77) * mm, "end": v(537.43, -53.12) * mm});
            skLineSegment(sketch, "E149.5.0.78", {"start": v(550.13, -59.47) * mm, "end": v(550.13, -65.82) * mm});
            skLineSegment(sketch, "E149.5.0.79", {"start": v(562.83, -72.17) * mm, "end": v(562.83, -78.52) * mm});
            skLineSegment(sketch, "E149.5.0.80", {"start": v(505.68, -72.17) * mm, "end": v(512.03, -72.17) * mm});
            skLineSegment(sketch, "E149.5.0.81", {"start": v(512.03, -84.87) * mm, "end": v(512.03, -91.22) * mm});
            skLineSegment(sketch, "E149.5.0.82", {"start": v(505.68, -78.52) * mm, "end": v(512.03, -78.52) * mm});
            skLineSegment(sketch, "E149.5.0.83", {"start": v(512.03, -72.17) * mm, "end": v(512.03, -78.52) * mm});
            skLineSegment(sketch, "E149.5.0.84", {"start": v(505.68, -84.87) * mm, "end": v(512.03, -84.87) * mm});
            skLineSegment(sketch, "E149.5.0.85", {"start": v(505.68, -59.47) * mm, "end": v(512.03, -59.47) * mm});
            skLineSegment(sketch, "E149.5.0.86", {"start": v(505.68, -72.17) * mm, "end": v(505.68, -78.52) * mm});
            skLineSegment(sketch, "E149.5.0.87", {"start": v(505.68, -65.82) * mm, "end": v(512.03, -65.82) * mm});
            skLineSegment(sketch, "E149.5.0.88", {"start": v(512.03, -59.47) * mm, "end": v(512.03, -65.82) * mm});
            skLineSegment(sketch, "E149.5.0.89", {"start": v(505.68, -59.47) * mm, "end": v(505.68, -65.82) * mm});
            skLineSegment(sketch, "E149.5.0.90", {"start": v(524.73, -59.47) * mm, "end": v(524.73, -65.82) * mm});
            skLineSegment(sketch, "E149.5.0.91", {"start": v(518.38, -59.47) * mm, "end": v(518.38, -65.82) * mm});
            skLineSegment(sketch, "E149.5.0.92", {"start": v(518.38, -65.82) * mm, "end": v(524.73, -65.82) * mm});
            skLineSegment(sketch, "E149.5.0.93", {"start": v(524.73, -72.17) * mm, "end": v(524.73, -78.52) * mm});
            skLineSegment(sketch, "E149.5.0.94", {"start": v(518.38, -72.17) * mm, "end": v(524.73, -72.17) * mm});
            skLineSegment(sketch, "E149.5.0.95", {"start": v(518.38, -72.17) * mm, "end": v(518.38, -78.52) * mm});
            skLineSegment(sketch, "E149.5.0.96", {"start": v(518.38, -78.52) * mm, "end": v(524.73, -78.52) * mm});
            skLineSegment(sketch, "E149.5.0.97", {"start": v(518.38, -59.47) * mm, "end": v(524.73, -59.47) * mm});
            skLineSegment(sketch, "E149.5.0.98", {"start": v(505.68, -91.22) * mm, "end": v(518.38, -91.22) * mm, "construction": true});
            skLineSegment(sketch, "E149.5.0.99", {"start": v(505.68, -91.22) * mm, "end": v(505.68, -78.52) * mm, "construction": true});
            skLineSegment(sketch, "E149.5.0.100", {"start": v(505.68, -84.87) * mm, "end": v(505.68, -91.22) * mm});
            skLineSegment(sketch, "E149.5.0.101", {"start": v(505.68, -91.22) * mm, "end": v(512.03, -91.22) * mm});
            skLineSegment(sketch, "E149.5.1.0", {"start": v(512.03, -300.77) * mm, "end": v(512.03, -307.12) * mm});
            skLineSegment(sketch, "E149.5.1.1", {"start": v(505.68, -300.77) * mm, "end": v(505.68, -307.12) * mm});
            skLineSegment(sketch, "E149.5.1.2", {"start": v(505.68, -307.12) * mm, "end": v(512.03, -307.12) * mm});
            skLineSegment(sketch, "E149.5.1.3", {"start": v(505.68, -300.77) * mm, "end": v(512.03, -300.77) * mm});
            skLineSegment(sketch, "E149.5.1.4", {"start": v(550.13, -338.87) * mm, "end": v(550.13, -345.22) * mm});
            skLineSegment(sketch, "E149.5.1.5", {"start": v(550.13, -288.07) * mm, "end": v(550.13, -294.42) * mm});
            skLineSegment(sketch, "E149.5.1.6", {"start": v(562.83, -300.77) * mm, "end": v(562.83, -307.12) * mm});
            skLineSegment(sketch, "E149.5.1.7", {"start": v(537.43, -326.17) * mm, "end": v(537.43, -332.52) * mm});
            skLineSegment(sketch, "E149.5.1.8", {"start": v(531.08, -326.17) * mm, "end": v(531.08, -332.52) * mm});
            skLineSegment(sketch, "E149.5.1.9", {"start": v(543.78, -338.87) * mm, "end": v(543.78, -345.22) * mm});
            skLineSegment(sketch, "E149.5.1.10", {"start": v(543.78, -288.07) * mm, "end": v(543.78, -294.42) * mm});
            skLineSegment(sketch, "E149.5.1.11", {"start": v(556.48, -300.77) * mm, "end": v(556.48, -307.12) * mm});
            skLineSegment(sketch, "E149.5.1.12", {"start": v(531.08, -332.52) * mm, "end": v(537.43, -332.52) * mm});
            skLineSegment(sketch, "E149.5.1.13", {"start": v(543.78, -345.22) * mm, "end": v(550.13, -345.22) * mm});
            skLineSegment(sketch, "E149.5.1.14", {"start": v(543.78, -294.42) * mm, "end": v(550.13, -294.42) * mm});
            skLineSegment(sketch, "E149.5.1.15", {"start": v(556.48, -307.12) * mm, "end": v(562.83, -307.12) * mm});
            skLineSegment(sketch, "E149.5.1.16", {"start": v(518.38, -338.87) * mm, "end": v(518.38, -345.22) * mm});
            skLineSegment(sketch, "E149.5.1.17", {"start": v(518.38, -288.07) * mm, "end": v(518.38, -294.42) * mm});
            skLineSegment(sketch, "E149.5.1.18", {"start": v(531.08, -300.77) * mm, "end": v(531.08, -307.12) * mm});
            skLineSegment(sketch, "E149.5.1.19", {"start": v(543.78, -313.47) * mm, "end": v(543.78, -319.82) * mm});
            skLineSegment(sketch, "E149.5.1.20", {"start": v(556.48, -326.17) * mm, "end": v(556.48, -332.52) * mm});
            skLineSegment(sketch, "E149.5.1.21", {"start": v(537.43, -338.87) * mm, "end": v(537.43, -345.22) * mm});
            skLineSegment(sketch, "E149.5.1.22", {"start": v(537.43, -288.07) * mm, "end": v(537.43, -294.42) * mm});
            skLineSegment(sketch, "E149.5.1.23", {"start": v(550.13, -300.77) * mm, "end": v(550.13, -307.12) * mm});
            skLineSegment(sketch, "E149.5.1.24", {"start": v(562.83, -313.47) * mm, "end": v(562.83, -319.82) * mm});
            skLineSegment(sketch, "E149.5.1.25", {"start": v(531.08, -338.87) * mm, "end": v(537.43, -338.87) * mm});
            skLineSegment(sketch, "E149.5.1.26", {"start": v(531.08, -288.07) * mm, "end": v(537.43, -288.07) * mm});
            skLineSegment(sketch, "E149.5.1.27", {"start": v(543.78, -300.77) * mm, "end": v(550.13, -300.77) * mm});
            skLineSegment(sketch, "E149.5.1.28", {"start": v(556.48, -313.47) * mm, "end": v(562.83, -313.47) * mm});
            skLineSegment(sketch, "E149.5.1.29", {"start": v(531.08, -338.87) * mm, "end": v(531.08, -345.22) * mm});
            skLineSegment(sketch, "E149.5.1.30", {"start": v(531.08, -288.07) * mm, "end": v(531.08, -294.42) * mm});
            skLineSegment(sketch, "E149.5.1.31", {"start": v(543.78, -300.77) * mm, "end": v(543.78, -307.12) * mm});
            skLineSegment(sketch, "E149.5.1.32", {"start": v(556.48, -313.47) * mm, "end": v(556.48, -319.82) * mm});
            skLineSegment(sketch, "E149.5.1.33", {"start": v(531.08, -345.22) * mm, "end": v(537.43, -345.22) * mm});
            skLineSegment(sketch, "E149.5.1.34", {"start": v(531.08, -294.42) * mm, "end": v(537.43, -294.42) * mm});
            skLineSegment(sketch, "E149.5.1.35", {"start": v(543.78, -307.12) * mm, "end": v(550.13, -307.12) * mm});
            skLineSegment(sketch, "E149.5.1.36", {"start": v(556.48, -319.82) * mm, "end": v(562.83, -319.82) * mm});
            skLineSegment(sketch, "E149.5.1.37", {"start": v(531.08, -326.17) * mm, "end": v(537.43, -326.17) * mm});
            skLineSegment(sketch, "E149.5.1.38", {"start": v(543.78, -338.87) * mm, "end": v(550.13, -338.87) * mm});
            skLineSegment(sketch, "E149.5.1.39", {"start": v(543.78, -288.07) * mm, "end": v(550.13, -288.07) * mm});
            skLineSegment(sketch, "E149.5.1.40", {"start": v(556.48, -300.77) * mm, "end": v(562.83, -300.77) * mm});
            skLineSegment(sketch, "E149.5.1.41", {"start": v(543.78, -326.17) * mm, "end": v(550.13, -326.17) * mm});
            skLineSegment(sketch, "E149.5.1.42", {"start": v(556.48, -338.87) * mm, "end": v(562.83, -338.87) * mm});
            skLineSegment(sketch, "E149.5.1.43", {"start": v(556.48, -288.07) * mm, "end": v(562.83, -288.07) * mm});
            skLineSegment(sketch, "E149.5.1.44", {"start": v(505.68, -288.07) * mm, "end": v(512.03, -288.07) * mm});
            skLineSegment(sketch, "E149.5.1.45", {"start": v(518.38, -300.77) * mm, "end": v(524.73, -300.77) * mm});
            skLineSegment(sketch, "E149.5.1.46", {"start": v(531.08, -313.47) * mm, "end": v(537.43, -313.47) * mm});
            skLineSegment(sketch, "E149.5.1.47", {"start": v(543.78, -332.52) * mm, "end": v(550.13, -332.52) * mm});
            skLineSegment(sketch, "E149.5.1.48", {"start": v(556.48, -345.22) * mm, "end": v(562.83, -345.22) * mm});
            skLineSegment(sketch, "E149.5.1.49", {"start": v(556.48, -294.42) * mm, "end": v(562.83, -294.42) * mm});
            skLineSegment(sketch, "E149.5.1.50", {"start": v(505.68, -294.42) * mm, "end": v(512.03, -294.42) * mm});
            skLineSegment(sketch, "E149.5.1.51", {"start": v(518.38, -307.12) * mm, "end": v(524.73, -307.12) * mm});
            skLineSegment(sketch, "E149.5.1.52", {"start": v(531.08, -319.82) * mm, "end": v(537.43, -319.82) * mm});
            skLineSegment(sketch, "E149.5.1.53", {"start": v(512.03, -288.07) * mm, "end": v(512.03, -294.42) * mm});
            skLineSegment(sketch, "E149.5.1.54", {"start": v(524.73, -300.77) * mm, "end": v(524.73, -307.12) * mm});
            skLineSegment(sketch, "E149.5.1.55", {"start": v(537.43, -313.47) * mm, "end": v(537.43, -319.82) * mm});
            skLineSegment(sketch, "E149.5.1.56", {"start": v(550.13, -326.17) * mm, "end": v(550.13, -332.52) * mm});
            skLineSegment(sketch, "E149.5.1.57", {"start": v(562.83, -338.87) * mm, "end": v(562.83, -345.22) * mm});
            skLineSegment(sketch, "E149.5.1.58", {"start": v(562.83, -288.07) * mm, "end": v(562.83, -294.42) * mm});
            skLineSegment(sketch, "E149.5.1.59", {"start": v(543.78, -313.47) * mm, "end": v(550.13, -313.47) * mm});
            skLineSegment(sketch, "E149.5.1.60", {"start": v(556.48, -326.17) * mm, "end": v(562.83, -326.17) * mm});
            skLineSegment(sketch, "E149.5.1.61", {"start": v(518.38, -338.87) * mm, "end": v(524.73, -338.87) * mm});
            skLineSegment(sketch, "E149.5.1.62", {"start": v(518.38, -288.07) * mm, "end": v(524.73, -288.07) * mm});
            skLineSegment(sketch, "E149.5.1.63", {"start": v(531.08, -300.77) * mm, "end": v(537.43, -300.77) * mm});
            skLineSegment(sketch, "E149.5.1.64", {"start": v(505.68, -288.07) * mm, "end": v(505.68, -294.42) * mm});
            skLineSegment(sketch, "E149.5.1.65", {"start": v(518.38, -300.77) * mm, "end": v(518.38, -307.12) * mm});
            skLineSegment(sketch, "E149.5.1.66", {"start": v(531.08, -313.47) * mm, "end": v(531.08, -319.82) * mm});
            skLineSegment(sketch, "E149.5.1.67", {"start": v(543.78, -326.17) * mm, "end": v(543.78, -332.52) * mm});
            skLineSegment(sketch, "E149.5.1.68", {"start": v(556.48, -338.87) * mm, "end": v(556.48, -345.22) * mm});
            skLineSegment(sketch, "E149.5.1.69", {"start": v(556.48, -288.07) * mm, "end": v(556.48, -294.42) * mm});
            skLineSegment(sketch, "E149.5.1.70", {"start": v(518.38, -345.22) * mm, "end": v(524.73, -345.22) * mm});
            skLineSegment(sketch, "E149.5.1.71", {"start": v(518.38, -294.42) * mm, "end": v(524.73, -294.42) * mm});
            skLineSegment(sketch, "E149.5.1.72", {"start": v(531.08, -307.12) * mm, "end": v(537.43, -307.12) * mm});
            skLineSegment(sketch, "E149.5.1.73", {"start": v(543.78, -319.82) * mm, "end": v(550.13, -319.82) * mm});
            skLineSegment(sketch, "E149.5.1.74", {"start": v(556.48, -332.52) * mm, "end": v(562.83, -332.52) * mm});
            skLineSegment(sketch, "E149.5.1.75", {"start": v(524.73, -338.87) * mm, "end": v(524.73, -345.22) * mm});
            skLineSegment(sketch, "E149.5.1.76", {"start": v(524.73, -288.07) * mm, "end": v(524.73, -294.42) * mm});
            skLineSegment(sketch, "E149.5.1.77", {"start": v(537.43, -300.77) * mm, "end": v(537.43, -307.12) * mm});
            skLineSegment(sketch, "E149.5.1.78", {"start": v(550.13, -313.47) * mm, "end": v(550.13, -319.82) * mm});
            skLineSegment(sketch, "E149.5.1.79", {"start": v(562.83, -326.17) * mm, "end": v(562.83, -332.52) * mm});
            skLineSegment(sketch, "E149.5.1.80", {"start": v(505.68, -326.17) * mm, "end": v(512.03, -326.17) * mm});
            skLineSegment(sketch, "E149.5.1.81", {"start": v(512.03, -338.87) * mm, "end": v(512.03, -345.22) * mm});
            skLineSegment(sketch, "E149.5.1.82", {"start": v(505.68, -332.52) * mm, "end": v(512.03, -332.52) * mm});
            skLineSegment(sketch, "E149.5.1.83", {"start": v(512.03, -326.17) * mm, "end": v(512.03, -332.52) * mm});
            skLineSegment(sketch, "E149.5.1.84", {"start": v(505.68, -338.87) * mm, "end": v(512.03, -338.87) * mm});
            skLineSegment(sketch, "E149.5.1.85", {"start": v(505.68, -313.47) * mm, "end": v(512.03, -313.47) * mm});
            skLineSegment(sketch, "E149.5.1.86", {"start": v(505.68, -326.17) * mm, "end": v(505.68, -332.52) * mm});
            skLineSegment(sketch, "E149.5.1.87", {"start": v(505.68, -319.82) * mm, "end": v(512.03, -319.82) * mm});
            skLineSegment(sketch, "E149.5.1.88", {"start": v(512.03, -313.47) * mm, "end": v(512.03, -319.82) * mm});
            skLineSegment(sketch, "E149.5.1.89", {"start": v(505.68, -313.47) * mm, "end": v(505.68, -319.82) * mm});
            skLineSegment(sketch, "E149.5.1.90", {"start": v(524.73, -313.47) * mm, "end": v(524.73, -319.82) * mm});
            skLineSegment(sketch, "E149.5.1.91", {"start": v(518.38, -313.47) * mm, "end": v(518.38, -319.82) * mm});
            skLineSegment(sketch, "E149.5.1.92", {"start": v(518.38, -319.82) * mm, "end": v(524.73, -319.82) * mm});
            skLineSegment(sketch, "E149.5.1.93", {"start": v(524.73, -326.17) * mm, "end": v(524.73, -332.52) * mm});
            skLineSegment(sketch, "E149.5.1.94", {"start": v(518.38, -326.17) * mm, "end": v(524.73, -326.17) * mm});
            skLineSegment(sketch, "E149.5.1.95", {"start": v(518.38, -326.17) * mm, "end": v(518.38, -332.52) * mm});
            skLineSegment(sketch, "E149.5.1.96", {"start": v(518.38, -332.52) * mm, "end": v(524.73, -332.52) * mm});
            skLineSegment(sketch, "E149.5.1.97", {"start": v(518.38, -313.47) * mm, "end": v(524.73, -313.47) * mm});
            skLineSegment(sketch, "E149.5.1.98", {"start": v(505.68, -345.22) * mm, "end": v(518.38, -345.22) * mm, "construction": true});
            skLineSegment(sketch, "E149.5.1.99", {"start": v(505.68, -345.22) * mm, "end": v(505.68, -332.52) * mm, "construction": true});
            skLineSegment(sketch, "E149.5.1.100", {"start": v(505.68, -338.87) * mm, "end": v(505.68, -345.22) * mm});
            skLineSegment(sketch, "E149.5.1.101", {"start": v(505.68, -345.22) * mm, "end": v(512.03, -345.22) * mm});
            skLineSegment(sketch, "E149.direction1", {"start": v(-561.12, -91.22) * mm, "end": v(-347.76, -91.22) * mm, "construction": true});
            skLineSegment(sketch, "E149.direction2", {"start": v(-561.12, -91.22) * mm, "end": v(-561.12, -345.22) * mm, "construction": true});
            skSolve(sketch);
        }
        {
            var Q0;
            Q0 = qSketchRegion(id + "F14", true);
            extrude(context, id + "F15", {"entities" : qUnion([Q0]), "operationType" : NewBodyOperationType.REMOVE, "endBound" : BoundingType.THROUGH_ALL, "oppositeDirection" : true, "depth" : 25.4 * mm});
        }
        {
            var Q0;
            Q0 = qSketchRegion(id + "F4", true);
            extrude(context, id + "F16", {"entities" : qUnion([Q0]), "operationType" : NewBodyOperationType.REMOVE, "endBound" : BoundingType.THROUGH_ALL, "oppositeDirection" : true, "depth" : 25.4 * mm});
        }
    });
